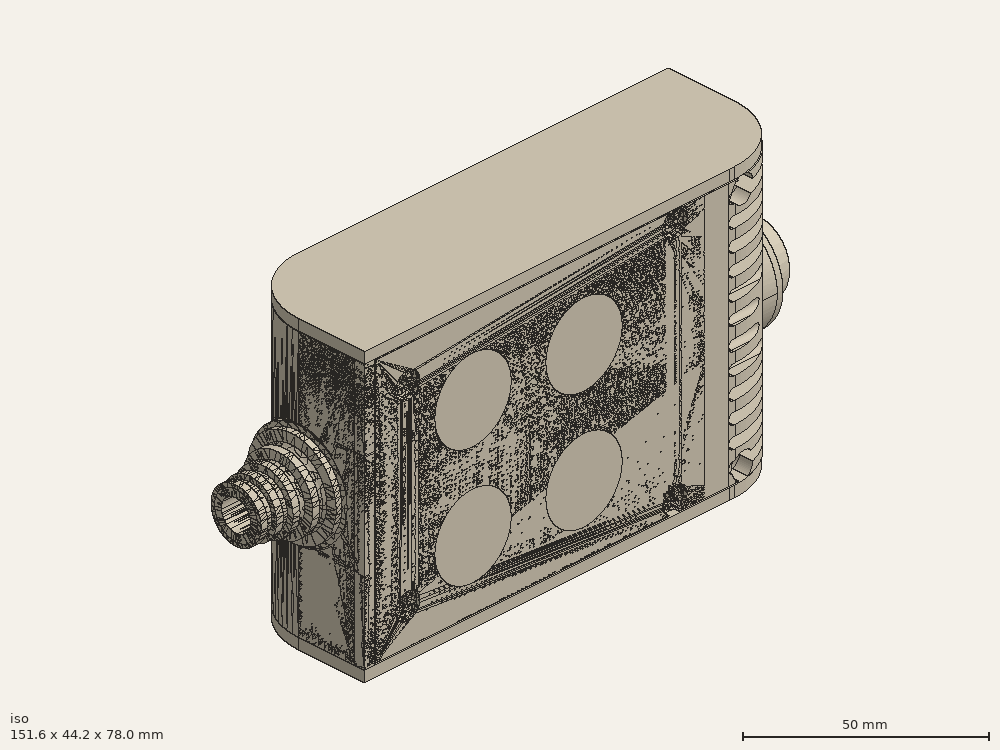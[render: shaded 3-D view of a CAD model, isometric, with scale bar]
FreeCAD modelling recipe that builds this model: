
FCSTD DOCUMENT  (FreeCAD 0.19R0.19.2)
Label: enclosure_204FCStd
License: All rights reserved
LicenseURL: http://en.wikipedia.org/wiki/All_rights_reserved
objects: Part::Revolution×152, Part::MultiFuse×146, Part::Feature×146, Sketcher::SketchObject×83, Part::Cut×70, Part::Cylinder×70, Part::Extrusion×68, Part::Fillet×58, Part::Box×36, App::MeasureDistance×4, Image::ImagePlane×1, PartDesign::Body×1, Part::FeaturePython×1
note: 831 computed .brp shape members not serialized (recipe doc carries the construction recipe); baked Part::Feature solids carry a one-line shape summary decoded from their .brp

FEATURE [Sketcher::SketchObject] Sketch  label="topSketch"
  FullyConstrained = true
  sketch-geometry (20):
    g0: LineSegment StartX=5.21097e-06 StartY=3 StartZ=0 EndX=5.21097e-06 EndY=19 EndZ=0
    g1: ArcOfCircle CenterX=19 CenterY=19 CenterZ=0 NormalX=0 NormalY=0 NormalZ=1 AngleXU=0 Radius=19 StartAngle=1.5708 EndAngle=3.14159
    g2: ArcOfCircle CenterX=19 CenterY=19 CenterZ=0 NormalX=0 NormalY=0 NormalZ=1 AngleXU=0 Radius=16 StartAngle=1.5708 EndAngle=3.14159
    g3: LineSegment StartX=114 StartY=35 StartZ=0 EndX=19 EndY=35 EndZ=0
    g4: LineSegment StartX=5.21097e-06 StartY=3 StartZ=0 EndX=5.21097e-06 EndY=0 EndZ=0
    g5: LineSegment StartX=3 StartY=0 StartZ=0 EndX=5.21097e-06 EndY=0 EndZ=0
    g6: LineSegment StartX=3 StartY=19 StartZ=0 EndX=3 EndY=0 EndZ=0
    g7: LineSegment StartX=19 StartY=38 StartZ=0 EndX=124 EndY=38 EndZ=0
    g8: Circle CenterX=119 CenterY=35 CenterZ=0 NormalX=0 NormalY=0 NormalZ=1 AngleXU=0 Radius=1
    g9: Circle CenterX=121 CenterY=35 CenterZ=0 NormalX=0 NormalY=0 NormalZ=1 AngleXU=0 Radius=1
    g10: Circle CenterX=121 CenterY=33 CenterZ=0 NormalX=0 NormalY=0 NormalZ=1 AngleXU=0 Radius=1
    g11: BSplineCurve PolesCount=3 KnotsCount=2 Degree=2 IsPeriodic=0
    g12: GeomPoint X=119 Y=35 Z=0
    g13: GeomPoint X=121 Y=33 Z=0
    g14: LineSegment StartX=119 StartY=35 StartZ=0 EndX=114 EndY=35 EndZ=0
    g15: ArcOfCircle CenterX=105 CenterY=19 CenterZ=0 NormalX=0 NormalY=0 NormalZ=1 AngleXU=0 Radius=19 StartAngle=5.7297 EndAngle=6.28319
    g16: ArcOfCircle CenterX=105 CenterY=19 CenterZ=0 NormalX=0 NormalY=0 NormalZ=1 AngleXU=0 Radius=16 StartAngle=5.60905 EndAngle=6.28319
    g17: LineSegment StartX=121 StartY=33 StartZ=0 EndX=121 EndY=19 EndZ=0
    g18: LineSegment StartX=124 StartY=38 StartZ=0 EndX=124 EndY=19 EndZ=0
    g19: LineSegment StartX=117.5 StartY=9.01251 StartZ=0 EndX=121.163 EndY=9.0125 EndZ=0
  constraints (46):
    c: Vertical(g0)
    c: Block(g0)
    c: Coincident(g1,g0)
    c: Block(g1)
    c: Coincident(g2,g1)
    c: Block(g2)
    c: Coincident(g3,g2)
    c: Horizontal(g3)
    c: Tangent(g3,g2)
    c: Coincident(g4,g0)
    c: Distance(g4) = 3
    c: Vertical(g4)
    c: Coincident(g5,g4)
    c: Horizontal(g5)
    c: Coincident(g6,g2)
    c: Coincident(g6,g5)
    c: Vertical(g6)
    c: Horizontal(g7)
    c: Distance(g7) = 105
    c: Coincident(g7,g1)
    c: Block(g3)
    c: Weight(g8) = 1
    c: Equal(g8,g9)
    c: Equal(g8,g10)
    c: InternalAlignment(g8,g11)
    c: InternalAlignment(g9,g11)
    c: InternalAlignment(g10,g11)
    c: InternalAlignment(g12,g11)
    c: InternalAlignment(g13,g11)
    c: Block(g11)
    c: Coincident(g14,g11)
    c: Coincident(g14,g3)
    c: Horizontal(g14)
    c: Block(g15)
    c: Coincident(g16,g15)
    c: Block(g16)
    c: Coincident(g17,g11)
    c: Coincident(g17,g16)
    c: Vertical(g17)
    c: Distance(g17) = 14
    c: Coincident(g18,g7)
    c: Coincident(g18,g15)
    c: Vertical(g18)
    c: Distance(g18) = 19
    c: Coincident(g19,g16)
    c: Coincident(g19,g15)
FEATURE [Sketcher::SketchObject] Sketch001  label="bottomSketch"
  FullyConstrained = true
  sketch-geometry (32):
    g0: LineSegment StartX=3.3 StartY=-6.03275e-07 StartZ=0 EndX=98 EndY=-6.03275e-07 EndZ=0
    g1: ArcOfCircle CenterX=98 CenterY=19 CenterZ=0 NormalX=0 NormalY=0 NormalZ=1 AngleXU=0 Radius=19 StartAngle=4.71239 EndAngle=5.71103
    g2: LineSegment StartX=6.3 StartY=8 StartZ=0 EndX=3.3 EndY=8 EndZ=0
    g3: LineSegment StartX=3.3 StartY=8 StartZ=0 EndX=3.3 EndY=-6.03275e-07 EndZ=0
    g4: ArcOfCircle CenterX=8.3 CenterY=5 CenterZ=0 NormalX=0 NormalY=0 NormalZ=1 AngleXU=0 Radius=2 StartAngle=3.14159 EndAngle=4.71239
    g5: LineSegment StartX=6.3 StartY=8 StartZ=0 EndX=6.3 EndY=5 EndZ=0
    g6: ArcOfCircle CenterX=98 CenterY=19 CenterZ=0 NormalX=0 NormalY=0 NormalZ=1 AngleXU=0 Radius=12.7 StartAngle=4.71239 EndAngle=6.28319
    g7: LineSegment StartX=94.7 StartY=3 StartZ=0 EndX=8.3 EndY=3 EndZ=0
    g8-g12: Circle x5 (B-spline internal-alignment scaffolding for g13; pole/knot coordinates omitted)
    g13: BSplineCurve PolesCount=5 KnotsCount=3 Degree=3 IsPeriodic=0
    g14: GeomPoint X=98 Y=6.3 Z=0
    g15: GeomPoint X=96.3938 Y=4.71946 Z=0
    g16: GeomPoint X=94.7 Y=3 Z=0
    g17-g23: Circle x7 (B-spline internal-alignment scaffolding for g24; pole/knot coordinates omitted)
    g24: BSplineCurve PolesCount=7 KnotsCount=5 Degree=3 IsPeriodic=0
    g25-g29: GeomPoint x5 (B-spline internal-alignment scaffolding for g24; pole/knot coordinates omitted)
    g30: ArcOfCircle CenterX=98 CenterY=19 CenterZ=0 NormalX=0 NormalY=0 NormalZ=1 AngleXU=0 Radius=15.7 StartAngle=5.81226 EndAngle=6.28319
    g31: LineSegment StartX=110.7 StartY=19 StartZ=0 EndX=113.7 EndY=19 EndZ=0
  constraints (41):
    c: Horizontal(g0)
    c: Coincident(g1,g0)
    c: Block(g1)
    c: Horizontal(g2)
    c: Distance(g2) = 3
    c: Coincident(g3,g2)
    c: Vertical(g3)
    c: Coincident(g3,g0)
    c: Block(g4)
    c: Block(g2)
    c: Coincident(g5,g2)
    c: Coincident(g5,g4)
    c: Vertical(g5)
    c: Coincident(g6,g1)
    c: Block(g6)
    c: Coincident(g7,g4)
    c: Horizontal(g7)
    c: Block(g0)
    c: Block(g7)
    c: Block(g3)
    c: Coincident(g13,g6)
    c: Weight(g8) = 1
    c: Equal(g8, g9-g12) x4
    c: Coincident(g13,g7)
    c: InternalAlignment(g8-g12 -> g13) x5
    c: InternalAlignment(g14,g13)
    c: InternalAlignment(g15,g13)
    c: InternalAlignment(g16,g13)
    c: Block(g13)
    c: Weight(g17) = 1
    c: Equal(g17, g18-g23) x6
    c: Coincident(g24,g1)
    c: InternalAlignment(g17-g23 -> g24) x7
    c: InternalAlignment(g25-g29 -> g24) x5
    c: Block(g24)
    c: Coincident(g30,g24)
    c: Coincident(g31,g6)
    c: Coincident(g31,g30)
    c: Horizontal(g31)
    c: Block(g31)
    c: Block(g30)
FEATURE [Part::Extrusion] Extrude  label="top"
  Base = -> Sketch
  Dir = (0,0,1)
  DirMode = 2
  FaceMakerClass = Part::FaceMakerBullseye
  LengthFwd = 72
  LengthRev = 0
  Solid = true
  Symmetric = false
FEATURE [Part::Extrusion] Extrude001  label="bottom"
  Base = -> Sketch001
  Dir = (0,0,1)
  DirMode = 2
  FaceMakerClass = Part::FaceMakerBullseye
  LengthFwd = 71.4
  LengthRev = 0
  Placement = pos=(0,0,0.3) rot=(0,0,1;0rad)
  Solid = true
  Symmetric = false
FEATURE [Sketcher::SketchObject] Sketch002  label="topSketch001"
  FullyConstrained = true
  sketch-geometry (8):
    g0: ArcOfCircle CenterX=19 CenterY=19.0975 CenterZ=0 NormalX=0 NormalY=0 NormalZ=1 AngleXU=0 Radius=18.9025 StartAngle=1.5708 EndAngle=3.14674
    g1: LineSegment StartX=0.0977805 StartY=19.0003 StartZ=0 EndX=0.0977805 EndY=0.000251602 EndZ=0
    g2: LineSegment StartX=19 StartY=38 StartZ=0 EndX=124 EndY=38 EndZ=0
    g3: LineSegment StartX=0.0977805 StartY=0.000251602 StartZ=0 EndX=105.098 EndY=0.000251602 EndZ=0
    g4: LineSegment StartX=124 StartY=38 StartZ=0 EndX=125.616 EndY=38 EndZ=0
    g5: LineSegment StartX=105.098 StartY=0.000251602 StartZ=0 EndX=106.713 EndY=0.000251602 EndZ=0
    g6: ArcOfCircle CenterX=106.616 CenterY=19 CenterZ=0 NormalX=0 NormalY=0 NormalZ=1 AngleXU=0 Radius=19 StartAngle=4.71754 EndAngle=6.28319
    g7: LineSegment StartX=125.616 StartY=38 StartZ=0 EndX=125.616 EndY=19 EndZ=0
  constraints (21):
    c: Block(g0)
    c: Coincident(g1,g0)
    c: Vertical(g1)
    c: Horizontal(g2)
    c: Distance(g2) = 105
    c: Coincident(g2,g0)
    c: Distance(g1) = 19
    c: Coincident(g3,g1)
    c: Horizontal(g3)
    c: Distance(g3) = 105
    c: Coincident(g4,g2)
    c: Horizontal(g4)
    c: Distance(g4) = 1.61553
    c: Horizontal(g5)
    c: Equal(g4,g5) = 1.61553
    c: Coincident(g5,g3)
    c: Block(g6)
    c: Coincident(g6,g5)
    c: Coincident(g7,g4)
    c: Coincident(g7,g6)
    c: Vertical(g7)
FEATURE [Part::Extrusion] Extrude002  label="sideA"
  Base = -> Sketch002
  Dir = (0,0,1)
  DirMode = 2
  FaceMakerClass = Part::FaceMakerBullseye
  LengthFwd = 3
  LengthRev = 0
  Placement = pos=(0,0,-3) rot=(0,0,1;0rad)
  Solid = true
  Symmetric = false
FEATURE [Sketcher::SketchObject] Sketch003  label="topSketch002"
  FullyConstrained = true
  sketch-geometry (6):
    g0: LineSegment StartX=19 StartY=38 StartZ=0 EndX=117 EndY=38 EndZ=0
    g1: ArcOfCircle CenterX=19 CenterY=19 CenterZ=0 NormalX=0 NormalY=0 NormalZ=1 AngleXU=0 Radius=19 StartAngle=1.5708 EndAngle=3.14159
    g2: LineSegment StartX=117 StartY=38 StartZ=0 EndX=117 EndY=19 EndZ=0
    g3: LineSegment StartX=98 StartY=1.0161e-12 StartZ=0 EndX=5.22862e-06 EndY=1.0161e-12 EndZ=0
    g4: LineSegment StartX=5.22862e-06 StartY=19 StartZ=0 EndX=5.22862e-06 EndY=1.0161e-12 EndZ=0
    g5: ArcOfCircle CenterX=98 CenterY=19 CenterZ=0 NormalX=0 NormalY=0 NormalZ=1 AngleXU=0 Radius=19 StartAngle=4.71239 EndAngle=6.28319
  constraints (16):
    c: Horizontal(g0)
    c: Distance(g0) = 98
    c: Coincident(g1,g0)
    c: Block(g1)
    c: Coincident(g2,g0)
    c: Vertical(g2)
    c: Distance(g2) = 19
    c: Horizontal(g3)
    c: Coincident(g4,g1)
    c: Vertical(g4)
    c: Coincident(g3,g4)
    c: Block(g3)
    c: Coincident(g5,g2)
    c: Coincident(g5,g3)
    c: Block(g0)
    c: Block(g5)
FEATURE [Sketcher::SketchObject] Sketch004
  FullyConstrained = true
  MapMode = 3
  Placement = pos=(0,0,0) rot=(1,0,0;1.5708rad)
  Support = -> [Extrude]
  sketch-geometry (8):
    g0: Circle CenterX=80.351 CenterY=-67.6202 CenterZ=0 NormalX=0 NormalY=0 NormalZ=1 AngleXU=0 Radius=2
    g1: Circle CenterX=80.351 CenterY=-67.6202 CenterZ=0 NormalX=0 NormalY=0 NormalZ=1 AngleXU=0 Radius=3
    g2: Circle CenterX=80.351 CenterY=-4.92017 CenterZ=0 NormalX=0 NormalY=0 NormalZ=1 AngleXU=0 Radius=2
    g3: Circle CenterX=80.351 CenterY=-4.92017 CenterZ=0 NormalX=0 NormalY=0 NormalZ=1 AngleXU=0 Radius=3
    g4: Circle CenterX=23.851 CenterY=-4.92017 CenterZ=0 NormalX=0 NormalY=0 NormalZ=1 AngleXU=0 Radius=2
    g5: Circle CenterX=23.851 CenterY=-4.92017 CenterZ=0 NormalX=0 NormalY=0 NormalZ=1 AngleXU=0 Radius=3
    g6: Circle CenterX=23.851 CenterY=-67.6202 CenterZ=0 NormalX=0 NormalY=0 NormalZ=1 AngleXU=0 Radius=2
    g7: Circle CenterX=23.851 CenterY=-67.6202 CenterZ=0 NormalX=0 NormalY=0 NormalZ=1 AngleXU=0 Radius=3
  constraints (8):
    c: Block(g3)
    c: Block(g2)
    c: Block(g1)
    c: Block(g0)
    c: Block(g6)
    c: Block(g7)
    c: Block(g4)
    c: Block(g5)
FEATURE [Part::Extrusion] Extrude004
  Base = -> Sketch004
  Dir = (0,-1,2e-16)
  DirMode = 2
  FaceMakerClass = Part::FaceMakerBullseye
  LengthFwd = 6
  LengthRev = 0
  Placement = pos=(0,9,0) rot=(0,0,1;0rad)
  Solid = true
  Symmetric = false
FEATURE [Sketcher::SketchObject] Sketch005
  FullyConstrained = true
  MapMode = 3
  Placement = pos=(0,0,0) rot=(1,0,0;1.5708rad)
  Support = -> [Extrude]
  sketch-geometry (8):
    g0: Circle CenterX=80.351 CenterY=-67.6202 CenterZ=0 NormalX=0 NormalY=0 NormalZ=1 AngleXU=0 Radius=3
    g1: Circle CenterX=80.351 CenterY=-4.92017 CenterZ=0 NormalX=0 NormalY=0 NormalZ=1 AngleXU=0 Radius=3
    g2: Circle CenterX=23.851 CenterY=-4.92017 CenterZ=0 NormalX=0 NormalY=0 NormalZ=1 AngleXU=0 Radius=3
    g3: Circle CenterX=23.851 CenterY=-67.6202 CenterZ=0 NormalX=0 NormalY=0 NormalZ=1 AngleXU=0 Radius=3
    g4: Circle CenterX=23.851 CenterY=-67.6202 CenterZ=0 NormalX=0 NormalY=0 NormalZ=1 AngleXU=0 Radius=5
    g5: Circle CenterX=80.351 CenterY=-67.6202 CenterZ=0 NormalX=0 NormalY=0 NormalZ=1 AngleXU=0 Radius=5
    g6: Circle CenterX=23.851 CenterY=-4.92017 CenterZ=0 NormalX=0 NormalY=0 NormalZ=1 AngleXU=0 Radius=5
    g7: Circle CenterX=80.351 CenterY=-4.92017 CenterZ=0 NormalX=0 NormalY=0 NormalZ=1 AngleXU=0 Radius=5
  constraints (8):
    c: Block(g1)
    c: Block(g0)
    c: Block(g3)
    c: Block(g2)
    c: Block(g5)
    c: Block(g4)
    c: Block(g6)
    c: Block(g7)
FEATURE [Part::Extrusion] Extrude005
  Base = -> Sketch005
  Dir = (0,-1,2e-16)
  DirMode = 2
  FaceMakerClass = Part::FaceMakerBullseye
  LengthFwd = 2
  LengthRev = 0
  Solid = true
  Symmetric = false
FEATURE [Sketcher::SketchObject] Sketch006
  FullyConstrained = true
  MapMode = 3
  Placement = pos=(0,0,0) rot=(1,0,0;1.5708rad)
  sketch-geometry (8):
    g0: Circle CenterX=80.351 CenterY=-67.6202 CenterZ=0 NormalX=0 NormalY=0 NormalZ=1 AngleXU=0 Radius=3
    g1: Circle CenterX=80.351 CenterY=-4.92017 CenterZ=0 NormalX=0 NormalY=0 NormalZ=1 AngleXU=0 Radius=3
    g2: Circle CenterX=23.851 CenterY=-4.92017 CenterZ=0 NormalX=0 NormalY=0 NormalZ=1 AngleXU=0 Radius=3
    g3: Circle CenterX=23.851 CenterY=-67.6202 CenterZ=0 NormalX=0 NormalY=0 NormalZ=1 AngleXU=0 Radius=3
    g4: Circle CenterX=23.851 CenterY=-67.6202 CenterZ=0 NormalX=0 NormalY=0 NormalZ=1 AngleXU=0 Radius=5
    g5: Circle CenterX=80.351 CenterY=-67.6202 CenterZ=0 NormalX=0 NormalY=0 NormalZ=1 AngleXU=0 Radius=5
    g6: Circle CenterX=23.851 CenterY=-4.92017 CenterZ=0 NormalX=0 NormalY=0 NormalZ=1 AngleXU=0 Radius=5
    g7: Circle CenterX=80.351 CenterY=-4.92017 CenterZ=0 NormalX=0 NormalY=0 NormalZ=1 AngleXU=0 Radius=5
  constraints (8):
    c: Block(g1)
    c: Block(g0)
    c: Block(g3)
    c: Block(g2)
    c: Block(g5)
    c: Block(g4)
    c: Block(g6)
    c: Block(g7)
FEATURE [Part::Extrusion] Extrude007
  Base = -> Sketch006
  Dir = (0,-1,2e-16)
  DirMode = 2
  FaceMakerClass = Part::FaceMakerBullseye
  LengthFwd = 2
  LengthRev = 0
  Solid = true
  Symmetric = false
FEATURE [Part::Fillet] Fillet
  Base = -> Extrude007
  Edges = 4 edges r=1.99: [Edge6,Edge12,Edge18,Edge24]
FEATURE [Part::Cut] Cut
  Base = -> Extrude005
  Placement = pos=(0,5,0) rot=(0,0,1;0rad)
  Tool = -> Fillet
FEATURE [Part::MultiFuse] Fusion  label="pCBScrews"
  Placement = pos=(-2.5,0,72.3) rot=(0,0,1;0rad)
  Shapes = -> [Extrude004,Cut]
FEATURE [App::MeasureDistance] Distance  label="Distance: 0.69 mm"
  Distance = 0.685967
  P1 = (24.0138,2.9647,0.3)
  P2 = (23.8901,3,-0.373787)
FEATURE [App::MeasureDistance] Distance001  label="Distance: 0.53 mm"
  Distance = 0.533607
  P1 = (80.2939,3,72.2334)
  P2 = (80.281,2.99661,71.7)
FEATURE [Part::Fillet] Fillet001
  Base = -> Extrude001
  Edges = 1 edges r=2.4: [Edge17]
FEATURE [Part::Fillet] Fillet002  label="bottom001"
  Base = -> Fillet001
  Edges = 1 edges r=2.4: [Edge36]
FEATURE [Part::Fillet] Fillet003  label="top001"
  Base = -> Extrude
  Edges = 1 edges r=2: [Edge1]
FEATURE [Sketcher::SketchObject] Sketch007
  FullyConstrained = true
  sketch-geometry (16):
    g0: LineSegment StartX=4 StartY=0 StartZ=0 EndX=4 EndY=2.4 EndZ=0
    g1: LineSegment StartX=4 StartY=2.4 StartZ=0 EndX=7 EndY=2.4 EndZ=0
    g2: LineSegment StartX=4 StartY=0 StartZ=0 EndX=5.7 EndY=0 EndZ=0
    g3: LineSegment StartX=5.7 StartY=0 StartZ=0 EndX=5.7 EndY=-5.6 EndZ=0
    g4-g8: Circle x5 (B-spline internal-alignment scaffolding for g9; pole/knot coordinates omitted)
    g9: BSplineCurve PolesCount=5 KnotsCount=3 Degree=3 IsPeriodic=0
    g10: GeomPoint X=7 Y=2.4 Z=0
    g11: GeomPoint X=10.4582 Y=-1.55472 Z=0
    g12: GeomPoint X=14 Y=-5.6 Z=0
    g13: LineSegment StartX=14 StartY=-5.6 StartZ=0 EndX=14 EndY=-14.1 EndZ=0
    g14: LineSegment StartX=14 StartY=-14.1 StartZ=0 EndX=6.5 EndY=-14.1 EndZ=0
    g15: LineSegment StartX=5.7 StartY=-5.6 StartZ=0 EndX=6.5 EndY=-14.1 EndZ=0
  constraints (28):
    c: Distance(g0) = 2.4
    c: Vertical(g0)
    c: Block(g0)
    c: Coincident(g1,g0)
    c: Horizontal(g1)
    c: Distance(g1) = 3
    c: Coincident(g2,g0)
    c: Horizontal(g2)
    c: Distance(g2) = 1.7
    c: Coincident(g3,g2)
    c: Vertical(g3)
    c: Distance(g3) = 5.6
    c: Coincident(g9,g1)
    c: Weight(g4) = 1
    c: Equal(g4, g5-g8) x4
    c: InternalAlignment(g4-g8 -> g9) x5
    c: InternalAlignment(g10,g9)
    c: InternalAlignment(g11,g9)
    c: InternalAlignment(g12,g9)
    c: Block(g9)
    c: Coincident(g13,g9)
    c: Vertical(g13)
    c: Distance(g13) = 8.5
    c: Coincident(g14,g13)
    c: Horizontal(g14)
    c: Distance(g14) = 7.5
    c: Coincident(g15,g3)
    c: Coincident(g15,g14)
FEATURE [Part::Feature] Face
  shape: bbox 10 x 16.5 x 2e-07 mm, 1 faces, 0 solids (baked)
FEATURE [Part::Revolution] Revolve  label="plugHousing"
  Angle = 360
  Axis = (0,1,0)
  Base = (0,0,0)
  FaceMakerClass = Part::FaceMakerBullseye
  Placement = pos=(0,0,36.15) rot=(0,0,1;0rad)
  Solid = false
  Source = -> Face
  Symmetric = false
FEATURE [Part::Feature] Face001
  shape: bbox 10 x 16.5 x 2e-07 mm, 1 faces, 0 solids (baked)
FEATURE [Part::Revolution] Revolve001  label="plugHousing001"
  Angle = 360
  Axis = (0,1,0)
  Base = (0,0,0)
  FaceMakerClass = Part::FaceMakerBullseye
  Placement = pos=(0,0,36.15) rot=(0,0,1;0rad)
  Solid = false
  Source = -> Face001
  Symmetric = false
FEATURE [Part::MultiFuse] Fusion001  label="plugHousing002"
  Placement = pos=(0,0,0) rot=(0,0,1;1.5708rad)
  Shapes = -> [Revolve001,Revolve]
FEATURE [Part::Feature] Face002
  shape: bbox 10 x 16.5 x 2e-07 mm, 1 faces, 0 solids (baked)
FEATURE [Part::Revolution] Revolve003  label="plugHousing005"
  Angle = 360
  Axis = (0,1,0)
  Base = (0,0,0)
  FaceMakerClass = Part::FaceMakerBullseye
  Placement = pos=(0,0,36.15) rot=(0,0,1;0rad)
  Solid = false
  Source = -> Face002
  Symmetric = false
FEATURE [Part::Feature] Face003
  shape: bbox 10 x 16.5 x 2e-07 mm, 1 faces, 0 solids (baked)
FEATURE [Part::Revolution] Revolve002  label="plugHousing003"
  Angle = 360
  Axis = (0,1,0)
  Base = (0,0,0)
  FaceMakerClass = Part::FaceMakerBullseye
  Placement = pos=(0,0,36.15) rot=(0,0,1;0rad)
  Solid = false
  Source = -> Face003
  Symmetric = false
FEATURE [Part::MultiFuse] Fusion002  label="plugHousing004"
  Placement = pos=(0,0,0) rot=(0,0,1;1.5708rad)
  Shapes = -> [Revolve002,Revolve003]
FEATURE [Part::MultiFuse] Fusion003  label="plugHousing006"
  Placement = pos=(0,19,0) rot=(0,0,1;3.14159rad)
  Shapes = -> [Fusion002,Fusion001]
FEATURE [Part::Feature] Face004
  shape: bbox 10 x 16.5 x 2e-07 mm, 1 faces, 0 solids (baked)
FEATURE [Part::Revolution] Revolve006  label="plugHousing010"
  Angle = 360
  Axis = (0,1,0)
  Base = (0,0,0)
  FaceMakerClass = Part::FaceMakerBullseye
  Placement = pos=(0,0,36.15) rot=(0,0,1;0rad)
  Solid = false
  Source = -> Face004
  Symmetric = false
FEATURE [Part::Feature] Face005
  shape: bbox 10 x 16.5 x 2e-07 mm, 1 faces, 0 solids (baked)
FEATURE [Part::Revolution] Revolve007  label="plugHousing011"
  Angle = 360
  Axis = (0,1,0)
  Base = (0,0,0)
  FaceMakerClass = Part::FaceMakerBullseye
  Placement = pos=(0,0,36.15) rot=(0,0,1;0rad)
  Solid = false
  Source = -> Face005
  Symmetric = false
FEATURE [Part::Feature] Face006
  shape: bbox 10 x 16.5 x 2e-07 mm, 1 faces, 0 solids (baked)
FEATURE [Part::Revolution] Revolve004  label="plugHousing007"
  Angle = 360
  Axis = (0,1,0)
  Base = (0,0,0)
  FaceMakerClass = Part::FaceMakerBullseye
  Placement = pos=(0,0,36.15) rot=(0,0,1;0rad)
  Solid = false
  Source = -> Face006
  Symmetric = false
FEATURE [Part::MultiFuse] Fusion004  label="plugHousing009"
  Placement = pos=(0,0,0) rot=(0,0,1;1.5708rad)
  Shapes = -> [Revolve004,Revolve007]
FEATURE [Part::Feature] Face007
  shape: bbox 10 x 16.5 x 2e-07 mm, 1 faces, 0 solids (baked)
FEATURE [Part::Revolution] Revolve005  label="plugHousing008"
  Angle = 360
  Axis = (0,1,0)
  Base = (0,0,0)
  FaceMakerClass = Part::FaceMakerBullseye
  Placement = pos=(0,0,36.15) rot=(0,0,1;0rad)
  Solid = false
  Source = -> Face007
  Symmetric = false
FEATURE [Part::MultiFuse] Fusion005  label="plugHousing012"
  Placement = pos=(0,0,0) rot=(0,0,1;1.5708rad)
  Shapes = -> [Revolve006,Revolve005]
FEATURE [Part::MultiFuse] Fusion006  label="plugHousing013"
  Placement = pos=(0,19,0) rot=(0,0,1;3.14159rad)
  Shapes = -> [Fusion005,Fusion004]
FEATURE [Part::MultiFuse] Fusion007  label="plugHousing014"
  Placement = pos=(122.621,0,-0.15) rot=(0,0,1;0rad)
  Shapes = -> [Fusion003,Fusion006]
FEATURE [Part::Cylinder] Cylinder002
  Angle = 360
  AttacherType = Attacher::AttachEngine3D
  Height = 20
  Placement = pos=(0,0,36.15) rot=(0,0,1;0rad)
  Radius = 4
FEATURE [Part::Cylinder] Cylinder003
  Angle = 360
  AttacherType = Attacher::AttachEngine3D
  Height = 10
  Placement = pos=(0,0,36.15) rot=(0,0,1;0rad)
  Radius = 4
FEATURE [Part::MultiFuse] Fusion009  label="removeToCreateHoleForPlugHousing"
  Placement = pos=(70,19,36.15) rot=(0,1,0;1.5708rad)
  Shapes = -> [Cylinder002,Cylinder003]
FEATURE [Part::Cylinder] Cylinder004
  Angle = 360
  AttacherType = Attacher::AttachEngine3D
  Height = 20
  Placement = pos=(0,0,36.15) rot=(0,0,1;0rad)
  Radius = 4
FEATURE [Part::Cylinder] Cylinder005
  Angle = 360
  AttacherType = Attacher::AttachEngine3D
  Height = 10
  Placement = pos=(0,0,36.15) rot=(0,0,1;0rad)
  Radius = 4
FEATURE [Part::MultiFuse] Fusion010  label="removeToCreateHoleForPlugHousing001"
  Placement = pos=(70,19,36.15) rot=(0,1,0;1.5708rad)
  Shapes = -> [Cylinder004,Cylinder005]
FEATURE [Part::Cut] Cut001
  Base = -> Fillet003
  Tool = -> Fusion010
FEATURE [Part::Cut] Cut002  label="Bottom"
  Base = -> Fillet002
  Tool = -> Fusion009
FEATURE [Part::Feature] Face008
  shape: bbox 10 x 16.5 x 2e-07 mm, 1 faces, 0 solids (baked)
FEATURE [Part::Revolution] Revolve011  label="plugHousing021"
  Angle = 360
  Axis = (0,1,0)
  Base = (0,0,0)
  FaceMakerClass = Part::FaceMakerBullseye
  Placement = pos=(0,0,36.15) rot=(0,0,1;0rad)
  Solid = false
  Source = -> Face008
  Symmetric = false
FEATURE [Part::Feature] Face009
  shape: bbox 10 x 16.5 x 2e-07 mm, 1 faces, 0 solids (baked)
FEATURE [Part::Revolution] Revolve012  label="plugHousing022"
  Angle = 360
  Axis = (0,1,0)
  Base = (0,0,0)
  FaceMakerClass = Part::FaceMakerBullseye
  Placement = pos=(0,0,36.15) rot=(0,0,1;0rad)
  Solid = false
  Source = -> Face009
  Symmetric = false
FEATURE [Part::Feature] Face010 .. Face013  x4 (patterned run collapsed; names and placements below)
  shape: bbox 10 x 16.5 x 2e-07 mm, 1 faces, 0 solids (baked)
FEATURE [Part::Revolution] Revolve015  label="plugHousing027"
  Angle = 360
  Axis = (0,1,0)
  Base = (0,0,0)
  FaceMakerClass = Part::FaceMakerBullseye
  Placement = pos=(0,0,36.15) rot=(0,0,1;0rad)
  Solid = false
  Source = -> Face013
  Symmetric = false
FEATURE [Part::Feature] Face014
  shape: bbox 10 x 16.5 x 2e-07 mm, 1 faces, 0 solids (baked)
FEATURE [Part::Feature] Face015
  shape: bbox 10 x 16.5 x 2e-07 mm, 1 faces, 0 solids (baked)
FEATURE [Part::Feature] Face016
  shape: bbox 10 x 16.5 x 2e-07 mm, 1 faces, 0 solids (baked)
FEATURE [Part::Revolution] Revolve019  label="plugHousing033"
  Angle = 360
  Axis = (0,1,0)
  Base = (0,0,0)
  FaceMakerClass = Part::FaceMakerBullseye
  Placement = pos=(0,0,36.15) rot=(0,0,1;0rad)
  Solid = false
  Source = -> Face016
  Symmetric = false
FEATURE [Part::Feature] Face017
  shape: bbox 10 x 16.5 x 2e-07 mm, 1 faces, 0 solids (baked)
FEATURE [Part::Revolution] Revolve020  label="plugHousing034"
  Angle = 360
  Axis = (0,1,0)
  Base = (0,0,0)
  FaceMakerClass = Part::FaceMakerBullseye
  Placement = pos=(0,0,36.15) rot=(0,0,1;0rad)
  Solid = false
  Source = -> Face017
  Symmetric = false
FEATURE [Part::Feature] Face018
  shape: bbox 10 x 16.5 x 2e-07 mm, 1 faces, 0 solids (baked)
FEATURE [Part::Revolution] Revolve016  label="plugHousing030"
  Angle = 360
  Axis = (0,1,0)
  Base = (0,0,0)
  FaceMakerClass = Part::FaceMakerBullseye
  Placement = pos=(0,0,36.15) rot=(0,0,1;0rad)
  Solid = false
  Source = -> Face018
  Symmetric = false
FEATURE [Part::MultiFuse] Fusion020  label="plugHousing038"
  Placement = pos=(0,0,0) rot=(0,0,1;1.5708rad)
  Shapes = -> [Revolve016,Revolve020]
FEATURE [Part::Feature] Face019
  shape: bbox 10 x 16.5 x 2e-07 mm, 1 faces, 0 solids (baked)
FEATURE [Part::Feature] Face020
  shape: bbox 10 x 16.5 x 2e-07 mm, 1 faces, 0 solids (baked)
FEATURE [Part::Revolution] Revolve017  label="plugHousing031"
  Angle = 360
  Axis = (0,1,0)
  Base = (0,0,0)
  FaceMakerClass = Part::FaceMakerBullseye
  Placement = pos=(0,0,36.15) rot=(0,0,1;0rad)
  Solid = false
  Source = -> Face020
  Symmetric = false
FEATURE [Part::MultiFuse] Fusion021  label="plugHousing039"
  Placement = pos=(0,0,0) rot=(0,0,1;1.5708rad)
  Shapes = -> [Revolve019,Revolve017]
FEATURE [Part::MultiFuse] Fusion023  label="plugHousing041"
  Placement = pos=(0,19,0) rot=(0,0,1;3.14159rad)
  Shapes = -> [Fusion021,Fusion020]
FEATURE [Part::Revolution] Revolve022  label="plugHousing043"
  Angle = 360
  Axis = (0,1,0)
  Base = (0,0,0)
  FaceMakerClass = Part::FaceMakerBullseye
  Placement = pos=(0,0,36.15) rot=(0,0,1;0rad)
  Solid = false
  Source = -> Face019
  Symmetric = false
FEATURE [Part::Feature] Face021
  shape: bbox 10 x 16.5 x 2e-07 mm, 1 faces, 0 solids (baked)
FEATURE [Part::Revolution] Revolve023  label="plugHousing044"
  Angle = 360
  Axis = (0,1,0)
  Base = (0,0,0)
  FaceMakerClass = Part::FaceMakerBullseye
  Placement = pos=(0,0,36.15) rot=(0,0,1;0rad)
  Solid = false
  Source = -> Face021
  Symmetric = false
FEATURE [Part::Feature] Face022
  shape: bbox 10 x 16.5 x 2e-07 mm, 1 faces, 0 solids (baked)
FEATURE [Part::Revolution] Revolve018  label="plugHousing032"
  Angle = 360
  Axis = (0,1,0)
  Base = (0,0,0)
  FaceMakerClass = Part::FaceMakerBullseye
  Placement = pos=(0,0,36.15) rot=(0,0,1;0rad)
  Solid = false
  Source = -> Face022
  Symmetric = false
FEATURE [Part::MultiFuse] Fusion022  label="plugHousing040"
  Placement = pos=(0,0,0) rot=(0,0,1;1.5708rad)
  Shapes = -> [Revolve018,Revolve023]
FEATURE [Part::Feature] Face023
  shape: bbox 10 x 16.5 x 2e-07 mm, 1 faces, 0 solids (baked)
FEATURE [Part::Revolution] Revolve021  label="plugHousing035"
  Angle = 360
  Axis = (0,1,0)
  Base = (0,0,0)
  FaceMakerClass = Part::FaceMakerBullseye
  Placement = pos=(0,0,36.15) rot=(0,0,1;0rad)
  Solid = false
  Source = -> Face023
  Symmetric = false
FEATURE [Part::MultiFuse] Fusion018  label="plugHousing036"
  Placement = pos=(0,0,0) rot=(0,0,1;1.5708rad)
  Shapes = -> [Revolve022,Revolve021]
FEATURE [Part::MultiFuse] Fusion019  label="plugHousing037"
  Placement = pos=(0,19,0) rot=(0,0,1;3.14159rad)
  Shapes = -> [Fusion018,Fusion022]
FEATURE [Part::MultiFuse] Fusion024  label="plugHousing042"
  Placement = pos=(122.621,0,-0.15) rot=(0,0,1;0rad)
  Shapes = -> [Fusion023,Fusion019]
FEATURE [Part::Cylinder] Cylinder006
  Angle = 360
  AttacherType = Attacher::AttachEngine3D
  Height = 20
  Placement = pos=(0,0,36.15) rot=(0,0,1;0rad)
  Radius = 14.3
FEATURE [Part::Cylinder] Cylinder007
  Angle = 360
  AttacherType = Attacher::AttachEngine3D
  Height = 10
  Placement = pos=(0,0,36.15) rot=(0,0,1;0rad)
  Radius = 4
FEATURE [Part::MultiFuse] Fusion026  label="removeToCreteHoleForPlugHousing"
  Placement = pos=(70,19,36) rot=(0,1,0;1.5708rad)
  Shapes = -> [Cylinder006,Cylinder007]
FEATURE [Part::Box] Box001  label="Cube001"
  AttacherType = Attacher::AttachEngine3D
  Height = 28
  Length = 3
  Placement = pos=(110.7,19,22) rot=(0,0,1;0rad)
  Width = 15.7
FEATURE [Part::Cut] Cut003  label="top002"
  Base = -> Cut001
  Tool = -> Fusion007
FEATURE [Part::Revolution] Revolve008  label="plugHousing015"
  Angle = 360
  Axis = (0,1,0)
  Base = (0,0,0)
  FaceMakerClass = Part::FaceMakerBullseye
  Placement = pos=(0,0,36.15) rot=(0,0,1;0rad)
  Solid = false
  Source = -> Face010
  Symmetric = false
FEATURE [Part::MultiFuse] Fusion013  label="plugHousing020"
  Placement = pos=(0,0,0) rot=(0,0,1;1.5708rad)
  Shapes = -> [Revolve008,Revolve012]
FEATURE [Part::Cut] Cut004  label="top003"
  Base = -> Cut003
  Placement = pos=(1,0,0) rot=(0,0,1;0rad)
  Tool = -> Fusion026
FEATURE [Part::Cylinder] Cylinder008
  Angle = 360
  AttacherType = Attacher::AttachEngine3D
  Height = 20
  Placement = pos=(0,0,36.15) rot=(0,0,1;0rad)
  Radius = 10.3
FEATURE [Part::Cylinder] Cylinder009
  Angle = 360
  AttacherType = Attacher::AttachEngine3D
  Height = 10
  Placement = pos=(0,0,36.15) rot=(0,0,1;0rad)
  Radius = 4
FEATURE [Part::MultiFuse] Fusion027  label="removeToCreteHoleForPlugHousing001"
  Placement = pos=(70,19,36) rot=(0,1,0;1.5708rad)
  Shapes = -> [Cylinder008,Cylinder009]
FEATURE [Part::Cut] Cut005  label="plugHousingTab"
  Base = -> Box001
  Tool = -> Fusion027
FEATURE [Part::MultiFuse] Fusion028  label="plugHousing045"
  Shapes = -> [Fusion024,Cut005]
FEATURE [Part::Box] Box002  label="Cube002"
  AttacherType = Attacher::AttachEngine3D
  Height = 28.8
  Length = 3
  Placement = pos=(107.3,28,21.6) rot=(0,0,1;0rad)
  Width = 7
FEATURE [Part::Box] Box003  label="Cube003"
  AttacherType = Attacher::AttachEngine3D
  Height = 3
  Length = 6.4
  Placement = pos=(107.3,28,18.6) rot=(0,0,1;0rad)
  Width = 7
FEATURE [Part::Box] Box004  label="Cube004"
  AttacherType = Attacher::AttachEngine3D
  Height = 3
  Length = 6.4
  Placement = pos=(107.3,28,50.4) rot=(0,0,1;0rad)
  Width = 7
FEATURE [Part::MultiFuse] Fusion029  label="plugHousingBracketHolder"
  Shapes = -> [Box004,Box002,Box003]
FEATURE [Part::Cylinder] Cylinder010
  Angle = 360
  AttacherType = Attacher::AttachEngine3D
  Height = 20
  Placement = pos=(0,0,36.15) rot=(0,0,1;0rad)
  Radius = 14.3
FEATURE [Part::Cylinder] Cylinder011
  Angle = 360
  AttacherType = Attacher::AttachEngine3D
  Height = 10
  Placement = pos=(0,0,36.15) rot=(0,0,1;0rad)
  Radius = 4
FEATURE [Part::MultiFuse] Fusion030  label="removeToCreteHoleForPlugHousing002"
  Placement = pos=(70,19,36) rot=(0,1,0;1.5708rad)
  Shapes = -> [Cylinder010,Cylinder011]
FEATURE [Part::Cut] Cut006  label="plugHousingBracketHolder001"
  Base = -> Fusion029
  Tool = -> Fusion030
FEATURE [Part::Cylinder] Cylinder012
  Angle = 360
  AttacherType = Attacher::AttachEngine3D
  Height = 20
  Placement = pos=(0,0,36.15) rot=(0,0,1;0rad)
  Radius = 7
FEATURE [Part::Cylinder] Cylinder013
  Angle = 360
  AttacherType = Attacher::AttachEngine3D
  Height = 10
  Placement = pos=(0,0,36.15) rot=(0,0,1;0rad)
  Radius = 4
FEATURE [Part::MultiFuse] Fusion032  label="removeToCreteHoleForPlugHousing003"
  Placement = pos=(70,19,36) rot=(0,1,0;1.5708rad)
  Shapes = -> [Cylinder012,Cylinder013]
FEATURE [Part::Cut] Cut007  label="bottom002"
  Base = -> Cut002
  Tool = -> Fusion032
FEATURE [Sketcher::SketchObject] Sketch008
  FullyConstrained = true
  sketch-geometry (54):
    g0: LineSegment StartX=-4.2 StartY=0 StartZ=0 EndX=-6.2 EndY=0 EndZ=0
    g1: LineSegment StartX=-14 StartY=-18 StartZ=0 EndX=-14 EndY=-26.5 EndZ=0
    g2: LineSegment StartX=-4.2 StartY=0 StartZ=0 EndX=-4.2 EndY=-13.4877 EndZ=0
    g3: Circle CenterX=-4.2 CenterY=-13.4877 CenterZ=0 NormalX=0 NormalY=0 NormalZ=1 AngleXU=0 Radius=1
    g4: Circle CenterX=-4.2 CenterY=-26.5 CenterZ=0 NormalX=0 NormalY=0 NormalZ=1 AngleXU=0 Radius=1
    g5: Circle CenterX=-8.2 CenterY=-26.5 CenterZ=0 NormalX=0 NormalY=0 NormalZ=1 AngleXU=0 Radius=1
    g6: BSplineCurve PolesCount=3 KnotsCount=2 Degree=2 IsPeriodic=0
    g7: GeomPoint X=-4.2 Y=-13.4877 Z=0
    g8: GeomPoint X=-8.2 Y=-26.5 Z=0
    g9: LineSegment StartX=-14 StartY=-26.5 StartZ=0 EndX=-8.2 EndY=-26.5 EndZ=0
    g10: LineSegment StartX=-10.15 StartY=-12 StartZ=0 EndX=-10.15 EndY=-14 EndZ=0
    g11: LineSegment StartX=-12.8401 StartY=-16 StartZ=0 EndX=-10.1571 EndY=-16 EndZ=0
    g12: LineSegment StartX=-10.15 StartY=-14 StartZ=0 EndX=-8.70761 EndY=-14 EndZ=0
    g13: LineSegment StartX=-12.8401 StartY=-16 StartZ=0 EndX=-12.8401 EndY=-17.6958 EndZ=0
    g14: LineSegment StartX=-10.15 StartY=-12 StartZ=0 EndX=-7.79258 EndY=-12 EndZ=0
    g15: Circle CenterX=-6.2215 CenterY=-2 CenterZ=0 NormalX=0 NormalY=0 NormalZ=1 AngleXU=0 Radius=1
    g16: Circle CenterX=-6.22762 CenterY=-2.58724 CenterZ=0 NormalX=0 NormalY=0 NormalZ=1 AngleXU=0 Radius=1
    g17: Circle CenterX=-6.32538 CenterY=-4 CenterZ=0 NormalX=0 NormalY=0 NormalZ=1 AngleXU=0 Radius=1
    g18: BSplineCurve PolesCount=3 KnotsCount=2 Degree=2 IsPeriodic=0
    g19: GeomPoint X=-6.2215 Y=-2 Z=0
    g20: GeomPoint X=-6.32538 Y=-4 Z=0
    g21: Circle CenterX=-6.48644 CenterY=-5.99526 CenterZ=0 NormalX=0 NormalY=0 NormalZ=1 AngleXU=0 Radius=1
    g22: Circle CenterX=-6.58486 CenterY=-6.99526 CenterZ=0 NormalX=0 NormalY=0 NormalZ=1 AngleXU=0 Radius=1
    g23: Circle CenterX=-6.77343 CenterY=-8 CenterZ=0 NormalX=0 NormalY=0 NormalZ=1 AngleXU=0 Radius=1
    g24: BSplineCurve PolesCount=3 KnotsCount=2 Degree=2 IsPeriodic=0
    g25: GeomPoint X=-6.48644 Y=-5.99526 Z=0
    g26: GeomPoint X=-6.77343 Y=-8 Z=0
    g27: Circle CenterX=-7.19003 CenterY=-10 CenterZ=0 NormalX=0 NormalY=0 NormalZ=1 AngleXU=0 Radius=1
    g28: Circle CenterX=-7.44407 CenterY=-11.0915 CenterZ=0 NormalX=0 NormalY=0 NormalZ=1 AngleXU=0 Radius=1
    g29: Circle CenterX=-7.79258 CenterY=-12 CenterZ=0 NormalX=0 NormalY=0 NormalZ=1 AngleXU=0 Radius=1
    g30: BSplineCurve PolesCount=3 KnotsCount=2 Degree=2 IsPeriodic=0
    g31: GeomPoint X=-7.19003 Y=-10 Z=0
    g32: GeomPoint X=-7.79258 Y=-12 Z=0
    g33: Circle CenterX=-8.70761 CenterY=-14 CenterZ=0 NormalX=0 NormalY=0 NormalZ=1 AngleXU=0 Radius=1
    g34: Circle CenterX=-9.33087 CenterY=-15.1837 CenterZ=0 NormalX=0 NormalY=0 NormalZ=1 AngleXU=0 Radius=1
    g35: Circle CenterX=-10.1571 CenterY=-16 CenterZ=0 NormalX=0 NormalY=0 NormalZ=1 AngleXU=0 Radius=1
    g36: BSplineCurve PolesCount=3 KnotsCount=2 Degree=2 IsPeriodic=0
    g37: GeomPoint X=-8.70761 Y=-14 Z=0
    g38: GeomPoint X=-10.1571 Y=-16 Z=0
    g39: Circle CenterX=-12.8401 CenterY=-17.6958 CenterZ=0 NormalX=0 NormalY=0 NormalZ=1 AngleXU=0 Radius=1
    g40: Circle CenterX=-13.3521 CenterY=-17.9027 CenterZ=0 NormalX=0 NormalY=0 NormalZ=1 AngleXU=0 Radius=1
    g41: Circle CenterX=-14 CenterY=-18 CenterZ=0 NormalX=0 NormalY=0 NormalZ=1 AngleXU=0 Radius=1
    g42: BSplineCurve PolesCount=3 KnotsCount=2 Degree=2 IsPeriodic=0
    g43: GeomPoint X=-12.8401 Y=-17.6958 Z=0
    g44: GeomPoint X=-14 Y=-18 Z=0
    g45: LineSegment StartX=-6.2 StartY=0 StartZ=0 EndX=-7.2 EndY=0 EndZ=0
    g46: LineSegment StartX=-7.2 StartY=0 StartZ=0 EndX=-7.2 EndY=-2 EndZ=0
    g47: LineSegment StartX=-7.2 StartY=-2 StartZ=0 EndX=-6.2215 EndY=-2 EndZ=0
    g48: LineSegment StartX=-6.32538 StartY=-4 StartZ=0 EndX=-7.65538 EndY=-4 EndZ=0
    g49: LineSegment StartX=-7.65538 StartY=-4 StartZ=0 EndX=-7.65538 EndY=-5.99526 EndZ=0
    g50: LineSegment StartX=-7.65538 StartY=-5.99526 StartZ=0 EndX=-6.48644 EndY=-5.99526 EndZ=0
    g51: LineSegment StartX=-6.77343 StartY=-8 StartZ=0 EndX=-8.43343 EndY=-8 EndZ=0
    g52: LineSegment StartX=-8.43343 StartY=-8 StartZ=0 EndX=-8.43343 EndY=-10 EndZ=0
    g53: LineSegment StartX=-8.43343 StartY=-10 StartZ=0 EndX=-7.19003 EndY=-10 EndZ=0
  constraints (112):
    c: Horizontal(g0)
    c: Distance(g0) = 2
    c: Block(g0)
    c: Vertical(g1)
    c: Coincident(g2,g0)
    c: Vertical(g2)
    c: Block(g2)
    c: Coincident(g6,g2)
    c: Weight(g3) = 1
    c: Equal(g3,g4)
    c: Equal(g3,g5)
    c: InternalAlignment(g3,g6)
    c: InternalAlignment(g4,g6)
    c: InternalAlignment(g5,g6)
    c: InternalAlignment(g7,g6)
    c: InternalAlignment(g8,g6)
    c: Block(g6)
    c: Coincident(g9,g1)
    c: Coincident(g9,g6)
    c: Horizontal(g9)
    c: Vertical(g10)
    c: Block(g10)
    c: Horizontal(g11)
    c: Block(g11)
    c: Coincident(g12,g10)
    c: Horizontal(g12)
    c: Block(g12)
    c: Coincident(g13,g11)
    c: Vertical(g13)
    c: Block(g13)
    c: Coincident(g14,g10)
    c: Horizontal(g14)
    c: Block(g14)
    c: Block(g9)
    c: Block(g1)
    c: Weight(g15) = 1
    c: Equal(g15,g16)
    c: Equal(g15,g17)
    c: InternalAlignment(g15,g18)
    c: InternalAlignment(g16,g18)
    c: InternalAlignment(g17,g18)
    c: InternalAlignment(g19,g18)
    c: InternalAlignment(g20,g18)
    c: Weight(g21) = 1
    c: Equal(g21,g22)
    c: Equal(g21,g23)
    c: InternalAlignment(g21,g24)
    c: InternalAlignment(g22,g24)
    c: InternalAlignment(g23,g24)
    c: InternalAlignment(g25,g24)
    c: InternalAlignment(g26,g24)
    c: Weight(g27) = 1
    c: Equal(g27,g28)
    c: Equal(g27,g29)
    c: Coincident(g30,g14)
    c: InternalAlignment(g27,g30)
    c: InternalAlignment(g28,g30)
    c: InternalAlignment(g29,g30)
    c: InternalAlignment(g31,g30)
    c: InternalAlignment(g32,g30)
    c: Coincident(g36,g12)
    c: Weight(g33) = 1
    c: Equal(g33,g34)
    c: Equal(g33,g35)
    c: Coincident(g36,g11)
    c: InternalAlignment(g33,g36)
    c: InternalAlignment(g34,g36)
    c: InternalAlignment(g35,g36)
    c: InternalAlignment(g37,g36)
    c: InternalAlignment(g38,g36)
    c: Coincident(g42,g13)
    c: Weight(g39) = 1
    c: Equal(g39,g40)
    c: Equal(g39,g41)
    c: Coincident(g42,g1)
    c: InternalAlignment(g39,g42)
    c: InternalAlignment(g40,g42)
    c: InternalAlignment(g41,g42)
    c: InternalAlignment(g43,g42)
    c: InternalAlignment(g44,g42)
    c: Block(g18)
    c: Block(g24)
    c: Block(g30)
    c: Block(g36)
    c: Block(g42)
    c: Horizontal(g45)
    c: Coincident(g45,g0)
    c: Vertical(g46)
    c: Coincident(g46,g45)
    c: Coincident(g47,g46)
    c: Coincident(g47,g18)
    c: Horizontal(g47)
    c: Block(g46)
    c: Coincident(g48,g18)
    c: Horizontal(g48)
    c: Distance(g48) = 1.33
    c: Vertical(g49)
    c: Coincident(g49,g48)
    c: Coincident(g50,g49)
    c: Coincident(g50,g24)
    c: Horizontal(g50)
    c: Tangent(g50,g22)
    c: Horizontal(g51)
    c: Coincident(g51,g24)
    c: Block(g51)
    c: Vertical(g52)
    c: Block(g52)
    c: Coincident(g52,g51)
    c: Coincident(g53,g52)
    c: Coincident(g53,g30)
    c: Horizontal(g53)
    c: Distance(g1) = 8.5
FEATURE [Part::Feature] Face024
  shape: bbox 9.8 x 26.5 x 2e-07 mm, 1 faces, 0 solids (baked)
FEATURE [Part::Revolution] Revolve024
  Angle = 360
  Axis = (0,1,0)
  Base = (0,0,0)
  FaceMakerClass = Part::FaceMakerBullseye
  Placement = pos=(0,0,0) rot=(0,0,1;1.5708rad)
  Solid = false
  Source = -> Face024
  Symmetric = false
FEATURE [Part::Feature] Face025
  shape: bbox 9.8 x 26.5 x 2e-07 mm, 1 faces, 0 solids (baked)
FEATURE [Part::Revolution] Revolve025
  Angle = 360
  Axis = (0,1,0)
  Base = (0,0,0)
  FaceMakerClass = Part::FaceMakerBullseye
  Placement = pos=(0,0,0) rot=(0,0,1;1.5708rad)
  Solid = false
  Source = -> Face025
  Symmetric = false
FEATURE [Part::MultiFuse] Fusion033
  Placement = pos=(-18,19,36) rot=(0,0,1;0rad)
  Shapes = -> [Revolve025,Revolve024]
FEATURE [Part::Cylinder] Cylinder014
  Angle = 360
  AttacherType = Attacher::AttachEngine3D
  Height = 20
  Placement = pos=(0,0,36.15) rot=(0,0,1;0rad)
  Radius = 14.3
FEATURE [Part::Cylinder] Cylinder015
  Angle = 360
  AttacherType = Attacher::AttachEngine3D
  Height = 10
  Placement = pos=(0,0,36.15) rot=(0,0,1;0rad)
  Radius = 4
FEATURE [Part::MultiFuse] Fusion034  label="removeToCreteHoleForPlugHousing004"
  Placement = pos=(-42,19,36) rot=(0,1,0;1.5708rad)
  Shapes = -> [Cylinder014,Cylinder015]
FEATURE [Part::Cut] Cut008  label="top004"
  Base = -> Cut004
  Placement = pos=(-1,0,0) rot=(0,0,1;0rad)
  Tool = -> Fusion034
FEATURE [Part::Box] Box005  label="Cube005"
  AttacherType = Attacher::AttachEngine3D
  Height = 28
  Length = 3
  Placement = pos=(110.7,19,22) rot=(0,0,1;0rad)
  Width = 15.7
FEATURE [Part::Cylinder] Cylinder016
  Angle = 360
  AttacherType = Attacher::AttachEngine3D
  Height = 10
  Placement = pos=(0,0,36.15) rot=(0,0,1;0rad)
  Radius = 4
FEATURE [Part::Cylinder] Cylinder017
  Angle = 360
  AttacherType = Attacher::AttachEngine3D
  Height = 20
  Placement = pos=(0,0,36.15) rot=(0,0,1;0rad)
  Radius = 10.3
FEATURE [Part::MultiFuse] Fusion035  label="removeToCreteHoleForPlugHousing005"
  Placement = pos=(70,19,36) rot=(0,1,0;1.5708rad)
  Shapes = -> [Cylinder017,Cylinder016]
FEATURE [Part::Cut] Cut009  label="plugHousingTab001"
  Base = -> Box005
  Placement = pos=(-107.4,-14,0) rot=(0,0,1;0rad)
  Tool = -> Fusion035
FEATURE [Part::Box] Box006  label="Cube006"
  AttacherType = Attacher::AttachEngine3D
  Height = 28
  Length = 3
  Placement = pos=(110.7,19,22) rot=(0,0,1;0rad)
  Width = 15.7
FEATURE [Part::Cylinder] Cylinder018
  Angle = 360
  AttacherType = Attacher::AttachEngine3D
  Height = 10
  Placement = pos=(0,0,36.15) rot=(0,0,1;0rad)
  Radius = 4
FEATURE [Part::Cylinder] Cylinder019
  Angle = 360
  AttacherType = Attacher::AttachEngine3D
  Height = 20
  Placement = pos=(0,0,36.15) rot=(0,0,1;0rad)
  Radius = 10.3
FEATURE [Part::MultiFuse] Fusion036  label="removeToCreteHoleForPlugHousing006"
  Placement = pos=(70,19,36) rot=(0,1,0;1.5708rad)
  Shapes = -> [Cylinder019,Cylinder018]
FEATURE [Part::Cut] Cut010  label="plugHousingTab002"
  Base = -> Box006
  Placement = pos=(-107.4,-14,0) rot=(0,0,1;0rad)
  Tool = -> Fusion036
FEATURE [Part::MultiFuse] Fusion037
  Placement = pos=(9.6,23,0) rot=(0,0,1;3.14159rad)
  Shapes = -> [Cut009,Cut010]
FEATURE [Part::Box] Box  label="Cube"
  AttacherType = Attacher::AttachEngine3D
  Height = 10
  Length = 3
  Placement = pos=(3.3,4,12) rot=(0,0,1;0rad)
  Width = 10
FEATURE [Part::Fillet] Fillet004
  Base = -> Fusion028
  Edges = 1 edges r=2: [Edge25]
FEATURE [Part::Fillet] Fillet005  label="plugHousing046"
  Base = -> Fillet004
  Edges = 1 edges r=2: [Edge8]
FEATURE [Part::Fillet] Fillet006
  Base = -> Box
  Edges = 1 edges r=2: [Edge11]
FEATURE [Part::Box] Box007  label="Cube007"
  AttacherType = Attacher::AttachEngine3D
  Height = 10
  Length = 3
  Placement = pos=(3.3,4,50) rot=(0,0,1;0rad)
  Width = 10
FEATURE [Part::Fillet] Fillet007
  Base = -> Box007
  Edges = 1 edges r=2: [Edge12]
FEATURE [Part::Box] Box008  label="Cube008"
  AttacherType = Attacher::AttachEngine3D
  Height = 28
  Length = 4
  Placement = pos=(5,0,22) rot=(0,0,1;0rad)
  Width = 10
FEATURE [Part::Fillet] Fillet008
  Base = -> Box008
  Edges = 1 edges r=1: [Edge7]
FEATURE [Part::Fillet] Fillet009
  Base = -> Fillet008
  Edges = 1 edges r=2: [Edge5]
FEATURE [Part::Fillet] Fillet010
  Base = -> Fillet009
  Edges = 1 edges r=2: [Edge2]
FEATURE [Sketcher::SketchObject] Sketch009  label="topSketch003"
  FullyConstrained = true
  sketch-geometry (4):
    g0: LineSegment StartX=16.8446 StartY=31.512 StartZ=0 EndX=16.3251 EndY=34.4666 EndZ=0
    g1: ArcOfCircle CenterX=19 CenterY=19.2524 CenterZ=0 NormalX=0 NormalY=0 NormalZ=1 AngleXU=0 Radius=15.4476 StartAngle=1.74483 EndAngle=2.72717
    g2: ArcOfCircle CenterX=19 CenterY=19.2524 CenterZ=0 NormalX=0 NormalY=0 NormalZ=1 AngleXU=0 Radius=12.4476 StartAngle=1.74483 EndAngle=2.73189
    g3: LineSegment StartX=4.86004 StartY=25.4725 StartZ=0 EndX=7.58253 EndY=24.2107 EndZ=0
  constraints (7):
    c: Block(g0)
    c: Coincident(g1,g0)
    c: Coincident(g2,g0)
    c: Coincident(g3,g1)
    c: Coincident(g3,g2)
    c: Block(g1)
    c: Block(g2)
FEATURE [Part::Extrusion] Extrude008
  Base = -> Sketch009
  Dir = (0,0,1)
  DirMode = 2
  FaceMakerClass = Part::FaceMakerBullseye
  LengthFwd = 10
  LengthRev = 0
  Placement = pos=(0,0,31) rot=(0,0,1;0rad)
  Solid = true
  Symmetric = false
FEATURE [Part::Cylinder] Cylinder020
  Angle = 360
  AttacherType = Attacher::AttachEngine3D
  Height = 20
  Placement = pos=(0,0,36.15) rot=(0,0,1;0rad)
  Radius = 8.2
FEATURE [Part::Cylinder] Cylinder021
  Angle = 360
  AttacherType = Attacher::AttachEngine3D
  Height = 10
  Placement = pos=(0,0,36.15) rot=(0,0,1;0rad)
  Radius = 4
FEATURE [Part::MultiFuse] Fusion038  label="removeToCreteHoleForPlugHousing007"
  Placement = pos=(-42,19,36) rot=(0,1,0;1.5708rad)
  Shapes = -> [Cylinder020,Cylinder021]
FEATURE [Part::Cut] Cut011
  Base = -> Extrude008
  Tool = -> Fusion038
FEATURE [Part::Fillet] Fillet011
  Base = -> Cut011
  Edges = 1 edges r=2: [Edge1]
FEATURE [Part::Fillet] Fillet012
  Base = -> Fillet011
  Edges = 1 edges r=2.5: [Edge1]
FEATURE [Part::Fillet] Fillet013
  Base = -> Fillet012
  Edges = 1 edges r=2.5: [Edge2]
FEATURE [Part::Box] Box010  label="Cube010"
  AttacherType = Attacher::AttachEngine3D
  Height = 16
  Length = 8
  Placement = pos=(12.7,31.52,28) rot=(0,0,1;0rad)
  Width = 4
FEATURE [Sketcher::SketchObject] Sketch010  label="topSketch004"
  FullyConstrained = true
  sketch-geometry (4):
    g0: LineSegment StartX=16.8446 StartY=31.512 StartZ=0 EndX=16.3251 EndY=34.4666 EndZ=0
    g1: ArcOfCircle CenterX=19 CenterY=19.2524 CenterZ=0 NormalX=0 NormalY=0 NormalZ=1 AngleXU=0 Radius=15.4476 StartAngle=1.74483 EndAngle=2.72717
    g2: ArcOfCircle CenterX=19 CenterY=19.2524 CenterZ=0 NormalX=0 NormalY=0 NormalZ=1 AngleXU=0 Radius=12.4476 StartAngle=1.74483 EndAngle=2.73189
    g3: LineSegment StartX=4.86004 StartY=25.4725 StartZ=0 EndX=7.58253 EndY=24.2107 EndZ=0
  constraints (7):
    c: Block(g0)
    c: Coincident(g1,g0)
    c: Coincident(g2,g0)
    c: Coincident(g3,g1)
    c: Coincident(g3,g2)
    c: Block(g1)
    c: Block(g2)
FEATURE [Part::Cylinder] Cylinder022
  Angle = 360
  AttacherType = Attacher::AttachEngine3D
  Height = 10
  Placement = pos=(0,0,36.15) rot=(0,0,1;0rad)
  Radius = 4
FEATURE [Sketcher::SketchObject] Sketch011  label="topSketch005"
  FullyConstrained = true
  sketch-geometry (4):
    g0: LineSegment StartX=16.8446 StartY=31.512 StartZ=0 EndX=16.3251 EndY=34.4666 EndZ=0
    g1: ArcOfCircle CenterX=19 CenterY=19.2524 CenterZ=0 NormalX=0 NormalY=0 NormalZ=1 AngleXU=0 Radius=15.4476 StartAngle=1.74483 EndAngle=2.72717
    g2: ArcOfCircle CenterX=19 CenterY=19.2524 CenterZ=0 NormalX=0 NormalY=0 NormalZ=1 AngleXU=0 Radius=12.4476 StartAngle=1.74483 EndAngle=2.73189
    g3: LineSegment StartX=4.86004 StartY=25.4725 StartZ=0 EndX=7.58253 EndY=24.2107 EndZ=0
  constraints (7):
    c: Block(g0)
    c: Coincident(g1,g0)
    c: Coincident(g2,g0)
    c: Coincident(g3,g1)
    c: Coincident(g3,g2)
    c: Block(g1)
    c: Block(g2)
FEATURE [Part::Extrusion] Extrude010
  Base = -> Sketch011
  Dir = (0,0,1)
  DirMode = 2
  FaceMakerClass = Part::FaceMakerBullseye
  LengthFwd = 10.6
  LengthRev = 0
  Placement = pos=(0,0,31) rot=(0,0,1;0rad)
  Solid = true
  Symmetric = false
FEATURE [Part::Cylinder] Cylinder023
  Angle = 360
  AttacherType = Attacher::AttachEngine3D
  Height = 20
  Placement = pos=(0,0,36.15) rot=(0,0,1;0rad)
  Radius = 8.2
FEATURE [Part::MultiFuse] Fusion039  label="removeToCreteHoleForPlugHousing008"
  Placement = pos=(-42,19,36) rot=(0,1,0;1.5708rad)
  Shapes = -> [Cylinder023,Cylinder022]
FEATURE [Part::Cut] Cut012
  Base = -> Extrude010
  Placement = pos=(0,0,-0.3) rot=(0,0,1;0rad)
  Tool = -> Fusion039
FEATURE [Part::Cut] Cut013
  Base = -> Box010
  Tool = -> Cut012
FEATURE [Part::Fillet] Fillet014
  Base = -> Cut013
  Edges = 1 edges r=0.7: [Edge13]
FEATURE [Part::Fillet] Fillet015
  Base = -> Fillet014
  Edges = 1 edges r=0.7: [Edge13]
FEATURE [Part::Fillet] Fillet016
  Base = -> Fillet015
  Edges = 1 edges r=0.7: [Edge16]
FEATURE [Part::Fillet] Fillet017
  Base = -> Fillet016
  Edges = 1 edges r=0.7: [Edge11]
FEATURE [Part::Fillet] Fillet018
  Base = -> Fillet017
  Edges = 1 edges r=0.7: [Edge10]
FEATURE [Part::Fillet] Fillet019
  Base = -> Fillet018
  Edges = 1 edges r=1.2: [Edge5]
FEATURE [Part::Fillet] Fillet020
  Base = -> Fillet019
  Edges = 1 edges r=1.2: [Edge12]
FEATURE [Part::Fillet] Fillet021
  Base = -> Fillet020
  Edges = 1 edges r=2: [Edge1]
  Placement = pos=(0.3,0,0) rot=(0,0,1;0rad)
FEATURE [Part::MultiFuse] Fusion040  label="top005"
  Shapes = -> [Cut008,Fillet021]
FEATURE [Part::MultiFuse] Fusion041  label="wireHolder"
  Shapes = -> [Fusion033,Fillet013]
FEATURE [Part::MultiFuse] Fusion042
  Shapes = -> [Fillet007,Fusion041]
FEATURE [Part::MultiFuse] Fusion043  label="wireHolder001"
  Shapes = -> [Fusion042,Fillet010]
FEATURE [Part::MultiFuse] Fusion044  label="wireHolder002"
  Shapes = -> [Fillet006,Fusion037,Fusion043]
FEATURE [Part::Feature] Face026
  shape: bbox 11 x 6 x 2e-07 mm, 1 faces, 0 solids (baked)
FEATURE [Part::Revolution] Revolve026
  Angle = 360
  Axis = (0,1,0)
  Base = (0,0,0)
  FaceMakerClass = Part::FaceMakerBullseye
  Placement = pos=(30.3,-1,19.7) rot=(0,0,1;0rad)
  Solid = false
  Source = -> Face026
  Symmetric = false
FEATURE [Sketcher::SketchObject] Sketch013  label="topSketch006"
  FullyConstrained = true
  sketch-geometry (13):
    g0: LineSegment StartX=117 StartY=19 StartZ=0 EndX=117 EndY=38 EndZ=0
    g1: ArcOfCircle CenterX=98 CenterY=19 CenterZ=0 NormalX=0 NormalY=0 NormalZ=1 AngleXU=0 Radius=19 StartAngle=5.7297 EndAngle=6.28319
    g2: LineSegment StartX=0 StartY=3 StartZ=0 EndX=0 EndY=19 EndZ=0
    g3: LineSegment StartX=19 StartY=38 StartZ=0 EndX=117 EndY=38 EndZ=0
    g4: ArcOfCircle CenterX=19 CenterY=19 CenterZ=0 NormalX=0 NormalY=0 NormalZ=1 AngleXU=0 Radius=19 StartAngle=1.5708 EndAngle=3.14159
    g5: ArcOfCircle CenterX=19 CenterY=19 CenterZ=0 NormalX=0 NormalY=0 NormalZ=1 AngleXU=0 Radius=16 StartAngle=1.5708 EndAngle=3.14159
    g6: ArcOfCircle CenterX=98 CenterY=19 CenterZ=0 NormalX=0 NormalY=0 NormalZ=1 AngleXU=0 Radius=16 StartAngle=5.60905 EndAngle=6.28319
    g7: LineSegment StartX=114 StartY=19 StartZ=0 EndX=114 EndY=35 EndZ=0
    g8: LineSegment StartX=110.5 StartY=9.01251 StartZ=0 EndX=114.163 EndY=9.01251 EndZ=0
    g9: LineSegment StartX=114 StartY=35 StartZ=0 EndX=19 EndY=35 EndZ=0
    g10: LineSegment StartX=0 StartY=3 StartZ=0 EndX=0 EndY=0 EndZ=0
    g11: LineSegment StartX=3 StartY=0 StartZ=0 EndX=0 EndY=0 EndZ=0
    g12: LineSegment StartX=3 StartY=19 StartZ=0 EndX=3 EndY=0 EndZ=0
  constraints (33):
    c: Vertical(g0)
    c: Distance(g0) = 19
    c: Block(g0)
    c: Coincident(g1,g0)
    c: Block(g1)
    c: Vertical(g2)
    c: Block(g2)
    c: Coincident(g3,g0)
    c: Horizontal(g3)
    c: Distance(g3) = 98
    c: Coincident(g4,g3)
    c: Coincident(g4,g2)
    c: Block(g4)
    c: Coincident(g5,g4)
    c: Coincident(g6,g1)
    c: Block(g6)
    c: Block(g5)
    c: Coincident(g7,g6)
    c: Vertical(g7)
    c: Coincident(g8,g6)
    c: Coincident(g8,g1)
    c: Coincident(g9,g7)
    c: Coincident(g9,g5)
    c: Horizontal(g9)
    c: Tangent(g9,g5)
    c: Coincident(g10,g2)
    c: Distance(g10) = 3
    c: Vertical(g10)
    c: Coincident(g11,g10)
    c: Horizontal(g11)
    c: Coincident(g12,g5)
    c: Coincident(g12,g11)
    c: Vertical(g12)
FEATURE [Part::Extrusion] Extrude011  label="top006"
  Base = -> Sketch013
  Dir = (0,0,1)
  DirMode = 2
  FaceMakerClass = Part::FaceMakerBullseye
  LengthFwd = 72
  LengthRev = 0
  Solid = true
  Symmetric = false
FEATURE [Sketcher::SketchObject] Sketch014
  FullyConstrained = true
  MapMode = 3
  Placement = pos=(0,0,0) rot=(1,0,0;1.5708rad)
  Support = -> [Extrude011]
  sketch-geometry (8):
    g0: Circle CenterX=80.351 CenterY=-67.6202 CenterZ=0 NormalX=0 NormalY=0 NormalZ=1 AngleXU=0 Radius=2
    g1: Circle CenterX=80.351 CenterY=-67.6202 CenterZ=0 NormalX=0 NormalY=0 NormalZ=1 AngleXU=0 Radius=3
    g2: Circle CenterX=80.351 CenterY=-4.92017 CenterZ=0 NormalX=0 NormalY=0 NormalZ=1 AngleXU=0 Radius=2
    g3: Circle CenterX=80.351 CenterY=-4.92017 CenterZ=0 NormalX=0 NormalY=0 NormalZ=1 AngleXU=0 Radius=3
    g4: Circle CenterX=23.851 CenterY=-4.92017 CenterZ=0 NormalX=0 NormalY=0 NormalZ=1 AngleXU=0 Radius=2
    g5: Circle CenterX=23.851 CenterY=-4.92017 CenterZ=0 NormalX=0 NormalY=0 NormalZ=1 AngleXU=0 Radius=3
    g6: Circle CenterX=23.851 CenterY=-67.6202 CenterZ=0 NormalX=0 NormalY=0 NormalZ=1 AngleXU=0 Radius=2
    g7: Circle CenterX=23.851 CenterY=-67.6202 CenterZ=0 NormalX=0 NormalY=0 NormalZ=1 AngleXU=0 Radius=3
  constraints (8):
    c: Block(g3)
    c: Block(g2)
    c: Block(g1)
    c: Block(g0)
    c: Block(g6)
    c: Block(g7)
    c: Block(g4)
    c: Block(g5)
FEATURE [Part::Feature] Face027
  shape: bbox 11 x 6 x 2e-07 mm, 1 faces, 0 solids (baked)
FEATURE [Part::Revolution] Revolve027
  Angle = 360
  Axis = (0,1,0)
  Base = (0,0,0)
  FaceMakerClass = Part::FaceMakerBullseye
  Placement = pos=(30.3,-1,51.7) rot=(0,0,1;0rad)
  Solid = false
  Source = -> Face027
  Symmetric = false
FEATURE [Part::Feature] Face028
  shape: bbox 11 x 6 x 2e-07 mm, 1 faces, 0 solids (baked)
FEATURE [Part::Revolution] Revolve028
  Angle = 360
  Axis = (0,1,0)
  Base = (0,0,0)
  FaceMakerClass = Part::FaceMakerBullseye
  Placement = pos=(62.3,-1,19.7) rot=(0,0,1;0rad)
  Solid = false
  Source = -> Face028
  Symmetric = false
FEATURE [Part::Feature] Face029
  shape: bbox 11 x 6 x 2e-07 mm, 1 faces, 0 solids (baked)
FEATURE [Part::Revolution] Revolve029
  Angle = 360
  Axis = (0,1,0)
  Base = (0,0,0)
  FaceMakerClass = Part::FaceMakerBullseye
  Placement = pos=(62.3,-1,51.7) rot=(0,0,1;0rad)
  Solid = false
  Source = -> Face029
  Symmetric = false
FEATURE [Part::Feature] Wire
  shape: bbox 11 x 5.2 x 2e-07 mm, 0 faces, 0 solids (baked)
FEATURE [Part::Revolution] Revolve030
  Angle = 360
  Axis = (0,1,0)
  Base = (0,0,0)
  FaceMakerClass = Part::FaceMakerBullseye
  Placement = pos=(30.3,38,19.7) rot=(0,0,1;0rad)
  Solid = true
  Source = -> Wire
  Symmetric = false
FEATURE [Part::Feature] Wire001
  shape: bbox 11 x 5.2 x 2e-07 mm, 0 faces, 0 solids (baked)
FEATURE [Part::Revolution] Revolve031
  Angle = 360
  Axis = (0,1,0)
  Base = (0,0,0)
  FaceMakerClass = Part::FaceMakerBullseye
  Placement = pos=(30.3,38,51.7) rot=(0,0,1;0rad)
  Solid = true
  Source = -> Wire001
  Symmetric = false
FEATURE [Part::Feature] Wire002
  shape: bbox 11 x 5.2 x 2e-07 mm, 0 faces, 0 solids (baked)
FEATURE [Part::Revolution] Revolve032
  Angle = 360
  Axis = (0,1,0)
  Base = (0,0,0)
  FaceMakerClass = Part::FaceMakerBullseye
  Placement = pos=(62.3,38,51.7) rot=(0,0,1;0rad)
  Solid = true
  Source = -> Wire002
  Symmetric = false
FEATURE [Part::Feature] Wire003
  shape: bbox 11 x 5.2 x 2e-07 mm, 0 faces, 0 solids (baked)
FEATURE [Part::Revolution] Revolve033
  Angle = 360
  Axis = (0,1,0)
  Base = (0,0,0)
  FaceMakerClass = Part::FaceMakerBullseye
  Placement = pos=(62.3,38,19.7) rot=(0,0,1;0rad)
  Solid = true
  Source = -> Wire003
  Symmetric = false
FEATURE [Part::MultiFuse] Fusion045  label="altRandScrewHousing"
  Shapes = -> [Revolve029,Revolve027,Revolve028,Revolve026]
FEATURE [Part::MultiFuse] Fusion046  label="fanScrewHousing"
  Shapes = -> [Revolve033,Revolve032,Revolve031,Revolve030]
FEATURE [Sketcher::SketchObject] Sketch015
  FullyConstrained = true
  sketch-geometry (17):
    g0: Circle CenterX=-3.5 CenterY=23.5 CenterZ=0 NormalX=0 NormalY=0 NormalZ=1 AngleXU=0 Radius=1
    g1: Circle CenterX=-1 CenterY=15.25 CenterZ=0 NormalX=0 NormalY=0 NormalZ=1 AngleXU=0 Radius=1
    g2: Circle CenterX=-3.5 CenterY=7 CenterZ=0 NormalX=0 NormalY=0 NormalZ=1 AngleXU=0 Radius=1
    g3: BSplineCurve PolesCount=3 KnotsCount=2 Degree=2 IsPeriodic=0
    g4: GeomPoint X=-3.5 Y=23.5 Z=0
    g5: GeomPoint X=-3.5 Y=7 Z=0
    g6: Circle CenterX=-4.8 CenterY=30.5 CenterZ=0 NormalX=0 NormalY=0 NormalZ=1 AngleXU=0 Radius=1
    g7: Circle CenterX=-3.5 CenterY=30.5 CenterZ=0 NormalX=0 NormalY=0 NormalZ=1 AngleXU=0 Radius=1
    g8: Circle CenterX=-3.5 CenterY=29.2 CenterZ=0 NormalX=0 NormalY=0 NormalZ=1 AngleXU=0 Radius=1
    g9: BSplineCurve PolesCount=3 KnotsCount=2 Degree=2 IsPeriodic=0
    g10: GeomPoint X=-4.8 Y=30.5 Z=0
    g11: GeomPoint X=-3.5 Y=29.2 Z=0
    g12: LineSegment StartX=-3.5 StartY=29.2 StartZ=0 EndX=-3.5 EndY=23.5 EndZ=0
    g13: LineSegment StartX=-4.8 StartY=30.5 StartZ=0 EndX=0 EndY=30.5 EndZ=0
    g14: LineSegment StartX=-3.5 StartY=0.3 StartZ=0 EndX=0 EndY=0.3 EndZ=0
    g15: LineSegment StartX=-3.5 StartY=0.3 StartZ=0 EndX=-3.5 EndY=7 EndZ=0
    g16: LineSegment StartX=0 StartY=0.3 StartZ=0 EndX=0 EndY=30.5 EndZ=0
  constraints (33):
    c: Weight(g0) = 1
    c: Equal(g0,g1)
    c: Equal(g0,g2)
    c: InternalAlignment(g0,g3)
    c: InternalAlignment(g1,g3)
    c: InternalAlignment(g2,g3)
    c: InternalAlignment(g4,g3)
    c: InternalAlignment(g5,g3)
    c: Block(g3)
    c: Weight(g6) = 1
    c: Equal(g6,g7)
    c: Equal(g6,g8)
    c: InternalAlignment(g6,g9)
    c: InternalAlignment(g7,g9)
    c: InternalAlignment(g8,g9)
    c: InternalAlignment(g10,g9)
    c: InternalAlignment(g11,g9)
    c: Block(g9)
    c: Coincident(g12,g9)
    c: Coincident(g12,g3)
    c: Vertical(g12)
    c: Coincident(g13,g9)
    c: Horizontal(g13)
    c: Distance(g13) = 4.8
    c: Horizontal(g14)
    c: Block(g14)
    c: Coincident(g15,g14)
    c: Coincident(g15,g3)
    c: Vertical(g15)
    c: Coincident(g16,g14)
    c: Coincident(g16,g13)
    c: Vertical(g16)
    c: Tangent(g16,g1)
FEATURE [Sketcher::SketchObject] Sketch016
  FullyConstrained = true
  sketch-geometry (16):
    g0: Circle CenterX=-3.5 CenterY=23.5 CenterZ=0 NormalX=0 NormalY=0 NormalZ=1 AngleXU=0 Radius=1
    g1: Circle CenterX=-1 CenterY=15.25 CenterZ=0 NormalX=0 NormalY=0 NormalZ=1 AngleXU=0 Radius=1
    g2: Circle CenterX=-3.5 CenterY=7 CenterZ=0 NormalX=0 NormalY=0 NormalZ=1 AngleXU=0 Radius=1
    g3: BSplineCurve PolesCount=3 KnotsCount=2 Degree=2 IsPeriodic=0
    g4: GeomPoint X=-3.5 Y=23.5 Z=0
    g5: GeomPoint X=-3.5 Y=7 Z=0
    g6: LineSegment StartX=-3.5 StartY=28.2 StartZ=0 EndX=-3.5 EndY=23.5 EndZ=0
    g7: LineSegment StartX=0 StartY=29.5 StartZ=0 EndX=0 EndY=30 EndZ=0
    g8: LineSegment StartX=-3.5 StartY=28.2 StartZ=0 EndX=-3.5 EndY=30 EndZ=0
    g9: LineSegment StartX=0 StartY=30 StartZ=0 EndX=0 EndY=30.5 EndZ=0
    g10: LineSegment StartX=0 StartY=30.5 StartZ=0 EndX=-3.5 EndY=30.5 EndZ=0
    g11: LineSegment StartX=-3.5 StartY=30.5 StartZ=0 EndX=-3.5 EndY=30 EndZ=0
    g12: LineSegment StartX=0 StartY=29.5 StartZ=0 EndX=0 EndY=5 EndZ=0
    g13: LineSegment StartX=-3.5 StartY=0.3 StartZ=0 EndX=-3.5 EndY=7 EndZ=0
    g14: LineSegment StartX=-3.5 StartY=0.3 StartZ=0 EndX=0 EndY=0.3 EndZ=0
    g15: LineSegment StartX=0 StartY=5 StartZ=0 EndX=0 EndY=0.3 EndZ=0
  constraints (39):
    c: Weight(g0) = 1
    c: Equal(g0,g1)
    c: Equal(g0,g2)
    c: InternalAlignment(g0,g3)
    c: InternalAlignment(g1,g3)
    c: InternalAlignment(g2,g3)
    c: InternalAlignment(g4,g3)
    c: InternalAlignment(g5,g3)
    c: Block(g3)
    c: Coincident(g6,g3)
    c: Vertical(g6)
    c: Vertical(g7)
    c: Distance(g7) = 0.5
    c: Coincident(g8,g6)
    c: Vertical(g8)
    c: Block(g6)
    c: Block(g7)
    c: Vertical(g9)
    c: Equal(g7,g9) = 0.5
    c: Block(g9)
    c: Coincident(g9,g7)
    c: Horizontal(g10)
    c: Coincident(g10,g9)
    c: Coincident(g11,g10)
    c: Coincident(g11,g8)
    c: Vertical(g11)
    c: Block(g11)
    c: Coincident(g12,g7)
    c: Vertical(g12)
    c: Coincident(g13,g3)
    c: Vertical(g13)
    c: Distance(g13) = 6.7
    c: Coincident(g14,g13)
    c: Horizontal(g14)
    c: Block(g14)
    c: Coincident(g15,g12)
    c: Coincident(g15,g14)
    c: Vertical(g15)
    c: Block(g15)
FEATURE [Sketcher::SketchObject] Sketch017
  FullyConstrained = true
  sketch-geometry (11):
    g0: LineSegment StartX=-3.5 StartY=1e-16 StartZ=0 EndX=-1.6 EndY=1e-16 EndZ=0
    g1: LineSegment StartX=-1.6 StartY=1e-16 StartZ=0 EndX=-1.6 EndY=1.5 EndZ=0
    g2: LineSegment StartX=-3.5 StartY=1.5 StartZ=0 EndX=-1.6 EndY=1.5 EndZ=0
    g3: LineSegment StartX=-3.5 StartY=1e-16 StartZ=0 EndX=-4.8 EndY=1e-16 EndZ=0
    g4: Circle CenterX=-3.5 CenterY=1.3 CenterZ=0 NormalX=0 NormalY=0 NormalZ=1 AngleXU=0 Radius=1
    g5: Circle CenterX=-3.5 CenterY=1e-16 CenterZ=0 NormalX=0 NormalY=0 NormalZ=1 AngleXU=0 Radius=1
    g6: Circle CenterX=-4.8 CenterY=1e-16 CenterZ=0 NormalX=0 NormalY=0 NormalZ=1 AngleXU=0 Radius=1
    g7: BSplineCurve PolesCount=3 KnotsCount=2 Degree=2 IsPeriodic=0
    g8: GeomPoint X=-3.5 Y=1.3 Z=0
    g9: GeomPoint X=-4.8 Y=1e-16 Z=0
    g10: LineSegment StartX=-3.5 StartY=1.3 StartZ=0 EndX=-3.5 EndY=1.5 EndZ=0
  constraints (24):
    c: Horizontal(g0)
    c: Distance(g0) = 1.9
    c: Block(g0)
    c: Coincident(g1,g0)
    c: Vertical(g1)
    c: Coincident(g2,g1)
    c: Horizontal(g2)
    c: Coincident(g3,g0)
    c: Horizontal(g3)
    c: Distance(g3) = 1.3
    c: Weight(g4) = 1
    c: Equal(g4,g5)
    c: Coincident(g5,g0)
    c: Equal(g4,g6)
    c: Coincident(g7,g3)
    c: InternalAlignment(g4,g7)
    c: InternalAlignment(g5,g7)
    c: InternalAlignment(g6,g7)
    c: InternalAlignment(g8,g7)
    c: InternalAlignment(g9,g7)
    c: Coincident(g10,g7)
    c: Coincident(g10,g2)
    c: Vertical(g10)
    c: Block(g10)
FEATURE [Part::Feature] Face035
  shape: bbox 3.2 x 1.5 x 2e-07 mm, 1 faces, 0 solids (baked)
FEATURE [Part::Revolution] Revolve039  label="backCaseScrewRetainer"
  Angle = 360
  Axis = (0,1,0)
  Base = (0,0,0)
  FaceMakerClass = Part::FaceMakerBullseye
  Placement = pos=(12.5,3,62) rot=(0,0,1;0rad)
  Solid = false
  Source = -> Face035
  Symmetric = false
FEATURE [Part::Feature] Face036
  shape: bbox 3.2 x 1.5 x 2e-07 mm, 1 faces, 0 solids (baked)
FEATURE [Part::Feature] Face039
  shape: bbox 4.8 x 30.2 x 2e-07 mm, 1 faces, 0 solids (baked)
FEATURE [Part::Revolution] Revolve043  label="frontCaseScrewPost002"
  Angle = 360
  Axis = (0,1,0)
  Base = (0,0,0)
  FaceMakerClass = Part::FaceMakerBullseye
  Placement = pos=(89.5,4.5,3.5) rot=(0,0,1;0rad)
  Solid = false
  Source = -> Face039
  Symmetric = false
FEATURE [Part::Feature] Face042
  shape: bbox 4.8 x 30.2 x 2e-07 mm, 1 faces, 0 solids (baked)
FEATURE [Part::Revolution] Revolve046  label="frontCaseScrewPost003"
  Angle = 360
  Axis = (0,1,0)
  Base = (0,0,0)
  FaceMakerClass = Part::FaceMakerBullseye
  Placement = pos=(89.5,4.5,68.5) rot=(0,0,1;0rad)
  Solid = false
  Source = -> Face042
  Symmetric = false
FEATURE [Part::Feature] Face043
  shape: bbox 3.2 x 1.5 x 2e-07 mm, 1 faces, 0 solids (baked)
FEATURE [Part::Revolution] Revolve047  label="frontCaseScrewRetainer002"
  Angle = 360
  Axis = (0,1,0)
  Base = (0,0,0)
  FaceMakerClass = Part::FaceMakerBullseye
  Placement = pos=(89.5,3,68.5) rot=(0,0,1;0rad)
  Solid = false
  Source = -> Face043
  Symmetric = false
FEATURE [Part::Feature] Face044
  shape: bbox 3.2 x 1.5 x 2e-07 mm, 1 faces, 0 solids (baked)
FEATURE [Part::Revolution] Revolve048  label="frontCaseScrewRetainer003"
  Angle = 360
  Axis = (0,1,0)
  Base = (0,0,0)
  FaceMakerClass = Part::FaceMakerBullseye
  Placement = pos=(89.5,3,3.5) rot=(0,0,1;0rad)
  Solid = false
  Source = -> Face044
  Symmetric = false
FEATURE [App::MeasureDistance] Distance002  label="Distance: 1.67 mm"
  Distance = 1.66921
  P1 = (99.2361,4.7524,71.7)
  P2 = (99.2347,6.42161,71.7)
FEATURE [Sketcher::SketchObject] Sketch018
  FullyConstrained = true
  sketch-geometry (7):
    g0: LineSegment StartX=0 StartY=0 StartZ=0 EndX=0 EndY=6 EndZ=0
    g1: Circle CenterX=0 CenterY=0 CenterZ=0 NormalX=0 NormalY=0 NormalZ=1 AngleXU=0 Radius=1
    g2: Circle CenterX=8 CenterY=6 CenterZ=0 NormalX=0 NormalY=0 NormalZ=1 AngleXU=0 Radius=1
    g3: BSplineCurve PolesCount=3 KnotsCount=2 Degree=2 IsPeriodic=0
    g4: GeomPoint X=0 Y=0 Z=0
    g5: GeomPoint X=8 Y=6 Z=0
    g6: LineSegment StartX=0 StartY=6 StartZ=0 EndX=8 EndY=6 EndZ=0
  constraints (14):
    c: Coincident(g0,g-1)
    c: Distance(g0) = 6
    c: Vertical(g0)
    c: Coincident(g3,g0)
    c: Weight(g1) = 1
    c: Equal(g1,g2)
    c: InternalAlignment(g1,g3)
    c: InternalAlignment(g2,g3)
    c: InternalAlignment(g4,g3)
    c: InternalAlignment(g5,g3)
    c: Block(g3)
    c: Coincident(g6,g0)
    c: Coincident(g6,g3)
    c: Horizontal(g6)
FEATURE [Part::Extrusion] Extrude012  label="caseScrewPillarBracket"
  Base = -> Sketch018
  Dir = (0,0,1)
  DirMode = 2
  FaceMakerClass = Part::FaceMakerBullseye
  LengthFwd = 2.4
  LengthRev = 0
  Placement = pos=(15.76,29,8.8) rot=(0,1,0;0rad)
  Solid = true
  Symmetric = false
FEATURE [Sketcher::SketchObject] Sketch019
  FullyConstrained = true
  sketch-geometry (7):
    g0: LineSegment StartX=0 StartY=0 StartZ=0 EndX=0 EndY=6 EndZ=0
    g1: Circle CenterX=0 CenterY=0 CenterZ=0 NormalX=0 NormalY=0 NormalZ=1 AngleXU=0 Radius=1
    g2: Circle CenterX=8 CenterY=6 CenterZ=0 NormalX=0 NormalY=0 NormalZ=1 AngleXU=0 Radius=1
    g3: BSplineCurve PolesCount=3 KnotsCount=2 Degree=2 IsPeriodic=0
    g4: GeomPoint X=0 Y=0 Z=0
    g5: GeomPoint X=8 Y=6 Z=0
    g6: LineSegment StartX=0 StartY=6 StartZ=0 EndX=8 EndY=6 EndZ=0
  constraints (14):
    c: Coincident(g0,g-1)
    c: Distance(g0) = 6
    c: Vertical(g0)
    c: Coincident(g3,g0)
    c: Weight(g1) = 1
    c: Equal(g1,g2)
    c: InternalAlignment(g1,g3)
    c: InternalAlignment(g2,g3)
    c: InternalAlignment(g4,g3)
    c: InternalAlignment(g5,g3)
    c: Block(g3)
    c: Coincident(g6,g0)
    c: Coincident(g6,g3)
    c: Horizontal(g6)
FEATURE [Part::Extrusion] Extrude013  label="caseScrewPillarBracket001"
  Base = -> Sketch019
  Dir = (0,0,1)
  DirMode = 2
  FaceMakerClass = Part::FaceMakerBullseye
  LengthFwd = 2.4
  LengthRev = 0
  Placement = pos=(15.76,29,60.8) rot=(0,0,1;0rad)
  Solid = true
  Symmetric = false
FEATURE [Sketcher::SketchObject] Sketch020
  FullyConstrained = true
  sketch-geometry (7):
    g0: LineSegment StartX=0 StartY=0 StartZ=0 EndX=0 EndY=6 EndZ=0
    g1: Circle CenterX=0 CenterY=0 CenterZ=0 NormalX=0 NormalY=0 NormalZ=1 AngleXU=0 Radius=1
    g2: Circle CenterX=8 CenterY=6 CenterZ=0 NormalX=0 NormalY=0 NormalZ=1 AngleXU=0 Radius=1
    g3: BSplineCurve PolesCount=3 KnotsCount=2 Degree=2 IsPeriodic=0
    g4: GeomPoint X=0 Y=0 Z=0
    g5: GeomPoint X=8 Y=6 Z=0
    g6: LineSegment StartX=0 StartY=6 StartZ=0 EndX=8 EndY=6 EndZ=0
  constraints (14):
    c: Coincident(g0,g-1)
    c: Distance(g0) = 6
    c: Vertical(g0)
    c: Coincident(g3,g0)
    c: Weight(g1) = 1
    c: Equal(g1,g2)
    c: InternalAlignment(g1,g3)
    c: InternalAlignment(g2,g3)
    c: InternalAlignment(g4,g3)
    c: InternalAlignment(g5,g3)
    c: Block(g3)
    c: Coincident(g6,g0)
    c: Coincident(g6,g3)
    c: Horizontal(g6)
FEATURE [Part::Extrusion] Extrude014  label="caseScrewPillarBracket002"
  Base = -> Sketch020
  Dir = (0,0,1)
  DirMode = 2
  FaceMakerClass = Part::FaceMakerBullseye
  LengthFwd = 2.4
  LengthRev = 0
  Placement = pos=(13.7,29,13.26) rot=(0,-1,0;1.5708rad)
  Solid = true
  Symmetric = false
FEATURE [Sketcher::SketchObject] Sketch021
  FullyConstrained = true
  sketch-geometry (7):
    g0: LineSegment StartX=0 StartY=0 StartZ=0 EndX=0 EndY=6 EndZ=0
    g1: Circle CenterX=0 CenterY=0 CenterZ=0 NormalX=0 NormalY=0 NormalZ=1 AngleXU=0 Radius=1
    g2: Circle CenterX=8 CenterY=6 CenterZ=0 NormalX=0 NormalY=0 NormalZ=1 AngleXU=0 Radius=1
    g3: BSplineCurve PolesCount=3 KnotsCount=2 Degree=2 IsPeriodic=0
    g4: GeomPoint X=0 Y=0 Z=0
    g5: GeomPoint X=8 Y=6 Z=0
    g6: LineSegment StartX=0 StartY=6 StartZ=0 EndX=8 EndY=6 EndZ=0
  constraints (14):
    c: Coincident(g0,g-1)
    c: Distance(g0) = 6
    c: Vertical(g0)
    c: Coincident(g3,g0)
    c: Weight(g1) = 1
    c: Equal(g1,g2)
    c: InternalAlignment(g1,g3)
    c: InternalAlignment(g2,g3)
    c: InternalAlignment(g4,g3)
    c: InternalAlignment(g5,g3)
    c: Block(g3)
    c: Coincident(g6,g0)
    c: Coincident(g6,g3)
    c: Horizontal(g6)
FEATURE [Part::Extrusion] Extrude015  label="caseScrewPillarBracket003"
  Base = -> Sketch021
  Dir = (0,0,1)
  DirMode = 2
  FaceMakerClass = Part::FaceMakerBullseye
  LengthFwd = 2.4
  LengthRev = 0
  Placement = pos=(11.3,29,58.74) rot=(0,1,0;1.5708rad)
  Solid = true
  Symmetric = false
FEATURE [Sketcher::SketchObject] Sketch022
  FullyConstrained = true
  sketch-geometry (7):
    g0: LineSegment StartX=0 StartY=0 StartZ=0 EndX=0 EndY=6 EndZ=0
    g1: Circle CenterX=0 CenterY=0 CenterZ=0 NormalX=0 NormalY=0 NormalZ=1 AngleXU=0 Radius=1
    g2: Circle CenterX=8 CenterY=6 CenterZ=0 NormalX=0 NormalY=0 NormalZ=1 AngleXU=0 Radius=1
    g3: BSplineCurve PolesCount=3 KnotsCount=2 Degree=2 IsPeriodic=0
    g4: GeomPoint X=0 Y=0 Z=0
    g5: GeomPoint X=8 Y=6 Z=0
    g6: LineSegment StartX=0 StartY=6 StartZ=0 EndX=8 EndY=6 EndZ=0
  constraints (14):
    c: Coincident(g0,g-1)
    c: Distance(g0) = 6
    c: Vertical(g0)
    c: Coincident(g3,g0)
    c: Weight(g1) = 1
    c: Equal(g1,g2)
    c: InternalAlignment(g1,g3)
    c: InternalAlignment(g2,g3)
    c: InternalAlignment(g4,g3)
    c: InternalAlignment(g5,g3)
    c: Block(g3)
    c: Coincident(g6,g0)
    c: Coincident(g6,g3)
    c: Horizontal(g6)
FEATURE [Part::Extrusion] Extrude016  label="caseScrewPillarBracket004"
  Base = -> Sketch022
  Dir = (0,0,1)
  DirMode = 2
  FaceMakerClass = Part::FaceMakerBullseye
  LengthFwd = 2.4
  LengthRev = 0
  Placement = pos=(88.3,29,65.23) rot=(0,1,0;1.5708rad)
  Solid = true
  Symmetric = false
FEATURE [Sketcher::SketchObject] Sketch023
  FullyConstrained = true
  sketch-geometry (7):
    g0: LineSegment StartX=0 StartY=0 StartZ=0 EndX=0 EndY=6 EndZ=0
    g1: Circle CenterX=0 CenterY=0 CenterZ=0 NormalX=0 NormalY=0 NormalZ=1 AngleXU=0 Radius=1
    g2: Circle CenterX=8 CenterY=6 CenterZ=0 NormalX=0 NormalY=0 NormalZ=1 AngleXU=0 Radius=1
    g3: BSplineCurve PolesCount=3 KnotsCount=2 Degree=2 IsPeriodic=0
    g4: GeomPoint X=0 Y=0 Z=0
    g5: GeomPoint X=8 Y=6 Z=0
    g6: LineSegment StartX=0 StartY=6 StartZ=0 EndX=8 EndY=6 EndZ=0
  constraints (14):
    c: Coincident(g0,g-1)
    c: Distance(g0) = 6
    c: Vertical(g0)
    c: Coincident(g3,g0)
    c: Weight(g1) = 1
    c: Equal(g1,g2)
    c: InternalAlignment(g1,g3)
    c: InternalAlignment(g2,g3)
    c: InternalAlignment(g4,g3)
    c: InternalAlignment(g5,g3)
    c: Block(g3)
    c: Coincident(g6,g0)
    c: Coincident(g6,g3)
    c: Horizontal(g6)
FEATURE [Part::Extrusion] Extrude017  label="caseScrewPillarBracket005"
  Base = -> Sketch023
  Dir = (0,0,1)
  DirMode = 2
  FaceMakerClass = Part::FaceMakerBullseye
  LengthFwd = 2.4
  LengthRev = 0
  Placement = pos=(90.7,29,6.77) rot=(0,-1,0;1.5708rad)
  Solid = true
  Symmetric = false
FEATURE [Sketcher::SketchObject] Sketch024
  FullyConstrained = true
  sketch-geometry (7):
    g0: LineSegment StartX=0 StartY=0 StartZ=0 EndX=0 EndY=6 EndZ=0
    g1: Circle CenterX=0 CenterY=0 CenterZ=0 NormalX=0 NormalY=0 NormalZ=1 AngleXU=0 Radius=1
    g2: Circle CenterX=8 CenterY=6 CenterZ=0 NormalX=0 NormalY=0 NormalZ=1 AngleXU=0 Radius=1
    g3: BSplineCurve PolesCount=3 KnotsCount=2 Degree=2 IsPeriodic=0
    g4: GeomPoint X=0 Y=0 Z=0
    g5: GeomPoint X=8 Y=6 Z=0
    g6: LineSegment StartX=0 StartY=6 StartZ=0 EndX=8 EndY=6 EndZ=0
  constraints (14):
    c: Coincident(g0,g-1)
    c: Distance(g0) = 6
    c: Vertical(g0)
    c: Coincident(g3,g0)
    c: Weight(g1) = 1
    c: Equal(g1,g2)
    c: InternalAlignment(g1,g3)
    c: InternalAlignment(g2,g3)
    c: InternalAlignment(g4,g3)
    c: InternalAlignment(g5,g3)
    c: Block(g3)
    c: Coincident(g6,g0)
    c: Coincident(g6,g3)
    c: Horizontal(g6)
FEATURE [Part::Extrusion] Extrude018  label="caseScrewPillarBracket006"
  Base = -> Sketch024
  Dir = (0,0,1)
  DirMode = 2
  FaceMakerClass = Part::FaceMakerBullseye
  LengthFwd = 2.4
  LengthRev = 0
  Placement = pos=(103.7,29,6.77) rot=(0,-1,0;1.5708rad)
  Solid = true
  Symmetric = false
FEATURE [Sketcher::SketchObject] Sketch025
  FullyConstrained = true
  sketch-geometry (7):
    g0: LineSegment StartX=0 StartY=0 StartZ=0 EndX=0 EndY=6 EndZ=0
    g1: Circle CenterX=0 CenterY=0 CenterZ=0 NormalX=0 NormalY=0 NormalZ=1 AngleXU=0 Radius=1
    g2: Circle CenterX=8 CenterY=6 CenterZ=0 NormalX=0 NormalY=0 NormalZ=1 AngleXU=0 Radius=1
    g3: BSplineCurve PolesCount=3 KnotsCount=2 Degree=2 IsPeriodic=0
    g4: GeomPoint X=0 Y=0 Z=0
    g5: GeomPoint X=8 Y=6 Z=0
    g6: LineSegment StartX=0 StartY=6 StartZ=0 EndX=8 EndY=6 EndZ=0
  constraints (14):
    c: Coincident(g0,g-1)
    c: Distance(g0) = 6
    c: Vertical(g0)
    c: Coincident(g3,g0)
    c: Weight(g1) = 1
    c: Equal(g1,g2)
    c: InternalAlignment(g1,g3)
    c: InternalAlignment(g2,g3)
    c: InternalAlignment(g4,g3)
    c: InternalAlignment(g5,g3)
    c: Block(g3)
    c: Coincident(g6,g0)
    c: Coincident(g6,g3)
    c: Horizontal(g6)
FEATURE [Part::Extrusion] Extrude019  label="caseScrewPillarBracket007"
  Base = -> Sketch025
  Dir = (0,0,1)
  DirMode = 2
  FaceMakerClass = Part::FaceMakerBullseye
  LengthFwd = 2.4
  LengthRev = 0
  Placement = pos=(101.3,29,65.23) rot=(0,1,0;1.5708rad)
  Solid = true
  Symmetric = false
FEATURE [Part::Box] Box011  label="frontCaseScrewPillarBracket"
  AttacherType = Attacher::AttachEngine3D
  Height = 2.4
  Length = 16
  Placement = pos=(87,28,2.3) rot=(0,0,1;0rad)
  Width = 7
FEATURE [Part::Box] Box012  label="frontCaseScrewPillarBracket001"
  AttacherType = Attacher::AttachEngine3D
  Height = 2.4
  Length = 16
  Placement = pos=(87,28,67.3) rot=(0,0,1;0rad)
  Width = 7
FEATURE [Sketcher::SketchObject] Sketch026
  FullyConstrained = true
  sketch-geometry (17):
    g0: Circle CenterX=-3.5 CenterY=23.5 CenterZ=0 NormalX=0 NormalY=0 NormalZ=1 AngleXU=0 Radius=1
    g1: Circle CenterX=-1 CenterY=15.25 CenterZ=0 NormalX=0 NormalY=0 NormalZ=1 AngleXU=0 Radius=1
    g2: Circle CenterX=-3.5 CenterY=7 CenterZ=0 NormalX=0 NormalY=0 NormalZ=1 AngleXU=0 Radius=1
    g3: BSplineCurve PolesCount=3 KnotsCount=2 Degree=2 IsPeriodic=0
    g4: GeomPoint X=-3.5 Y=23.5 Z=0
    g5: GeomPoint X=-3.5 Y=7 Z=0
    g6: Circle CenterX=-4.8 CenterY=30.5 CenterZ=0 NormalX=0 NormalY=0 NormalZ=1 AngleXU=0 Radius=1
    g7: Circle CenterX=-3.5 CenterY=30.5 CenterZ=0 NormalX=0 NormalY=0 NormalZ=1 AngleXU=0 Radius=1
    g8: Circle CenterX=-3.5 CenterY=29.2 CenterZ=0 NormalX=0 NormalY=0 NormalZ=1 AngleXU=0 Radius=1
    g9: BSplineCurve PolesCount=3 KnotsCount=2 Degree=2 IsPeriodic=0
    g10: GeomPoint X=-4.8 Y=30.5 Z=0
    g11: GeomPoint X=-3.5 Y=29.2 Z=0
    g12: LineSegment StartX=-3.5 StartY=29.2 StartZ=0 EndX=-3.5 EndY=23.5 EndZ=0
    g13: LineSegment StartX=-4.8 StartY=30.5 StartZ=0 EndX=0 EndY=30.5 EndZ=0
    g14: LineSegment StartX=-3.5 StartY=5 StartZ=0 EndX=-3.5 EndY=7 EndZ=0
    g15: LineSegment StartX=0 StartY=5 StartZ=0 EndX=0 EndY=30.5 EndZ=0
    g16: LineSegment StartX=-3.5 StartY=5 StartZ=0 EndX=0 EndY=5 EndZ=0
  constraints (33):
    c: Weight(g0) = 1
    c: Equal(g0,g1)
    c: Equal(g0,g2)
    c: InternalAlignment(g0,g3)
    c: InternalAlignment(g1,g3)
    c: InternalAlignment(g2,g3)
    c: InternalAlignment(g4,g3)
    c: InternalAlignment(g5,g3)
    c: Block(g3)
    c: Weight(g6) = 1
    c: Equal(g6,g7)
    c: Equal(g6,g8)
    c: InternalAlignment(g6,g9)
    c: InternalAlignment(g7,g9)
    c: InternalAlignment(g8,g9)
    c: InternalAlignment(g10,g9)
    c: InternalAlignment(g11,g9)
    c: Block(g9)
    c: Coincident(g12,g9)
    c: Coincident(g12,g3)
    c: Vertical(g12)
    c: Coincident(g13,g9)
    c: Horizontal(g13)
    c: Distance(g13) = 4.8
    c: Coincident(g14,g3)
    c: Vertical(g14)
    c: Coincident(g15,g13)
    c: Vertical(g15)
    c: Tangent(g15,g1)
    c: Distance(g14) = 2
    c: Coincident(g16,g14)
    c: Horizontal(g16)
    c: Coincident(g15,g16)
FEATURE [Part::Feature] Face050
  shape: bbox 4.8 x 25.5 x 2e-07 mm, 1 faces, 0 solids (baked)
FEATURE [Part::Revolution] Revolve054  label="moreFrontCaseScrewPost001"
  Angle = 360
  Axis = (0,1,0)
  Base = (0,0,0)
  FaceMakerClass = Part::FaceMakerBullseye
  Placement = pos=(102.5,4.5,3.5) rot=(0,0,1;0rad)
  Solid = false
  Source = -> Face050
  Symmetric = false
FEATURE [Part::Feature] Face051
  shape: bbox 4.8 x 25.5 x 2e-07 mm, 1 faces, 0 solids (baked)
FEATURE [Part::Revolution] Revolve055  label="moreFrontCaseScrewPost002"
  Angle = 360
  Axis = (0,1,0)
  Base = (0,0,0)
  FaceMakerClass = Part::FaceMakerBullseye
  Placement = pos=(102.5,4.5,68.5) rot=(0,0,1;0rad)
  Solid = false
  Source = -> Face051
  Symmetric = false
FEATURE [Sketcher::SketchObject] Sketch027
  FullyConstrained = true
  sketch-geometry (10):
    g0: LineSegment StartX=-1.6 StartY=4.7 StartZ=0 EndX=-1.6 EndY=1.7 EndZ=0
    g1: LineSegment StartX=-3.5 StartY=4.7 StartZ=0 EndX=-1.6 EndY=4.7 EndZ=0
    g2: LineSegment StartX=-1.6 StartY=1.7 StartZ=0 EndX=-1.6 EndY=1.5 EndZ=0
    g3: LineSegment StartX=-1.6 StartY=1.5 StartZ=0 EndX=-5.2 EndY=1.5 EndZ=0
    g4: Circle CenterX=-3.5 CenterY=4.7 CenterZ=0 NormalX=0 NormalY=0 NormalZ=1 AngleXU=0 Radius=1
    g5: Circle CenterX=-3.59627 CenterY=2.99743 CenterZ=0 NormalX=0 NormalY=0 NormalZ=1 AngleXU=0 Radius=1
    g6: Circle CenterX=-5.2 CenterY=1.5 CenterZ=0 NormalX=0 NormalY=0 NormalZ=1 AngleXU=0 Radius=1
    g7: BSplineCurve PolesCount=3 KnotsCount=2 Degree=2 IsPeriodic=0
    g8: GeomPoint X=-3.5 Y=4.7 Z=0
    g9: GeomPoint X=-5.2 Y=1.5 Z=0
  constraints (23):
    c: Vertical(g0)
    c: Distance(g0) = 3
    c: Coincident(g1,g0)
    c: Horizontal(g1)
    c: Block(g0)
    c: Block(g1)
    c: Coincident(g2,g0)
    c: Vertical(g2)
    c: Distance(g2) = 0.2
    c: Coincident(g3,g2)
    c: Horizontal(g3)
    c: Block(g3)
    c: Coincident(g7,g1)
    c: Weight(g4) = 1
    c: Equal(g4,g5)
    c: Equal(g4,g6)
    c: Coincident(g7,g3)
    c: InternalAlignment(g4,g7)
    c: InternalAlignment(g5,g7)
    c: InternalAlignment(g6,g7)
    c: InternalAlignment(g8,g7)
    c: InternalAlignment(g9,g7)
    c: Block(g7)
FEATURE [Sketcher::SketchObject] Sketch028
  FullyConstrained = true
  sketch-geometry (18):
    g0: LineSegment StartX=0 StartY=3e-16 StartZ=0 EndX=0 EndY=1.7 EndZ=0
    g1: LineSegment StartX=-3.5 StartY=0 StartZ=0 EndX=-3.5 EndY=0.9 EndZ=0
    g2: Circle CenterX=-2.7 CenterY=1.7 CenterZ=0 NormalX=0 NormalY=0 NormalZ=1 AngleXU=0 Radius=1
    g3: Circle CenterX=-3.5 CenterY=1.7 CenterZ=0 NormalX=0 NormalY=0 NormalZ=1 AngleXU=0 Radius=1
    g4: Circle CenterX=-3.5 CenterY=0.9 CenterZ=0 NormalX=0 NormalY=0 NormalZ=1 AngleXU=0 Radius=1
    g5: BSplineCurve PolesCount=3 KnotsCount=2 Degree=2 IsPeriodic=0
    g6: GeomPoint X=-2.7 Y=1.7 Z=0
    g7: GeomPoint X=-3.5 Y=0.9 Z=0
    g8: LineSegment StartX=-3.5 StartY=0 StartZ=0 EndX=-3.5 EndY=-7 EndZ=0
    g9: LineSegment StartX=0 StartY=3e-16 StartZ=0 EndX=0 EndY=-7 EndZ=0
    g10: LineSegment StartX=-3.5 StartY=-7 StartZ=0 EndX=0 EndY=-7 EndZ=0
    g11: LineSegment StartX=-2.7 StartY=1.7 StartZ=0 EndX=-1.6 EndY=1.7 EndZ=0
    g12: LineSegment StartX=0 StartY=1.7 StartZ=0 EndX=0 EndY=4.5 EndZ=0
    g13: LineSegment StartX=0 StartY=4.5 StartZ=0 EndX=0 EndY=10.8 EndZ=0
    g14: LineSegment StartX=0 StartY=10.8 StartZ=0 EndX=-2 EndY=10.8 EndZ=0
    g15: LineSegment StartX=-1.6 StartY=4.7 StartZ=0 EndX=-1.6 EndY=1.7 EndZ=0
    g16: LineSegment StartX=-1.6 StartY=4.7 StartZ=0 EndX=-2 EndY=4.7 EndZ=0
    g17: LineSegment StartX=-2 StartY=4.7 StartZ=0 EndX=-2 EndY=10.8 EndZ=0
  constraints (44):
    c: Vertical(g0)
    c: Vertical(g1)
    c: Distance(g1) = 0.9
    c: Block(g0)
    c: Distance(g0) = 1.7
    c: Weight(g2) = 1
    c: Equal(g2,g3)
    c: Equal(g2,g4)
    c: Coincident(g5,g1)
    c: InternalAlignment(g2,g5)
    c: InternalAlignment(g3,g5)
    c: InternalAlignment(g4,g5)
    c: InternalAlignment(g6,g5)
    c: InternalAlignment(g7,g5)
    c: Block(g5)
    c: Coincident(g8,g1)
    c: Vertical(g8)
    c: Distance(g8) = 7
    c: Vertical(g9)
    c: Equal(g8,g9) = 7
    c: Coincident(g9,g0)
    c: Coincident(g10,g8)
    c: Coincident(g10,g9)
    c: Horizontal(g10)
    c: Coincident(g11,g5)
    c: Horizontal(g11)
    c: Coincident(g12,g0)
    c: Vertical(g12)
    c: Distance(g12) = 2.8
    c: Coincident(g13,g12)
    c: Vertical(g13)
    c: Distance(g13) = 6.3
    c: Coincident(g14,g13)
    c: Horizontal(g14)
    c: Distance(g14) = 2
    c: Vertical(g15)
    c: Distance(g15) = 3
    c: Block(g11)
    c: Coincident(g15,g11)
    c: Coincident(g16,g15)
    c: Horizontal(g16)
    c: Coincident(g17,g16)
    c: Coincident(g17,g14)
    c: Vertical(g17)
FEATURE [Part::Revolution] Revolve040  label="backCaseScrewRetainer001"
  Angle = 360
  Axis = (0,1,0)
  Base = (0,0,0)
  FaceMakerClass = Part::FaceMakerBullseye
  Placement = pos=(12.5,3,10) rot=(0,0,1;0rad)
  Solid = false
  Source = -> Face036
  Symmetric = false
FEATURE [Part::Feature] Face055
  shape: bbox 3.5 x 30.2 x 2e-07 mm, 1 faces, 0 solids (baked)
FEATURE [Part::Revolution] Revolve059  label="backCaseScrewPost"
  Angle = 360
  Axis = (0,1,0)
  Base = (0,0,0)
  FaceMakerClass = Part::FaceMakerBullseye
  Placement = pos=(12.5,4.5,10) rot=(0,0,1;0rad)
  Solid = false
  Source = -> Face055
  Symmetric = false
FEATURE [Part::Feature] Face056
  shape: bbox 3.5 x 30.2 x 2e-07 mm, 1 faces, 0 solids (baked)
FEATURE [Part::Revolution] Revolve060  label="backCaseScrewPost001"
  Angle = 360
  Axis = (0,1,0)
  Base = (0,0,0)
  FaceMakerClass = Part::FaceMakerBullseye
  Placement = pos=(12.5,4.5,62) rot=(0,0,1;0rad)
  Solid = false
  Source = -> Face056
  Symmetric = false
FEATURE [Part::Feature] Face057
  shape: bbox 3.5 x 17.8 x 2e-07 mm, 1 faces, 0 solids (baked)
FEATURE [Part::Revolution] Revolve061  label="removeToCreateScrewAndThreadedInsertHole"
  Angle = 360
  Axis = (0,1,0)
  Base = (0,0,0)
  FaceMakerClass = Part::FaceMakerBullseye
  Placement = pos=(12.5,0,10) rot=(0,0,1;0rad)
  Solid = false
  Source = -> Face057
  Symmetric = false
FEATURE [Part::Feature] Face058
  shape: bbox 3.5 x 17.8 x 2e-07 mm, 1 faces, 0 solids (baked)
FEATURE [Part::Revolution] Revolve062  label="removeToCreateScrewAndThreadedInsertHole001"
  Angle = 360
  Axis = (0,1,0)
  Base = (0,0,0)
  FaceMakerClass = Part::FaceMakerBullseye
  Placement = pos=(12.5,0,62) rot=(0,0,1;0rad)
  Solid = false
  Source = -> Face058
  Symmetric = false
FEATURE [Part::Feature] Face059
  shape: bbox 3.5 x 17.8 x 2e-07 mm, 1 faces, 0 solids (baked)
FEATURE [Part::Revolution] Revolve063  label="removeToCreateScrewAndThreadedInsertHole002"
  Angle = 360
  Axis = (0,1,0)
  Base = (0,0,0)
  FaceMakerClass = Part::FaceMakerBullseye
  Placement = pos=(89.5,0,68.5) rot=(0,0,1;0rad)
  Solid = false
  Source = -> Face059
  Symmetric = false
FEATURE [Part::Feature] Face060
  shape: bbox 3.5 x 17.8 x 2e-07 mm, 1 faces, 0 solids (baked)
FEATURE [Part::Revolution] Revolve064  label="removeToCreateScrewAndThreadedInsertHole003"
  Angle = 360
  Axis = (0,1,0)
  Base = (0,0,0)
  FaceMakerClass = Part::FaceMakerBullseye
  Placement = pos=(89.5,0,3.5) rot=(0,0,1;0rad)
  Solid = false
  Source = -> Face060
  Symmetric = false
FEATURE [Part::Feature] Face061
  shape: bbox 3.5 x 17.8 x 2e-07 mm, 1 faces, 0 solids (baked)
FEATURE [Part::Revolution] Revolve065  label="removeToCreateScrewAndThreadedInsertHole004"
  Angle = 360
  Axis = (0,1,0)
  Base = (0,0,0)
  FaceMakerClass = Part::FaceMakerBullseye
  Placement = pos=(102.5,4.7,3.5) rot=(0,0,1;0rad)
  Solid = false
  Source = -> Face061
  Symmetric = false
FEATURE [Part::Feature] Face062
  shape: bbox 3.5 x 17.8 x 2e-07 mm, 1 faces, 0 solids (baked)
FEATURE [Part::Revolution] Revolve066  label="removeToCreateScrewAndThreadedInsertHole005"
  Angle = 360
  Axis = (0,1,0)
  Base = (0,0,0)
  FaceMakerClass = Part::FaceMakerBullseye
  Placement = pos=(102.5,4.7,68.5) rot=(0,0,1;0rad)
  Solid = false
  Source = -> Face062
  Symmetric = false
FEATURE [Part::MultiFuse] Fusion047  label="makeHoles"
  Shapes = -> [Revolve066,Revolve065,Revolve064,Revolve063,Revolve062,Revolve061]
FEATURE [Part::Feature] Face063
  shape: bbox 3.6 x 3.2 x 2e-07 mm, 1 faces, 0 solids (baked)
FEATURE [Part::Revolution] Revolve067  label="moreFrontCaseScrewRetainer002"
  Angle = 360
  Axis = (0,1,0)
  Base = (0,0,0)
  FaceMakerClass = Part::FaceMakerBullseye
  Placement = pos=(102.5,4.5,68.5) rot=(0,0,1;0rad)
  Solid = false
  Source = -> Face063
  Symmetric = false
FEATURE [Part::Feature] Face064
  shape: bbox 3.6 x 3.2 x 2e-07 mm, 1 faces, 0 solids (baked)
FEATURE [Part::Revolution] Revolve068  label="moreFrontCaseScrewRetainer003"
  Angle = 360
  Axis = (0,1,0)
  Base = (0,0,0)
  FaceMakerClass = Part::FaceMakerBullseye
  Placement = pos=(102.5,4.5,3.5) rot=(0,0,1;0rad)
  Solid = false
  Source = -> Face064
  Symmetric = false
FEATURE [Part::Feature] Face065
  shape: bbox 3.5 x 17.8 x 2e-07 mm, 1 faces, 0 solids (baked)
FEATURE [Part::Revolution] Revolve069  label="removeToCreateScrewAndThreadedInsertHole006"
  Angle = 360
  Axis = (0,1,0)
  Base = (0,0,0)
  FaceMakerClass = Part::FaceMakerBullseye
  Placement = pos=(12.5,0,10) rot=(0,0,1;0rad)
  Solid = false
  Source = -> Face065
  Symmetric = false
FEATURE [Part::Feature] Face066
  shape: bbox 3.5 x 17.8 x 2e-07 mm, 1 faces, 0 solids (baked)
FEATURE [Part::Revolution] Revolve070  label="removeToCreateScrewAndThreadedInsertHole007"
  Angle = 360
  Axis = (0,1,0)
  Base = (0,0,0)
  FaceMakerClass = Part::FaceMakerBullseye
  Placement = pos=(12.5,0,62) rot=(0,0,1;0rad)
  Solid = false
  Source = -> Face066
  Symmetric = false
FEATURE [Part::Feature] Face067
  shape: bbox 3.5 x 17.8 x 2e-07 mm, 1 faces, 0 solids (baked)
FEATURE [Part::Revolution] Revolve071  label="removeToCreateScrewAndThreadedInsertHole008"
  Angle = 360
  Axis = (0,1,0)
  Base = (0,0,0)
  FaceMakerClass = Part::FaceMakerBullseye
  Placement = pos=(89.5,0,68.5) rot=(0,0,1;0rad)
  Solid = false
  Source = -> Face067
  Symmetric = false
FEATURE [Part::Feature] Face068
  shape: bbox 3.5 x 17.8 x 2e-07 mm, 1 faces, 0 solids (baked)
FEATURE [Part::Revolution] Revolve072  label="removeToCreateScrewAndThreadedInsertHole009"
  Angle = 360
  Axis = (0,1,0)
  Base = (0,0,0)
  FaceMakerClass = Part::FaceMakerBullseye
  Placement = pos=(89.5,0,3.5) rot=(0,0,1;0rad)
  Solid = false
  Source = -> Face068
  Symmetric = false
FEATURE [Part::Feature] Face069
  shape: bbox 3.5 x 17.8 x 2e-07 mm, 1 faces, 0 solids (baked)
FEATURE [Part::Feature] Face070
  shape: bbox 3.5 x 17.8 x 2e-07 mm, 1 faces, 0 solids (baked)
FEATURE [Part::Revolution] Revolve073  label="removeToCreateScrewAndThreadedInsertHole010"
  Angle = 360
  Axis = (0,1,0)
  Base = (0,0,0)
  FaceMakerClass = Part::FaceMakerBullseye
  Placement = pos=(102.5,4.7,3.5) rot=(0,0,1;0rad)
  Solid = false
  Source = -> Face069
  Symmetric = false
FEATURE [Part::Revolution] Revolve074  label="removeToCreateScrewAndThreadedInsertHole011"
  Angle = 360
  Axis = (0,1,0)
  Base = (0,0,0)
  FaceMakerClass = Part::FaceMakerBullseye
  Placement = pos=(102.5,4.7,68.5) rot=(0,0,1;0rad)
  Solid = false
  Source = -> Face070
  Symmetric = false
FEATURE [Part::MultiFuse] Fusion048  label="makeHoles001"
  Shapes = -> [Revolve074,Revolve073,Revolve072,Revolve071,Revolve070,Revolve069]
FEATURE [Part::MultiFuse] Fusion049  label="caseScrewRetainers"
  Shapes = -> [Revolve067,Revolve068,Revolve048,Revolve047,Revolve039,Revolve040]
FEATURE [Part::Cut] Cut015  label="caseScrewRetainers001"
  Base = -> Fusion049
  Tool = -> Fusion048
FEATURE [Part::MultiFuse] Fusion050  label="casePillars"
  Shapes = -> [Revolve055,Revolve054,Revolve043,Revolve046,Revolve059,Revolve060]
FEATURE [Part::Feature] Face071 .. Face076  x6 (patterned run collapsed; names and placements below)
  shape: bbox 3.5 x 17.8 x 2e-07 mm, 1 faces, 0 solids (baked)
FEATURE [Part::Revolution] Revolve075  label="removeToCreateScrewAndThreadedInsertHole012"
  Angle = 360
  Axis = (0,1,0)
  Base = (0,0,0)
  FaceMakerClass = Part::FaceMakerBullseye
  Placement = pos=(12.5,0,10) rot=(0,0,1;0rad)
  Solid = false
  Source = -> Face071
  Symmetric = false
FEATURE [Part::Revolution] Revolve076  label="removeToCreateScrewAndThreadedInsertHole013"
  Angle = 360
  Axis = (0,1,0)
  Base = (0,0,0)
  FaceMakerClass = Part::FaceMakerBullseye
  Placement = pos=(12.5,0,62) rot=(0,0,1;0rad)
  Solid = false
  Source = -> Face072
  Symmetric = false
FEATURE [Part::Revolution] Revolve077  label="removeToCreateScrewAndThreadedInsertHole014"
  Angle = 360
  Axis = (0,1,0)
  Base = (0,0,0)
  FaceMakerClass = Part::FaceMakerBullseye
  Placement = pos=(89.5,0,68.5) rot=(0,0,1;0rad)
  Solid = false
  Source = -> Face073
  Symmetric = false
FEATURE [Part::Revolution] Revolve078  label="removeToCreateScrewAndThreadedInsertHole015"
  Angle = 360
  Axis = (0,1,0)
  Base = (0,0,0)
  FaceMakerClass = Part::FaceMakerBullseye
  Placement = pos=(89.5,0,3.5) rot=(0,0,1;0rad)
  Solid = false
  Source = -> Face074
  Symmetric = false
FEATURE [Part::Revolution] Revolve079  label="removeToCreateScrewAndThreadedInsertHole016"
  Angle = 360
  Axis = (0,1,0)
  Base = (0,0,0)
  FaceMakerClass = Part::FaceMakerBullseye
  Placement = pos=(102.5,4.7,3.5) rot=(0,0,1;0rad)
  Solid = false
  Source = -> Face075
  Symmetric = false
FEATURE [Part::Revolution] Revolve080  label="removeToCreateScrewAndThreadedInsertHole017"
  Angle = 360
  Axis = (0,1,0)
  Base = (0,0,0)
  FaceMakerClass = Part::FaceMakerBullseye
  Placement = pos=(102.5,4.7,68.5) rot=(0,0,1;0rad)
  Solid = false
  Source = -> Face076
  Symmetric = false
FEATURE [Part::MultiFuse] Fusion051  label="makeHoles002"
  Shapes = -> [Revolve080,Revolve079,Revolve078,Revolve077,Revolve076,Revolve075]
FEATURE [Part::Cut] Cut016  label="caesPillars"
  Base = -> Fusion050
  Tool = -> Fusion051
FEATURE [Part::Revolution] Revolve009  label="plugHousing016"
  Angle = 360
  Axis = (0,1,0)
  Base = (0,0,0)
  FaceMakerClass = Part::FaceMakerBullseye
  Placement = pos=(0,0,36.15) rot=(0,0,1;0rad)
  Solid = false
  Source = -> Face012
  Symmetric = false
FEATURE [Part::MultiFuse] Fusion014  label="plugHousing023"
  Placement = pos=(0,0,0) rot=(0,0,1;1.5708rad)
  Shapes = -> [Revolve011,Revolve009]
FEATURE [Part::Revolution] Revolve010  label="plugHousing017"
  Angle = 360
  Axis = (0,1,0)
  Base = (0,0,0)
  FaceMakerClass = Part::FaceMakerBullseye
  Placement = pos=(0,0,36.15) rot=(0,0,1;0rad)
  Solid = false
  Source = -> Face014
  Symmetric = false
FEATURE [Part::MultiFuse] Fusion015  label="plugHousing024"
  Placement = pos=(0,0,0) rot=(0,0,1;1.5708rad)
  Shapes = -> [Revolve010,Revolve015]
FEATURE [Part::Revolution] Revolve014  label="plugHousing026"
  Angle = 360
  Axis = (0,1,0)
  Base = (0,0,0)
  FaceMakerClass = Part::FaceMakerBullseye
  Placement = pos=(0,0,36.15) rot=(0,0,1;0rad)
  Solid = false
  Source = -> Face011
  Symmetric = false
FEATURE [Part::Revolution] Revolve013  label="plugHousing025"
  Angle = 360
  Axis = (0,1,0)
  Base = (0,0,0)
  FaceMakerClass = Part::FaceMakerBullseye
  Placement = pos=(0,0,36.15) rot=(0,0,1;0rad)
  Solid = false
  Source = -> Face015
  Symmetric = false
FEATURE [Part::MultiFuse] Fusion016  label="plugHousing028"
  Placement = pos=(0,19,0) rot=(0,0,1;3.14159rad)
  Shapes = -> [Fusion014,Fusion013]
FEATURE [Part::MultiFuse] Fusion011  label="plugHousing018"
  Placement = pos=(0,0,0) rot=(0,0,1;1.5708rad)
  Shapes = -> [Revolve014,Revolve013]
FEATURE [Part::MultiFuse] Fusion012  label="plugHousing019"
  Placement = pos=(0,19,0) rot=(0,0,1;3.14159rad)
  Shapes = -> [Fusion011,Fusion015]
FEATURE [Part::MultiFuse] Fusion017  label="plugHousing029"
  Placement = pos=(122.621,0,-0.15) rot=(0,0,1;0rad)
  Shapes = -> [Fusion016,Fusion012]
FEATURE [Part::MultiFuse] Fusion052  label="casePillarRetainers"
  Shapes = -> [Extrude012,Extrude013,Extrude014,Extrude015,Extrude016,Extrude017,Extrude018,Extrude019,Box011,Box012]
FEATURE [Part::Feature] Face077
  shape: bbox 3.5 x 17.8 x 2e-07 mm, 1 faces, 0 solids (baked)
FEATURE [Part::Revolution] Revolve081  label="removeToCreateScrewAndThreadedInsertHole018"
  Angle = 360
  Axis = (0,1,0)
  Base = (0,0,0)
  FaceMakerClass = Part::FaceMakerBullseye
  Placement = pos=(62.3,30.3,19.7) rot=(0,0,1;0rad)
  Solid = false
  Source = -> Face077
  Symmetric = false
FEATURE [Part::Feature] Face078
  shape: bbox 3.5 x 17.8 x 2e-07 mm, 1 faces, 0 solids (baked)
FEATURE [Part::Revolution] Revolve082  label="removeToCreateScrewAndThreadedInsertHole019"
  Angle = 360
  Axis = (0,1,0)
  Base = (0,0,0)
  FaceMakerClass = Part::FaceMakerBullseye
  Placement = pos=(62.3,30.3,51.7) rot=(0,0,1;0rad)
  Solid = false
  Source = -> Face078
  Symmetric = false
FEATURE [Part::Feature] Face079
  shape: bbox 3.5 x 17.8 x 2e-07 mm, 1 faces, 0 solids (baked)
FEATURE [Part::Revolution] Revolve083  label="removeToCreateScrewAndThreadedInsertHole020"
  Angle = 360
  Axis = (0,1,0)
  Base = (0,0,0)
  FaceMakerClass = Part::FaceMakerBullseye
  Placement = pos=(30.3,30.3,19.7) rot=(0,0,1;0rad)
  Solid = false
  Source = -> Face079
  Symmetric = false
FEATURE [Part::Feature] Face080
  shape: bbox 3.5 x 17.8 x 2e-07 mm, 1 faces, 0 solids (baked)
FEATURE [Part::Revolution] Revolve084  label="removeToCreateScrewAndThreadedInsertHole021"
  Angle = 360
  Axis = (0,1,0)
  Base = (0,0,0)
  FaceMakerClass = Part::FaceMakerBullseye
  Placement = pos=(30.3,30.3,51.7) rot=(0,0,1;0rad)
  Solid = false
  Source = -> Face080
  Symmetric = false
FEATURE [Part::MultiFuse] Fusion053  label="createThreadedInsertHolesForFan"
  Shapes = -> [Revolve081,Revolve082,Revolve083,Revolve084]
FEATURE [Part::Cut] Cut017  label="fanScrewHousing001"
  Base = -> Fusion046
  Tool = -> Fusion053
FEATURE [Part::Feature] Face081
  shape: bbox 3.5 x 17.8 x 2e-07 mm, 1 faces, 0 solids (baked)
FEATURE [Part::Revolution] Revolve085  label="removeToCreateScrewAndThreadedInsertHole022"
  Angle = 360
  Axis = (0,1,0)
  Base = (0,0,0)
  FaceMakerClass = Part::FaceMakerBullseye
  Placement = pos=(62.3,30.3,19.7) rot=(0,0,1;0rad)
  Solid = false
  Source = -> Face081
  Symmetric = false
FEATURE [Part::Feature] Face082
  shape: bbox 3.5 x 17.8 x 2e-07 mm, 1 faces, 0 solids (baked)
FEATURE [Part::Revolution] Revolve086  label="removeToCreateScrewAndThreadedInsertHole023"
  Angle = 360
  Axis = (0,1,0)
  Base = (0,0,0)
  FaceMakerClass = Part::FaceMakerBullseye
  Placement = pos=(62.3,30.3,51.7) rot=(0,0,1;0rad)
  Solid = false
  Source = -> Face082
  Symmetric = false
FEATURE [Part::Feature] Face083
  shape: bbox 3.5 x 17.8 x 2e-07 mm, 1 faces, 0 solids (baked)
FEATURE [Part::Revolution] Revolve087  label="removeToCreateScrewAndThreadedInsertHole024"
  Angle = 360
  Axis = (0,1,0)
  Base = (0,0,0)
  FaceMakerClass = Part::FaceMakerBullseye
  Placement = pos=(30.3,30.3,19.7) rot=(0,0,1;0rad)
  Solid = false
  Source = -> Face083
  Symmetric = false
FEATURE [Part::Feature] Face084
  shape: bbox 3.5 x 17.8 x 2e-07 mm, 1 faces, 0 solids (baked)
FEATURE [Part::Revolution] Revolve088  label="removeToCreateScrewAndThreadedInsertHole025"
  Angle = 360
  Axis = (0,1,0)
  Base = (0,0,0)
  FaceMakerClass = Part::FaceMakerBullseye
  Placement = pos=(30.3,30.3,51.7) rot=(0,0,1;0rad)
  Solid = false
  Source = -> Face084
  Symmetric = false
FEATURE [Part::MultiFuse] Fusion054  label="createThreadedInsertHolesForFan001"
  Shapes = -> [Revolve085,Revolve086,Revolve087,Revolve088]
FEATURE [Part::Cut] Cut018  label="top007"
  Base = -> Fusion040
  Tool = -> Fusion054
FEATURE [Sketcher::SketchObject] Sketch029
  FullyConstrained = false
  Placement = pos=(0,0,0) rot=(1,0,0;1.5708rad)
  sketch-geometry (24):
    g0: ArcOfCircle CenterX=-4 CenterY=-10.5 CenterZ=0 NormalX=0 NormalY=0 NormalZ=1 AngleXU=0 Radius=1.5 StartAngle=6e-16 EndAngle=3.14159
    g1: ArcOfCircle CenterX=-34.2 CenterY=-10.5 CenterZ=0 NormalX=0 NormalY=0 NormalZ=1 AngleXU=0 Radius=1.5 StartAngle=0 EndAngle=3.14159
    g2: ArcOfCircle CenterX=-34.2 CenterY=-27.7 CenterZ=0 NormalX=0 NormalY=0 NormalZ=1 AngleXU=0 Radius=1.5 StartAngle=3.14159 EndAngle=6.28319
    g3: ArcOfCircle CenterX=-4 CenterY=-27.7 CenterZ=0 NormalX=0 NormalY=0 NormalZ=1 AngleXU=0 Radius=1.5 StartAngle=3.1416 EndAngle=6.28319
    g4: ArcOfCircle CenterX=-10 CenterY=-4.3 CenterZ=0 NormalX=0 NormalY=0 NormalZ=1 AngleXU=0 Radius=1.5 StartAngle=2e-16 EndAngle=3.14159
    g5: ArcOfCircle CenterX=-16.1 CenterY=-1.8 CenterZ=0 NormalX=0 NormalY=0 NormalZ=1 AngleXU=0 Radius=1.5 StartAngle=5e-16 EndAngle=3.14159
    g6: ArcOfCircle CenterX=-22.1 CenterY=-1.8 CenterZ=0 NormalX=0 NormalY=0 NormalZ=1 AngleXU=0 Radius=1.5 StartAngle=5e-16 EndAngle=3.14159
    g7: ArcOfCircle CenterX=-28.2 CenterY=-4.3 CenterZ=0 NormalX=0 NormalY=0 NormalZ=1 AngleXU=0 Radius=1.5 StartAngle=2e-16 EndAngle=3.14159
    g8: ArcOfCircle CenterX=-10 CenterY=-33.9 CenterZ=0 NormalX=0 NormalY=0 NormalZ=1 AngleXU=0 Radius=1.5 StartAngle=3.14159 EndAngle=6.28319
    g9: ArcOfCircle CenterX=-16.1 CenterY=-36.4 CenterZ=0 NormalX=0 NormalY=0 NormalZ=1 AngleXU=0 Radius=1.5 StartAngle=3.14159 EndAngle=6.28319
    g10: ArcOfCircle CenterX=-22.1 CenterY=-36.4 CenterZ=0 NormalX=0 NormalY=0 NormalZ=1 AngleXU=0 Radius=1.5 StartAngle=3.14159 EndAngle=6.28319
    g11: ArcOfCircle CenterX=-28.2 CenterY=-33.9 CenterZ=0 NormalX=0 NormalY=0 NormalZ=1 AngleXU=0 Radius=1.5 StartAngle=3.14159 EndAngle=6.28319
    g12: LineSegment StartX=-35.7 StartY=-10.5 StartZ=0 EndX=-35.7 EndY=-27.7 EndZ=0
    g13: LineSegment StartX=-32.7 StartY=-10.5 StartZ=0 EndX=-32.7 EndY=-27.7 EndZ=0
    g14: LineSegment StartX=-29.7 StartY=-33.9 StartZ=0 EndX=-29.7 EndY=-4.3 EndZ=0
    g15: LineSegment StartX=-26.7 StartY=-33.9 StartZ=0 EndX=-26.7 EndY=-4.3 EndZ=0
    g16: LineSegment StartX=-2.5 StartY=-10.5 StartZ=0 EndX=-2.5 EndY=-27.7 EndZ=0
    g17: LineSegment StartX=-8.5 StartY=-4.3 StartZ=0 EndX=-8.5 EndY=-33.9 EndZ=0
    g18: LineSegment StartX=-5.5 StartY=-10.5 StartZ=0 EndX=-5.5 EndY=-27.7 EndZ=0
    g19: LineSegment StartX=-11.5 StartY=-4.3 StartZ=0 EndX=-11.5 EndY=-33.9 EndZ=0
    g20: LineSegment StartX=-14.6 StartY=-1.8 StartZ=0 EndX=-14.6 EndY=-36.4 EndZ=0
    g21: LineSegment StartX=-17.6 StartY=-1.8 StartZ=0 EndX=-17.6 EndY=-36.4 EndZ=0
    g22: LineSegment StartX=-20.6 StartY=-36.4 StartZ=0 EndX=-20.6 EndY=-1.8 EndZ=0
    g23: LineSegment StartX=-23.6 StartY=-1.8 StartZ=0 EndX=-23.6 EndY=-36.4 EndZ=0
  constraints (48):
    c: Block(g0)
    c: Block(g1)
    c: Block(g2)
    c: Block(g3)
    c: Block(g4)
    c: Block(g5)
    c: Block(g6)
    c: Block(g7)
    c: Block(g8)
    c: Block(g9)
    c: Block(g10)
    c: Block(g11)
    c: Coincident(g12,g1)
    c: Coincident(g12,g2)
    c: Vertical(g12)
    c: Coincident(g13,g1)
    c: Coincident(g13,g2)
    c: Vertical(g13)
    c: Coincident(g14,g11)
    c: Coincident(g14,g7)
    c: Vertical(g14)
    c: Coincident(g15,g11)
    c: Coincident(g15,g7)
    c: Vertical(g15)
    c: Coincident(g16,g0)
    c: Coincident(g16,g3)
    c: Vertical(g16)
    c: Coincident(g17,g4)
    c: Coincident(g17,g8)
    c: Vertical(g17)
    c: Coincident(g18,g0)
    c: Coincident(g18,g3)
    c: Vertical(g18)
    c: Coincident(g19,g4)
    c: Coincident(g19,g8)
    c: Vertical(g19)
    c: Coincident(g20,g5)
    c: Coincident(g20,g9)
    c: Vertical(g20)
    c: Coincident(g21,g5)
    c: Coincident(g21,g9)
    c: Vertical(g21)
    c: Coincident(g22,g10)
    c: Coincident(g22,g6)
    c: Vertical(g22)
    c: Coincident(g23,g6)
    c: Coincident(g23,g10)
    c: Vertical(g23)
FEATURE [Part::Extrusion] Extrude020  label="removeToCreateFanGrillHoles"
  Base = -> Sketch029
  Dir = (0,-1,6e-16)
  DirMode = 2
  FaceMakerClass = Part::FaceMakerBullseye
  LengthFwd = 10
  LengthRev = 0
  Placement = pos=(65.4,44,54.82) rot=(0,0,1;0rad)
  Solid = true
  Symmetric = false
FEATURE [Part::MultiFuse] Fusion055  label="top008"
  Shapes = -> [Cut017,Cut018]
FEATURE [Part::Cut] Cut019  label="top009"
  Base = -> Fusion055
  Tool = -> Extrude020
FEATURE [App::MeasureDistance] Distance003  label="Distance: 71.95 mm"
  Distance = 71.9513
  P1 = (117,38,72)
  P2 = (117,38,0.0487319)
FEATURE [Sketcher::SketchObject] Sketch030
  FullyConstrained = true
  Placement = pos=(117,19,0) rot=(0.57735,0.57735,0.57735;2.0944rad)
  sketch-geometry (48):
    g0: LineSegment StartX=-49.19 StartY=69.25 StartZ=0 EndX=-49.19 EndY=66.25 EndZ=0
    g1: LineSegment StartX=-49.19 StartY=63.5 StartZ=0 EndX=-49.19 EndY=60.5 EndZ=0
    g2: LineSegment StartX=-49.19 StartY=57.75 StartZ=0 EndX=-49.19 EndY=54.75 EndZ=0
    g3: LineSegment StartX=-49.19 StartY=52 StartZ=0 EndX=-49.19 EndY=49 EndZ=0
    g4: LineSegment StartX=-49.19 StartY=46.25 StartZ=0 EndX=-49.19 EndY=43.25 EndZ=0
    g5: LineSegment StartX=-49.19 StartY=40.5 StartZ=0 EndX=-49.19 EndY=37.5 EndZ=0
    g6: LineSegment StartX=-49.19 StartY=34.5 StartZ=0 EndX=-49.19 EndY=31.5 EndZ=0
    g7: LineSegment StartX=-49.19 StartY=28.75 StartZ=0 EndX=-49.19 EndY=25.75 EndZ=0
    g8: LineSegment StartX=-49.19 StartY=23 StartZ=0 EndX=-49.19 EndY=20 EndZ=0
    g9: LineSegment StartX=-49.19 StartY=17.25 StartZ=0 EndX=-49.19 EndY=14.25 EndZ=0
    g10: LineSegment StartX=-49.19 StartY=11.5 StartZ=0 EndX=-49.19 EndY=8.5 EndZ=0
    g11: LineSegment StartX=-49.19 StartY=5.75 StartZ=0 EndX=-49.19 EndY=2.75 EndZ=0
    g12: ArcOfCircle CenterX=-1.5 CenterY=67.75 CenterZ=0 NormalX=0 NormalY=0 NormalZ=1 AngleXU=0 Radius=1.5 StartAngle=4.71239 EndAngle=7.85398
    g13: ArcOfCircle CenterX=-1.5 CenterY=62 CenterZ=0 NormalX=0 NormalY=0 NormalZ=1 AngleXU=0 Radius=1.5 StartAngle=4.71239 EndAngle=7.85398
    g14: ArcOfCircle CenterX=-1.5 CenterY=56.25 CenterZ=0 NormalX=0 NormalY=0 NormalZ=1 AngleXU=0 Radius=1.5 StartAngle=4.71239 EndAngle=7.85398
    g15: ArcOfCircle CenterX=-11.49 CenterY=50.5 CenterZ=0 NormalX=0 NormalY=0 NormalZ=1 AngleXU=0 Radius=1.5 StartAngle=4.71239 EndAngle=7.85398
    g16: ArcOfCircle CenterX=-16.28 CenterY=44.75 CenterZ=0 NormalX=0 NormalY=0 NormalZ=1 AngleXU=0 Radius=1.5 StartAngle=4.71239 EndAngle=7.85398
    g17: ArcOfCircle CenterX=-18.2337 CenterY=39 CenterZ=0 NormalX=0 NormalY=0 NormalZ=1 AngleXU=0 Radius=1.5 StartAngle=4.71485 EndAngle=7.85398
    g18: ArcOfCircle CenterX=-16.2837 CenterY=27.25 CenterZ=0 NormalX=0 NormalY=0 NormalZ=1 AngleXU=0 Radius=1.5 StartAngle=4.71485 EndAngle=7.85398
    g19: ArcOfCircle CenterX=-18.2337 CenterY=33 CenterZ=0 NormalX=0 NormalY=0 NormalZ=1 AngleXU=0 Radius=1.5 StartAngle=4.71485 EndAngle=7.85398
    g20: ArcOfCircle CenterX=-11.49 CenterY=21.5 CenterZ=0 NormalX=0 NormalY=0 NormalZ=1 AngleXU=0 Radius=1.5 StartAngle=4.71239 EndAngle=7.85398
    g21: ArcOfCircle CenterX=-1.5 CenterY=4.25 CenterZ=0 NormalX=0 NormalY=0 NormalZ=1 AngleXU=0 Radius=1.5 StartAngle=4.71239 EndAngle=7.85398
    g22: ArcOfCircle CenterX=-1.5 CenterY=10 CenterZ=0 NormalX=0 NormalY=0 NormalZ=1 AngleXU=0 Radius=1.5 StartAngle=4.71239 EndAngle=7.85398
    g23: ArcOfCircle CenterX=-1.5 CenterY=15.75 CenterZ=0 NormalX=0 NormalY=0 NormalZ=1 AngleXU=0 Radius=1.5 StartAngle=4.71239 EndAngle=7.85398
    g24: LineSegment StartX=-49.19 StartY=69.25 StartZ=0 EndX=-1.5 EndY=69.25 EndZ=0
    g25: LineSegment StartX=-49.19 StartY=66.25 StartZ=0 EndX=-1.5 EndY=66.25 EndZ=0
    g26: LineSegment StartX=-49.19 StartY=63.5 StartZ=0 EndX=-1.5 EndY=63.5 EndZ=0
    g27: LineSegment StartX=-49.19 StartY=60.5 StartZ=0 EndX=-1.5 EndY=60.5 EndZ=0
    g28: LineSegment StartX=-49.19 StartY=57.75 StartZ=0 EndX=-1.5 EndY=57.75 EndZ=0
    g29: LineSegment StartX=-49.19 StartY=54.75 StartZ=0 EndX=-1.5 EndY=54.75 EndZ=0
    g30: LineSegment StartX=-49.19 StartY=52 StartZ=0 EndX=-11.49 EndY=52 EndZ=0
    g31: LineSegment StartX=-49.19 StartY=49 StartZ=0 EndX=-11.49 EndY=49 EndZ=0
    g32: LineSegment StartX=-49.19 StartY=46.25 StartZ=0 EndX=-16.28 EndY=46.25 EndZ=0
    g33: LineSegment StartX=-49.19 StartY=43.25 StartZ=0 EndX=-16.28 EndY=43.25 EndZ=0
    g34: LineSegment StartX=-49.19 StartY=40.5 StartZ=0 EndX=-18.2337 EndY=40.5 EndZ=0
    g35: LineSegment StartX=-49.19 StartY=37.5 StartZ=0 EndX=-18.23 EndY=37.5 EndZ=0
    g36: LineSegment StartX=-49.19 StartY=34.5 StartZ=0 EndX=-18.2337 EndY=34.5 EndZ=0
    g37: LineSegment StartX=-49.19 StartY=31.5 StartZ=0 EndX=-18.23 EndY=31.5 EndZ=0
    g38: LineSegment StartX=-49.19 StartY=28.75 StartZ=0 EndX=-16.2837 EndY=28.75 EndZ=0
    g39: LineSegment StartX=-49.19 StartY=25.75 StartZ=0 EndX=-16.28 EndY=25.75 EndZ=0
    g40: LineSegment StartX=-49.19 StartY=23 StartZ=0 EndX=-11.49 EndY=23 EndZ=0
    g41: LineSegment StartX=-49.19 StartY=20 StartZ=0 EndX=-11.49 EndY=20 EndZ=0
    g42: LineSegment StartX=-49.19 StartY=17.25 StartZ=0 EndX=-1.5 EndY=17.25 EndZ=0
    g43: LineSegment StartX=-49.19 StartY=14.25 StartZ=0 EndX=-1.5 EndY=14.25 EndZ=0
    g44: LineSegment StartX=-49.19 StartY=11.5 StartZ=0 EndX=-1.5 EndY=11.5 EndZ=0
    g45: LineSegment StartX=-49.19 StartY=8.5 StartZ=0 EndX=-1.5 EndY=8.5 EndZ=0
    g46: LineSegment StartX=-49.19 StartY=5.75 StartZ=0 EndX=-1.5 EndY=5.75 EndZ=0
    g47: LineSegment StartX=-49.19 StartY=2.75 StartZ=0 EndX=-1.5 EndY=2.75 EndZ=0
  constraints (120):
    c: Vertical(g0)
    c: Distance(g0) = 3
    c: Block(g0)
    c: Vertical(g1)
    c: Distance(g1) = 3
    c: Vertical(g2)
    c: Equal(g0,g2) = 3
    c: Block(g2)
    c: Vertical(g3)
    c: Equal(g1,g3) = 3
    c: Vertical(g4)
    c: Equal(g0,g4) = 3
    c: Block(g4)
    c: Vertical(g5)
    c: Equal(g1,g5) = 3
    c: Vertical(g6)
    c: Equal(g0,g6) = 3
    c: Block(g6)
    c: Vertical(g7)
    c: Equal(g1,g7) = 3
    c: Vertical(g8)
    c: Equal(g0,g8) = 3
    c: Block(g8)
    c: Vertical(g9)
    c: Equal(g1,g9) = 3
    c: Vertical(g10)
    c: Equal(g0,g10) = 3
    c: Block(g10)
    c: Vertical(g11)
    c: Equal(g1,g11) = 3
    c: Block(g12)
    c: Block(g13)
    c: Block(g14)
    c: Block(g15)
    c: Block(g16)
    c: Block(g17)
    c: Block(g18)
    c: Block(g19)
    c: Block(g20)
    c: Block(g21)
    c: Block(g22)
    c: Block(g23)
    c: Block(g11)
    c: Block(g9)
    c: Block(g7)
    c: Block(g5)
    c: Block(g3)
    c: Block(g1)
    c: Coincident(g24,g0)
    c: Coincident(g24,g12)
    c: Horizontal(g24)
    c: Coincident(g25,g0)
    c: Coincident(g25,g12)
    c: Horizontal(g25)
    c: Coincident(g26,g1)
    c: Coincident(g26,g13)
    c: Horizontal(g26)
    c: Coincident(g27,g1)
    c: Coincident(g27,g13)
    c: Horizontal(g27)
    c: Coincident(g28,g2)
    c: Coincident(g28,g14)
    c: Horizontal(g28)
    c: Coincident(g29,g2)
    c: Coincident(g29,g14)
    c: Horizontal(g29)
    c: Coincident(g30,g3)
    c: Coincident(g30,g15)
    c: Horizontal(g30)
    c: Coincident(g31,g3)
    c: Coincident(g31,g15)
    c: Horizontal(g31)
    c: Coincident(g32,g4)
    c: Coincident(g32,g16)
    c: Horizontal(g32)
    c: Coincident(g33,g4)
    c: Coincident(g33,g16)
    c: Horizontal(g33)
    c: Coincident(g34,g5)
    c: Coincident(g34,g17)
    c: Horizontal(g34)
    c: Coincident(g35,g5)
    c: Coincident(g35,g17)
    c: Horizontal(g35)
    c: Coincident(g36,g6)
    c: Coincident(g36,g19)
    c: Horizontal(g36)
    c: Coincident(g37,g6)
    c: Coincident(g37,g19)
    c: Horizontal(g37)
    c: Coincident(g38,g7)
    c: Coincident(g38,g18)
    c: Horizontal(g38)
    c: Coincident(g39,g7)
    c: Coincident(g39,g18)
    c: Horizontal(g39)
    c: Coincident(g40,g8)
    c: Coincident(g40,g20)
    c: Horizontal(g40)
    c: Coincident(g41,g8)
    c: Coincident(g41,g20)
    c: Horizontal(g41)
    c: Coincident(g42,g9)
    c: Coincident(g42,g23)
    c: Horizontal(g42)
    c: Coincident(g43,g9)
    c: Coincident(g43,g23)
    c: Horizontal(g43)
    c: Coincident(g44,g10)
    c: Coincident(g44,g22)
    c: Horizontal(g44)
    c: Coincident(g45,g10)
    c: Coincident(g45,g22)
    c: Horizontal(g45)
    c: Coincident(g46,g11)
    c: Coincident(g46,g21)
    c: Horizontal(g46)
    c: Coincident(g47,g11)
    c: Coincident(g47,g21)
    c: Horizontal(g47)
FEATURE [Sketcher::SketchObject] Sketch031
  FullyConstrained = true
  Placement = pos=(117,19,0) rot=(0.57735,0.57735,0.57735;2.0944rad)
  sketch-geometry (24):
    g0: ArcOfCircle CenterX=-49.19 CenterY=67.75 CenterZ=0 NormalX=0 NormalY=0 NormalZ=1 AngleXU=0 Radius=1.5 StartAngle=1.5708 EndAngle=4.71239
    g1: ArcOfCircle CenterX=-49.19 CenterY=62 CenterZ=0 NormalX=0 NormalY=0 NormalZ=1 AngleXU=0 Radius=1.5 StartAngle=1.5708 EndAngle=4.71239
    g2: ArcOfCircle CenterX=-49.19 CenterY=56.25 CenterZ=0 NormalX=0 NormalY=0 NormalZ=1 AngleXU=0 Radius=1.5 StartAngle=1.5708 EndAngle=4.71239
    g3: ArcOfCircle CenterX=-49.19 CenterY=50.5 CenterZ=0 NormalX=0 NormalY=0 NormalZ=1 AngleXU=0 Radius=1.5 StartAngle=1.5708 EndAngle=4.71239
    g4: ArcOfCircle CenterX=-49.19 CenterY=44.75 CenterZ=0 NormalX=0 NormalY=0 NormalZ=1 AngleXU=0 Radius=1.5 StartAngle=1.5708 EndAngle=4.71239
    g5: ArcOfCircle CenterX=-49.19 CenterY=39 CenterZ=0 NormalX=0 NormalY=0 NormalZ=1 AngleXU=0 Radius=1.5 StartAngle=1.5708 EndAngle=4.71239
    g6: ArcOfCircle CenterX=-49.19 CenterY=33 CenterZ=0 NormalX=0 NormalY=0 NormalZ=1 AngleXU=0 Radius=1.5 StartAngle=1.5708 EndAngle=4.71239
    g7: ArcOfCircle CenterX=-49.19 CenterY=27.25 CenterZ=0 NormalX=0 NormalY=0 NormalZ=1 AngleXU=0 Radius=1.5 StartAngle=1.5708 EndAngle=4.71239
    g8: ArcOfCircle CenterX=-49.19 CenterY=21.5 CenterZ=0 NormalX=0 NormalY=0 NormalZ=1 AngleXU=0 Radius=1.5 StartAngle=1.5708 EndAngle=4.71239
    g9: ArcOfCircle CenterX=-49.19 CenterY=15.75 CenterZ=0 NormalX=0 NormalY=0 NormalZ=1 AngleXU=0 Radius=1.5 StartAngle=1.5708 EndAngle=4.71239
    g10: ArcOfCircle CenterX=-49.19 CenterY=10 CenterZ=0 NormalX=0 NormalY=0 NormalZ=1 AngleXU=0 Radius=1.5 StartAngle=1.5708 EndAngle=4.71239
    g11: ArcOfCircle CenterX=-49.19 CenterY=4.25 CenterZ=0 NormalX=0 NormalY=0 NormalZ=1 AngleXU=0 Radius=1.5 StartAngle=1.5708 EndAngle=4.71239
    g12: LineSegment StartX=-49.19 StartY=69.25 StartZ=0 EndX=-49.19 EndY=66.25 EndZ=0
    g13: LineSegment StartX=-49.19 StartY=63.5 StartZ=0 EndX=-49.19 EndY=60.5 EndZ=0
    g14: LineSegment StartX=-49.19 StartY=57.75 StartZ=0 EndX=-49.19 EndY=54.75 EndZ=0
    g15: LineSegment StartX=-49.19 StartY=52 StartZ=0 EndX=-49.19 EndY=49 EndZ=0
    g16: LineSegment StartX=-49.19 StartY=46.25 StartZ=0 EndX=-49.19 EndY=43.25 EndZ=0
    g17: LineSegment StartX=-49.19 StartY=40.5 StartZ=0 EndX=-49.19 EndY=37.5 EndZ=0
    g18: LineSegment StartX=-49.19 StartY=34.5 StartZ=0 EndX=-49.19 EndY=31.5 EndZ=0
    g19: LineSegment StartX=-49.19 StartY=28.75 StartZ=0 EndX=-49.19 EndY=25.75 EndZ=0
    g20: LineSegment StartX=-49.19 StartY=23 StartZ=0 EndX=-49.19 EndY=20 EndZ=0
    g21: LineSegment StartX=-49.19 StartY=17.25 StartZ=0 EndX=-49.19 EndY=14.25 EndZ=0
    g22: LineSegment StartX=-49.19 StartY=11.5 StartZ=0 EndX=-49.19 EndY=8.5 EndZ=0
    g23: LineSegment StartX=-49.19 StartY=5.75 StartZ=0 EndX=-49.19 EndY=2.75 EndZ=0
  constraints (48):
    c: Block(g0)
    c: Block(g1)
    c: Block(g2)
    c: Block(g3)
    c: Block(g4)
    c: Block(g5)
    c: Block(g6)
    c: Block(g7)
    c: Block(g8)
    c: Block(g9)
    c: Block(g10)
    c: Block(g11)
    c: Coincident(g12,g0)
    c: Coincident(g12,g0)
    c: Vertical(g12)
    c: Vertical(g13)
    c: Coincident(g13,g1)
    c: Vertical(g14)
    c: Coincident(g14,g2)
    c: Vertical(g15)
    c: Coincident(g15,g3)
    c: Vertical(g16)
    c: Coincident(g16,g4)
    c: Vertical(g17)
    c: Coincident(g17,g5)
    c: Vertical(g18)
    c: Coincident(g18,g6)
    c: Vertical(g19)
    c: Coincident(g19,g7)
    c: Vertical(g20)
    c: Coincident(g20,g8)
    c: Vertical(g21)
    c: Coincident(g21,g9)
    c: Vertical(g22)
    c: Coincident(g22,g10)
    c: Vertical(g23)
    c: Coincident(g23,g11)
    c: Block(g23)
    c: Block(g22)
    c: Block(g21)
    c: Block(g20)
    c: Block(g13)
    c: Block(g14)
    c: Block(g15)
    c: Block(g16)
    c: Block(g17)
    c: Block(g18)
    c: Block(g19)
FEATURE [Part::Extrusion] Extrude022
  Base = -> Sketch030
  Dir = (1,-2e-16,2e-16)
  DirMode = 2
  FaceMakerClass = Part::FaceMakerBullseye
  LengthFwd = 19
  LengthRev = 0
  Placement = pos=(-19,0,0) rot=(0,0,1;0rad)
  Solid = true
  Symmetric = false
FEATURE [Part::Fillet] Fillet022
  Base = -> Extrude022
  Edges = 24 edges r=1.49: [Edge6,Edge11,Edge18,Edge23,Edge30,Edge35,Edge42,Edge47,Edge54,Edge59,Edge66,Edge71,Edge78,Edge83,Edge90,Edge95,Edge102,Edge107,Edge114,Edge119,Edge126,Edge131,Edge138,Edge143]
FEATURE [Part::Cut] Cut020  label="top010"
  Base = -> Cut019
  Tool = -> Fillet022
FEATURE [Sketcher::SketchObject] Sketch032
  FullyConstrained = true
  Placement = pos=(117,19,0) rot=(0.57735,0.57735,0.57735;2.0944rad)
  sketch-geometry (48):
    g0: LineSegment StartX=-49.19 StartY=69.25 StartZ=0 EndX=-49.19 EndY=66.25 EndZ=0
    g1: LineSegment StartX=-49.19 StartY=63.5 StartZ=0 EndX=-49.19 EndY=60.5 EndZ=0
    g2: LineSegment StartX=-49.19 StartY=57.75 StartZ=0 EndX=-49.19 EndY=54.75 EndZ=0
    g3: LineSegment StartX=-49.19 StartY=52 StartZ=0 EndX=-49.19 EndY=49 EndZ=0
    g4: LineSegment StartX=-49.19 StartY=46.25 StartZ=0 EndX=-49.19 EndY=43.25 EndZ=0
    g5: LineSegment StartX=-49.19 StartY=40.5 StartZ=0 EndX=-49.19 EndY=37.5 EndZ=0
    g6: LineSegment StartX=-49.19 StartY=34.5 StartZ=0 EndX=-49.19 EndY=31.5 EndZ=0
    g7: LineSegment StartX=-49.19 StartY=28.75 StartZ=0 EndX=-49.19 EndY=25.75 EndZ=0
    g8: LineSegment StartX=-49.19 StartY=23 StartZ=0 EndX=-49.19 EndY=20 EndZ=0
    g9: LineSegment StartX=-49.19 StartY=17.25 StartZ=0 EndX=-49.19 EndY=14.25 EndZ=0
    g10: LineSegment StartX=-49.19 StartY=11.5 StartZ=0 EndX=-49.19 EndY=8.5 EndZ=0
    g11: LineSegment StartX=-49.19 StartY=5.75 StartZ=0 EndX=-49.19 EndY=2.75 EndZ=0
    g12: ArcOfCircle CenterX=-1.5 CenterY=67.75 CenterZ=0 NormalX=0 NormalY=0 NormalZ=1 AngleXU=0 Radius=1.5 StartAngle=4.71239 EndAngle=7.85398
    g13: ArcOfCircle CenterX=-1.5 CenterY=62 CenterZ=0 NormalX=0 NormalY=0 NormalZ=1 AngleXU=0 Radius=1.5 StartAngle=4.71239 EndAngle=7.85398
    g14: ArcOfCircle CenterX=-1.5 CenterY=56.25 CenterZ=0 NormalX=0 NormalY=0 NormalZ=1 AngleXU=0 Radius=1.5 StartAngle=4.71239 EndAngle=7.85398
    g15: ArcOfCircle CenterX=-11.49 CenterY=50.5 CenterZ=0 NormalX=0 NormalY=0 NormalZ=1 AngleXU=0 Radius=1.5 StartAngle=4.71239 EndAngle=7.85398
    g16: ArcOfCircle CenterX=-16.28 CenterY=44.75 CenterZ=0 NormalX=0 NormalY=0 NormalZ=1 AngleXU=0 Radius=1.5 StartAngle=4.71239 EndAngle=7.85398
    g17: ArcOfCircle CenterX=-18.2337 CenterY=39 CenterZ=0 NormalX=0 NormalY=0 NormalZ=1 AngleXU=0 Radius=1.5 StartAngle=4.71485 EndAngle=7.85398
    g18: ArcOfCircle CenterX=-16.2837 CenterY=27.25 CenterZ=0 NormalX=0 NormalY=0 NormalZ=1 AngleXU=0 Radius=1.5 StartAngle=4.71485 EndAngle=7.85398
    g19: ArcOfCircle CenterX=-18.2337 CenterY=33 CenterZ=0 NormalX=0 NormalY=0 NormalZ=1 AngleXU=0 Radius=1.5 StartAngle=4.71485 EndAngle=7.85398
    g20: ArcOfCircle CenterX=-11.49 CenterY=21.5 CenterZ=0 NormalX=0 NormalY=0 NormalZ=1 AngleXU=0 Radius=1.5 StartAngle=4.71239 EndAngle=7.85398
    g21: ArcOfCircle CenterX=-1.5 CenterY=4.25 CenterZ=0 NormalX=0 NormalY=0 NormalZ=1 AngleXU=0 Radius=1.5 StartAngle=4.71239 EndAngle=7.85398
    g22: ArcOfCircle CenterX=-1.5 CenterY=10 CenterZ=0 NormalX=0 NormalY=0 NormalZ=1 AngleXU=0 Radius=1.5 StartAngle=4.71239 EndAngle=7.85398
    g23: ArcOfCircle CenterX=-1.5 CenterY=15.75 CenterZ=0 NormalX=0 NormalY=0 NormalZ=1 AngleXU=0 Radius=1.5 StartAngle=4.71239 EndAngle=7.85398
    g24: LineSegment StartX=-49.19 StartY=69.25 StartZ=0 EndX=-1.5 EndY=69.25 EndZ=0
    g25: LineSegment StartX=-49.19 StartY=66.25 StartZ=0 EndX=-1.5 EndY=66.25 EndZ=0
    g26: LineSegment StartX=-49.19 StartY=63.5 StartZ=0 EndX=-1.5 EndY=63.5 EndZ=0
    g27: LineSegment StartX=-49.19 StartY=60.5 StartZ=0 EndX=-1.5 EndY=60.5 EndZ=0
    g28: LineSegment StartX=-49.19 StartY=57.75 StartZ=0 EndX=-1.5 EndY=57.75 EndZ=0
    g29: LineSegment StartX=-49.19 StartY=54.75 StartZ=0 EndX=-1.5 EndY=54.75 EndZ=0
    g30: LineSegment StartX=-49.19 StartY=52 StartZ=0 EndX=-11.49 EndY=52 EndZ=0
    g31: LineSegment StartX=-49.19 StartY=49 StartZ=0 EndX=-11.49 EndY=49 EndZ=0
    g32: LineSegment StartX=-49.19 StartY=46.25 StartZ=0 EndX=-16.28 EndY=46.25 EndZ=0
    g33: LineSegment StartX=-49.19 StartY=43.25 StartZ=0 EndX=-16.28 EndY=43.25 EndZ=0
    g34: LineSegment StartX=-49.19 StartY=40.5 StartZ=0 EndX=-18.2337 EndY=40.5 EndZ=0
    g35: LineSegment StartX=-49.19 StartY=37.5 StartZ=0 EndX=-18.23 EndY=37.5 EndZ=0
    g36: LineSegment StartX=-49.19 StartY=34.5 StartZ=0 EndX=-18.2337 EndY=34.5 EndZ=0
    g37: LineSegment StartX=-49.19 StartY=31.5 StartZ=0 EndX=-18.23 EndY=31.5 EndZ=0
    g38: LineSegment StartX=-49.19 StartY=28.75 StartZ=0 EndX=-16.2837 EndY=28.75 EndZ=0
    g39: LineSegment StartX=-49.19 StartY=25.75 StartZ=0 EndX=-16.28 EndY=25.75 EndZ=0
    g40: LineSegment StartX=-49.19 StartY=23 StartZ=0 EndX=-11.49 EndY=23 EndZ=0
    g41: LineSegment StartX=-49.19 StartY=20 StartZ=0 EndX=-11.49 EndY=20 EndZ=0
    g42: LineSegment StartX=-49.19 StartY=17.25 StartZ=0 EndX=-1.5 EndY=17.25 EndZ=0
    g43: LineSegment StartX=-49.19 StartY=14.25 StartZ=0 EndX=-1.5 EndY=14.25 EndZ=0
    g44: LineSegment StartX=-49.19 StartY=11.5 StartZ=0 EndX=-1.5 EndY=11.5 EndZ=0
    g45: LineSegment StartX=-49.19 StartY=8.5 StartZ=0 EndX=-1.5 EndY=8.5 EndZ=0
    g46: LineSegment StartX=-49.19 StartY=5.75 StartZ=0 EndX=-1.5 EndY=5.75 EndZ=0
    g47: LineSegment StartX=-49.19 StartY=2.75 StartZ=0 EndX=-1.5 EndY=2.75 EndZ=0
  constraints (120):
    c: Vertical(g0)
    c: Distance(g0) = 3
    c: Block(g0)
    c: Vertical(g1)
    c: Distance(g1) = 3
    c: Vertical(g2)
    c: Equal(g0,g2) = 3
    c: Block(g2)
    c: Vertical(g3)
    c: Equal(g1,g3) = 3
    c: Vertical(g4)
    c: Equal(g0,g4) = 3
    c: Block(g4)
    c: Vertical(g5)
    c: Equal(g1,g5) = 3
    c: Vertical(g6)
    c: Equal(g0,g6) = 3
    c: Block(g6)
    c: Vertical(g7)
    c: Equal(g1,g7) = 3
    c: Vertical(g8)
    c: Equal(g0,g8) = 3
    c: Block(g8)
    c: Vertical(g9)
    c: Equal(g1,g9) = 3
    c: Vertical(g10)
    c: Equal(g0,g10) = 3
    c: Block(g10)
    c: Vertical(g11)
    c: Equal(g1,g11) = 3
    c: Block(g12)
    c: Block(g13)
    c: Block(g14)
    c: Block(g15)
    c: Block(g16)
    c: Block(g17)
    c: Block(g18)
    c: Block(g19)
    c: Block(g20)
    c: Block(g21)
    c: Block(g22)
    c: Block(g23)
    c: Block(g11)
    c: Block(g9)
    c: Block(g7)
    c: Block(g5)
    c: Block(g3)
    c: Block(g1)
    c: Coincident(g24,g0)
    c: Coincident(g24,g12)
    c: Horizontal(g24)
    c: Coincident(g25,g0)
    c: Coincident(g25,g12)
    c: Horizontal(g25)
    c: Coincident(g26,g1)
    c: Coincident(g26,g13)
    c: Horizontal(g26)
    c: Coincident(g27,g1)
    c: Coincident(g27,g13)
    c: Horizontal(g27)
    c: Coincident(g28,g2)
    c: Coincident(g28,g14)
    c: Horizontal(g28)
    c: Coincident(g29,g2)
    c: Coincident(g29,g14)
    c: Horizontal(g29)
    c: Coincident(g30,g3)
    c: Coincident(g30,g15)
    c: Horizontal(g30)
    c: Coincident(g31,g3)
    c: Coincident(g31,g15)
    c: Horizontal(g31)
    c: Coincident(g32,g4)
    c: Coincident(g32,g16)
    c: Horizontal(g32)
    c: Coincident(g33,g4)
    c: Coincident(g33,g16)
    c: Horizontal(g33)
    c: Coincident(g34,g5)
    c: Coincident(g34,g17)
    c: Horizontal(g34)
    c: Coincident(g35,g5)
    c: Coincident(g35,g17)
    c: Horizontal(g35)
    c: Coincident(g36,g6)
    c: Coincident(g36,g19)
    c: Horizontal(g36)
    c: Coincident(g37,g6)
    c: Coincident(g37,g19)
    c: Horizontal(g37)
    c: Coincident(g38,g7)
    c: Coincident(g38,g18)
    c: Horizontal(g38)
    c: Coincident(g39,g7)
    c: Coincident(g39,g18)
    c: Horizontal(g39)
    c: Coincident(g40,g8)
    c: Coincident(g40,g20)
    c: Horizontal(g40)
    c: Coincident(g41,g8)
    c: Coincident(g41,g20)
    c: Horizontal(g41)
    c: Coincident(g42,g9)
    c: Coincident(g42,g23)
    c: Horizontal(g42)
    c: Coincident(g43,g9)
    c: Coincident(g43,g23)
    c: Horizontal(g43)
    c: Coincident(g44,g10)
    c: Coincident(g44,g22)
    c: Horizontal(g44)
    c: Coincident(g45,g10)
    c: Coincident(g45,g22)
    c: Horizontal(g45)
    c: Coincident(g46,g11)
    c: Coincident(g46,g21)
    c: Horizontal(g46)
    c: Coincident(g47,g11)
    c: Coincident(g47,g21)
    c: Horizontal(g47)
FEATURE [Part::Extrusion] Extrude023
  Base = -> Sketch032
  Dir = (1,-2e-16,2e-16)
  DirMode = 2
  FaceMakerClass = Part::FaceMakerBullseye
  LengthFwd = 19
  LengthRev = 0
  Placement = pos=(-19,0,0) rot=(0,0,1;0rad)
  Solid = true
  Symmetric = false
FEATURE [Part::Fillet] Fillet023
  Base = -> Extrude023
  Edges = <same value as first occurrence — deduplicated (x6 in doc)>
  Placement = pos=(0,0.05,0) rot=(0,0,1;0rad)
FEATURE [Part::Cut] Cut014  label="bottom003"
  Base = -> Cut007
  Tool = -> Fusion047
FEATURE [Part::Cut] Cut021  label="bottom004"
  Base = -> Cut014
  Tool = -> Fillet023
FEATURE [Sketcher::SketchObject] Sketch033
  FullyConstrained = true
  Placement = pos=(117,19,0) rot=(0.57735,0.57735,0.57735;2.0944rad)
  sketch-geometry (8):
    g0: LineSegment StartX=-49.19 StartY=69.25 StartZ=0 EndX=-49.19 EndY=66.25 EndZ=0
    g1: LineSegment StartX=-49.19 StartY=5.75 StartZ=0 EndX=-49.19 EndY=2.75 EndZ=0
    g2: ArcOfCircle CenterX=-1.5 CenterY=67.75 CenterZ=0 NormalX=0 NormalY=0 NormalZ=1 AngleXU=0 Radius=1.5 StartAngle=4.71239 EndAngle=7.85398
    g3: ArcOfCircle CenterX=-1.5 CenterY=4.25 CenterZ=0 NormalX=0 NormalY=0 NormalZ=1 AngleXU=0 Radius=1.5 StartAngle=4.71239 EndAngle=7.85398
    g4: LineSegment StartX=-49.19 StartY=69.25 StartZ=0 EndX=-1.5 EndY=69.25 EndZ=0
    g5: LineSegment StartX=-49.19 StartY=66.25 StartZ=0 EndX=-1.5 EndY=66.25 EndZ=0
    g6: LineSegment StartX=-49.19 StartY=5.75 StartZ=0 EndX=-1.5 EndY=5.75 EndZ=0
    g7: LineSegment StartX=-49.19 StartY=2.75 StartZ=0 EndX=-1.5 EndY=2.75 EndZ=0
  constraints (19):
    c: Vertical(g0)
    c: Distance(g0) = 3
    c: Block(g0)
    c: Vertical(g1)
    c: Block(g2)
    c: Block(g3)
    c: Block(g1)
    c: Coincident(g4,g0)
    c: Coincident(g4,g2)
    c: Horizontal(g4)
    c: Coincident(g5,g0)
    c: Coincident(g5,g2)
    c: Horizontal(g5)
    c: Coincident(g6,g1)
    c: Coincident(g6,g3)
    c: Horizontal(g6)
    c: Coincident(g7,g1)
    c: Coincident(g7,g3)
    c: Horizontal(g7)
FEATURE [Sketcher::SketchObject] Sketch034
  FullyConstrained = true
  Placement = pos=(117,19,0) rot=(0.57735,0.57735,0.57735;2.0944rad)
  sketch-geometry (8):
    g0: LineSegment StartX=-49.19 StartY=63.5 StartZ=0 EndX=-49.19 EndY=60.5 EndZ=0
    g1: LineSegment StartX=-49.19 StartY=11.5 StartZ=0 EndX=-49.19 EndY=8.5 EndZ=0
    g2: ArcOfCircle CenterX=-1.5 CenterY=62 CenterZ=0 NormalX=0 NormalY=0 NormalZ=1 AngleXU=0 Radius=1.5 StartAngle=4.71239 EndAngle=7.85398
    g3: ArcOfCircle CenterX=-1.5 CenterY=10 CenterZ=0 NormalX=0 NormalY=0 NormalZ=1 AngleXU=0 Radius=1.5 StartAngle=4.71239 EndAngle=7.85398
    g4: LineSegment StartX=-49.19 StartY=63.5 StartZ=0 EndX=-1.5 EndY=63.5 EndZ=0
    g5: LineSegment StartX=-49.19 StartY=60.5 StartZ=0 EndX=-1.5 EndY=60.5 EndZ=0
    g6: LineSegment StartX=-49.19 StartY=11.5 StartZ=0 EndX=-1.5 EndY=11.5 EndZ=0
    g7: LineSegment StartX=-49.19 StartY=8.5 StartZ=0 EndX=-1.5 EndY=8.5 EndZ=0
  constraints (19):
    c: Vertical(g0)
    c: Distance(g0) = 3
    c: Vertical(g1)
    c: Block(g1)
    c: Block(g2)
    c: Block(g3)
    c: Block(g0)
    c: Coincident(g4,g0)
    c: Coincident(g4,g2)
    c: Horizontal(g4)
    c: Coincident(g5,g0)
    c: Coincident(g5,g2)
    c: Horizontal(g5)
    c: Coincident(g6,g1)
    c: Coincident(g6,g3)
    c: Horizontal(g6)
    c: Coincident(g7,g1)
    c: Coincident(g7,g3)
    c: Horizontal(g7)
FEATURE [Part::Extrusion] Extrude024
  Base = -> Sketch033
  Dir = (1,0,0)
  DirMode = 2
  FaceMakerClass = Part::FaceMakerBullseye
  LengthFwd = 10
  LengthRev = 0
  Solid = true
  Symmetric = false
FEATURE [Part::Extrusion] Extrude025
  Base = -> Sketch034
  Dir = (1,0,0)
  DirMode = 2
  FaceMakerClass = Part::FaceMakerBullseye
  LengthFwd = 10
  LengthRev = 0
  Solid = true
  Symmetric = false
FEATURE [Part::Fillet] Fillet024  label="removeFromtMoreFrontCaseScrewRetainers"
  Base = -> Extrude024
  Edges = 4 edges r=1.49: [Edge6,Edge11,Edge18,Edge23]
  Placement = pos=(-11,0,0) rot=(0,0,1;0rad)
FEATURE [Part::Fillet] Fillet025  label="removeFromtMoreFrontCaseScrewRetainers001"
  Base = -> Extrude025
  Edges = 4 edges r=1.49: [Edge6,Edge11,Edge18,Edge23]
  Placement = pos=(-19,0,0) rot=(0,0,1;0rad)
FEATURE [Part::Cut] Cut022
  Base = -> Cut015
  Tool = -> Fillet025
FEATURE [Part::Cut] Cut023  label="screwRetainers"
  Base = -> Cut022
  Tool = -> Fillet024
FEATURE [Part::MultiFuse] Fusion056  label="bottom005"
  Shapes = -> [Fusion044,Cut021]
FEATURE [Part::MultiFuse] Fusion057  label="casePillars001"
  Shapes = -> [Cut016,Fusion052]
FEATURE [Part::MultiFuse] Fusion058  label="bottom006"
  Shapes = -> [Fusion056,Cut023]
FEATURE [Part::MultiFuse] Fusion059  label="bottom007"
  Shapes = -> [Fusion058,Fillet005]
FEATURE [Part::MultiFuse] Fusion060  label="bottom008"
  Shapes = -> [Fusion059,Fusion]
FEATURE [Part::MultiFuse] Fusion061  label="top011"
  Shapes = -> [Cut006,Cut020]
FEATURE [Part::MultiFuse] Fusion062  label="top012"
  Shapes = -> [Fusion057,Fusion061]
FEATURE [Sketcher::SketchObject] Sketch035  label="topSketch007"
  FullyConstrained = true
  sketch-geometry (6):
    g0: LineSegment StartX=19 StartY=38 StartZ=0 EndX=117 EndY=38 EndZ=0
    g1: ArcOfCircle CenterX=19 CenterY=19 CenterZ=0 NormalX=0 NormalY=0 NormalZ=1 AngleXU=0 Radius=19 StartAngle=1.5708 EndAngle=3.14159
    g2: LineSegment StartX=117 StartY=38 StartZ=0 EndX=117 EndY=19 EndZ=0
    g3: LineSegment StartX=98 StartY=1.0161e-12 StartZ=0 EndX=5.22862e-06 EndY=1.0161e-12 EndZ=0
    g4: LineSegment StartX=5.22862e-06 StartY=19 StartZ=0 EndX=5.22862e-06 EndY=1.0161e-12 EndZ=0
    g5: ArcOfCircle CenterX=98 CenterY=19 CenterZ=0 NormalX=0 NormalY=0 NormalZ=1 AngleXU=0 Radius=19 StartAngle=4.71239 EndAngle=6.28319
  constraints (16):
    c: Horizontal(g0)
    c: Distance(g0) = 98
    c: Coincident(g1,g0)
    c: Block(g1)
    c: Coincident(g2,g0)
    c: Vertical(g2)
    c: Distance(g2) = 19
    c: Horizontal(g3)
    c: Coincident(g4,g1)
    c: Vertical(g4)
    c: Coincident(g3,g4)
    c: Block(g3)
    c: Coincident(g5,g2)
    c: Coincident(g5,g3)
    c: Block(g0)
    c: Block(g5)
FEATURE [Part::Extrusion] Extrude026  label="sideA001"
  Base = -> Sketch035
  Dir = (0,0,1)
  DirMode = 2
  FaceMakerClass = Part::FaceMakerBullseye
  LengthFwd = 3
  LengthRev = 0
  Placement = pos=(0,0,-2.7) rot=(0,0,1;0rad)
  Solid = true
  Symmetric = false
FEATURE [Sketcher::SketchObject] Sketch036  label="topSketch008"
  FullyConstrained = true
  sketch-geometry (6):
    g0: LineSegment StartX=19 StartY=38 StartZ=0 EndX=117 EndY=38 EndZ=0
    g1: ArcOfCircle CenterX=19 CenterY=19 CenterZ=0 NormalX=0 NormalY=0 NormalZ=1 AngleXU=0 Radius=19 StartAngle=1.5708 EndAngle=3.14159
    g2: LineSegment StartX=117 StartY=38 StartZ=0 EndX=117 EndY=19 EndZ=0
    g3: LineSegment StartX=98 StartY=1.0161e-12 StartZ=0 EndX=5.22862e-06 EndY=1.0161e-12 EndZ=0
    g4: LineSegment StartX=5.22862e-06 StartY=19 StartZ=0 EndX=5.22862e-06 EndY=1.0161e-12 EndZ=0
    g5: ArcOfCircle CenterX=98 CenterY=19 CenterZ=0 NormalX=0 NormalY=0 NormalZ=1 AngleXU=0 Radius=19 StartAngle=4.71239 EndAngle=6.28319
  constraints (16):
    c: Horizontal(g0)
    c: Distance(g0) = 98
    c: Coincident(g1,g0)
    c: Block(g1)
    c: Coincident(g2,g0)
    c: Vertical(g2)
    c: Distance(g2) = 19
    c: Horizontal(g3)
    c: Coincident(g4,g1)
    c: Vertical(g4)
    c: Coincident(g3,g4)
    c: Block(g3)
    c: Coincident(g5,g2)
    c: Coincident(g5,g3)
    c: Block(g0)
    c: Block(g5)
FEATURE [Part::Extrusion] Extrude027  label="sideB001"
  Base = -> Sketch036
  Dir = (0,0,1)
  DirMode = 2
  FaceMakerClass = Part::FaceMakerBullseye
  LengthFwd = 3
  LengthRev = 0
  Placement = pos=(0,0,71.7) rot=(0,0,1;0rad)
  Solid = true
  Symmetric = false
FEATURE [Part::MultiFuse] Fusion064  label="removeFromBottom"
  Shapes = -> [Extrude026,Extrude027]
FEATURE [Part::Cut] Cut024  label="bottom009"
  Base = -> Fusion060
  Tool = -> Fusion064
FEATURE [Sketcher::SketchObject] Sketch037  label="topSketch009"
  FullyConstrained = true
  sketch-geometry (8):
    g0: ArcOfCircle CenterX=19 CenterY=19.1201 CenterZ=0 NormalX=0 NormalY=0 NormalZ=1 AngleXU=0 Radius=18.8799 StartAngle=1.5708 EndAngle=3.14793
    g1: LineSegment StartX=0.120501 StartY=19.0004 StartZ=0 EndX=0.120501 EndY=0.000382114 EndZ=0
    g2: LineSegment StartX=19 StartY=38 StartZ=0 EndX=124 EndY=38 EndZ=0
    g3: LineSegment StartX=0.120501 StartY=0.000382114 StartZ=0 EndX=105.121 EndY=0.000382114 EndZ=0
    g4: LineSegment StartX=124 StartY=38 StartZ=0 EndX=125.616 EndY=38 EndZ=0
    g5: LineSegment StartX=105.121 StartY=0.000382114 StartZ=0 EndX=106.736 EndY=0.000382114 EndZ=0
    g6: ArcOfCircle CenterX=106.616 CenterY=19 CenterZ=0 NormalX=0 NormalY=0 NormalZ=1 AngleXU=0 Radius=19 StartAngle=4.71873 EndAngle=6.28319
    g7: LineSegment StartX=125.616 StartY=38 StartZ=0 EndX=125.616 EndY=19 EndZ=0
  constraints (21):
    c: Block(g0)
    c: Coincident(g1,g0)
    c: Vertical(g1)
    c: Horizontal(g2)
    c: Distance(g2) = 105
    c: Coincident(g2,g0)
    c: Distance(g1) = 19
    c: Coincident(g3,g1)
    c: Horizontal(g3)
    c: Distance(g3) = 105
    c: Coincident(g4,g2)
    c: Horizontal(g4)
    c: Distance(g4) = 1.61553
    c: Horizontal(g5)
    c: Equal(g4,g5) = 1.61553
    c: Coincident(g5,g3)
    c: Block(g6)
    c: Coincident(g6,g5)
    c: Coincident(g7,g4)
    c: Coincident(g7,g6)
    c: Vertical(g7)
FEATURE [Part::Extrusion] Extrude028  label="sideB"
  Base = -> Sketch037
  Dir = (0,0,1)
  DirMode = 2
  FaceMakerClass = Part::FaceMakerBullseye
  LengthFwd = 3
  LengthRev = 0
  Placement = pos=(0,0,72) rot=(0,0,1;0rad)
  Solid = true
  Symmetric = false
FEATURE [Sketcher::SketchObject] Sketch038  label="topSketch010"
  FullyConstrained = true
  sketch-geometry (22):
    g0: LineSegment StartX=5.21097e-06 StartY=3 StartZ=0 EndX=5.21097e-06 EndY=19 EndZ=0
    g1: ArcOfCircle CenterX=19 CenterY=19 CenterZ=0 NormalX=0 NormalY=0 NormalZ=1 AngleXU=0 Radius=19 StartAngle=1.5708 EndAngle=3.14159
    g2: ArcOfCircle CenterX=19 CenterY=19 CenterZ=0 NormalX=0 NormalY=0 NormalZ=1 AngleXU=0 Radius=16 StartAngle=1.5708 EndAngle=3.14159
    g3: LineSegment StartX=114 StartY=35 StartZ=0 EndX=19 EndY=35 EndZ=0
    g4: LineSegment StartX=5.21097e-06 StartY=3 StartZ=0 EndX=5.21097e-06 EndY=0 EndZ=0
    g5: LineSegment StartX=3 StartY=0 StartZ=0 EndX=5.21097e-06 EndY=0 EndZ=0
    g6: LineSegment StartX=3 StartY=19 StartZ=0 EndX=3 EndY=0 EndZ=0
    g7: LineSegment StartX=19 StartY=38 StartZ=0 EndX=124 EndY=38 EndZ=0
    g8: Circle CenterX=119 CenterY=35 CenterZ=0 NormalX=0 NormalY=0 NormalZ=1 AngleXU=0 Radius=1
    g9: Circle CenterX=121 CenterY=35 CenterZ=0 NormalX=0 NormalY=0 NormalZ=1 AngleXU=0 Radius=1
    g10: Circle CenterX=121 CenterY=33 CenterZ=0 NormalX=0 NormalY=0 NormalZ=1 AngleXU=0 Radius=1
    g11: BSplineCurve PolesCount=3 KnotsCount=2 Degree=2 IsPeriodic=0
    g12: GeomPoint X=119 Y=35 Z=0
    g13: GeomPoint X=121 Y=33 Z=0
    g14: LineSegment StartX=119 StartY=35 StartZ=0 EndX=114 EndY=35 EndZ=0
    g15: ArcOfCircle CenterX=105 CenterY=19 CenterZ=0 NormalX=0 NormalY=0 NormalZ=1 AngleXU=0 Radius=16 StartAngle=5.60905 EndAngle=6.28319
    g16: LineSegment StartX=121 StartY=33 StartZ=0 EndX=121 EndY=19 EndZ=0
    g17: LineSegment StartX=117.5 StartY=9.01251 StartZ=0 EndX=121.163 EndY=9.0125 EndZ=0
    g18: ArcOfCircle CenterX=105 CenterY=19 CenterZ=0 NormalX=0 NormalY=0 NormalZ=1 AngleXU=0 Radius=20.6155 StartAngle=5.7297 EndAngle=6.28319
    g19: LineSegment StartX=121.163 StartY=9.0125 StartZ=0 EndX=122.538 EndY=8.16329 EndZ=0
    g20: LineSegment StartX=124 StartY=38 StartZ=0 EndX=125.616 EndY=38 EndZ=0
    g21: LineSegment StartX=125.616 StartY=19 StartZ=0 EndX=125.616 EndY=38 EndZ=0
  constraints (49):
    c: Vertical(g0)
    c: Block(g0)
    c: Coincident(g1,g0)
    c: Block(g1)
    c: Coincident(g2,g1)
    c: Block(g2)
    c: Coincident(g3,g2)
    c: Horizontal(g3)
    c: Tangent(g3,g2)
    c: Coincident(g4,g0)
    c: Distance(g4) = 3
    c: Vertical(g4)
    c: Coincident(g5,g4)
    c: Horizontal(g5)
    c: Coincident(g6,g2)
    c: Coincident(g6,g5)
    c: Vertical(g6)
    c: Horizontal(g7)
    c: Distance(g7) = 105
    c: Coincident(g7,g1)
    c: Block(g3)
    c: Weight(g8) = 1
    c: Equal(g8,g9)
    c: Equal(g8,g10)
    c: InternalAlignment(g8,g11)
    c: InternalAlignment(g9,g11)
    c: InternalAlignment(g10,g11)
    c: InternalAlignment(g12,g11)
    c: InternalAlignment(g13,g11)
    c: Block(g11)
    c: Coincident(g14,g11)
    c: Coincident(g14,g3)
    c: Horizontal(g14)
    c: Block(g15)
    c: Coincident(g16,g11)
    c: Coincident(g16,g15)
    c: Vertical(g16)
    c: Distance(g16) = 14
    c: Coincident(g17,g15)
    c: Block(g18)
    c: Coincident(g19,g18)
    c: Coincident(g20,g7)
    c: Horizontal(g20)
    c: Vertical(g21)
    c: Coincident(g20,g21)
    c: Block(g20)
    c: Block(g21)
    c: Block(g19)
    c: Block(g17)
FEATURE [Part::Extrusion] Extrude029
  Base = -> Sketch038
  Dir = (0,0,1)
  DirMode = 2
  FaceMakerClass = Part::FaceMakerBullseye
  LengthFwd = 72
  LengthRev = 0
  Solid = true
  Symmetric = false
FEATURE [Part::Feature] Face085
  shape: bbox 4.8 x 25.5 x 2e-07 mm, 1 faces, 0 solids (baked)
FEATURE [Part::Revolution] Revolve089  label="moreFrontCaseScrewPost003"
  Angle = 360
  Axis = (0,1,0)
  Base = (0,0,0)
  FaceMakerClass = Part::FaceMakerBullseye
  Placement = pos=(109.5,4.5,3.5) rot=(0,0,1;0rad)
  Solid = false
  Source = -> Face085
  Symmetric = false
FEATURE [Part::Feature] Face086
  shape: bbox 4.8 x 25.5 x 2e-07 mm, 1 faces, 0 solids (baked)
FEATURE [Part::Revolution] Revolve090  label="moreFrontCaseScrewPost004"
  Angle = 360
  Axis = (0,1,0)
  Base = (0,0,0)
  FaceMakerClass = Part::FaceMakerBullseye
  Placement = pos=(109.5,4.5,68.5) rot=(0,0,1;0rad)
  Solid = false
  Source = -> Face086
  Symmetric = false
FEATURE [Part::Fillet] Fillet026  label="top013"
  Base = -> Extrude029
  Edges = 1 edges r=2: [Edge35]
FEATURE [Sketcher::SketchObject] Sketch039
  FullyConstrained = true
  sketch-geometry (7):
    g0: LineSegment StartX=0 StartY=0 StartZ=0 EndX=0 EndY=6 EndZ=0
    g1: Circle CenterX=0 CenterY=0 CenterZ=0 NormalX=0 NormalY=0 NormalZ=1 AngleXU=0 Radius=1
    g2: Circle CenterX=8 CenterY=6 CenterZ=0 NormalX=0 NormalY=0 NormalZ=1 AngleXU=0 Radius=1
    g3: BSplineCurve PolesCount=3 KnotsCount=2 Degree=2 IsPeriodic=0
    g4: GeomPoint X=0 Y=0 Z=0
    g5: GeomPoint X=8 Y=6 Z=0
    g6: LineSegment StartX=0 StartY=6 StartZ=0 EndX=8 EndY=6 EndZ=0
  constraints (14):
    c: Coincident(g0,g-1)
    c: Distance(g0) = 6
    c: Vertical(g0)
    c: Coincident(g3,g0)
    c: Weight(g1) = 1
    c: Equal(g1,g2)
    c: InternalAlignment(g1,g3)
    c: InternalAlignment(g2,g3)
    c: InternalAlignment(g4,g3)
    c: InternalAlignment(g5,g3)
    c: Block(g3)
    c: Coincident(g6,g0)
    c: Coincident(g6,g3)
    c: Horizontal(g6)
FEATURE [Sketcher::SketchObject] Sketch040
  FullyConstrained = true
  sketch-geometry (7):
    g0: LineSegment StartX=0 StartY=0 StartZ=0 EndX=0 EndY=6 EndZ=0
    g1: Circle CenterX=0 CenterY=0 CenterZ=0 NormalX=0 NormalY=0 NormalZ=1 AngleXU=0 Radius=1
    g2: Circle CenterX=8 CenterY=6 CenterZ=0 NormalX=0 NormalY=0 NormalZ=1 AngleXU=0 Radius=1
    g3: BSplineCurve PolesCount=3 KnotsCount=2 Degree=2 IsPeriodic=0
    g4: GeomPoint X=0 Y=0 Z=0
    g5: GeomPoint X=8 Y=6 Z=0
    g6: LineSegment StartX=0 StartY=6 StartZ=0 EndX=8 EndY=6 EndZ=0
  constraints (14):
    c: Coincident(g0,g-1)
    c: Distance(g0) = 6
    c: Vertical(g0)
    c: Coincident(g3,g0)
    c: Weight(g1) = 1
    c: Equal(g1,g2)
    c: InternalAlignment(g1,g3)
    c: InternalAlignment(g2,g3)
    c: InternalAlignment(g4,g3)
    c: InternalAlignment(g5,g3)
    c: Block(g3)
    c: Coincident(g6,g0)
    c: Coincident(g6,g3)
    c: Horizontal(g6)
FEATURE [Sketcher::SketchObject] Sketch041
  FullyConstrained = true
  sketch-geometry (7):
    g0: LineSegment StartX=0 StartY=0 StartZ=0 EndX=0 EndY=6 EndZ=0
    g1: Circle CenterX=0 CenterY=0 CenterZ=0 NormalX=0 NormalY=0 NormalZ=1 AngleXU=0 Radius=1
    g2: Circle CenterX=8 CenterY=6 CenterZ=0 NormalX=0 NormalY=0 NormalZ=1 AngleXU=0 Radius=1
    g3: BSplineCurve PolesCount=3 KnotsCount=2 Degree=2 IsPeriodic=0
    g4: GeomPoint X=0 Y=0 Z=0
    g5: GeomPoint X=8 Y=6 Z=0
    g6: LineSegment StartX=0 StartY=6 StartZ=0 EndX=8 EndY=6 EndZ=0
  constraints (14):
    c: Coincident(g0,g-1)
    c: Distance(g0) = 6
    c: Vertical(g0)
    c: Coincident(g3,g0)
    c: Weight(g1) = 1
    c: Equal(g1,g2)
    c: InternalAlignment(g1,g3)
    c: InternalAlignment(g2,g3)
    c: InternalAlignment(g4,g3)
    c: InternalAlignment(g5,g3)
    c: Block(g3)
    c: Coincident(g6,g0)
    c: Coincident(g6,g3)
    c: Horizontal(g6)
FEATURE [Sketcher::SketchObject] Sketch042
  FullyConstrained = true
  sketch-geometry (7):
    g0: LineSegment StartX=0 StartY=0 StartZ=0 EndX=0 EndY=6 EndZ=0
    g1: Circle CenterX=0 CenterY=0 CenterZ=0 NormalX=0 NormalY=0 NormalZ=1 AngleXU=0 Radius=1
    g2: Circle CenterX=8 CenterY=6 CenterZ=0 NormalX=0 NormalY=0 NormalZ=1 AngleXU=0 Radius=1
    g3: BSplineCurve PolesCount=3 KnotsCount=2 Degree=2 IsPeriodic=0
    g4: GeomPoint X=0 Y=0 Z=0
    g5: GeomPoint X=8 Y=6 Z=0
    g6: LineSegment StartX=0 StartY=6 StartZ=0 EndX=8 EndY=6 EndZ=0
  constraints (14):
    c: Coincident(g0,g-1)
    c: Distance(g0) = 6
    c: Vertical(g0)
    c: Coincident(g3,g0)
    c: Weight(g1) = 1
    c: Equal(g1,g2)
    c: InternalAlignment(g1,g3)
    c: InternalAlignment(g2,g3)
    c: InternalAlignment(g4,g3)
    c: InternalAlignment(g5,g3)
    c: Block(g3)
    c: Coincident(g6,g0)
    c: Coincident(g6,g3)
    c: Horizontal(g6)
FEATURE [Part::Extrusion] Extrude030  label="caseScrewPillarBracket008"
  Base = -> Sketch039
  Dir = (0,0,1)
  DirMode = 2
  FaceMakerClass = Part::FaceMakerBullseye
  LengthFwd = 2.4
  LengthRev = 0
  Placement = pos=(15.76,29,8.8) rot=(0,1,0;0rad)
  Solid = true
  Symmetric = false
FEATURE [Part::Extrusion] Extrude031  label="caseScrewPillarBracket009"
  Base = -> Sketch040
  Dir = (0,0,1)
  DirMode = 2
  FaceMakerClass = Part::FaceMakerBullseye
  LengthFwd = 2.4
  LengthRev = 0
  Placement = pos=(15.76,29,60.8) rot=(0,0,1;0rad)
  Solid = true
  Symmetric = false
FEATURE [Part::Extrusion] Extrude032  label="caseScrewPillarBracket010"
  Base = -> Sketch041
  Dir = (0,0,1)
  DirMode = 2
  FaceMakerClass = Part::FaceMakerBullseye
  LengthFwd = 2.4
  LengthRev = 0
  Placement = pos=(13.7,29,13.26) rot=(0,-1,0;1.5708rad)
  Solid = true
  Symmetric = false
FEATURE [Part::Extrusion] Extrude033  label="caseScrewPillarBracket011"
  Base = -> Sketch042
  Dir = (0,0,1)
  DirMode = 2
  FaceMakerClass = Part::FaceMakerBullseye
  LengthFwd = 2.4
  LengthRev = 0
  Placement = pos=(11.3,29,58.74) rot=(0,1,0;1.5708rad)
  Solid = true
  Symmetric = false
FEATURE [Sketcher::SketchObject] Sketch043
  FullyConstrained = true
  sketch-geometry (7):
    g0: LineSegment StartX=0 StartY=0 StartZ=0 EndX=0 EndY=6 EndZ=0
    g1: Circle CenterX=0 CenterY=0 CenterZ=0 NormalX=0 NormalY=0 NormalZ=1 AngleXU=0 Radius=1
    g2: Circle CenterX=8 CenterY=6 CenterZ=0 NormalX=0 NormalY=0 NormalZ=1 AngleXU=0 Radius=1
    g3: BSplineCurve PolesCount=3 KnotsCount=2 Degree=2 IsPeriodic=0
    g4: GeomPoint X=0 Y=0 Z=0
    g5: GeomPoint X=8 Y=6 Z=0
    g6: LineSegment StartX=0 StartY=6 StartZ=0 EndX=8 EndY=6 EndZ=0
  constraints (14):
    c: Coincident(g0,g-1)
    c: Distance(g0) = 6
    c: Vertical(g0)
    c: Coincident(g3,g0)
    c: Weight(g1) = 1
    c: Equal(g1,g2)
    c: InternalAlignment(g1,g3)
    c: InternalAlignment(g2,g3)
    c: InternalAlignment(g4,g3)
    c: InternalAlignment(g5,g3)
    c: Block(g3)
    c: Coincident(g6,g0)
    c: Coincident(g6,g3)
    c: Horizontal(g6)
FEATURE [Part::Extrusion] Extrude034  label="caseScrewPillarBracket012"
  Base = -> Sketch043
  Dir = (0,0,1)
  DirMode = 2
  FaceMakerClass = Part::FaceMakerBullseye
  LengthFwd = 2.4
  LengthRev = 0
  Placement = pos=(88.3,29,65.23) rot=(0,1,0;1.5708rad)
  Solid = true
  Symmetric = false
FEATURE [Sketcher::SketchObject] Sketch044
  FullyConstrained = true
  sketch-geometry (7):
    g0: LineSegment StartX=0 StartY=0 StartZ=0 EndX=0 EndY=6 EndZ=0
    g1: Circle CenterX=0 CenterY=0 CenterZ=0 NormalX=0 NormalY=0 NormalZ=1 AngleXU=0 Radius=1
    g2: Circle CenterX=8 CenterY=6 CenterZ=0 NormalX=0 NormalY=0 NormalZ=1 AngleXU=0 Radius=1
    g3: BSplineCurve PolesCount=3 KnotsCount=2 Degree=2 IsPeriodic=0
    g4: GeomPoint X=0 Y=0 Z=0
    g5: GeomPoint X=8 Y=6 Z=0
    g6: LineSegment StartX=0 StartY=6 StartZ=0 EndX=8 EndY=6 EndZ=0
  constraints (14):
    c: Coincident(g0,g-1)
    c: Distance(g0) = 6
    c: Vertical(g0)
    c: Coincident(g3,g0)
    c: Weight(g1) = 1
    c: Equal(g1,g2)
    c: InternalAlignment(g1,g3)
    c: InternalAlignment(g2,g3)
    c: InternalAlignment(g4,g3)
    c: InternalAlignment(g5,g3)
    c: Block(g3)
    c: Coincident(g6,g0)
    c: Coincident(g6,g3)
    c: Horizontal(g6)
FEATURE [Part::Extrusion] Extrude035  label="caseScrewPillarBracket013"
  Base = -> Sketch044
  Dir = (0,0,1)
  DirMode = 2
  FaceMakerClass = Part::FaceMakerBullseye
  LengthFwd = 2.4
  LengthRev = 0
  Placement = pos=(90.7,29,6.77) rot=(0,-1,0;1.5708rad)
  Solid = true
  Symmetric = false
FEATURE [Sketcher::SketchObject] Sketch045
  FullyConstrained = true
  sketch-geometry (7):
    g0: LineSegment StartX=0 StartY=0 StartZ=0 EndX=0 EndY=6 EndZ=0
    g1: Circle CenterX=0 CenterY=0 CenterZ=0 NormalX=0 NormalY=0 NormalZ=1 AngleXU=0 Radius=1
    g2: Circle CenterX=8 CenterY=6 CenterZ=0 NormalX=0 NormalY=0 NormalZ=1 AngleXU=0 Radius=1
    g3: BSplineCurve PolesCount=3 KnotsCount=2 Degree=2 IsPeriodic=0
    g4: GeomPoint X=0 Y=0 Z=0
    g5: GeomPoint X=8 Y=6 Z=0
    g6: LineSegment StartX=0 StartY=6 StartZ=0 EndX=8 EndY=6 EndZ=0
  constraints (14):
    c: Coincident(g0,g-1)
    c: Distance(g0) = 6
    c: Vertical(g0)
    c: Coincident(g3,g0)
    c: Weight(g1) = 1
    c: Equal(g1,g2)
    c: InternalAlignment(g1,g3)
    c: InternalAlignment(g2,g3)
    c: InternalAlignment(g4,g3)
    c: InternalAlignment(g5,g3)
    c: Block(g3)
    c: Coincident(g6,g0)
    c: Coincident(g6,g3)
    c: Horizontal(g6)
FEATURE [Sketcher::SketchObject] Sketch046
  FullyConstrained = true
  sketch-geometry (7):
    g0: LineSegment StartX=0 StartY=0 StartZ=0 EndX=0 EndY=6 EndZ=0
    g1: Circle CenterX=0 CenterY=0 CenterZ=0 NormalX=0 NormalY=0 NormalZ=1 AngleXU=0 Radius=1
    g2: Circle CenterX=8 CenterY=6 CenterZ=0 NormalX=0 NormalY=0 NormalZ=1 AngleXU=0 Radius=1
    g3: BSplineCurve PolesCount=3 KnotsCount=2 Degree=2 IsPeriodic=0
    g4: GeomPoint X=0 Y=0 Z=0
    g5: GeomPoint X=8 Y=6 Z=0
    g6: LineSegment StartX=0 StartY=6 StartZ=0 EndX=8 EndY=6 EndZ=0
  constraints (14):
    c: Coincident(g0,g-1)
    c: Distance(g0) = 6
    c: Vertical(g0)
    c: Coincident(g3,g0)
    c: Weight(g1) = 1
    c: Equal(g1,g2)
    c: InternalAlignment(g1,g3)
    c: InternalAlignment(g2,g3)
    c: InternalAlignment(g4,g3)
    c: InternalAlignment(g5,g3)
    c: Block(g3)
    c: Coincident(g6,g0)
    c: Coincident(g6,g3)
    c: Horizontal(g6)
FEATURE [Part::Extrusion] Extrude036  label="caseScrewPillarBracket014"
  Base = -> Sketch045
  Dir = (0,0,1)
  DirMode = 2
  FaceMakerClass = Part::FaceMakerBullseye
  LengthFwd = 2.4
  LengthRev = 0
  Placement = pos=(110.7,29,6.77) rot=(0,-1,0;1.5708rad)
  Solid = true
  Symmetric = false
FEATURE [Part::Extrusion] Extrude037  label="caseScrewPillarBracket015"
  Base = -> Sketch046
  Dir = (0,0,1)
  DirMode = 2
  FaceMakerClass = Part::FaceMakerBullseye
  LengthFwd = 2.4
  LengthRev = 0
  Placement = pos=(108.3,29,65.23) rot=(0,1,0;1.5708rad)
  Solid = true
  Symmetric = false
FEATURE [Part::Box] Box013  label="frontCaseScrewPillarBracket002"
  AttacherType = Attacher::AttachEngine3D
  Height = 2.4
  Length = 22
  Placement = pos=(87,28,2.3) rot=(0,0,1;0rad)
  Width = 7
FEATURE [Part::Box] Box014  label="frontCaseScrewPillarBracket003"
  AttacherType = Attacher::AttachEngine3D
  Height = 2.4
  Length = 22
  Placement = pos=(87,28,67.3) rot=(0,0,1;0rad)
  Width = 7
FEATURE [Part::Feature] Face087
  shape: bbox 4.8 x 30.2 x 2e-07 mm, 1 faces, 0 solids (baked)
FEATURE [Part::Revolution] Revolve091  label="frontCaseScrewPost004"
  Angle = 360
  Axis = (0,1,0)
  Base = (0,0,0)
  FaceMakerClass = Part::FaceMakerBullseye
  Placement = pos=(89.5,4.5,3.5) rot=(0,0,1;0rad)
  Solid = false
  Source = -> Face087
  Symmetric = false
FEATURE [Part::Feature] Face088
  shape: bbox 4.8 x 30.2 x 2e-07 mm, 1 faces, 0 solids (baked)
FEATURE [Part::Revolution] Revolve092  label="frontCaseScrewPost005"
  Angle = 360
  Axis = (0,1,0)
  Base = (0,0,0)
  FaceMakerClass = Part::FaceMakerBullseye
  Placement = pos=(89.5,4.5,68.5) rot=(0,0,1;0rad)
  Solid = false
  Source = -> Face088
  Symmetric = false
FEATURE [Part::Feature] Face089
  shape: bbox 3.5 x 30.2 x 2e-07 mm, 1 faces, 0 solids (baked)
FEATURE [Part::Revolution] Revolve093  label="backCaseScrewPost002"
  Angle = 360
  Axis = (0,1,0)
  Base = (0,0,0)
  FaceMakerClass = Part::FaceMakerBullseye
  Placement = pos=(12.5,4.5,10) rot=(0,0,1;0rad)
  Solid = false
  Source = -> Face089
  Symmetric = false
FEATURE [Part::Feature] Face090
  shape: bbox 3.5 x 30.2 x 2e-07 mm, 1 faces, 0 solids (baked)
FEATURE [Part::Revolution] Revolve094  label="backCaseScrewPost003"
  Angle = 360
  Axis = (0,1,0)
  Base = (0,0,0)
  FaceMakerClass = Part::FaceMakerBullseye
  Placement = pos=(12.5,4.5,62) rot=(0,0,1;0rad)
  Solid = false
  Source = -> Face090
  Symmetric = false
FEATURE [Part::Box] Box015  label="Cube011"
  AttacherType = Attacher::AttachEngine3D
  Height = 28.8
  Length = 3
  Placement = pos=(107.3,28,21.6) rot=(0,0,1;0rad)
  Width = 7
FEATURE [Part::Box] Box016  label="Cube012"
  AttacherType = Attacher::AttachEngine3D
  Height = 3
  Length = 7.4
  Placement = pos=(107.3,28,18.6) rot=(0,0,1;0rad)
  Width = 7
FEATURE [Part::Box] Box017  label="Cube013"
  AttacherType = Attacher::AttachEngine3D
  Height = 3
  Length = 7.4
  Placement = pos=(107.3,28,50.4) rot=(0,0,1;0rad)
  Width = 7
FEATURE [Part::Cylinder] Cylinder024
  Angle = 360
  AttacherType = Attacher::AttachEngine3D
  Height = 20
  Placement = pos=(0,0,36.15) rot=(0,0,1;0rad)
  Radius = 14.3
FEATURE [Part::Cylinder] Cylinder025
  Angle = 360
  AttacherType = Attacher::AttachEngine3D
  Height = 10
  Placement = pos=(0,0,36.15) rot=(0,0,1;0rad)
  Radius = 4
FEATURE [Part::MultiFuse] Fusion066  label="removeToCreteHoleForPlugHousing009"
  Placement = pos=(70,19,36) rot=(0,1,0;1.5708rad)
  Shapes = -> [Cylinder024,Cylinder025]
FEATURE [Part::MultiFuse] Fusion065  label="plugHousingBracketHolder002"
  Shapes = -> [Box017,Box015,Box016]
FEATURE [Part::Cut] Cut025  label="plugHousingBracketHolder003"
  Base = -> Fusion065
  Placement = pos=(7,0,0) rot=(0,0,1;0rad)
  Tool = -> Fusion066
FEATURE [Sketcher::SketchObject] Sketch047
  FullyConstrained = false
  Placement = pos=(0,0,0) rot=(1,0,0;1.5708rad)
  sketch-geometry (24):
    g0: ArcOfCircle CenterX=-4 CenterY=-10.5 CenterZ=0 NormalX=0 NormalY=0 NormalZ=1 AngleXU=0 Radius=1.5 StartAngle=6e-16 EndAngle=3.14159
    g1: ArcOfCircle CenterX=-34.2 CenterY=-10.5 CenterZ=0 NormalX=0 NormalY=0 NormalZ=1 AngleXU=0 Radius=1.5 StartAngle=0 EndAngle=3.14159
    g2: ArcOfCircle CenterX=-34.2 CenterY=-27.7 CenterZ=0 NormalX=0 NormalY=0 NormalZ=1 AngleXU=0 Radius=1.5 StartAngle=3.14159 EndAngle=6.28319
    g3: ArcOfCircle CenterX=-4 CenterY=-27.7 CenterZ=0 NormalX=0 NormalY=0 NormalZ=1 AngleXU=0 Radius=1.5 StartAngle=3.1416 EndAngle=6.28319
    g4: ArcOfCircle CenterX=-10 CenterY=-4.3 CenterZ=0 NormalX=0 NormalY=0 NormalZ=1 AngleXU=0 Radius=1.5 StartAngle=2e-16 EndAngle=3.14159
    g5: ArcOfCircle CenterX=-16.1 CenterY=-1.8 CenterZ=0 NormalX=0 NormalY=0 NormalZ=1 AngleXU=0 Radius=1.5 StartAngle=5e-16 EndAngle=3.14159
    g6: ArcOfCircle CenterX=-22.1 CenterY=-1.8 CenterZ=0 NormalX=0 NormalY=0 NormalZ=1 AngleXU=0 Radius=1.5 StartAngle=5e-16 EndAngle=3.14159
    g7: ArcOfCircle CenterX=-28.2 CenterY=-4.3 CenterZ=0 NormalX=0 NormalY=0 NormalZ=1 AngleXU=0 Radius=1.5 StartAngle=2e-16 EndAngle=3.14159
    g8: ArcOfCircle CenterX=-10 CenterY=-33.9 CenterZ=0 NormalX=0 NormalY=0 NormalZ=1 AngleXU=0 Radius=1.5 StartAngle=3.14159 EndAngle=6.28319
    g9: ArcOfCircle CenterX=-16.1 CenterY=-36.4 CenterZ=0 NormalX=0 NormalY=0 NormalZ=1 AngleXU=0 Radius=1.5 StartAngle=3.14159 EndAngle=6.28319
    g10: ArcOfCircle CenterX=-22.1 CenterY=-36.4 CenterZ=0 NormalX=0 NormalY=0 NormalZ=1 AngleXU=0 Radius=1.5 StartAngle=3.14159 EndAngle=6.28319
    g11: ArcOfCircle CenterX=-28.2 CenterY=-33.9 CenterZ=0 NormalX=0 NormalY=0 NormalZ=1 AngleXU=0 Radius=1.5 StartAngle=3.14159 EndAngle=6.28319
    g12: LineSegment StartX=-35.7 StartY=-10.5 StartZ=0 EndX=-35.7 EndY=-27.7 EndZ=0
    g13: LineSegment StartX=-32.7 StartY=-10.5 StartZ=0 EndX=-32.7 EndY=-27.7 EndZ=0
    g14: LineSegment StartX=-29.7 StartY=-33.9 StartZ=0 EndX=-29.7 EndY=-4.3 EndZ=0
    g15: LineSegment StartX=-26.7 StartY=-33.9 StartZ=0 EndX=-26.7 EndY=-4.3 EndZ=0
    g16: LineSegment StartX=-2.5 StartY=-10.5 StartZ=0 EndX=-2.5 EndY=-27.7 EndZ=0
    g17: LineSegment StartX=-8.5 StartY=-4.3 StartZ=0 EndX=-8.5 EndY=-33.9 EndZ=0
    g18: LineSegment StartX=-5.5 StartY=-10.5 StartZ=0 EndX=-5.5 EndY=-27.7 EndZ=0
    g19: LineSegment StartX=-11.5 StartY=-4.3 StartZ=0 EndX=-11.5 EndY=-33.9 EndZ=0
    g20: LineSegment StartX=-14.6 StartY=-1.8 StartZ=0 EndX=-14.6 EndY=-36.4 EndZ=0
    g21: LineSegment StartX=-17.6 StartY=-1.8 StartZ=0 EndX=-17.6 EndY=-36.4 EndZ=0
    g22: LineSegment StartX=-20.6 StartY=-36.4 StartZ=0 EndX=-20.6 EndY=-1.8 EndZ=0
    g23: LineSegment StartX=-23.6 StartY=-1.8 StartZ=0 EndX=-23.6 EndY=-36.4 EndZ=0
  constraints (48):
    c: Block(g0)
    c: Block(g1)
    c: Block(g2)
    c: Block(g3)
    c: Block(g4)
    c: Block(g5)
    c: Block(g6)
    c: Block(g7)
    c: Block(g8)
    c: Block(g9)
    c: Block(g10)
    c: Block(g11)
    c: Coincident(g12,g1)
    c: Coincident(g12,g2)
    c: Vertical(g12)
    c: Coincident(g13,g1)
    c: Coincident(g13,g2)
    c: Vertical(g13)
    c: Coincident(g14,g11)
    c: Coincident(g14,g7)
    c: Vertical(g14)
    c: Coincident(g15,g11)
    c: Coincident(g15,g7)
    c: Vertical(g15)
    c: Coincident(g16,g0)
    c: Coincident(g16,g3)
    c: Vertical(g16)
    c: Coincident(g17,g4)
    c: Coincident(g17,g8)
    c: Vertical(g17)
    c: Coincident(g18,g0)
    c: Coincident(g18,g3)
    c: Vertical(g18)
    c: Coincident(g19,g4)
    c: Coincident(g19,g8)
    c: Vertical(g19)
    c: Coincident(g20,g5)
    c: Coincident(g20,g9)
    c: Vertical(g20)
    c: Coincident(g21,g5)
    c: Coincident(g21,g9)
    c: Vertical(g21)
    c: Coincident(g22,g10)
    c: Coincident(g22,g6)
    c: Vertical(g22)
    c: Coincident(g23,g6)
    c: Coincident(g23,g10)
    c: Vertical(g23)
FEATURE [Part::Extrusion] Extrude038  label="removeToCreateFanGrillHoles001"
  Base = -> Sketch047
  Dir = (0,-1,6e-16)
  DirMode = 2
  FaceMakerClass = Part::FaceMakerBullseye
  LengthFwd = 10
  LengthRev = 0
  Placement = pos=(65.4,44,54.82) rot=(0,0,1;0rad)
  Solid = true
  Symmetric = false
FEATURE [Part::Feature] Wire004
  shape: bbox 11 x 5.2 x 2e-07 mm, 0 faces, 0 solids (baked)
FEATURE [Part::Revolution] Revolve095
  Angle = 360
  Axis = (0,1,0)
  Base = (0,0,0)
  FaceMakerClass = Part::FaceMakerBullseye
  Placement = pos=(30.3,38,19.7) rot=(0,0,1;0rad)
  Solid = true
  Source = -> Wire004
  Symmetric = false
FEATURE [Part::Feature] Wire005
  shape: bbox 11 x 5.2 x 2e-07 mm, 0 faces, 0 solids (baked)
FEATURE [Part::Revolution] Revolve096
  Angle = 360
  Axis = (0,1,0)
  Base = (0,0,0)
  FaceMakerClass = Part::FaceMakerBullseye
  Placement = pos=(30.3,38,51.7) rot=(0,0,1;0rad)
  Solid = true
  Source = -> Wire005
  Symmetric = false
FEATURE [Part::Feature] Wire006
  shape: bbox 11 x 5.2 x 2e-07 mm, 0 faces, 0 solids (baked)
FEATURE [Part::Revolution] Revolve097
  Angle = 360
  Axis = (0,1,0)
  Base = (0,0,0)
  FaceMakerClass = Part::FaceMakerBullseye
  Placement = pos=(62.3,38,51.7) rot=(0,0,1;0rad)
  Solid = true
  Source = -> Wire006
  Symmetric = false
FEATURE [Part::Feature] Wire007
  shape: bbox 11 x 5.2 x 2e-07 mm, 0 faces, 0 solids (baked)
FEATURE [Part::Revolution] Revolve098
  Angle = 360
  Axis = (0,1,0)
  Base = (0,0,0)
  FaceMakerClass = Part::FaceMakerBullseye
  Placement = pos=(62.3,38,19.7) rot=(0,0,1;0rad)
  Solid = true
  Source = -> Wire007
  Symmetric = false
FEATURE [Part::MultiFuse] Fusion067  label="fanScrewHousing002"
  Shapes = -> [Revolve098,Revolve097,Revolve096,Revolve095]
FEATURE [Part::Feature] Face091 .. Face094  x4 (patterned run collapsed; names and placements below)
  shape: bbox 3.5 x 17.8 x 2e-07 mm, 1 faces, 0 solids (baked)
FEATURE [Part::Revolution] Revolve099  label="removeToCreateScrewAndThreadedInsertHole026"
  Angle = 360
  Axis = (0,1,0)
  Base = (0,0,0)
  FaceMakerClass = Part::FaceMakerBullseye
  Placement = pos=(62.3,30.3,19.7) rot=(0,0,1;0rad)
  Solid = false
  Source = -> Face091
  Symmetric = false
FEATURE [Part::Revolution] Revolve100  label="removeToCreateScrewAndThreadedInsertHole027"
  Angle = 360
  Axis = (0,1,0)
  Base = (0,0,0)
  FaceMakerClass = Part::FaceMakerBullseye
  Placement = pos=(62.3,30.3,51.7) rot=(0,0,1;0rad)
  Solid = false
  Source = -> Face092
  Symmetric = false
FEATURE [Part::Revolution] Revolve101  label="removeToCreateScrewAndThreadedInsertHole028"
  Angle = 360
  Axis = (0,1,0)
  Base = (0,0,0)
  FaceMakerClass = Part::FaceMakerBullseye
  Placement = pos=(30.3,30.3,19.7) rot=(0,0,1;0rad)
  Solid = false
  Source = -> Face093
  Symmetric = false
FEATURE [Part::Revolution] Revolve102  label="removeToCreateScrewAndThreadedInsertHole029"
  Angle = 360
  Axis = (0,1,0)
  Base = (0,0,0)
  FaceMakerClass = Part::FaceMakerBullseye
  Placement = pos=(30.3,30.3,51.7) rot=(0,0,1;0rad)
  Solid = false
  Source = -> Face094
  Symmetric = false
FEATURE [Part::MultiFuse] Fusion068  label="createThreadedInsertHolesForFan002"
  Shapes = -> [Revolve099,Revolve100,Revolve101,Revolve102]
FEATURE [Part::Cut] Cut026  label="fanScrewHousing003"
  Base = -> Fusion067
  Tool = -> Fusion068
FEATURE [Sketcher::SketchObject] Sketch048
  FullyConstrained = false
  Placement = pos=(0,0,0) rot=(1,0,0;1.5708rad)
  sketch-geometry (24):
    g0: ArcOfCircle CenterX=-4 CenterY=-10.5 CenterZ=0 NormalX=0 NormalY=0 NormalZ=1 AngleXU=0 Radius=1.5 StartAngle=6e-16 EndAngle=3.14159
    g1: ArcOfCircle CenterX=-34.2 CenterY=-10.5 CenterZ=0 NormalX=0 NormalY=0 NormalZ=1 AngleXU=0 Radius=1.5 StartAngle=0 EndAngle=3.14159
    g2: ArcOfCircle CenterX=-34.2 CenterY=-27.7 CenterZ=0 NormalX=0 NormalY=0 NormalZ=1 AngleXU=0 Radius=1.5 StartAngle=3.14159 EndAngle=6.28319
    g3: ArcOfCircle CenterX=-4 CenterY=-27.7 CenterZ=0 NormalX=0 NormalY=0 NormalZ=1 AngleXU=0 Radius=1.5 StartAngle=3.1416 EndAngle=6.28319
    g4: ArcOfCircle CenterX=-10 CenterY=-4.3 CenterZ=0 NormalX=0 NormalY=0 NormalZ=1 AngleXU=0 Radius=1.5 StartAngle=2e-16 EndAngle=3.14159
    g5: ArcOfCircle CenterX=-16.1 CenterY=-1.8 CenterZ=0 NormalX=0 NormalY=0 NormalZ=1 AngleXU=0 Radius=1.5 StartAngle=5e-16 EndAngle=3.14159
    g6: ArcOfCircle CenterX=-22.1 CenterY=-1.8 CenterZ=0 NormalX=0 NormalY=0 NormalZ=1 AngleXU=0 Radius=1.5 StartAngle=5e-16 EndAngle=3.14159
    g7: ArcOfCircle CenterX=-28.2 CenterY=-4.3 CenterZ=0 NormalX=0 NormalY=0 NormalZ=1 AngleXU=0 Radius=1.5 StartAngle=2e-16 EndAngle=3.14159
    g8: ArcOfCircle CenterX=-10 CenterY=-33.9 CenterZ=0 NormalX=0 NormalY=0 NormalZ=1 AngleXU=0 Radius=1.5 StartAngle=3.14159 EndAngle=6.28319
    g9: ArcOfCircle CenterX=-16.1 CenterY=-36.4 CenterZ=0 NormalX=0 NormalY=0 NormalZ=1 AngleXU=0 Radius=1.5 StartAngle=3.14159 EndAngle=6.28319
    g10: ArcOfCircle CenterX=-22.1 CenterY=-36.4 CenterZ=0 NormalX=0 NormalY=0 NormalZ=1 AngleXU=0 Radius=1.5 StartAngle=3.14159 EndAngle=6.28319
    g11: ArcOfCircle CenterX=-28.2 CenterY=-33.9 CenterZ=0 NormalX=0 NormalY=0 NormalZ=1 AngleXU=0 Radius=1.5 StartAngle=3.14159 EndAngle=6.28319
    g12: LineSegment StartX=-35.7 StartY=-10.5 StartZ=0 EndX=-35.7 EndY=-27.7 EndZ=0
    g13: LineSegment StartX=-32.7 StartY=-10.5 StartZ=0 EndX=-32.7 EndY=-27.7 EndZ=0
    g14: LineSegment StartX=-29.7 StartY=-33.9 StartZ=0 EndX=-29.7 EndY=-4.3 EndZ=0
    g15: LineSegment StartX=-26.7 StartY=-33.9 StartZ=0 EndX=-26.7 EndY=-4.3 EndZ=0
    g16: LineSegment StartX=-2.5 StartY=-10.5 StartZ=0 EndX=-2.5 EndY=-27.7 EndZ=0
    g17: LineSegment StartX=-8.5 StartY=-4.3 StartZ=0 EndX=-8.5 EndY=-33.9 EndZ=0
    g18: LineSegment StartX=-5.5 StartY=-10.5 StartZ=0 EndX=-5.5 EndY=-27.7 EndZ=0
    g19: LineSegment StartX=-11.5 StartY=-4.3 StartZ=0 EndX=-11.5 EndY=-33.9 EndZ=0
    g20: LineSegment StartX=-14.6 StartY=-1.8 StartZ=0 EndX=-14.6 EndY=-36.4 EndZ=0
    g21: LineSegment StartX=-17.6 StartY=-1.8 StartZ=0 EndX=-17.6 EndY=-36.4 EndZ=0
    g22: LineSegment StartX=-20.6 StartY=-36.4 StartZ=0 EndX=-20.6 EndY=-1.8 EndZ=0
    g23: LineSegment StartX=-23.6 StartY=-1.8 StartZ=0 EndX=-23.6 EndY=-36.4 EndZ=0
  constraints (48):
    c: Block(g0)
    c: Block(g1)
    c: Block(g2)
    c: Block(g3)
    c: Block(g4)
    c: Block(g5)
    c: Block(g6)
    c: Block(g7)
    c: Block(g8)
    c: Block(g9)
    c: Block(g10)
    c: Block(g11)
    c: Coincident(g12,g1)
    c: Coincident(g12,g2)
    c: Vertical(g12)
    c: Coincident(g13,g1)
    c: Coincident(g13,g2)
    c: Vertical(g13)
    c: Coincident(g14,g11)
    c: Coincident(g14,g7)
    c: Vertical(g14)
    c: Coincident(g15,g11)
    c: Coincident(g15,g7)
    c: Vertical(g15)
    c: Coincident(g16,g0)
    c: Coincident(g16,g3)
    c: Vertical(g16)
    c: Coincident(g17,g4)
    c: Coincident(g17,g8)
    c: Vertical(g17)
    c: Coincident(g18,g0)
    c: Coincident(g18,g3)
    c: Vertical(g18)
    c: Coincident(g19,g4)
    c: Coincident(g19,g8)
    c: Vertical(g19)
    c: Coincident(g20,g5)
    c: Coincident(g20,g9)
    c: Vertical(g20)
    c: Coincident(g21,g5)
    c: Coincident(g21,g9)
    c: Vertical(g21)
    c: Coincident(g22,g10)
    c: Coincident(g22,g6)
    c: Vertical(g22)
    c: Coincident(g23,g6)
    c: Coincident(g23,g10)
    c: Vertical(g23)
FEATURE [Part::Extrusion] Extrude039  label="removeToCreateFanGrillHoles002"
  Base = -> Sketch048
  Dir = (0,-1,6e-16)
  DirMode = 2
  FaceMakerClass = Part::FaceMakerBullseye
  LengthFwd = 10
  LengthRev = 0
  Placement = pos=(65.4,44,54.82) rot=(0,0,1;0rad)
  Solid = true
  Symmetric = false
FEATURE [Part::Cut] Cut027  label="fanScrewHousing004"
  Base = -> Cut026
  Tool = -> Extrude038
FEATURE [Part::Cut] Cut028  label="top014"
  Base = -> Fillet026
  Tool = -> Extrude039
FEATURE [Part::Feature] Face095 .. Face098  x4 (patterned run collapsed; names and placements below)
  shape: bbox 3.5 x 17.8 x 2e-07 mm, 1 faces, 0 solids (baked)
FEATURE [Part::Revolution] Revolve103  label="removeToCreateScrewAndThreadedInsertHole030"
  Angle = 360
  Axis = (0,1,0)
  Base = (0,0,0)
  FaceMakerClass = Part::FaceMakerBullseye
  Placement = pos=(62.3,30.3,19.7) rot=(0,0,1;0rad)
  Solid = false
  Source = -> Face095
  Symmetric = false
FEATURE [Part::Revolution] Revolve104  label="removeToCreateScrewAndThreadedInsertHole031"
  Angle = 360
  Axis = (0,1,0)
  Base = (0,0,0)
  FaceMakerClass = Part::FaceMakerBullseye
  Placement = pos=(62.3,30.3,51.7) rot=(0,0,1;0rad)
  Solid = false
  Source = -> Face096
  Symmetric = false
FEATURE [Part::Revolution] Revolve105  label="removeToCreateScrewAndThreadedInsertHole032"
  Angle = 360
  Axis = (0,1,0)
  Base = (0,0,0)
  FaceMakerClass = Part::FaceMakerBullseye
  Placement = pos=(30.3,30.3,19.7) rot=(0,0,1;0rad)
  Solid = false
  Source = -> Face097
  Symmetric = false
FEATURE [Part::Revolution] Revolve106  label="removeToCreateScrewAndThreadedInsertHole033"
  Angle = 360
  Axis = (0,1,0)
  Base = (0,0,0)
  FaceMakerClass = Part::FaceMakerBullseye
  Placement = pos=(30.3,30.3,51.7) rot=(0,0,1;0rad)
  Solid = false
  Source = -> Face098
  Symmetric = false
FEATURE [Part::MultiFuse] Fusion069  label="createThreadedInsertHolesForFan003"
  Shapes = -> [Revolve103,Revolve104,Revolve105,Revolve106]
FEATURE [Part::Cut] Cut029  label="top015"
  Base = -> Cut028
  Tool = -> Fusion054
FEATURE [Part::Cut] Cut030  label="fanScrewHousing005"
  Base = -> Cut027
  Tool = -> Fusion069
FEATURE [Part::Cylinder] Cylinder026  label="removeToCreteHoleForPlugHousing010"
  Angle = 360
  AttacherType = Attacher::AttachEngine3D
  Height = 20
  Placement = pos=(-2,19,36) rot=(0,1,0;1.5708rad)
  Radius = 14.3
FEATURE [Part::Box] Box018  label="removeToCreteHoleForPlugHousing011"
  AttacherType = Attacher::AttachEngine3D
  Height = 28.6
  Length = 10
  Placement = pos=(-2,0,21.7) rot=(0,0,1;0rad)
  Width = 19
FEATURE [Part::Box] Box019  label="wireHolderBottomCaseBit"
  AttacherType = Attacher::AttachEngine3D
  Height = 28
  Length = 3
  Placement = pos=(0,0,22) rot=(0,0,1;0rad)
  Width = 21
FEATURE [Part::Cylinder] Cylinder027  label="removeToCreteHoleForPlugHousing012"
  Angle = 360
  AttacherType = Attacher::AttachEngine3D
  Height = 20
  Placement = pos=(-2,19,36) rot=(0,1,0;1.5708rad)
  Radius = 14.3
FEATURE [Part::Cut] Cut031  label="wireHolderBottomCaseBit001"
  Base = -> Box019
  Tool = -> Cylinder027
FEATURE [Part::MultiFuse] Fusion070  label="removeToCreteHoleForPlugHousing013"
  Shapes = -> [Box018,Cylinder026]
FEATURE [Part::Cut] Cut032  label="top016"
  Base = -> Cut029
  Tool = -> Fusion070
FEATURE [Part::Cylinder] Cylinder028
  Angle = 360
  AttacherType = Attacher::AttachEngine3D
  Height = 20
  Placement = pos=(0,0,36.15) rot=(0,0,1;0rad)
  Radius = 14.3
FEATURE [Part::Cylinder] Cylinder029
  Angle = 360
  AttacherType = Attacher::AttachEngine3D
  Height = 10
  Placement = pos=(0,0,36.15) rot=(0,0,1;0rad)
  Radius = 4
FEATURE [Part::MultiFuse] Fusion071  label="removeToCreteHoleForPlugHousing014"
  Placement = pos=(70,19,36) rot=(0,1,0;1.5708rad)
  Shapes = -> [Cylinder028,Cylinder029]
FEATURE [Sketcher::SketchObject] Sketch049  label="topSketch011"
  FullyConstrained = true
  sketch-geometry (4):
    g0: ArcOfCircle CenterX=105 CenterY=19 CenterZ=0 NormalX=0 NormalY=0 NormalZ=1 AngleXU=0 Radius=20.6155 StartAngle=5.54125 EndAngle=6.28319
    g1: ArcOfCircle CenterX=105 CenterY=19 CenterZ=0 NormalX=0 NormalY=0 NormalZ=1 AngleXU=0 Radius=13 StartAngle=5.54125 EndAngle=6.28319
    g2: LineSegment StartX=118 StartY=19 StartZ=0 EndX=125.616 EndY=19 EndZ=0
    g3: LineSegment StartX=114.583 StartY=10.2157 StartZ=0 EndX=120.197 EndY=5.06982 EndZ=0
  constraints (7):
    c: Block(g0)
    c: Block(g1)
    c: Coincident(g2,g1)
    c: Coincident(g2,g0)
    c: Horizontal(g2)
    c: Coincident(g3,g1)
    c: Coincident(g3,g0)
FEATURE [Part::Box] Box020  label="removeToCreteHoleForPlugHousing015"
  AttacherType = Attacher::AttachEngine3D
  Height = 28.6
  Length = 20
  Placement = pos=(106.15,0,21.7) rot=(0,0,1;0rad)
  Width = 19
FEATURE [Part::MultiFuse] Fusion072  label="removeToCreteHoleForPlugHousing016"
  Shapes = -> [Box020,Fusion071]
FEATURE [Part::Cut] Cut033  label="removeToCreteHoleForPlugHousing017"
  Base = -> Cut032
  Tool = -> Fusion072
FEATURE [Part::Cylinder] Cylinder030
  Angle = 360
  AttacherType = Attacher::AttachEngine3D
  Height = 20
  Placement = pos=(0,0,36.15) rot=(0,0,1;0rad)
  Radius = 14.3
FEATURE [Part::Cylinder] Cylinder031
  Angle = 360
  AttacherType = Attacher::AttachEngine3D
  Height = 10
  Placement = pos=(0,0,36.15) rot=(0,0,1;0rad)
  Radius = 4
FEATURE [Part::Box] Box021  label="removeToCreteHoleForPlugHousing019"
  AttacherType = Attacher::AttachEngine3D
  Height = 28.6
  Length = 20
  Placement = pos=(106.15,0,21.7) rot=(0,0,1;0rad)
  Width = 19
FEATURE [Part::MultiFuse] Fusion074  label="removeToCreteHoleForPlugHousing020"
  Placement = pos=(70,19,36) rot=(0,1,0;1.5708rad)
  Shapes = -> [Cylinder030,Cylinder031]
FEATURE [Part::MultiFuse] Fusion073  label="removeToCreteHoleForPlugHousing018"
  Placement = pos=(0,0,28.3) rot=(0,0,1;0rad)
  Shapes = -> [Box021,Fusion074]
FEATURE [Part::Cylinder] Cylinder032
  Angle = 360
  AttacherType = Attacher::AttachEngine3D
  Height = 20
  Placement = pos=(0,0,36.15) rot=(0,0,1;0rad)
  Radius = 14.3
FEATURE [Part::Cylinder] Cylinder033
  Angle = 360
  AttacherType = Attacher::AttachEngine3D
  Height = 10
  Placement = pos=(0,0,36.15) rot=(0,0,1;0rad)
  Radius = 4
FEATURE [Part::Box] Box022  label="removeToCreteHoleForPlugHousing021"
  AttacherType = Attacher::AttachEngine3D
  Height = 28.6
  Length = 20
  Placement = pos=(106.15,0,21.7) rot=(0,0,1;0rad)
  Width = 19
FEATURE [Part::MultiFuse] Fusion076  label="removeToCreteHoleForPlugHousing023"
  Placement = pos=(70,19,36) rot=(0,1,0;1.5708rad)
  Shapes = -> [Cylinder032,Cylinder033]
FEATURE [Part::MultiFuse] Fusion075  label="removeToCreteHoleForPlugHousing022"
  Placement = pos=(0,0,-28.3) rot=(0,0,1;0rad)
  Shapes = -> [Box022,Fusion076]
FEATURE [Part::MultiFuse] Fusion077  label="removeToCreatePlugHousingBottomBit"
  Shapes = -> [Fusion075,Fusion073]
FEATURE [Part::Cylinder] Cylinder034
  Angle = 360
  AttacherType = Attacher::AttachEngine3D
  Height = 20
  Placement = pos=(0,0,36.15) rot=(0,0,1;0rad)
  Radius = 14
FEATURE [Part::Cylinder] Cylinder035
  Angle = 360
  AttacherType = Attacher::AttachEngine3D
  Height = 10
  Placement = pos=(0,0,36.15) rot=(0,0,1;0rad)
  Radius = 4
FEATURE [Part::MultiFuse] Fusion078  label="removeToCreteHoleForPlugHousing024"
  Placement = pos=(70,19,36) rot=(0,1,0;1.5708rad)
  Shapes = -> [Cylinder034,Cylinder035]
FEATURE [Part::MultiFuse] Fusion079  label="removeToCreatePlugHousingBottomBit001"
  Shapes = -> [Fusion078,Fusion077]
FEATURE [Part::Extrusion] Extrude040  label="bottomPlugHousingBit"
  Base = -> Sketch049
  Dir = (0,0,1)
  DirMode = 2
  FaceMakerClass = Part::FaceMakerBullseye
  LengthFwd = 72
  LengthRev = 0
  Solid = true
  Symmetric = false
FEATURE [Part::Cut] Cut034  label="bottomPlugHousingBit001"
  Base = -> Extrude040
  Placement = pos=(-0.09,0,0) rot=(0,0,1;0rad)
  Tool = -> Fusion079
FEATURE [Part::Box] Box023  label="Cube014"
  AttacherType = Attacher::AttachEngine3D
  Height = 16
  Length = 8
  Placement = pos=(12.7,31.52,28) rot=(0,0,1;0rad)
  Width = 4
FEATURE [Part::Cylinder] Cylinder036
  Angle = 360
  AttacherType = Attacher::AttachEngine3D
  Height = 10
  Placement = pos=(0,0,36.15) rot=(0,0,1;0rad)
  Radius = 4
FEATURE [Part::Cylinder] Cylinder037
  Angle = 360
  AttacherType = Attacher::AttachEngine3D
  Height = 20
  Placement = pos=(0,0,36.15) rot=(0,0,1;0rad)
  Radius = 8.2
FEATURE [Part::MultiFuse] Fusion080  label="removeToCreteHoleForPlugHousing025"
  Placement = pos=(-42,19,36) rot=(0,1,0;1.5708rad)
  Shapes = -> [Cylinder037,Cylinder036]
FEATURE [Sketcher::SketchObject] Sketch050  label="topSketch012"
  FullyConstrained = true
  sketch-geometry (4):
    g0: LineSegment StartX=16.8446 StartY=31.512 StartZ=0 EndX=16.3251 EndY=34.4666 EndZ=0
    g1: ArcOfCircle CenterX=19 CenterY=19.2524 CenterZ=0 NormalX=0 NormalY=0 NormalZ=1 AngleXU=0 Radius=15.4476 StartAngle=1.74483 EndAngle=2.72717
    g2: ArcOfCircle CenterX=19 CenterY=19.2524 CenterZ=0 NormalX=0 NormalY=0 NormalZ=1 AngleXU=0 Radius=12.4476 StartAngle=1.74483 EndAngle=2.73189
    g3: LineSegment StartX=4.86004 StartY=25.4725 StartZ=0 EndX=7.58253 EndY=24.2107 EndZ=0
  constraints (7):
    c: Block(g0)
    c: Coincident(g1,g0)
    c: Coincident(g2,g0)
    c: Coincident(g3,g1)
    c: Coincident(g3,g2)
    c: Block(g1)
    c: Block(g2)
FEATURE [Part::Extrusion] Extrude041
  Base = -> Sketch050
  Dir = (0,0,1)
  DirMode = 2
  FaceMakerClass = Part::FaceMakerBullseye
  LengthFwd = 10.6
  LengthRev = 0
  Placement = pos=(0,0,31) rot=(0,0,1;0rad)
  Solid = true
  Symmetric = false
FEATURE [Part::Cut] Cut035
  Base = -> Extrude041
  Placement = pos=(0,0,-0.3) rot=(0,0,1;0rad)
  Tool = -> Fusion080
FEATURE [Part::Cut] Cut036
  Base = -> Box023
  Tool = -> Cut035
FEATURE [Part::Fillet] Fillet027
  Base = -> Cut036
  Edges = 1 edges r=0.7: [Edge13]
FEATURE [Part::Fillet] Fillet028
  Base = -> Fillet027
  Edges = 1 edges r=0.7: [Edge13]
FEATURE [Part::Fillet] Fillet029
  Base = -> Fillet028
  Edges = 1 edges r=0.7: [Edge16]
FEATURE [Part::Fillet] Fillet030
  Base = -> Fillet029
  Edges = 1 edges r=0.7: [Edge11]
FEATURE [Part::Fillet] Fillet031
  Base = -> Fillet030
  Edges = 1 edges r=0.7: [Edge10]
FEATURE [Part::Fillet] Fillet032
  Base = -> Fillet031
  Edges = 1 edges r=1.2: [Edge5]
FEATURE [Part::Fillet] Fillet033
  Base = -> Fillet032
  Edges = 1 edges r=1.2: [Edge12]
FEATURE [Part::Fillet] Fillet034  label="wireHousingRetainer"
  Base = -> Fillet033
  Edges = 1 edges r=2: [Edge1]
  Placement = pos=(0.3,0,0) rot=(0,0,1;0rad)
FEATURE [Part::Feature] Face099
  shape: bbox 3.5 x 17.8 x 2e-07 mm, 1 faces, 0 solids (baked)
FEATURE [Part::Revolution] Revolve107  label="removeToCreateScrewAndThreadedInsertHole034"
  Angle = 360
  Axis = (0,1,0)
  Base = (0,0,0)
  FaceMakerClass = Part::FaceMakerBullseye
  Placement = pos=(12.5,0,10) rot=(0,0,1;0rad)
  Solid = false
  Source = -> Face099
  Symmetric = false
FEATURE [Part::Feature] Face100
  shape: bbox 3.5 x 17.8 x 2e-07 mm, 1 faces, 0 solids (baked)
FEATURE [Part::Revolution] Revolve108  label="removeToCreateScrewAndThreadedInsertHole035"
  Angle = 360
  Axis = (0,1,0)
  Base = (0,0,0)
  FaceMakerClass = Part::FaceMakerBullseye
  Placement = pos=(12.5,0,62) rot=(0,0,1;0rad)
  Solid = false
  Source = -> Face100
  Symmetric = false
FEATURE [Part::Feature] Face101
  shape: bbox 3.5 x 17.8 x 2e-07 mm, 1 faces, 0 solids (baked)
FEATURE [Part::Revolution] Revolve109  label="removeToCreateScrewAndThreadedInsertHole036"
  Angle = 360
  Axis = (0,1,0)
  Base = (0,0,0)
  FaceMakerClass = Part::FaceMakerBullseye
  Placement = pos=(89.5,0,68.5) rot=(0,0,1;0rad)
  Solid = false
  Source = -> Face101
  Symmetric = false
FEATURE [Part::Feature] Face102
  shape: bbox 3.5 x 17.8 x 2e-07 mm, 1 faces, 0 solids (baked)
FEATURE [Part::Revolution] Revolve110  label="removeToCreateScrewAndThreadedInsertHole037"
  Angle = 360
  Axis = (0,1,0)
  Base = (0,0,0)
  FaceMakerClass = Part::FaceMakerBullseye
  Placement = pos=(89.5,0,3.5) rot=(0,0,1;0rad)
  Solid = false
  Source = -> Face102
  Symmetric = false
FEATURE [Part::Feature] Face103
  shape: bbox 3.5 x 17.8 x 2e-07 mm, 1 faces, 0 solids (baked)
FEATURE [Part::Revolution] Revolve111  label="removeToCreateScrewAndThreadedInsertHole038"
  Angle = 360
  Axis = (0,1,0)
  Base = (0,0,0)
  FaceMakerClass = Part::FaceMakerBullseye
  Placement = pos=(109.5,4.7,3.5) rot=(0,0,1;0rad)
  Solid = false
  Source = -> Face103
  Symmetric = false
FEATURE [Part::Feature] Face104
  shape: bbox 3.5 x 17.8 x 2e-07 mm, 1 faces, 0 solids (baked)
FEATURE [Part::Revolution] Revolve112  label="removeToCreateScrewAndThreadedInsertHole039"
  Angle = 360
  Axis = (0,1,0)
  Base = (0,0,0)
  FaceMakerClass = Part::FaceMakerBullseye
  Placement = pos=(109.5,4.7,68.5) rot=(0,0,1;0rad)
  Solid = false
  Source = -> Face104
  Symmetric = false
FEATURE [Part::MultiFuse] Fusion081  label="removeToCreateScrewAndThreadedInsertHole040"
  Shapes = -> [Revolve107,Revolve108,Revolve109,Revolve110,Revolve111,Revolve112]
FEATURE [Part::MultiFuse] Fusion082  label="casePillars002"
  Shapes = -> [Revolve094,Revolve092,Revolve090,Revolve089,Revolve091,Revolve093]
FEATURE [Part::Cut] Cut037  label="casePillars003"
  Base = -> Fusion082
  Tool = -> Fusion081
FEATURE [Sketcher::SketchObject] Sketch051
  FullyConstrained = true
  Placement = pos=(117,19,0) rot=(0.57735,0.57735,0.57735;2.0944rad)
  sketch-geometry (48):
    g0: LineSegment StartX=-49.19 StartY=69.25 StartZ=0 EndX=-49.19 EndY=66.25 EndZ=0
    g1: LineSegment StartX=-49.19 StartY=63.5 StartZ=0 EndX=-49.19 EndY=60.5 EndZ=0
    g2: LineSegment StartX=-49.19 StartY=57.75 StartZ=0 EndX=-49.19 EndY=54.75 EndZ=0
    g3: LineSegment StartX=-49.19 StartY=52 StartZ=0 EndX=-49.19 EndY=49 EndZ=0
    g4: LineSegment StartX=-49.19 StartY=46.25 StartZ=0 EndX=-49.19 EndY=43.25 EndZ=0
    g5: LineSegment StartX=-49.19 StartY=40.5 StartZ=0 EndX=-49.19 EndY=37.5 EndZ=0
    g6: LineSegment StartX=-49.19 StartY=34.5 StartZ=0 EndX=-49.19 EndY=31.5 EndZ=0
    g7: LineSegment StartX=-49.19 StartY=28.75 StartZ=0 EndX=-49.19 EndY=25.75 EndZ=0
    g8: LineSegment StartX=-49.19 StartY=23 StartZ=0 EndX=-49.19 EndY=20 EndZ=0
    g9: LineSegment StartX=-49.19 StartY=17.25 StartZ=0 EndX=-49.19 EndY=14.25 EndZ=0
    g10: LineSegment StartX=-49.19 StartY=11.5 StartZ=0 EndX=-49.19 EndY=8.5 EndZ=0
    g11: LineSegment StartX=-49.19 StartY=5.75 StartZ=0 EndX=-49.19 EndY=2.75 EndZ=0
    g12: ArcOfCircle CenterX=-1.5 CenterY=67.75 CenterZ=0 NormalX=0 NormalY=0 NormalZ=1 AngleXU=0 Radius=1.5 StartAngle=4.71239 EndAngle=7.85398
    g13: ArcOfCircle CenterX=-1.5 CenterY=62 CenterZ=0 NormalX=0 NormalY=0 NormalZ=1 AngleXU=0 Radius=1.5 StartAngle=4.71239 EndAngle=7.85398
    g14: ArcOfCircle CenterX=-1.5 CenterY=56.25 CenterZ=0 NormalX=0 NormalY=0 NormalZ=1 AngleXU=0 Radius=1.5 StartAngle=4.71239 EndAngle=7.85398
    g15: ArcOfCircle CenterX=-11.49 CenterY=50.5 CenterZ=0 NormalX=0 NormalY=0 NormalZ=1 AngleXU=0 Radius=1.5 StartAngle=4.71239 EndAngle=7.85398
    g16: ArcOfCircle CenterX=-16.28 CenterY=44.75 CenterZ=0 NormalX=0 NormalY=0 NormalZ=1 AngleXU=0 Radius=1.5 StartAngle=4.71239 EndAngle=7.85398
    g17: ArcOfCircle CenterX=-18.2337 CenterY=39 CenterZ=0 NormalX=0 NormalY=0 NormalZ=1 AngleXU=0 Radius=1.5 StartAngle=4.71485 EndAngle=7.85398
    g18: ArcOfCircle CenterX=-16.2837 CenterY=27.25 CenterZ=0 NormalX=0 NormalY=0 NormalZ=1 AngleXU=0 Radius=1.5 StartAngle=4.71485 EndAngle=7.85398
    g19: ArcOfCircle CenterX=-18.2337 CenterY=33 CenterZ=0 NormalX=0 NormalY=0 NormalZ=1 AngleXU=0 Radius=1.5 StartAngle=4.71485 EndAngle=7.85398
    g20: ArcOfCircle CenterX=-11.49 CenterY=21.5 CenterZ=0 NormalX=0 NormalY=0 NormalZ=1 AngleXU=0 Radius=1.5 StartAngle=4.71239 EndAngle=7.85398
    g21: ArcOfCircle CenterX=-1.5 CenterY=4.25 CenterZ=0 NormalX=0 NormalY=0 NormalZ=1 AngleXU=0 Radius=1.5 StartAngle=4.71239 EndAngle=7.85398
    g22: ArcOfCircle CenterX=-1.5 CenterY=10 CenterZ=0 NormalX=0 NormalY=0 NormalZ=1 AngleXU=0 Radius=1.5 StartAngle=4.71239 EndAngle=7.85398
    g23: ArcOfCircle CenterX=-1.5 CenterY=15.75 CenterZ=0 NormalX=0 NormalY=0 NormalZ=1 AngleXU=0 Radius=1.5 StartAngle=4.71239 EndAngle=7.85398
    g24: LineSegment StartX=-49.19 StartY=69.25 StartZ=0 EndX=-1.5 EndY=69.25 EndZ=0
    g25: LineSegment StartX=-49.19 StartY=66.25 StartZ=0 EndX=-1.5 EndY=66.25 EndZ=0
    g26: LineSegment StartX=-49.19 StartY=63.5 StartZ=0 EndX=-1.5 EndY=63.5 EndZ=0
    g27: LineSegment StartX=-49.19 StartY=60.5 StartZ=0 EndX=-1.5 EndY=60.5 EndZ=0
    g28: LineSegment StartX=-49.19 StartY=57.75 StartZ=0 EndX=-1.5 EndY=57.75 EndZ=0
    g29: LineSegment StartX=-49.19 StartY=54.75 StartZ=0 EndX=-1.5 EndY=54.75 EndZ=0
    g30: LineSegment StartX=-49.19 StartY=52 StartZ=0 EndX=-11.49 EndY=52 EndZ=0
    g31: LineSegment StartX=-49.19 StartY=49 StartZ=0 EndX=-11.49 EndY=49 EndZ=0
    g32: LineSegment StartX=-49.19 StartY=46.25 StartZ=0 EndX=-16.28 EndY=46.25 EndZ=0
    g33: LineSegment StartX=-49.19 StartY=43.25 StartZ=0 EndX=-16.28 EndY=43.25 EndZ=0
    g34: LineSegment StartX=-49.19 StartY=40.5 StartZ=0 EndX=-18.2337 EndY=40.5 EndZ=0
    g35: LineSegment StartX=-49.19 StartY=37.5 StartZ=0 EndX=-18.23 EndY=37.5 EndZ=0
    g36: LineSegment StartX=-49.19 StartY=34.5 StartZ=0 EndX=-18.2337 EndY=34.5 EndZ=0
    g37: LineSegment StartX=-49.19 StartY=31.5 StartZ=0 EndX=-18.23 EndY=31.5 EndZ=0
    g38: LineSegment StartX=-49.19 StartY=28.75 StartZ=0 EndX=-16.2837 EndY=28.75 EndZ=0
    g39: LineSegment StartX=-49.19 StartY=25.75 StartZ=0 EndX=-16.28 EndY=25.75 EndZ=0
    g40: LineSegment StartX=-49.19 StartY=23 StartZ=0 EndX=-11.49 EndY=23 EndZ=0
    g41: LineSegment StartX=-49.19 StartY=20 StartZ=0 EndX=-11.49 EndY=20 EndZ=0
    g42: LineSegment StartX=-49.19 StartY=17.25 StartZ=0 EndX=-1.5 EndY=17.25 EndZ=0
    g43: LineSegment StartX=-49.19 StartY=14.25 StartZ=0 EndX=-1.5 EndY=14.25 EndZ=0
    g44: LineSegment StartX=-49.19 StartY=11.5 StartZ=0 EndX=-1.5 EndY=11.5 EndZ=0
    g45: LineSegment StartX=-49.19 StartY=8.5 StartZ=0 EndX=-1.5 EndY=8.5 EndZ=0
    g46: LineSegment StartX=-49.19 StartY=5.75 StartZ=0 EndX=-1.5 EndY=5.75 EndZ=0
    g47: LineSegment StartX=-49.19 StartY=2.75 StartZ=0 EndX=-1.5 EndY=2.75 EndZ=0
  constraints (120):
    c: Vertical(g0)
    c: Distance(g0) = 3
    c: Block(g0)
    c: Vertical(g1)
    c: Distance(g1) = 3
    c: Vertical(g2)
    c: Equal(g0,g2) = 3
    c: Block(g2)
    c: Vertical(g3)
    c: Equal(g1,g3) = 3
    c: Vertical(g4)
    c: Equal(g0,g4) = 3
    c: Block(g4)
    c: Vertical(g5)
    c: Equal(g1,g5) = 3
    c: Vertical(g6)
    c: Equal(g0,g6) = 3
    c: Block(g6)
    c: Vertical(g7)
    c: Equal(g1,g7) = 3
    c: Vertical(g8)
    c: Equal(g0,g8) = 3
    c: Block(g8)
    c: Vertical(g9)
    c: Equal(g1,g9) = 3
    c: Vertical(g10)
    c: Equal(g0,g10) = 3
    c: Block(g10)
    c: Vertical(g11)
    c: Equal(g1,g11) = 3
    c: Block(g12)
    c: Block(g13)
    c: Block(g14)
    c: Block(g15)
    c: Block(g16)
    c: Block(g17)
    c: Block(g18)
    c: Block(g19)
    c: Block(g20)
    c: Block(g21)
    c: Block(g22)
    c: Block(g23)
    c: Block(g11)
    c: Block(g9)
    c: Block(g7)
    c: Block(g5)
    c: Block(g3)
    c: Block(g1)
    c: Coincident(g24,g0)
    c: Coincident(g24,g12)
    c: Horizontal(g24)
    c: Coincident(g25,g0)
    c: Coincident(g25,g12)
    c: Horizontal(g25)
    c: Coincident(g26,g1)
    c: Coincident(g26,g13)
    c: Horizontal(g26)
    c: Coincident(g27,g1)
    c: Coincident(g27,g13)
    c: Horizontal(g27)
    c: Coincident(g28,g2)
    c: Coincident(g28,g14)
    c: Horizontal(g28)
    c: Coincident(g29,g2)
    c: Coincident(g29,g14)
    c: Horizontal(g29)
    c: Coincident(g30,g3)
    c: Coincident(g30,g15)
    c: Horizontal(g30)
    c: Coincident(g31,g3)
    c: Coincident(g31,g15)
    c: Horizontal(g31)
    c: Coincident(g32,g4)
    c: Coincident(g32,g16)
    c: Horizontal(g32)
    c: Coincident(g33,g4)
    c: Coincident(g33,g16)
    c: Horizontal(g33)
    c: Coincident(g34,g5)
    c: Coincident(g34,g17)
    c: Horizontal(g34)
    c: Coincident(g35,g5)
    c: Coincident(g35,g17)
    c: Horizontal(g35)
    c: Coincident(g36,g6)
    c: Coincident(g36,g19)
    c: Horizontal(g36)
    c: Coincident(g37,g6)
    c: Coincident(g37,g19)
    c: Horizontal(g37)
    c: Coincident(g38,g7)
    c: Coincident(g38,g18)
    c: Horizontal(g38)
    c: Coincident(g39,g7)
    c: Coincident(g39,g18)
    c: Horizontal(g39)
    c: Coincident(g40,g8)
    c: Coincident(g40,g20)
    c: Horizontal(g40)
    c: Coincident(g41,g8)
    c: Coincident(g41,g20)
    c: Horizontal(g41)
    c: Coincident(g42,g9)
    c: Coincident(g42,g23)
    c: Horizontal(g42)
    c: Coincident(g43,g9)
    c: Coincident(g43,g23)
    c: Horizontal(g43)
    c: Coincident(g44,g10)
    c: Coincident(g44,g22)
    c: Horizontal(g44)
    c: Coincident(g45,g10)
    c: Coincident(g45,g22)
    c: Horizontal(g45)
    c: Coincident(g46,g11)
    c: Coincident(g46,g21)
    c: Horizontal(g46)
    c: Coincident(g47,g11)
    c: Coincident(g47,g21)
    c: Horizontal(g47)
FEATURE [Part::Extrusion] Extrude042
  Base = -> Sketch051
  Dir = (1,-2e-16,2e-16)
  DirMode = 2
  FaceMakerClass = Part::FaceMakerBullseye
  LengthFwd = 19
  LengthRev = 0
  Placement = pos=(-19,0,0) rot=(0,0,1;0rad)
  Solid = true
  Symmetric = false
FEATURE [Part::Fillet] Fillet035  label="removeToCreateVentalationHoles"
  Base = -> Extrude042
  Edges = <same value as first occurrence — deduplicated (x6 in doc)>
  Placement = pos=(7,0,0) rot=(0,0,1;0rad)
FEATURE [Part::Cut] Cut038  label="top017"
  Base = -> Cut033
  Tool = -> Fillet035
FEATURE [Sketcher::SketchObject] Sketch052  label="bottomSketch001"
  FullyConstrained = true
  sketch-geometry (45):
    g0: LineSegment StartX=6.29999 StartY=8 StartZ=0 EndX=3.29999 EndY=8 EndZ=0
    g1: LineSegment StartX=3.29999 StartY=8 StartZ=0 EndX=3.29999 EndY=-6.03275e-07 EndZ=0
    g2: ArcOfCircle CenterX=8.29999 CenterY=5 CenterZ=0 NormalX=0 NormalY=0 NormalZ=1 AngleXU=0 Radius=2 StartAngle=3.14159 EndAngle=4.71239
    g3: LineSegment StartX=6.29999 StartY=8 StartZ=0 EndX=6.29999 EndY=5 EndZ=0
    g4: ArcOfCircle CenterX=105 CenterY=19 CenterZ=0 NormalX=0 NormalY=0 NormalZ=1 AngleXU=0 Radius=12.7 StartAngle=4.71239 EndAngle=5.94289
    g5-g11: Circle x7 (B-spline internal-alignment scaffolding for g12; pole/knot coordinates omitted)
    g12: BSplineCurve PolesCount=7 KnotsCount=5 Degree=3 IsPeriodic=0
    g13-g17: GeomPoint x5 (B-spline internal-alignment scaffolding for g12; pole/knot coordinates omitted)
    g18: ArcOfCircle CenterX=105 CenterY=19 CenterZ=0 NormalX=0 NormalY=0 NormalZ=1 AngleXU=0 Radius=15.7 StartAngle=5.81226 EndAngle=6.28319
    g19: BSplineCurve PolesCount=5 KnotsCount=3 Degree=3 IsPeriodic=0
    g20: LineSegment StartX=8.29999 StartY=3 StartZ=0 EndX=101.7 EndY=3 EndZ=0
    g21: LineSegment StartX=3.29999 StartY=-6.03275e-07 StartZ=0 EndX=105 EndY=-6.03275e-07 EndZ=0
    g22: LineSegment StartX=120.974 StartY=8.71251 StartZ=0 EndX=122.332 EndY=7.83778 EndZ=0
    g23: LineSegment StartX=105 StartY=-6.03274e-07 StartZ=0 EndX=113 EndY=-6.03274e-07 EndZ=0
    g24: ArcOfCircle CenterX=105 CenterY=19 CenterZ=0 NormalX=0 NormalY=0 NormalZ=1 AngleXU=0 Radius=20.6155 StartAngle=5.11091 EndAngle=5.71103
    g25: ArcOfCircle CenterX=117.7 CenterY=19 CenterZ=0 NormalX=0 NormalY=0 NormalZ=1 AngleXU=0 Radius=3 StartAngle=1.2e-15 EndAngle=2.10468
    g26: Circle CenterX=116.345 CenterY=16.3232 CenterZ=0 NormalX=0 NormalY=0 NormalZ=1 AngleXU=0 Radius=1
    g27: Circle CenterX=117.24 CenterY=15.7584 CenterZ=0 NormalX=0 NormalY=0 NormalZ=1 AngleXU=0 Radius=1
    g28: Circle CenterX=116.972 CenterY=14.7612 CenterZ=0 NormalX=0 NormalY=0 NormalZ=1 AngleXU=0 Radius=1
    g29: BSplineCurve PolesCount=3 KnotsCount=2 Degree=2 IsPeriodic=0
    g30: GeomPoint X=116.345 Y=16.3232 Z=0
    g31: GeomPoint X=116.972 Y=14.7612 Z=0
    g32: Circle CenterX=115.828 CenterY=17.157 CenterZ=0 NormalX=0 NormalY=0 NormalZ=1 AngleXU=0 Radius=1
    g33: Circle CenterX=115.841 CenterY=16.639 CenterZ=0 NormalX=0 NormalY=0 NormalZ=1 AngleXU=0 Radius=1
    g34: Circle CenterX=116.345 CenterY=16.3232 CenterZ=0 NormalX=0 NormalY=0 NormalZ=1 AngleXU=0 Radius=1
    g35: BSplineCurve PolesCount=3 KnotsCount=2 Degree=2 IsPeriodic=0
    g36: GeomPoint X=115.828 Y=17.157 Z=0
    g37: GeomPoint X=116.345 Y=16.3232 Z=0
    g38: LineSegment StartX=115.828 StartY=17.157 StartZ=0 EndX=115.828 EndY=20.8307 EndZ=0
    g39: Circle CenterX=115.828 CenterY=20.8307 CenterZ=0 NormalX=0 NormalY=0 NormalZ=1 AngleXU=0 Radius=1
    g40: Circle CenterX=115.831 CenterY=21.3396 CenterZ=0 NormalX=0 NormalY=0 NormalZ=1 AngleXU=0 Radius=1
    g41: Circle CenterX=116.173 CenterY=21.5825 CenterZ=0 NormalX=0 NormalY=0 NormalZ=1 AngleXU=0 Radius=1
    g42: BSplineCurve PolesCount=3 KnotsCount=2 Degree=2 IsPeriodic=0
    g43: GeomPoint X=115.828 Y=20.8307 Z=0
    g44: GeomPoint X=116.173 Y=21.5825 Z=0
  constraints (70):
    c: Horizontal(g0)
    c: Distance(g0) = 3
    c: Coincident(g1,g0)
    c: Vertical(g1)
    c: Block(g2)
    c: Block(g0)
    c: Coincident(g3,g0)
    c: Coincident(g3,g2)
    c: Vertical(g3)
    c: Block(g1)
    c: Block(g4)
    c: Coincident(g19,g4)
    c: Block(g19)
    c: Equal(g5, g6-g11) x6
    c: InternalAlignment(g5-g11 -> g12) x7
    c: InternalAlignment(g13-g17 -> g12) x5
    c: Block(g12)
    c: Coincident(g18,g12)
    c: Block(g18)
    c: Coincident(g20,g2)
    c: Coincident(g20,g19)
    c: Horizontal(g20)
    c: Distance(g20) = 93.4
    c: Coincident(g21,g1)
    c: Horizontal(g21)
    c: Distance(g21) = 101.7
    c: Horizontal(g23)
    c: Distance(g23) = 8
    c: Coincident(g24,g23)
    c: Block(g23)
    c: Coincident(g22,g24)
    c: Block(g24)
    c: Block(g22)
    c: Distance(g22) = 1.61553
    c: Coincident(g25,g18)
    c: Block(g25)
    c: Weight(g26) = 1
    c: Equal(g26,g27)
    c: Equal(g26,g28)
    c: Coincident(g29,g4)
    c: InternalAlignment(g26,g29)
    c: InternalAlignment(g27,g29)
    c: InternalAlignment(g28,g29)
    c: InternalAlignment(g30,g29)
    c: InternalAlignment(g31,g29)
    c: Block(g29)
    c: Weight(g32) = 1
    c: Equal(g32,g33)
    c: Equal(g32,g34)
    c: Coincident(g35,g29)
    c: InternalAlignment(g32,g35)
    c: InternalAlignment(g33,g35)
    c: InternalAlignment(g34,g35)
    c: InternalAlignment(g36,g35)
    c: InternalAlignment(g37,g35)
    c: Block(g35)
    c: Coincident(g38,g35)
    c: Vertical(g38)
    c: Block(g38)
    c: Coincident(g42,g38)
    c: Weight(g39) = 1
    c: Equal(g39,g40)
    c: Equal(g39,g41)
    c: Coincident(g42,g25)
    c: InternalAlignment(g39,g42)
    c: InternalAlignment(g40,g42)
    c: InternalAlignment(g41,g42)
    c: InternalAlignment(g43,g42)
    c: InternalAlignment(g44,g42)
    c: Block(g42)
FEATURE [Part::Extrusion] Extrude043  label="bottom010"
  Base = -> Sketch052
  Dir = (0,0,1)
  DirMode = 2
  FaceMakerClass = Part::FaceMakerBullseye
  LengthFwd = 71.4
  LengthRev = 0
  Placement = pos=(0,0,0.3) rot=(0,0,1;0rad)
  Solid = true
  Symmetric = false
FEATURE [Sketcher::SketchObject] Sketch053  label="topSketch013"
  FullyConstrained = true
  sketch-geometry (22):
    g0: LineSegment StartX=5.21097e-06 StartY=3 StartZ=0 EndX=5.21097e-06 EndY=19 EndZ=0
    g1: ArcOfCircle CenterX=19 CenterY=19 CenterZ=0 NormalX=0 NormalY=0 NormalZ=1 AngleXU=0 Radius=19 StartAngle=1.5708 EndAngle=3.14159
    g2: ArcOfCircle CenterX=19 CenterY=19 CenterZ=0 NormalX=0 NormalY=0 NormalZ=1 AngleXU=0 Radius=16 StartAngle=1.5708 EndAngle=3.14159
    g3: LineSegment StartX=114 StartY=35 StartZ=0 EndX=19 EndY=35 EndZ=0
    g4: LineSegment StartX=5.21097e-06 StartY=3 StartZ=0 EndX=5.21097e-06 EndY=0 EndZ=0
    g5: LineSegment StartX=3 StartY=0 StartZ=0 EndX=5.21097e-06 EndY=0 EndZ=0
    g6: LineSegment StartX=3 StartY=19 StartZ=0 EndX=3 EndY=0 EndZ=0
    g7: LineSegment StartX=19 StartY=38 StartZ=0 EndX=124 EndY=38 EndZ=0
    g8: Circle CenterX=119 CenterY=35 CenterZ=0 NormalX=0 NormalY=0 NormalZ=1 AngleXU=0 Radius=1
    g9: Circle CenterX=121 CenterY=35 CenterZ=0 NormalX=0 NormalY=0 NormalZ=1 AngleXU=0 Radius=1
    g10: Circle CenterX=121 CenterY=33 CenterZ=0 NormalX=0 NormalY=0 NormalZ=1 AngleXU=0 Radius=1
    g11: BSplineCurve PolesCount=3 KnotsCount=2 Degree=2 IsPeriodic=0
    g12: GeomPoint X=119 Y=35 Z=0
    g13: GeomPoint X=121 Y=33 Z=0
    g14: LineSegment StartX=119 StartY=35 StartZ=0 EndX=114 EndY=35 EndZ=0
    g15: ArcOfCircle CenterX=105 CenterY=19 CenterZ=0 NormalX=0 NormalY=0 NormalZ=1 AngleXU=0 Radius=16 StartAngle=5.60905 EndAngle=6.28319
    g16: LineSegment StartX=121 StartY=33 StartZ=0 EndX=121 EndY=19 EndZ=0
    g17: LineSegment StartX=117.5 StartY=9.01251 StartZ=0 EndX=121.163 EndY=9.0125 EndZ=0
    g18: ArcOfCircle CenterX=105 CenterY=19 CenterZ=0 NormalX=0 NormalY=0 NormalZ=1 AngleXU=0 Radius=20.6155 StartAngle=5.7297 EndAngle=6.28319
    g19: LineSegment StartX=121.163 StartY=9.0125 StartZ=0 EndX=122.538 EndY=8.16329 EndZ=0
    g20: LineSegment StartX=124 StartY=38 StartZ=0 EndX=125.616 EndY=38 EndZ=0
    g21: LineSegment StartX=125.616 StartY=19 StartZ=0 EndX=125.616 EndY=38 EndZ=0
  constraints (50):
    c: Vertical(g0)
    c: Block(g0)
    c: Coincident(g1,g0)
    c: Block(g1)
    c: Coincident(g2,g1)
    c: Block(g2)
    c: Coincident(g3,g2)
    c: Horizontal(g3)
    c: Tangent(g3,g2)
    c: Coincident(g4,g0)
    c: Distance(g4) = 3
    c: Vertical(g4)
    c: Coincident(g5,g4)
    c: Horizontal(g5)
    c: Coincident(g6,g2)
    c: Coincident(g6,g5)
    c: Vertical(g6)
    c: Horizontal(g7)
    c: Distance(g7) = 105
    c: Coincident(g7,g1)
    c: Block(g3)
    c: Weight(g8) = 1
    c: Equal(g8,g9)
    c: Equal(g8,g10)
    c: InternalAlignment(g8,g11)
    c: InternalAlignment(g9,g11)
    c: InternalAlignment(g10,g11)
    c: InternalAlignment(g12,g11)
    c: InternalAlignment(g13,g11)
    c: Block(g11)
    c: Coincident(g14,g11)
    c: Coincident(g14,g3)
    c: Horizontal(g14)
    c: Block(g15)
    c: Coincident(g16,g11)
    c: Coincident(g16,g15)
    c: Vertical(g16)
    c: Distance(g16) = 14
    c: Coincident(g17,g15)
    c: Block(g18)
    c: Coincident(g19,g18)
    c: Coincident(g20,g7)
    c: Horizontal(g20)
    c: Vertical(g21)
    c: Coincident(g20,g21)
    c: Block(g20)
    c: Block(g21)
    c: Block(g19)
    c: Block(g17)
    c: Distance(g20) = 1.61553
FEATURE [Part::Extrusion] Extrude044
  Base = -> Sketch053
  Dir = (0,0,1)
  DirMode = 2
  FaceMakerClass = Part::FaceMakerBullseye
  LengthFwd = 72
  LengthRev = 0
  Solid = true
  Symmetric = false
FEATURE [Part::Fillet] Fillet036  label="top018"
  Base = -> Extrude044
  Edges = 1 edges r=2: [Edge41]
FEATURE [Sketcher::SketchObject] Sketch054
  FullyConstrained = false
  Placement = pos=(0,0,0) rot=(1,0,0;1.5708rad)
  sketch-geometry (24):
    g0: ArcOfCircle CenterX=-4 CenterY=-10.5 CenterZ=0 NormalX=0 NormalY=0 NormalZ=1 AngleXU=0 Radius=1.5 StartAngle=6e-16 EndAngle=3.14159
    g1: ArcOfCircle CenterX=-34.2 CenterY=-10.5 CenterZ=0 NormalX=0 NormalY=0 NormalZ=1 AngleXU=0 Radius=1.5 StartAngle=0 EndAngle=3.14159
    g2: ArcOfCircle CenterX=-34.2 CenterY=-27.7 CenterZ=0 NormalX=0 NormalY=0 NormalZ=1 AngleXU=0 Radius=1.5 StartAngle=3.14159 EndAngle=6.28319
    g3: ArcOfCircle CenterX=-4 CenterY=-27.7 CenterZ=0 NormalX=0 NormalY=0 NormalZ=1 AngleXU=0 Radius=1.5 StartAngle=3.1416 EndAngle=6.28319
    g4: ArcOfCircle CenterX=-10 CenterY=-4.3 CenterZ=0 NormalX=0 NormalY=0 NormalZ=1 AngleXU=0 Radius=1.5 StartAngle=2e-16 EndAngle=3.14159
    g5: ArcOfCircle CenterX=-16.1 CenterY=-1.8 CenterZ=0 NormalX=0 NormalY=0 NormalZ=1 AngleXU=0 Radius=1.5 StartAngle=5e-16 EndAngle=3.14159
    g6: ArcOfCircle CenterX=-22.1 CenterY=-1.8 CenterZ=0 NormalX=0 NormalY=0 NormalZ=1 AngleXU=0 Radius=1.5 StartAngle=5e-16 EndAngle=3.14159
    g7: ArcOfCircle CenterX=-28.2 CenterY=-4.3 CenterZ=0 NormalX=0 NormalY=0 NormalZ=1 AngleXU=0 Radius=1.5 StartAngle=2e-16 EndAngle=3.14159
    g8: ArcOfCircle CenterX=-10 CenterY=-33.9 CenterZ=0 NormalX=0 NormalY=0 NormalZ=1 AngleXU=0 Radius=1.5 StartAngle=3.14159 EndAngle=6.28319
    g9: ArcOfCircle CenterX=-16.1 CenterY=-36.4 CenterZ=0 NormalX=0 NormalY=0 NormalZ=1 AngleXU=0 Radius=1.5 StartAngle=3.14159 EndAngle=6.28319
    g10: ArcOfCircle CenterX=-22.1 CenterY=-36.4 CenterZ=0 NormalX=0 NormalY=0 NormalZ=1 AngleXU=0 Radius=1.5 StartAngle=3.14159 EndAngle=6.28319
    g11: ArcOfCircle CenterX=-28.2 CenterY=-33.9 CenterZ=0 NormalX=0 NormalY=0 NormalZ=1 AngleXU=0 Radius=1.5 StartAngle=3.14159 EndAngle=6.28319
    g12: LineSegment StartX=-35.7 StartY=-10.5 StartZ=0 EndX=-35.7 EndY=-27.7 EndZ=0
    g13: LineSegment StartX=-32.7 StartY=-10.5 StartZ=0 EndX=-32.7 EndY=-27.7 EndZ=0
    g14: LineSegment StartX=-29.7 StartY=-33.9 StartZ=0 EndX=-29.7 EndY=-4.3 EndZ=0
    g15: LineSegment StartX=-26.7 StartY=-33.9 StartZ=0 EndX=-26.7 EndY=-4.3 EndZ=0
    g16: LineSegment StartX=-2.5 StartY=-10.5 StartZ=0 EndX=-2.5 EndY=-27.7 EndZ=0
    g17: LineSegment StartX=-8.5 StartY=-4.3 StartZ=0 EndX=-8.5 EndY=-33.9 EndZ=0
    g18: LineSegment StartX=-5.5 StartY=-10.5 StartZ=0 EndX=-5.5 EndY=-27.7 EndZ=0
    g19: LineSegment StartX=-11.5 StartY=-4.3 StartZ=0 EndX=-11.5 EndY=-33.9 EndZ=0
    g20: LineSegment StartX=-14.6 StartY=-1.8 StartZ=0 EndX=-14.6 EndY=-36.4 EndZ=0
    g21: LineSegment StartX=-17.6 StartY=-1.8 StartZ=0 EndX=-17.6 EndY=-36.4 EndZ=0
    g22: LineSegment StartX=-20.6 StartY=-36.4 StartZ=0 EndX=-20.6 EndY=-1.8 EndZ=0
    g23: LineSegment StartX=-23.6 StartY=-1.8 StartZ=0 EndX=-23.6 EndY=-36.4 EndZ=0
  constraints (48):
    c: Block(g0)
    c: Block(g1)
    c: Block(g2)
    c: Block(g3)
    c: Block(g4)
    c: Block(g5)
    c: Block(g6)
    c: Block(g7)
    c: Block(g8)
    c: Block(g9)
    c: Block(g10)
    c: Block(g11)
    c: Coincident(g12,g1)
    c: Coincident(g12,g2)
    c: Vertical(g12)
    c: Coincident(g13,g1)
    c: Coincident(g13,g2)
    c: Vertical(g13)
    c: Coincident(g14,g11)
    c: Coincident(g14,g7)
    c: Vertical(g14)
    c: Coincident(g15,g11)
    c: Coincident(g15,g7)
    c: Vertical(g15)
    c: Coincident(g16,g0)
    c: Coincident(g16,g3)
    c: Vertical(g16)
    c: Coincident(g17,g4)
    c: Coincident(g17,g8)
    c: Vertical(g17)
    c: Coincident(g18,g0)
    c: Coincident(g18,g3)
    c: Vertical(g18)
    c: Coincident(g19,g4)
    c: Coincident(g19,g8)
    c: Vertical(g19)
    c: Coincident(g20,g5)
    c: Coincident(g20,g9)
    c: Vertical(g20)
    c: Coincident(g21,g5)
    c: Coincident(g21,g9)
    c: Vertical(g21)
    c: Coincident(g22,g10)
    c: Coincident(g22,g6)
    c: Vertical(g22)
    c: Coincident(g23,g6)
    c: Coincident(g23,g10)
    c: Vertical(g23)
FEATURE [Part::Extrusion] Extrude045  label="removeToCreateFanGrillHoles003"
  Base = -> Sketch054
  Dir = (0,-1,6e-16)
  DirMode = 2
  FaceMakerClass = Part::FaceMakerBullseye
  LengthFwd = 10
  LengthRev = 0
  Placement = pos=(65.4,44,54.82) rot=(0,0,1;0rad)
  Solid = true
  Symmetric = false
FEATURE [Part::Feature] Face105 .. Face108  x4 (patterned run collapsed; names and placements below)
  shape: bbox 3.5 x 17.8 x 2e-07 mm, 1 faces, 0 solids (baked)
FEATURE [Part::Revolution] Revolve113  label="removeToCreateScrewAndThreadedInsertHole041"
  Angle = 360
  Axis = (0,1,0)
  Base = (0,0,0)
  FaceMakerClass = Part::FaceMakerBullseye
  Placement = pos=(62.3,30.3,19.7) rot=(0,0,1;0rad)
  Solid = false
  Source = -> Face105
  Symmetric = false
FEATURE [Part::Revolution] Revolve114  label="removeToCreateScrewAndThreadedInsertHole042"
  Angle = 360
  Axis = (0,1,0)
  Base = (0,0,0)
  FaceMakerClass = Part::FaceMakerBullseye
  Placement = pos=(62.3,30.3,51.7) rot=(0,0,1;0rad)
  Solid = false
  Source = -> Face106
  Symmetric = false
FEATURE [Part::Revolution] Revolve115  label="removeToCreateScrewAndThreadedInsertHole043"
  Angle = 360
  Axis = (0,1,0)
  Base = (0,0,0)
  FaceMakerClass = Part::FaceMakerBullseye
  Placement = pos=(30.3,30.3,19.7) rot=(0,0,1;0rad)
  Solid = false
  Source = -> Face107
  Symmetric = false
FEATURE [Part::Revolution] Revolve116  label="removeToCreateScrewAndThreadedInsertHole044"
  Angle = 360
  Axis = (0,1,0)
  Base = (0,0,0)
  FaceMakerClass = Part::FaceMakerBullseye
  Placement = pos=(30.3,30.3,51.7) rot=(0,0,1;0rad)
  Solid = false
  Source = -> Face108
  Symmetric = false
FEATURE [Part::MultiFuse] Fusion083  label="createThreadedInsertHolesForFan004"
  Shapes = -> [Revolve113,Revolve114,Revolve115,Revolve116]
FEATURE [Part::Box] Box024  label="removeToCreteHoleForPlugHousing026"
  AttacherType = Attacher::AttachEngine3D
  Height = 28.6
  Length = 10
  Placement = pos=(-2,0,21.7) rot=(0,0,1;0rad)
  Width = 19
FEATURE [Part::Cylinder] Cylinder038  label="removeToCreteHoleForPlugHousing027"
  Angle = 360
  AttacherType = Attacher::AttachEngine3D
  Height = 20
  Placement = pos=(-2,19,36) rot=(0,1,0;1.5708rad)
  Radius = 14.3
FEATURE [Part::MultiFuse] Fusion084  label="removeToCreteHoleForPlugHousing028"
  Shapes = -> [Box024,Cylinder038]
FEATURE [Part::Cylinder] Cylinder039
  Angle = 360
  AttacherType = Attacher::AttachEngine3D
  Height = 20
  Placement = pos=(0,0,36.15) rot=(0,0,1;0rad)
  Radius = 14.3
FEATURE [Part::Cylinder] Cylinder040
  Angle = 360
  AttacherType = Attacher::AttachEngine3D
  Height = 10
  Placement = pos=(0,0,36.15) rot=(0,0,1;0rad)
  Radius = 4
FEATURE [Part::Box] Box025  label="removeToCreteHoleForPlugHousing030"
  AttacherType = Attacher::AttachEngine3D
  Height = 28.6
  Length = 20
  Placement = pos=(106.15,0,21.7) rot=(0,0,1;0rad)
  Width = 19
FEATURE [Part::MultiFuse] Fusion086  label="removeToCreteHoleForPlugHousing031"
  Placement = pos=(70,19,36) rot=(0,1,0;1.5708rad)
  Shapes = -> [Cylinder039,Cylinder040]
FEATURE [Part::MultiFuse] Fusion085  label="removeToCreteHoleForPlugHousing029"
  Shapes = -> [Box025,Fusion086]
FEATURE [Sketcher::SketchObject] Sketch055
  FullyConstrained = true
  Placement = pos=(117,19,0) rot=(0.57735,0.57735,0.57735;2.0944rad)
  sketch-geometry (48):
    g0: LineSegment StartX=-49.19 StartY=69.25 StartZ=0 EndX=-49.19 EndY=66.25 EndZ=0
    g1: LineSegment StartX=-49.19 StartY=63.5 StartZ=0 EndX=-49.19 EndY=60.5 EndZ=0
    g2: LineSegment StartX=-49.19 StartY=57.75 StartZ=0 EndX=-49.19 EndY=54.75 EndZ=0
    g3: LineSegment StartX=-49.19 StartY=52 StartZ=0 EndX=-49.19 EndY=49 EndZ=0
    g4: LineSegment StartX=-49.19 StartY=46.25 StartZ=0 EndX=-49.19 EndY=43.25 EndZ=0
    g5: LineSegment StartX=-49.19 StartY=40.5 StartZ=0 EndX=-49.19 EndY=37.5 EndZ=0
    g6: LineSegment StartX=-49.19 StartY=34.5 StartZ=0 EndX=-49.19 EndY=31.5 EndZ=0
    g7: LineSegment StartX=-49.19 StartY=28.75 StartZ=0 EndX=-49.19 EndY=25.75 EndZ=0
    g8: LineSegment StartX=-49.19 StartY=23 StartZ=0 EndX=-49.19 EndY=20 EndZ=0
    g9: LineSegment StartX=-49.19 StartY=17.25 StartZ=0 EndX=-49.19 EndY=14.25 EndZ=0
    g10: LineSegment StartX=-49.19 StartY=11.5 StartZ=0 EndX=-49.19 EndY=8.5 EndZ=0
    g11: LineSegment StartX=-49.19 StartY=5.75 StartZ=0 EndX=-49.19 EndY=2.75 EndZ=0
    g12: ArcOfCircle CenterX=-1.5 CenterY=67.75 CenterZ=0 NormalX=0 NormalY=0 NormalZ=1 AngleXU=0 Radius=1.5 StartAngle=4.71239 EndAngle=7.85398
    g13: ArcOfCircle CenterX=-1.5 CenterY=62 CenterZ=0 NormalX=0 NormalY=0 NormalZ=1 AngleXU=0 Radius=1.5 StartAngle=4.71239 EndAngle=7.85398
    g14: ArcOfCircle CenterX=-1.5 CenterY=56.25 CenterZ=0 NormalX=0 NormalY=0 NormalZ=1 AngleXU=0 Radius=1.5 StartAngle=4.71239 EndAngle=7.85398
    g15: ArcOfCircle CenterX=-11.49 CenterY=50.5 CenterZ=0 NormalX=0 NormalY=0 NormalZ=1 AngleXU=0 Radius=1.5 StartAngle=4.71239 EndAngle=7.85398
    g16: ArcOfCircle CenterX=-16.28 CenterY=44.75 CenterZ=0 NormalX=0 NormalY=0 NormalZ=1 AngleXU=0 Radius=1.5 StartAngle=4.71239 EndAngle=7.85398
    g17: ArcOfCircle CenterX=-18.2337 CenterY=39 CenterZ=0 NormalX=0 NormalY=0 NormalZ=1 AngleXU=0 Radius=1.5 StartAngle=4.71485 EndAngle=7.85398
    g18: ArcOfCircle CenterX=-16.2837 CenterY=27.25 CenterZ=0 NormalX=0 NormalY=0 NormalZ=1 AngleXU=0 Radius=1.5 StartAngle=4.71485 EndAngle=7.85398
    g19: ArcOfCircle CenterX=-18.2337 CenterY=33 CenterZ=0 NormalX=0 NormalY=0 NormalZ=1 AngleXU=0 Radius=1.5 StartAngle=4.71485 EndAngle=7.85398
    g20: ArcOfCircle CenterX=-11.49 CenterY=21.5 CenterZ=0 NormalX=0 NormalY=0 NormalZ=1 AngleXU=0 Radius=1.5 StartAngle=4.71239 EndAngle=7.85398
    g21: ArcOfCircle CenterX=-1.5 CenterY=4.25 CenterZ=0 NormalX=0 NormalY=0 NormalZ=1 AngleXU=0 Radius=1.5 StartAngle=4.71239 EndAngle=7.85398
    g22: ArcOfCircle CenterX=-1.5 CenterY=10 CenterZ=0 NormalX=0 NormalY=0 NormalZ=1 AngleXU=0 Radius=1.5 StartAngle=4.71239 EndAngle=7.85398
    g23: ArcOfCircle CenterX=-1.5 CenterY=15.75 CenterZ=0 NormalX=0 NormalY=0 NormalZ=1 AngleXU=0 Radius=1.5 StartAngle=4.71239 EndAngle=7.85398
    g24: LineSegment StartX=-49.19 StartY=69.25 StartZ=0 EndX=-1.5 EndY=69.25 EndZ=0
    g25: LineSegment StartX=-49.19 StartY=66.25 StartZ=0 EndX=-1.5 EndY=66.25 EndZ=0
    g26: LineSegment StartX=-49.19 StartY=63.5 StartZ=0 EndX=-1.5 EndY=63.5 EndZ=0
    g27: LineSegment StartX=-49.19 StartY=60.5 StartZ=0 EndX=-1.5 EndY=60.5 EndZ=0
    g28: LineSegment StartX=-49.19 StartY=57.75 StartZ=0 EndX=-1.5 EndY=57.75 EndZ=0
    g29: LineSegment StartX=-49.19 StartY=54.75 StartZ=0 EndX=-1.5 EndY=54.75 EndZ=0
    g30: LineSegment StartX=-49.19 StartY=52 StartZ=0 EndX=-11.49 EndY=52 EndZ=0
    g31: LineSegment StartX=-49.19 StartY=49 StartZ=0 EndX=-11.49 EndY=49 EndZ=0
    g32: LineSegment StartX=-49.19 StartY=46.25 StartZ=0 EndX=-16.28 EndY=46.25 EndZ=0
    g33: LineSegment StartX=-49.19 StartY=43.25 StartZ=0 EndX=-16.28 EndY=43.25 EndZ=0
    g34: LineSegment StartX=-49.19 StartY=40.5 StartZ=0 EndX=-18.2337 EndY=40.5 EndZ=0
    g35: LineSegment StartX=-49.19 StartY=37.5 StartZ=0 EndX=-18.23 EndY=37.5 EndZ=0
    g36: LineSegment StartX=-49.19 StartY=34.5 StartZ=0 EndX=-18.2337 EndY=34.5 EndZ=0
    g37: LineSegment StartX=-49.19 StartY=31.5 StartZ=0 EndX=-18.23 EndY=31.5 EndZ=0
    g38: LineSegment StartX=-49.19 StartY=28.75 StartZ=0 EndX=-16.2837 EndY=28.75 EndZ=0
    g39: LineSegment StartX=-49.19 StartY=25.75 StartZ=0 EndX=-16.28 EndY=25.75 EndZ=0
    g40: LineSegment StartX=-49.19 StartY=23 StartZ=0 EndX=-11.49 EndY=23 EndZ=0
    g41: LineSegment StartX=-49.19 StartY=20 StartZ=0 EndX=-11.49 EndY=20 EndZ=0
    g42: LineSegment StartX=-49.19 StartY=17.25 StartZ=0 EndX=-1.5 EndY=17.25 EndZ=0
    g43: LineSegment StartX=-49.19 StartY=14.25 StartZ=0 EndX=-1.5 EndY=14.25 EndZ=0
    g44: LineSegment StartX=-49.19 StartY=11.5 StartZ=0 EndX=-1.5 EndY=11.5 EndZ=0
    g45: LineSegment StartX=-49.19 StartY=8.5 StartZ=0 EndX=-1.5 EndY=8.5 EndZ=0
    g46: LineSegment StartX=-49.19 StartY=5.75 StartZ=0 EndX=-1.5 EndY=5.75 EndZ=0
    g47: LineSegment StartX=-49.19 StartY=2.75 StartZ=0 EndX=-1.5 EndY=2.75 EndZ=0
  constraints (120):
    c: Vertical(g0)
    c: Distance(g0) = 3
    c: Block(g0)
    c: Vertical(g1)
    c: Distance(g1) = 3
    c: Vertical(g2)
    c: Equal(g0,g2) = 3
    c: Block(g2)
    c: Vertical(g3)
    c: Equal(g1,g3) = 3
    c: Vertical(g4)
    c: Equal(g0,g4) = 3
    c: Block(g4)
    c: Vertical(g5)
    c: Equal(g1,g5) = 3
    c: Vertical(g6)
    c: Equal(g0,g6) = 3
    c: Block(g6)
    c: Vertical(g7)
    c: Equal(g1,g7) = 3
    c: Vertical(g8)
    c: Equal(g0,g8) = 3
    c: Block(g8)
    c: Vertical(g9)
    c: Equal(g1,g9) = 3
    c: Vertical(g10)
    c: Equal(g0,g10) = 3
    c: Block(g10)
    c: Vertical(g11)
    c: Equal(g1,g11) = 3
    c: Block(g12)
    c: Block(g13)
    c: Block(g14)
    c: Block(g15)
    c: Block(g16)
    c: Block(g17)
    c: Block(g18)
    c: Block(g19)
    c: Block(g20)
    c: Block(g21)
    c: Block(g22)
    c: Block(g23)
    c: Block(g11)
    c: Block(g9)
    c: Block(g7)
    c: Block(g5)
    c: Block(g3)
    c: Block(g1)
    c: Coincident(g24,g0)
    c: Coincident(g24,g12)
    c: Horizontal(g24)
    c: Coincident(g25,g0)
    c: Coincident(g25,g12)
    c: Horizontal(g25)
    c: Coincident(g26,g1)
    c: Coincident(g26,g13)
    c: Horizontal(g26)
    c: Coincident(g27,g1)
    c: Coincident(g27,g13)
    c: Horizontal(g27)
    c: Coincident(g28,g2)
    c: Coincident(g28,g14)
    c: Horizontal(g28)
    c: Coincident(g29,g2)
    c: Coincident(g29,g14)
    c: Horizontal(g29)
    c: Coincident(g30,g3)
    c: Coincident(g30,g15)
    c: Horizontal(g30)
    c: Coincident(g31,g3)
    c: Coincident(g31,g15)
    c: Horizontal(g31)
    c: Coincident(g32,g4)
    c: Coincident(g32,g16)
    c: Horizontal(g32)
    c: Coincident(g33,g4)
    c: Coincident(g33,g16)
    c: Horizontal(g33)
    c: Coincident(g34,g5)
    c: Coincident(g34,g17)
    c: Horizontal(g34)
    c: Coincident(g35,g5)
    c: Coincident(g35,g17)
    c: Horizontal(g35)
    c: Coincident(g36,g6)
    c: Coincident(g36,g19)
    c: Horizontal(g36)
    c: Coincident(g37,g6)
    c: Coincident(g37,g19)
    c: Horizontal(g37)
    c: Coincident(g38,g7)
    c: Coincident(g38,g18)
    c: Horizontal(g38)
    c: Coincident(g39,g7)
    c: Coincident(g39,g18)
    c: Horizontal(g39)
    c: Coincident(g40,g8)
    c: Coincident(g40,g20)
    c: Horizontal(g40)
    c: Coincident(g41,g8)
    c: Coincident(g41,g20)
    c: Horizontal(g41)
    c: Coincident(g42,g9)
    c: Coincident(g42,g23)
    c: Horizontal(g42)
    c: Coincident(g43,g9)
    c: Coincident(g43,g23)
    c: Horizontal(g43)
    c: Coincident(g44,g10)
    c: Coincident(g44,g22)
    c: Horizontal(g44)
    c: Coincident(g45,g10)
    c: Coincident(g45,g22)
    c: Horizontal(g45)
    c: Coincident(g46,g11)
    c: Coincident(g46,g21)
    c: Horizontal(g46)
    c: Coincident(g47,g11)
    c: Coincident(g47,g21)
    c: Horizontal(g47)
FEATURE [Part::Extrusion] Extrude046
  Base = -> Sketch055
  Dir = (1,0,0)
  DirMode = 2
  FaceMakerClass = Part::FaceMakerBullseye
  LengthFwd = 23
  LengthRev = 0
  Placement = pos=(-19,0,0) rot=(0,0,1;0rad)
  Solid = true
  Symmetric = false
FEATURE [Part::Fillet] Fillet038  label="removeToCreateVentalationHoles001"
  Base = -> Extrude046
  Edges = <same value as first occurrence — deduplicated (x6 in doc)>
  Placement = pos=(7,0,0) rot=(0,0,1;0rad)
FEATURE [Sketcher::SketchObject] Sketch056  label="topSketch014"
  FullyConstrained = true
  sketch-geometry (22):
    g0: LineSegment StartX=5.21097e-06 StartY=3 StartZ=0 EndX=5.21097e-06 EndY=19 EndZ=0
    g1: ArcOfCircle CenterX=19 CenterY=19 CenterZ=0 NormalX=0 NormalY=0 NormalZ=1 AngleXU=0 Radius=19 StartAngle=1.5708 EndAngle=3.14159
    g2: ArcOfCircle CenterX=19 CenterY=19 CenterZ=0 NormalX=0 NormalY=0 NormalZ=1 AngleXU=0 Radius=16 StartAngle=1.5708 EndAngle=3.14159
    g3: LineSegment StartX=114 StartY=35 StartZ=0 EndX=19 EndY=35 EndZ=0
    g4: LineSegment StartX=5.21097e-06 StartY=3 StartZ=0 EndX=5.21097e-06 EndY=0 EndZ=0
    g5: LineSegment StartX=3 StartY=0 StartZ=0 EndX=5.21097e-06 EndY=0 EndZ=0
    g6: LineSegment StartX=3 StartY=19 StartZ=0 EndX=3 EndY=0 EndZ=0
    g7: LineSegment StartX=19 StartY=38 StartZ=0 EndX=124 EndY=38 EndZ=0
    g8: Circle CenterX=119 CenterY=35 CenterZ=0 NormalX=0 NormalY=0 NormalZ=1 AngleXU=0 Radius=1
    g9: Circle CenterX=121 CenterY=35 CenterZ=0 NormalX=0 NormalY=0 NormalZ=1 AngleXU=0 Radius=1
    g10: Circle CenterX=121 CenterY=33 CenterZ=0 NormalX=0 NormalY=0 NormalZ=1 AngleXU=0 Radius=1
    g11: BSplineCurve PolesCount=3 KnotsCount=2 Degree=2 IsPeriodic=0
    g12: GeomPoint X=119 Y=35 Z=0
    g13: GeomPoint X=121 Y=33 Z=0
    g14: LineSegment StartX=119 StartY=35 StartZ=0 EndX=114 EndY=35 EndZ=0
    g15: ArcOfCircle CenterX=105 CenterY=19 CenterZ=0 NormalX=0 NormalY=0 NormalZ=1 AngleXU=0 Radius=16 StartAngle=5.60905 EndAngle=6.28319
    g16: LineSegment StartX=121 StartY=33 StartZ=0 EndX=121 EndY=19 EndZ=0
    g17: LineSegment StartX=117.5 StartY=9.01251 StartZ=0 EndX=121.163 EndY=9.0125 EndZ=0
    g18: ArcOfCircle CenterX=105 CenterY=19 CenterZ=0 NormalX=0 NormalY=0 NormalZ=1 AngleXU=0 Radius=20.6155 StartAngle=5.7297 EndAngle=6.28319
    g19: LineSegment StartX=121.163 StartY=9.0125 StartZ=0 EndX=122.538 EndY=8.16329 EndZ=0
    g20: LineSegment StartX=124 StartY=38 StartZ=0 EndX=125.616 EndY=38 EndZ=0
    g21: LineSegment StartX=125.616 StartY=19 StartZ=0 EndX=125.616 EndY=38 EndZ=0
  constraints (49):
    c: Vertical(g0)
    c: Block(g0)
    c: Coincident(g1,g0)
    c: Block(g1)
    c: Coincident(g2,g1)
    c: Block(g2)
    c: Coincident(g3,g2)
    c: Horizontal(g3)
    c: Tangent(g3,g2)
    c: Coincident(g4,g0)
    c: Distance(g4) = 3
    c: Vertical(g4)
    c: Coincident(g5,g4)
    c: Horizontal(g5)
    c: Coincident(g6,g2)
    c: Coincident(g6,g5)
    c: Vertical(g6)
    c: Horizontal(g7)
    c: Distance(g7) = 105
    c: Coincident(g7,g1)
    c: Block(g3)
    c: Weight(g8) = 1
    c: Equal(g8,g9)
    c: Equal(g8,g10)
    c: InternalAlignment(g8,g11)
    c: InternalAlignment(g9,g11)
    c: InternalAlignment(g10,g11)
    c: InternalAlignment(g12,g11)
    c: InternalAlignment(g13,g11)
    c: Block(g11)
    c: Coincident(g14,g11)
    c: Coincident(g14,g3)
    c: Horizontal(g14)
    c: Block(g15)
    c: Coincident(g16,g11)
    c: Coincident(g16,g15)
    c: Vertical(g16)
    c: Distance(g16) = 14
    c: Coincident(g17,g15)
    c: Block(g18)
    c: Coincident(g19,g18)
    c: Coincident(g20,g7)
    c: Horizontal(g20)
    c: Vertical(g21)
    c: Coincident(g20,g21)
    c: Block(g20)
    c: Block(g21)
    c: Block(g19)
    c: Block(g17)
FEATURE [Part::Box] Box026  label="removeToCreteHoleForPlugHousing032"
  AttacherType = Attacher::AttachEngine3D
  Height = 28.6
  Length = 10
  Placement = pos=(-2,0,21.7) rot=(0,0,1;0rad)
  Width = 19
FEATURE [Part::Feature] Face109 .. Face112  x4 (patterned run collapsed; names and placements below)
  shape: bbox 3.5 x 17.8 x 2e-07 mm, 1 faces, 0 solids (baked)
FEATURE [Part::Revolution] Revolve117  label="removeToCreateScrewAndThreadedInsertHole045"
  Angle = 360
  Axis = (0,1,0)
  Base = (0,0,0)
  FaceMakerClass = Part::FaceMakerBullseye
  Placement = pos=(62.3,30.3,19.7) rot=(0,0,1;0rad)
  Solid = false
  Source = -> Face109
  Symmetric = false
FEATURE [Part::Revolution] Revolve118  label="removeToCreateScrewAndThreadedInsertHole046"
  Angle = 360
  Axis = (0,1,0)
  Base = (0,0,0)
  FaceMakerClass = Part::FaceMakerBullseye
  Placement = pos=(62.3,30.3,51.7) rot=(0,0,1;0rad)
  Solid = false
  Source = -> Face110
  Symmetric = false
FEATURE [Part::Revolution] Revolve119  label="removeToCreateScrewAndThreadedInsertHole047"
  Angle = 360
  Axis = (0,1,0)
  Base = (0,0,0)
  FaceMakerClass = Part::FaceMakerBullseye
  Placement = pos=(30.3,30.3,19.7) rot=(0,0,1;0rad)
  Solid = false
  Source = -> Face111
  Symmetric = false
FEATURE [Part::Revolution] Revolve120  label="removeToCreateScrewAndThreadedInsertHole048"
  Angle = 360
  Axis = (0,1,0)
  Base = (0,0,0)
  FaceMakerClass = Part::FaceMakerBullseye
  Placement = pos=(30.3,30.3,51.7) rot=(0,0,1;0rad)
  Solid = false
  Source = -> Face112
  Symmetric = false
FEATURE [Part::MultiFuse] Fusion087  label="createThreadedInsertHolesForFan005"
  Shapes = -> [Revolve117,Revolve118,Revolve119,Revolve120]
FEATURE [Part::Extrusion] Extrude047
  Base = -> Sketch056
  Dir = (0,0,1)
  DirMode = 2
  FaceMakerClass = Part::FaceMakerBullseye
  LengthFwd = 72
  LengthRev = 0
  Solid = true
  Symmetric = false
FEATURE [Part::Fillet] Fillet039  label="top019"
  Base = -> Extrude047
  Edges = 1 edges r=2: [Edge35]
FEATURE [Sketcher::SketchObject] Sketch057
  FullyConstrained = false
  Placement = pos=(0,0,0) rot=(1,0,0;1.5708rad)
  sketch-geometry (24):
    g0: ArcOfCircle CenterX=-4 CenterY=-10.5 CenterZ=0 NormalX=0 NormalY=0 NormalZ=1 AngleXU=0 Radius=1.5 StartAngle=6e-16 EndAngle=3.14159
    g1: ArcOfCircle CenterX=-34.2 CenterY=-10.5 CenterZ=0 NormalX=0 NormalY=0 NormalZ=1 AngleXU=0 Radius=1.5 StartAngle=0 EndAngle=3.14159
    g2: ArcOfCircle CenterX=-34.2 CenterY=-27.7 CenterZ=0 NormalX=0 NormalY=0 NormalZ=1 AngleXU=0 Radius=1.5 StartAngle=3.14159 EndAngle=6.28319
    g3: ArcOfCircle CenterX=-4 CenterY=-27.7 CenterZ=0 NormalX=0 NormalY=0 NormalZ=1 AngleXU=0 Radius=1.5 StartAngle=3.1416 EndAngle=6.28319
    g4: ArcOfCircle CenterX=-10 CenterY=-4.3 CenterZ=0 NormalX=0 NormalY=0 NormalZ=1 AngleXU=0 Radius=1.5 StartAngle=2e-16 EndAngle=3.14159
    g5: ArcOfCircle CenterX=-16.1 CenterY=-1.8 CenterZ=0 NormalX=0 NormalY=0 NormalZ=1 AngleXU=0 Radius=1.5 StartAngle=5e-16 EndAngle=3.14159
    g6: ArcOfCircle CenterX=-22.1 CenterY=-1.8 CenterZ=0 NormalX=0 NormalY=0 NormalZ=1 AngleXU=0 Radius=1.5 StartAngle=5e-16 EndAngle=3.14159
    g7: ArcOfCircle CenterX=-28.2 CenterY=-4.3 CenterZ=0 NormalX=0 NormalY=0 NormalZ=1 AngleXU=0 Radius=1.5 StartAngle=2e-16 EndAngle=3.14159
    g8: ArcOfCircle CenterX=-10 CenterY=-33.9 CenterZ=0 NormalX=0 NormalY=0 NormalZ=1 AngleXU=0 Radius=1.5 StartAngle=3.14159 EndAngle=6.28319
    g9: ArcOfCircle CenterX=-16.1 CenterY=-36.4 CenterZ=0 NormalX=0 NormalY=0 NormalZ=1 AngleXU=0 Radius=1.5 StartAngle=3.14159 EndAngle=6.28319
    g10: ArcOfCircle CenterX=-22.1 CenterY=-36.4 CenterZ=0 NormalX=0 NormalY=0 NormalZ=1 AngleXU=0 Radius=1.5 StartAngle=3.14159 EndAngle=6.28319
    g11: ArcOfCircle CenterX=-28.2 CenterY=-33.9 CenterZ=0 NormalX=0 NormalY=0 NormalZ=1 AngleXU=0 Radius=1.5 StartAngle=3.14159 EndAngle=6.28319
    g12: LineSegment StartX=-35.7 StartY=-10.5 StartZ=0 EndX=-35.7 EndY=-27.7 EndZ=0
    g13: LineSegment StartX=-32.7 StartY=-10.5 StartZ=0 EndX=-32.7 EndY=-27.7 EndZ=0
    g14: LineSegment StartX=-29.7 StartY=-33.9 StartZ=0 EndX=-29.7 EndY=-4.3 EndZ=0
    g15: LineSegment StartX=-26.7 StartY=-33.9 StartZ=0 EndX=-26.7 EndY=-4.3 EndZ=0
    g16: LineSegment StartX=-2.5 StartY=-10.5 StartZ=0 EndX=-2.5 EndY=-27.7 EndZ=0
    g17: LineSegment StartX=-8.5 StartY=-4.3 StartZ=0 EndX=-8.5 EndY=-33.9 EndZ=0
    g18: LineSegment StartX=-5.5 StartY=-10.5 StartZ=0 EndX=-5.5 EndY=-27.7 EndZ=0
    g19: LineSegment StartX=-11.5 StartY=-4.3 StartZ=0 EndX=-11.5 EndY=-33.9 EndZ=0
    g20: LineSegment StartX=-14.6 StartY=-1.8 StartZ=0 EndX=-14.6 EndY=-36.4 EndZ=0
    g21: LineSegment StartX=-17.6 StartY=-1.8 StartZ=0 EndX=-17.6 EndY=-36.4 EndZ=0
    g22: LineSegment StartX=-20.6 StartY=-36.4 StartZ=0 EndX=-20.6 EndY=-1.8 EndZ=0
    g23: LineSegment StartX=-23.6 StartY=-1.8 StartZ=0 EndX=-23.6 EndY=-36.4 EndZ=0
  constraints (48):
    c: Block(g0)
    c: Block(g1)
    c: Block(g2)
    c: Block(g3)
    c: Block(g4)
    c: Block(g5)
    c: Block(g6)
    c: Block(g7)
    c: Block(g8)
    c: Block(g9)
    c: Block(g10)
    c: Block(g11)
    c: Coincident(g12,g1)
    c: Coincident(g12,g2)
    c: Vertical(g12)
    c: Coincident(g13,g1)
    c: Coincident(g13,g2)
    c: Vertical(g13)
    c: Coincident(g14,g11)
    c: Coincident(g14,g7)
    c: Vertical(g14)
    c: Coincident(g15,g11)
    c: Coincident(g15,g7)
    c: Vertical(g15)
    c: Coincident(g16,g0)
    c: Coincident(g16,g3)
    c: Vertical(g16)
    c: Coincident(g17,g4)
    c: Coincident(g17,g8)
    c: Vertical(g17)
    c: Coincident(g18,g0)
    c: Coincident(g18,g3)
    c: Vertical(g18)
    c: Coincident(g19,g4)
    c: Coincident(g19,g8)
    c: Vertical(g19)
    c: Coincident(g20,g5)
    c: Coincident(g20,g9)
    c: Vertical(g20)
    c: Coincident(g21,g5)
    c: Coincident(g21,g9)
    c: Vertical(g21)
    c: Coincident(g22,g10)
    c: Coincident(g22,g6)
    c: Vertical(g22)
    c: Coincident(g23,g6)
    c: Coincident(g23,g10)
    c: Vertical(g23)
FEATURE [Part::Extrusion] Extrude048  label="removeToCreateFanGrillHoles004"
  Base = -> Sketch057
  Dir = (0,-1,6e-16)
  DirMode = 2
  FaceMakerClass = Part::FaceMakerBullseye
  LengthFwd = 10
  LengthRev = 0
  Placement = pos=(65.4,44,54.82) rot=(0,0,1;0rad)
  Solid = true
  Symmetric = false
FEATURE [Part::Cut] Cut040  label="top021"
  Base = -> Fillet039
  Tool = -> Extrude048
FEATURE [Part::Cylinder] Cylinder041  label="removeToCreteHoleForPlugHousing034"
  Angle = 360
  AttacherType = Attacher::AttachEngine3D
  Height = 20
  Placement = pos=(-2,19,36) rot=(0,1,0;1.5708rad)
  Radius = 14.3
FEATURE [Part::MultiFuse] Fusion089  label="removeToCreteHoleForPlugHousing035"
  Shapes = -> [Box026,Cylinder041]
FEATURE [Part::Cylinder] Cylinder042
  Angle = 360
  AttacherType = Attacher::AttachEngine3D
  Height = 20
  Placement = pos=(0,0,36.15) rot=(0,0,1;0rad)
  Radius = 14.3
FEATURE [Part::Cylinder] Cylinder043
  Angle = 360
  AttacherType = Attacher::AttachEngine3D
  Height = 10
  Placement = pos=(0,0,36.15) rot=(0,0,1;0rad)
  Radius = 4
FEATURE [Part::Box] Box027  label="removeToCreteHoleForPlugHousing036"
  AttacherType = Attacher::AttachEngine3D
  Height = 28.6
  Length = 20
  Placement = pos=(106.15,0,21.7) rot=(0,0,1;0rad)
  Width = 19
FEATURE [Part::Cut] Cut041  label="top022"
  Base = -> Cut040
  Tool = -> Fusion087
FEATURE [Part::Cut] Cut039  label="top020"
  Base = -> Cut041
  Tool = -> Fusion089
FEATURE [Part::MultiFuse] Fusion090  label="removeToCreteHoleForPlugHousing037"
  Placement = pos=(70,19,36) rot=(0,1,0;1.5708rad)
  Shapes = -> [Cylinder042,Cylinder043]
FEATURE [Part::MultiFuse] Fusion088  label="removeToCreteHoleForPlugHousing033"
  Shapes = -> [Box027,Fusion090]
FEATURE [Part::Cut] Cut042  label="removeToCreteHoleForPlugHousing038"
  Base = -> Cut039
  Tool = -> Fusion088
FEATURE [Part::MultiFuse] Fusion091  label="removeFromTop"
  Shapes = -> [Fillet038,Fusion085,Fusion084,Fusion083,Extrude045]
FEATURE [Part::Cut] Cut043  label="REAL TOP ====="
  Base = -> Fillet036
  Tool = -> Fusion091
FEATURE [Part::MultiFuse] Fusion092  label="caseScrewPillarBracket016"
  Shapes = -> [Extrude030,Extrude031,Extrude032,Extrude033,Extrude034,Extrude035,Extrude036,Extrude037,Box013,Box014]
FEATURE [Sketcher::SketchObject] Sketch058  label="topSketch015"
  FullyConstrained = true
  sketch-geometry (20):
    g0: LineSegment StartX=5.21097e-06 StartY=3 StartZ=0 EndX=5.21097e-06 EndY=19 EndZ=0
    g1: ArcOfCircle CenterX=19 CenterY=19 CenterZ=0 NormalX=0 NormalY=0 NormalZ=1 AngleXU=0 Radius=19 StartAngle=1.5708 EndAngle=3.14159
    g2: ArcOfCircle CenterX=19 CenterY=19 CenterZ=0 NormalX=0 NormalY=0 NormalZ=1 AngleXU=0 Radius=16 StartAngle=1.5708 EndAngle=3.14159
    g3: LineSegment StartX=114 StartY=35 StartZ=0 EndX=19 EndY=35 EndZ=0
    g4: LineSegment StartX=5.21097e-06 StartY=3 StartZ=0 EndX=5.21097e-06 EndY=0 EndZ=0
    g5: LineSegment StartX=3 StartY=0 StartZ=0 EndX=5.21097e-06 EndY=0 EndZ=0
    g6: LineSegment StartX=3 StartY=19 StartZ=0 EndX=3 EndY=0 EndZ=0
    g7: LineSegment StartX=19 StartY=38 StartZ=0 EndX=124 EndY=38 EndZ=0
    g8: Circle CenterX=119 CenterY=35 CenterZ=0 NormalX=0 NormalY=0 NormalZ=1 AngleXU=0 Radius=1
    g9: Circle CenterX=121 CenterY=35 CenterZ=0 NormalX=0 NormalY=0 NormalZ=1 AngleXU=0 Radius=1
    g10: Circle CenterX=121 CenterY=33 CenterZ=0 NormalX=0 NormalY=0 NormalZ=1 AngleXU=0 Radius=1
    g11: BSplineCurve PolesCount=3 KnotsCount=2 Degree=2 IsPeriodic=0
    g12: GeomPoint X=119 Y=35 Z=0
    g13: GeomPoint X=121 Y=33 Z=0
    g14: LineSegment StartX=119 StartY=35 StartZ=0 EndX=114 EndY=35 EndZ=0
    g15: ArcOfCircle CenterX=105 CenterY=19 CenterZ=0 NormalX=0 NormalY=0 NormalZ=1 AngleXU=0 Radius=19 StartAngle=5.7297 EndAngle=6.28319
    g16: ArcOfCircle CenterX=105 CenterY=19 CenterZ=0 NormalX=0 NormalY=0 NormalZ=1 AngleXU=0 Radius=16 StartAngle=5.60905 EndAngle=6.28319
    g17: LineSegment StartX=121 StartY=33 StartZ=0 EndX=121 EndY=19 EndZ=0
    g18: LineSegment StartX=124 StartY=38 StartZ=0 EndX=124 EndY=19 EndZ=0
    g19: LineSegment StartX=117.5 StartY=9.01251 StartZ=0 EndX=121.163 EndY=9.0125 EndZ=0
  constraints (46):
    c: Vertical(g0)
    c: Block(g0)
    c: Coincident(g1,g0)
    c: Block(g1)
    c: Coincident(g2,g1)
    c: Block(g2)
    c: Coincident(g3,g2)
    c: Horizontal(g3)
    c: Tangent(g3,g2)
    c: Coincident(g4,g0)
    c: Distance(g4) = 3
    c: Vertical(g4)
    c: Coincident(g5,g4)
    c: Horizontal(g5)
    c: Coincident(g6,g2)
    c: Coincident(g6,g5)
    c: Vertical(g6)
    c: Horizontal(g7)
    c: Distance(g7) = 105
    c: Coincident(g7,g1)
    c: Block(g3)
    c: Weight(g8) = 1
    c: Equal(g8,g9)
    c: Equal(g8,g10)
    c: InternalAlignment(g8,g11)
    c: InternalAlignment(g9,g11)
    c: InternalAlignment(g10,g11)
    c: InternalAlignment(g12,g11)
    c: InternalAlignment(g13,g11)
    c: Block(g11)
    c: Coincident(g14,g11)
    c: Coincident(g14,g3)
    c: Horizontal(g14)
    c: Block(g15)
    c: Coincident(g16,g15)
    c: Block(g16)
    c: Coincident(g17,g11)
    c: Coincident(g17,g16)
    c: Vertical(g17)
    c: Distance(g17) = 14
    c: Coincident(g18,g7)
    c: Coincident(g18,g15)
    c: Vertical(g18)
    c: Distance(g18) = 19
    c: Coincident(g19,g16)
    c: Coincident(g19,g15)
FEATURE [Part::Extrusion] Extrude049  label="top023"
  Base = -> Sketch058
  Dir = (0,0,1)
  DirMode = 2
  FaceMakerClass = Part::FaceMakerBullseye
  LengthFwd = 72
  LengthRev = 0
  Solid = true
  Symmetric = false
FEATURE [Sketcher::SketchObject] Sketch059
  FullyConstrained = true
  MapMode = 3
  Placement = pos=(0,0,0) rot=(1,0,0;1.5708rad)
  Support = -> [Extrude049]
  sketch-geometry (8):
    g0: Circle CenterX=80.351 CenterY=-67.6202 CenterZ=0 NormalX=0 NormalY=0 NormalZ=1 AngleXU=0 Radius=2
    g1: Circle CenterX=80.351 CenterY=-67.6202 CenterZ=0 NormalX=0 NormalY=0 NormalZ=1 AngleXU=0 Radius=3
    g2: Circle CenterX=80.351 CenterY=-4.92017 CenterZ=0 NormalX=0 NormalY=0 NormalZ=1 AngleXU=0 Radius=2
    g3: Circle CenterX=80.351 CenterY=-4.92017 CenterZ=0 NormalX=0 NormalY=0 NormalZ=1 AngleXU=0 Radius=3
    g4: Circle CenterX=23.851 CenterY=-4.92017 CenterZ=0 NormalX=0 NormalY=0 NormalZ=1 AngleXU=0 Radius=2
    g5: Circle CenterX=23.851 CenterY=-4.92017 CenterZ=0 NormalX=0 NormalY=0 NormalZ=1 AngleXU=0 Radius=3
    g6: Circle CenterX=23.851 CenterY=-67.6202 CenterZ=0 NormalX=0 NormalY=0 NormalZ=1 AngleXU=0 Radius=2
    g7: Circle CenterX=23.851 CenterY=-67.6202 CenterZ=0 NormalX=0 NormalY=0 NormalZ=1 AngleXU=0 Radius=3
  constraints (8):
    c: Block(g3)
    c: Block(g2)
    c: Block(g1)
    c: Block(g0)
    c: Block(g6)
    c: Block(g7)
    c: Block(g4)
    c: Block(g5)
FEATURE [Sketcher::SketchObject] Sketch060
  FullyConstrained = true
  MapMode = 3
  Placement = pos=(0,0,0) rot=(1,0,0;1.5708rad)
  Support = -> [Extrude049]
  sketch-geometry (8):
    g0: Circle CenterX=80.351 CenterY=-67.6202 CenterZ=0 NormalX=0 NormalY=0 NormalZ=1 AngleXU=0 Radius=3
    g1: Circle CenterX=80.351 CenterY=-4.92017 CenterZ=0 NormalX=0 NormalY=0 NormalZ=1 AngleXU=0 Radius=3
    g2: Circle CenterX=23.851 CenterY=-4.92017 CenterZ=0 NormalX=0 NormalY=0 NormalZ=1 AngleXU=0 Radius=3
    g3: Circle CenterX=23.851 CenterY=-67.6202 CenterZ=0 NormalX=0 NormalY=0 NormalZ=1 AngleXU=0 Radius=3
    g4: Circle CenterX=23.851 CenterY=-67.6202 CenterZ=0 NormalX=0 NormalY=0 NormalZ=1 AngleXU=0 Radius=5
    g5: Circle CenterX=80.351 CenterY=-67.6202 CenterZ=0 NormalX=0 NormalY=0 NormalZ=1 AngleXU=0 Radius=5
    g6: Circle CenterX=23.851 CenterY=-4.92017 CenterZ=0 NormalX=0 NormalY=0 NormalZ=1 AngleXU=0 Radius=5
    g7: Circle CenterX=80.351 CenterY=-4.92017 CenterZ=0 NormalX=0 NormalY=0 NormalZ=1 AngleXU=0 Radius=5
  constraints (8):
    c: Block(g1)
    c: Block(g0)
    c: Block(g3)
    c: Block(g2)
    c: Block(g5)
    c: Block(g4)
    c: Block(g6)
    c: Block(g7)
FEATURE [Sketcher::SketchObject] Sketch061
  FullyConstrained = true
  MapMode = 3
  Placement = pos=(0,0,0) rot=(1,0,0;1.5708rad)
  sketch-geometry (8):
    g0: Circle CenterX=80.351 CenterY=-67.6202 CenterZ=0 NormalX=0 NormalY=0 NormalZ=1 AngleXU=0 Radius=3
    g1: Circle CenterX=80.351 CenterY=-4.92017 CenterZ=0 NormalX=0 NormalY=0 NormalZ=1 AngleXU=0 Radius=3
    g2: Circle CenterX=23.851 CenterY=-4.92017 CenterZ=0 NormalX=0 NormalY=0 NormalZ=1 AngleXU=0 Radius=3
    g3: Circle CenterX=23.851 CenterY=-67.6202 CenterZ=0 NormalX=0 NormalY=0 NormalZ=1 AngleXU=0 Radius=3
    g4: Circle CenterX=23.851 CenterY=-67.6202 CenterZ=0 NormalX=0 NormalY=0 NormalZ=1 AngleXU=0 Radius=5
    g5: Circle CenterX=80.351 CenterY=-67.6202 CenterZ=0 NormalX=0 NormalY=0 NormalZ=1 AngleXU=0 Radius=5
    g6: Circle CenterX=23.851 CenterY=-4.92017 CenterZ=0 NormalX=0 NormalY=0 NormalZ=1 AngleXU=0 Radius=5
    g7: Circle CenterX=80.351 CenterY=-4.92017 CenterZ=0 NormalX=0 NormalY=0 NormalZ=1 AngleXU=0 Radius=5
  constraints (8):
    c: Block(g1)
    c: Block(g0)
    c: Block(g3)
    c: Block(g2)
    c: Block(g5)
    c: Block(g4)
    c: Block(g6)
    c: Block(g7)
FEATURE [Sketcher::SketchObject] Sketch062  label="topSketch016"
  FullyConstrained = true
  sketch-geometry (20):
    g0: LineSegment StartX=5.21097e-06 StartY=3 StartZ=0 EndX=5.21097e-06 EndY=19 EndZ=0
    g1: ArcOfCircle CenterX=19 CenterY=19 CenterZ=0 NormalX=0 NormalY=0 NormalZ=1 AngleXU=0 Radius=19 StartAngle=1.5708 EndAngle=3.14159
    g2: ArcOfCircle CenterX=19 CenterY=19 CenterZ=0 NormalX=0 NormalY=0 NormalZ=1 AngleXU=0 Radius=16 StartAngle=1.5708 EndAngle=3.14159
    g3: LineSegment StartX=114 StartY=35 StartZ=0 EndX=19 EndY=35 EndZ=0
    g4: LineSegment StartX=5.21097e-06 StartY=3 StartZ=0 EndX=5.21097e-06 EndY=0 EndZ=0
    g5: LineSegment StartX=3 StartY=0 StartZ=0 EndX=5.21097e-06 EndY=0 EndZ=0
    g6: LineSegment StartX=3 StartY=19 StartZ=0 EndX=3 EndY=0 EndZ=0
    g7: LineSegment StartX=19 StartY=38 StartZ=0 EndX=124 EndY=38 EndZ=0
    g8: Circle CenterX=119 CenterY=35 CenterZ=0 NormalX=0 NormalY=0 NormalZ=1 AngleXU=0 Radius=1
    g9: Circle CenterX=121 CenterY=35 CenterZ=0 NormalX=0 NormalY=0 NormalZ=1 AngleXU=0 Radius=1
    g10: Circle CenterX=121 CenterY=33 CenterZ=0 NormalX=0 NormalY=0 NormalZ=1 AngleXU=0 Radius=1
    g11: BSplineCurve PolesCount=3 KnotsCount=2 Degree=2 IsPeriodic=0
    g12: GeomPoint X=119 Y=35 Z=0
    g13: GeomPoint X=121 Y=33 Z=0
    g14: LineSegment StartX=119 StartY=35 StartZ=0 EndX=114 EndY=35 EndZ=0
    g15: ArcOfCircle CenterX=105 CenterY=19 CenterZ=0 NormalX=0 NormalY=0 NormalZ=1 AngleXU=0 Radius=19 StartAngle=5.7297 EndAngle=6.28319
    g16: ArcOfCircle CenterX=105 CenterY=19 CenterZ=0 NormalX=0 NormalY=0 NormalZ=1 AngleXU=0 Radius=16 StartAngle=5.60905 EndAngle=6.28319
    g17: LineSegment StartX=121 StartY=33 StartZ=0 EndX=121 EndY=19 EndZ=0
    g18: LineSegment StartX=124 StartY=38 StartZ=0 EndX=124 EndY=19 EndZ=0
    g19: LineSegment StartX=117.5 StartY=9.01251 StartZ=0 EndX=121.163 EndY=9.0125 EndZ=0
  constraints (46):
    c: Vertical(g0)
    c: Block(g0)
    c: Coincident(g1,g0)
    c: Block(g1)
    c: Coincident(g2,g1)
    c: Block(g2)
    c: Coincident(g3,g2)
    c: Horizontal(g3)
    c: Tangent(g3,g2)
    c: Coincident(g4,g0)
    c: Distance(g4) = 3
    c: Vertical(g4)
    c: Coincident(g5,g4)
    c: Horizontal(g5)
    c: Coincident(g6,g2)
    c: Coincident(g6,g5)
    c: Vertical(g6)
    c: Horizontal(g7)
    c: Distance(g7) = 105
    c: Coincident(g7,g1)
    c: Block(g3)
    c: Weight(g8) = 1
    c: Equal(g8,g9)
    c: Equal(g8,g10)
    c: InternalAlignment(g8,g11)
    c: InternalAlignment(g9,g11)
    c: InternalAlignment(g10,g11)
    c: InternalAlignment(g12,g11)
    c: InternalAlignment(g13,g11)
    c: Block(g11)
    c: Coincident(g14,g11)
    c: Coincident(g14,g3)
    c: Horizontal(g14)
    c: Block(g15)
    c: Coincident(g16,g15)
    c: Block(g16)
    c: Coincident(g17,g11)
    c: Coincident(g17,g16)
    c: Vertical(g17)
    c: Distance(g17) = 14
    c: Coincident(g18,g7)
    c: Coincident(g18,g15)
    c: Vertical(g18)
    c: Distance(g18) = 19
    c: Coincident(g19,g16)
    c: Coincident(g19,g15)
FEATURE [Part::Extrusion] Extrude053  label="top024"
  Base = -> Sketch062
  Dir = (0,0,1)
  DirMode = 2
  FaceMakerClass = Part::FaceMakerBullseye
  LengthFwd = 72
  LengthRev = 0
  Solid = true
  Symmetric = false
FEATURE [Sketcher::SketchObject] Sketch063
  FullyConstrained = true
  MapMode = 3
  Placement = pos=(0,0,0) rot=(1,0,0;1.5708rad)
  Support = -> [Extrude053]
  sketch-geometry (8):
    g0: Circle CenterX=80.351 CenterY=-67.6202 CenterZ=0 NormalX=0 NormalY=0 NormalZ=1 AngleXU=0 Radius=2
    g1: Circle CenterX=80.351 CenterY=-67.6202 CenterZ=0 NormalX=0 NormalY=0 NormalZ=1 AngleXU=0 Radius=3
    g2: Circle CenterX=80.351 CenterY=-4.92017 CenterZ=0 NormalX=0 NormalY=0 NormalZ=1 AngleXU=0 Radius=2
    g3: Circle CenterX=80.351 CenterY=-4.92017 CenterZ=0 NormalX=0 NormalY=0 NormalZ=1 AngleXU=0 Radius=3
    g4: Circle CenterX=23.851 CenterY=-4.92017 CenterZ=0 NormalX=0 NormalY=0 NormalZ=1 AngleXU=0 Radius=2
    g5: Circle CenterX=23.851 CenterY=-4.92017 CenterZ=0 NormalX=0 NormalY=0 NormalZ=1 AngleXU=0 Radius=3
    g6: Circle CenterX=23.851 CenterY=-67.6202 CenterZ=0 NormalX=0 NormalY=0 NormalZ=1 AngleXU=0 Radius=2
    g7: Circle CenterX=23.851 CenterY=-67.6202 CenterZ=0 NormalX=0 NormalY=0 NormalZ=1 AngleXU=0 Radius=3
  constraints (8):
    c: Block(g3)
    c: Block(g2)
    c: Block(g1)
    c: Block(g0)
    c: Block(g6)
    c: Block(g7)
    c: Block(g4)
    c: Block(g5)
FEATURE [Part::Extrusion] Extrude054
  Base = -> Sketch063
  Dir = (0,-1,2e-16)
  DirMode = 2
  FaceMakerClass = Part::FaceMakerBullseye
  LengthFwd = 6
  LengthRev = 0
  Placement = pos=(0,9,0) rot=(0,0,1;0rad)
  Solid = true
  Symmetric = false
FEATURE [Sketcher::SketchObject] Sketch064  label="topSketch017"
  FullyConstrained = true
  sketch-geometry (20):
    g0: LineSegment StartX=5.21097e-06 StartY=3 StartZ=0 EndX=5.21097e-06 EndY=19 EndZ=0
    g1: ArcOfCircle CenterX=19 CenterY=19 CenterZ=0 NormalX=0 NormalY=0 NormalZ=1 AngleXU=0 Radius=19 StartAngle=1.5708 EndAngle=3.14159
    g2: ArcOfCircle CenterX=19 CenterY=19 CenterZ=0 NormalX=0 NormalY=0 NormalZ=1 AngleXU=0 Radius=16 StartAngle=1.5708 EndAngle=3.14159
    g3: LineSegment StartX=114 StartY=35 StartZ=0 EndX=19 EndY=35 EndZ=0
    g4: LineSegment StartX=5.21097e-06 StartY=3 StartZ=0 EndX=5.21097e-06 EndY=0 EndZ=0
    g5: LineSegment StartX=3 StartY=0 StartZ=0 EndX=5.21097e-06 EndY=0 EndZ=0
    g6: LineSegment StartX=3 StartY=19 StartZ=0 EndX=3 EndY=0 EndZ=0
    g7: LineSegment StartX=19 StartY=38 StartZ=0 EndX=124 EndY=38 EndZ=0
    g8: Circle CenterX=119 CenterY=35 CenterZ=0 NormalX=0 NormalY=0 NormalZ=1 AngleXU=0 Radius=1
    g9: Circle CenterX=121 CenterY=35 CenterZ=0 NormalX=0 NormalY=0 NormalZ=1 AngleXU=0 Radius=1
    g10: Circle CenterX=121 CenterY=33 CenterZ=0 NormalX=0 NormalY=0 NormalZ=1 AngleXU=0 Radius=1
    g11: BSplineCurve PolesCount=3 KnotsCount=2 Degree=2 IsPeriodic=0
    g12: GeomPoint X=119 Y=35 Z=0
    g13: GeomPoint X=121 Y=33 Z=0
    g14: LineSegment StartX=119 StartY=35 StartZ=0 EndX=114 EndY=35 EndZ=0
    g15: ArcOfCircle CenterX=105 CenterY=19 CenterZ=0 NormalX=0 NormalY=0 NormalZ=1 AngleXU=0 Radius=19 StartAngle=5.7297 EndAngle=6.28319
    g16: ArcOfCircle CenterX=105 CenterY=19 CenterZ=0 NormalX=0 NormalY=0 NormalZ=1 AngleXU=0 Radius=16 StartAngle=5.60905 EndAngle=6.28319
    g17: LineSegment StartX=121 StartY=33 StartZ=0 EndX=121 EndY=19 EndZ=0
    g18: LineSegment StartX=124 StartY=38 StartZ=0 EndX=124 EndY=19 EndZ=0
    g19: LineSegment StartX=117.5 StartY=9.01251 StartZ=0 EndX=121.163 EndY=9.0125 EndZ=0
  constraints (46):
    c: Vertical(g0)
    c: Block(g0)
    c: Coincident(g1,g0)
    c: Block(g1)
    c: Coincident(g2,g1)
    c: Block(g2)
    c: Coincident(g3,g2)
    c: Horizontal(g3)
    c: Tangent(g3,g2)
    c: Coincident(g4,g0)
    c: Distance(g4) = 3
    c: Vertical(g4)
    c: Coincident(g5,g4)
    c: Horizontal(g5)
    c: Coincident(g6,g2)
    c: Coincident(g6,g5)
    c: Vertical(g6)
    c: Horizontal(g7)
    c: Distance(g7) = 105
    c: Coincident(g7,g1)
    c: Block(g3)
    c: Weight(g8) = 1
    c: Equal(g8,g9)
    c: Equal(g8,g10)
    c: InternalAlignment(g8,g11)
    c: InternalAlignment(g9,g11)
    c: InternalAlignment(g10,g11)
    c: InternalAlignment(g12,g11)
    c: InternalAlignment(g13,g11)
    c: Block(g11)
    c: Coincident(g14,g11)
    c: Coincident(g14,g3)
    c: Horizontal(g14)
    c: Block(g15)
    c: Coincident(g16,g15)
    c: Block(g16)
    c: Coincident(g17,g11)
    c: Coincident(g17,g16)
    c: Vertical(g17)
    c: Distance(g17) = 14
    c: Coincident(g18,g7)
    c: Coincident(g18,g15)
    c: Vertical(g18)
    c: Distance(g18) = 19
    c: Coincident(g19,g16)
    c: Coincident(g19,g15)
FEATURE [Sketcher::SketchObject] Sketch065
  FullyConstrained = true
  MapMode = 3
  Placement = pos=(0,0,0) rot=(1,0,0;1.5708rad)
  sketch-geometry (8):
    g0: Circle CenterX=80.351 CenterY=-67.6202 CenterZ=0 NormalX=0 NormalY=0 NormalZ=1 AngleXU=0 Radius=3
    g1: Circle CenterX=80.351 CenterY=-4.92017 CenterZ=0 NormalX=0 NormalY=0 NormalZ=1 AngleXU=0 Radius=3
    g2: Circle CenterX=23.851 CenterY=-4.92017 CenterZ=0 NormalX=0 NormalY=0 NormalZ=1 AngleXU=0 Radius=3
    g3: Circle CenterX=23.851 CenterY=-67.6202 CenterZ=0 NormalX=0 NormalY=0 NormalZ=1 AngleXU=0 Radius=3
    g4: Circle CenterX=23.851 CenterY=-67.6202 CenterZ=0 NormalX=0 NormalY=0 NormalZ=1 AngleXU=0 Radius=5
    g5: Circle CenterX=80.351 CenterY=-67.6202 CenterZ=0 NormalX=0 NormalY=0 NormalZ=1 AngleXU=0 Radius=5
    g6: Circle CenterX=23.851 CenterY=-4.92017 CenterZ=0 NormalX=0 NormalY=0 NormalZ=1 AngleXU=0 Radius=5
    g7: Circle CenterX=80.351 CenterY=-4.92017 CenterZ=0 NormalX=0 NormalY=0 NormalZ=1 AngleXU=0 Radius=5
  constraints (8):
    c: Block(g1)
    c: Block(g0)
    c: Block(g3)
    c: Block(g2)
    c: Block(g5)
    c: Block(g4)
    c: Block(g6)
    c: Block(g7)
FEATURE [Part::Extrusion] Extrude056
  Base = -> Sketch065
  Dir = (0,-1,2e-16)
  DirMode = 2
  FaceMakerClass = Part::FaceMakerBullseye
  LengthFwd = 2
  LengthRev = 0
  Solid = true
  Symmetric = false
FEATURE [Part::Extrusion] Extrude057  label="top025"
  Base = -> Sketch064
  Dir = (0,0,1)
  DirMode = 2
  FaceMakerClass = Part::FaceMakerBullseye
  LengthFwd = 72
  LengthRev = 0
  Solid = true
  Symmetric = false
FEATURE [Sketcher::SketchObject] Sketch066
  FullyConstrained = true
  MapMode = 3
  Placement = pos=(0,0,0) rot=(1,0,0;1.5708rad)
  Support = -> [Extrude057]
  sketch-geometry (8):
    g0: Circle CenterX=80.351 CenterY=-67.6202 CenterZ=0 NormalX=0 NormalY=0 NormalZ=1 AngleXU=0 Radius=3
    g1: Circle CenterX=80.351 CenterY=-4.92017 CenterZ=0 NormalX=0 NormalY=0 NormalZ=1 AngleXU=0 Radius=3
    g2: Circle CenterX=23.851 CenterY=-4.92017 CenterZ=0 NormalX=0 NormalY=0 NormalZ=1 AngleXU=0 Radius=3
    g3: Circle CenterX=23.851 CenterY=-67.6202 CenterZ=0 NormalX=0 NormalY=0 NormalZ=1 AngleXU=0 Radius=3
    g4: Circle CenterX=23.851 CenterY=-67.6202 CenterZ=0 NormalX=0 NormalY=0 NormalZ=1 AngleXU=0 Radius=5
    g5: Circle CenterX=80.351 CenterY=-67.6202 CenterZ=0 NormalX=0 NormalY=0 NormalZ=1 AngleXU=0 Radius=5
    g6: Circle CenterX=23.851 CenterY=-4.92017 CenterZ=0 NormalX=0 NormalY=0 NormalZ=1 AngleXU=0 Radius=5
    g7: Circle CenterX=80.351 CenterY=-4.92017 CenterZ=0 NormalX=0 NormalY=0 NormalZ=1 AngleXU=0 Radius=5
  constraints (8):
    c: Block(g1)
    c: Block(g0)
    c: Block(g3)
    c: Block(g2)
    c: Block(g5)
    c: Block(g4)
    c: Block(g6)
    c: Block(g7)
FEATURE [Part::Extrusion] Extrude055
  Base = -> Sketch066
  Dir = (0,-1,2e-16)
  DirMode = 2
  FaceMakerClass = Part::FaceMakerBullseye
  LengthFwd = 2
  LengthRev = 0
  Solid = true
  Symmetric = false
FEATURE [Part::Fillet] Fillet041
  Base = -> Extrude056
  Edges = 4 edges r=1.99: [Edge6,Edge12,Edge18,Edge24]
FEATURE [Part::Cut] Cut045
  Base = -> Extrude055
  Placement = pos=(0,6,0) rot=(0,0,1;0rad)
  Tool = -> Fillet041
FEATURE [Part::MultiFuse] Fusion095  label="pcbScrewPillars"
  Placement = pos=(-3.2,-1,72.3) rot=(0,0,1;0rad)
  Shapes = -> [Cut045,Extrude054]
FEATURE [Part::Feature] Face113
  shape: bbox 3.2 x 1.5 x 2e-07 mm, 1 faces, 0 solids (baked)
FEATURE [Part::Revolution] Revolve121  label="backCaseScrewRetainer002"
  Angle = 360
  Axis = (0,1,0)
  Base = (0,0,0)
  FaceMakerClass = Part::FaceMakerBullseye
  Placement = pos=(12.5,3,62) rot=(0,0,1;0rad)
  Solid = false
  Source = -> Face113
  Symmetric = false
FEATURE [Part::Feature] Face114
  shape: bbox 3.2 x 1.5 x 2e-07 mm, 1 faces, 0 solids (baked)
FEATURE [Part::Feature] Face115
  shape: bbox 3.2 x 1.5 x 2e-07 mm, 1 faces, 0 solids (baked)
FEATURE [Part::Feature] Face116
  shape: bbox 3.2 x 1.5 x 2e-07 mm, 1 faces, 0 solids (baked)
FEATURE [Part::Revolution] Revolve122  label="frontCaseScrewRetainer004"
  Angle = 360
  Axis = (0,1,0)
  Base = (0,0,0)
  FaceMakerClass = Part::FaceMakerBullseye
  Placement = pos=(89.5,3,68.5) rot=(0,0,1;0rad)
  Solid = false
  Source = -> Face115
  Symmetric = false
FEATURE [Part::Revolution] Revolve123  label="frontCaseScrewRetainer005"
  Angle = 360
  Axis = (0,1,0)
  Base = (0,0,0)
  FaceMakerClass = Part::FaceMakerBullseye
  Placement = pos=(89.5,3,3.5) rot=(0,0,1;0rad)
  Solid = false
  Source = -> Face116
  Symmetric = false
FEATURE [Part::Revolution] Revolve124  label="backCaseScrewRetainer003"
  Angle = 360
  Axis = (0,1,0)
  Base = (0,0,0)
  FaceMakerClass = Part::FaceMakerBullseye
  Placement = pos=(12.5,3,10) rot=(0,0,1;0rad)
  Solid = false
  Source = -> Face114
  Symmetric = false
FEATURE [Part::Feature] Face117
  shape: bbox 3.6 x 3.2 x 2e-07 mm, 1 faces, 0 solids (baked)
FEATURE [Part::Revolution] Revolve125  label="moreFrontCaseScrewRetainer004"
  Angle = 360
  Axis = (0,1,0)
  Base = (0,0,0)
  FaceMakerClass = Part::FaceMakerBullseye
  Placement = pos=(109.5,4.5,68.5) rot=(0,0,1;0rad)
  Solid = false
  Source = -> Face117
  Symmetric = false
FEATURE [Part::Feature] Face118
  shape: bbox 3.6 x 3.2 x 2e-07 mm, 1 faces, 0 solids (baked)
FEATURE [Part::Revolution] Revolve126  label="moreFrontCaseScrewRetainer005"
  Angle = 360
  Axis = (0,1,0)
  Base = (0,0,0)
  FaceMakerClass = Part::FaceMakerBullseye
  Placement = pos=(109.5,4.5,3.5) rot=(0,0,1;0rad)
  Solid = false
  Source = -> Face118
  Symmetric = false
FEATURE [Part::MultiFuse] Fusion096  label="screwRetainers001"
  Shapes = -> [Revolve126,Revolve125,Revolve124,Revolve123,Revolve122,Revolve121]
FEATURE [Part::Feature] Face119
  shape: bbox 10 x 16.5 x 2e-07 mm, 1 faces, 0 solids (baked)
FEATURE [Part::Revolution] Revolve130  label="plugHousing050"
  Angle = 360
  Axis = (0,1,0)
  Base = (0,0,0)
  FaceMakerClass = Part::FaceMakerBullseye
  Placement = pos=(0,0,36.15) rot=(0,0,1;0rad)
  Solid = false
  Source = -> Face119
  Symmetric = false
FEATURE [Part::Feature] Face120
  shape: bbox 10 x 16.5 x 2e-07 mm, 1 faces, 0 solids (baked)
FEATURE [Part::Feature] Face121
  shape: bbox 10 x 16.5 x 2e-07 mm, 1 faces, 0 solids (baked)
FEATURE [Part::Revolution] Revolve127  label="plugHousing047"
  Angle = 360
  Axis = (0,1,0)
  Base = (0,0,0)
  FaceMakerClass = Part::FaceMakerBullseye
  Placement = pos=(0,0,36.15) rot=(0,0,1;0rad)
  Solid = false
  Source = -> Face121
  Symmetric = false
FEATURE [Part::Feature] Face122
  shape: bbox 10 x 16.5 x 2e-07 mm, 1 faces, 0 solids (baked)
FEATURE [Part::Feature] Face123
  shape: bbox 10 x 16.5 x 2e-07 mm, 1 faces, 0 solids (baked)
FEATURE [Part::Revolution] Revolve128  label="plugHousing048"
  Angle = 360
  Axis = (0,1,0)
  Base = (0,0,0)
  FaceMakerClass = Part::FaceMakerBullseye
  Placement = pos=(0,0,36.15) rot=(0,0,1;0rad)
  Solid = false
  Source = -> Face123
  Symmetric = false
FEATURE [Part::MultiFuse] Fusion100  label="plugHousing054"
  Placement = pos=(0,0,0) rot=(0,0,1;1.5708rad)
  Shapes = -> [Revolve130,Revolve128]
FEATURE [Part::Feature] Face124
  shape: bbox 10 x 16.5 x 2e-07 mm, 1 faces, 0 solids (baked)
FEATURE [Part::Feature] Face125
  shape: bbox 10 x 16.5 x 2e-07 mm, 1 faces, 0 solids (baked)
FEATURE [Part::Revolution] Revolve129  label="plugHousing049"
  Angle = 360
  Axis = (0,1,0)
  Base = (0,0,0)
  FaceMakerClass = Part::FaceMakerBullseye
  Placement = pos=(0,0,36.15) rot=(0,0,1;0rad)
  Solid = false
  Source = -> Face125
  Symmetric = false
FEATURE [Part::Feature] Face126
  shape: bbox 10 x 16.5 x 2e-07 mm, 1 faces, 0 solids (baked)
FEATURE [Part::Revolution] Revolve131  label="plugHousing058"
  Angle = 360
  Axis = (0,1,0)
  Base = (0,0,0)
  FaceMakerClass = Part::FaceMakerBullseye
  Placement = pos=(0,0,36.15) rot=(0,0,1;0rad)
  Solid = false
  Source = -> Face120
  Symmetric = false
FEATURE [Part::MultiFuse] Fusion099  label="plugHousing053"
  Placement = pos=(0,0,0) rot=(0,0,1;1.5708rad)
  Shapes = -> [Revolve127,Revolve131]
FEATURE [Part::MultiFuse] Fusion102  label="plugHousing056"
  Placement = pos=(0,19,0) rot=(0,0,1;3.14159rad)
  Shapes = -> [Fusion100,Fusion099]
FEATURE [Part::Revolution] Revolve132  label="plugHousing059"
  Angle = 360
  Axis = (0,1,0)
  Base = (0,0,0)
  FaceMakerClass = Part::FaceMakerBullseye
  Placement = pos=(0,0,36.15) rot=(0,0,1;0rad)
  Solid = false
  Source = -> Face126
  Symmetric = false
FEATURE [Part::Revolution] Revolve133  label="plugHousing060"
  Angle = 360
  Axis = (0,1,0)
  Base = (0,0,0)
  FaceMakerClass = Part::FaceMakerBullseye
  Placement = pos=(0,0,36.15) rot=(0,0,1;0rad)
  Solid = false
  Source = -> Face122
  Symmetric = false
FEATURE [Part::MultiFuse] Fusion097  label="plugHousing051"
  Placement = pos=(0,0,0) rot=(0,0,1;1.5708rad)
  Shapes = -> [Revolve133,Revolve132]
FEATURE [Part::Revolution] Revolve134  label="plugHousing061"
  Angle = 360
  Axis = (0,1,0)
  Base = (0,0,0)
  FaceMakerClass = Part::FaceMakerBullseye
  Placement = pos=(0,0,36.15) rot=(0,0,1;0rad)
  Solid = false
  Source = -> Face124
  Symmetric = false
FEATURE [Part::MultiFuse] Fusion101  label="plugHousing055"
  Placement = pos=(0,0,0) rot=(0,0,1;1.5708rad)
  Shapes = -> [Revolve129,Revolve134]
FEATURE [Part::MultiFuse] Fusion098  label="plugHousing052"
  Placement = pos=(0,19,0) rot=(0,0,1;3.14159rad)
  Shapes = -> [Fusion097,Fusion101]
FEATURE [Part::MultiFuse] Fusion103  label="plugHousing057"
  Placement = pos=(122.621,0,-0.15) rot=(0,0,1;0rad)
  Shapes = -> [Fusion102,Fusion098]
FEATURE [Part::Box] Box028  label="Cube015"
  AttacherType = Attacher::AttachEngine3D
  Height = 28
  Length = 3
  Placement = pos=(110.7,19,22) rot=(0,0,1;0rad)
  Width = 15.7
FEATURE [Part::Cylinder] Cylinder044
  Angle = 360
  AttacherType = Attacher::AttachEngine3D
  Height = 20
  Placement = pos=(0,0,36.15) rot=(0,0,1;0rad)
  Radius = 10.3
FEATURE [Part::Cylinder] Cylinder045
  Angle = 360
  AttacherType = Attacher::AttachEngine3D
  Height = 10
  Placement = pos=(0,0,36.15) rot=(0,0,1;0rad)
  Radius = 4
FEATURE [Part::MultiFuse] Fusion104  label="removeToCreteHoleForPlugHousing040"
  Placement = pos=(70,19,36) rot=(0,1,0;1.5708rad)
  Shapes = -> [Cylinder044,Cylinder045]
FEATURE [Part::Cut] Cut046  label="plugHousingTab003"
  Base = -> Box028
  Tool = -> Fusion104
FEATURE [Part::MultiFuse] Fusion105  label="plugHousing062"
  Shapes = -> [Fusion103,Cut046]
FEATURE [Part::Fillet] Fillet042
  Base = -> Fusion105
  Edges = 1 edges r=2: [Edge25]
FEATURE [Part::Fillet] Fillet043  label="plugHousing063"
  Base = -> Fillet042
  Edges = 1 edges r=2: [Edge8]
  Placement = pos=(7,0,0) rot=(0,0,1;0rad)
FEATURE [Part::Feature] Face127
  shape: bbox 10 x 16.5 x 2e-07 mm, 1 faces, 0 solids (baked)
FEATURE [Part::Feature] Face128
  shape: bbox 10 x 16.5 x 2e-07 mm, 1 faces, 0 solids (baked)
FEATURE [Part::Revolution] Revolve137  label="plugHousing070"
  Angle = 360
  Axis = (0,1,0)
  Base = (0,0,0)
  FaceMakerClass = Part::FaceMakerBullseye
  Placement = pos=(0,0,36.15) rot=(0,0,1;0rad)
  Solid = false
  Source = -> Face127
  Symmetric = false
FEATURE [Part::Revolution] Revolve140  label="plugHousing073"
  Angle = 360
  Axis = (0,1,0)
  Base = (0,0,0)
  FaceMakerClass = Part::FaceMakerBullseye
  Placement = pos=(0,0,36.15) rot=(0,0,1;0rad)
  Solid = false
  Source = -> Face128
  Symmetric = false
FEATURE [Part::Feature] Face129
  shape: bbox 10 x 16.5 x 2e-07 mm, 1 faces, 0 solids (baked)
FEATURE [Part::Revolution] Revolve138  label="plugHousing071"
  Angle = 360
  Axis = (0,1,0)
  Base = (0,0,0)
  FaceMakerClass = Part::FaceMakerBullseye
  Placement = pos=(0,0,36.15) rot=(0,0,1;0rad)
  Solid = false
  Source = -> Face129
  Symmetric = false
FEATURE [Part::Feature] Face130
  shape: bbox 10 x 16.5 x 2e-07 mm, 1 faces, 0 solids (baked)
FEATURE [Part::Revolution] Revolve139  label="plugHousing072"
  Angle = 360
  Axis = (0,1,0)
  Base = (0,0,0)
  FaceMakerClass = Part::FaceMakerBullseye
  Placement = pos=(0,0,36.15) rot=(0,0,1;0rad)
  Solid = false
  Source = -> Face130
  Symmetric = false
FEATURE [Part::Feature] Face131
  shape: bbox 10 x 16.5 x 2e-07 mm, 1 faces, 0 solids (baked)
FEATURE [Part::Revolution] Revolve135  label="plugHousing068"
  Angle = 360
  Axis = (0,1,0)
  Base = (0,0,0)
  FaceMakerClass = Part::FaceMakerBullseye
  Placement = pos=(0,0,36.15) rot=(0,0,1;0rad)
  Solid = false
  Source = -> Face131
  Symmetric = false
FEATURE [Part::MultiFuse] Fusion112  label="plugHousing078"
  Placement = pos=(0,0,0) rot=(0,0,1;1.5708rad)
  Shapes = -> [Revolve135,Revolve139]
FEATURE [Part::Feature] Face132
  shape: bbox 10 x 16.5 x 2e-07 mm, 1 faces, 0 solids (baked)
FEATURE [Part::Revolution] Revolve141  label="plugHousing074"
  Angle = 360
  Axis = (0,1,0)
  Base = (0,0,0)
  FaceMakerClass = Part::FaceMakerBullseye
  Placement = pos=(0,0,36.15) rot=(0,0,1;0rad)
  Solid = false
  Source = -> Face132
  Symmetric = false
FEATURE [Part::MultiFuse] Fusion110  label="plugHousing076"
  Placement = pos=(0,0,0) rot=(0,0,1;1.5708rad)
  Shapes = -> [Revolve141,Revolve140]
FEATURE [Part::Feature] Face133
  shape: bbox 10 x 16.5 x 2e-07 mm, 1 faces, 0 solids (baked)
FEATURE [Part::Revolution] Revolve136  label="plugHousing069"
  Angle = 360
  Axis = (0,1,0)
  Base = (0,0,0)
  FaceMakerClass = Part::FaceMakerBullseye
  Placement = pos=(0,0,36.15) rot=(0,0,1;0rad)
  Solid = false
  Source = -> Face133
  Symmetric = false
FEATURE [Part::MultiFuse] Fusion106  label="plugHousing064"
  Placement = pos=(0,0,0) rot=(0,0,1;1.5708rad)
  Shapes = -> [Revolve138,Revolve136]
FEATURE [Part::MultiFuse] Fusion108  label="plugHousing066"
  Placement = pos=(0,19,0) rot=(0,0,1;3.14159rad)
  Shapes = -> [Fusion106,Fusion112]
FEATURE [Part::Feature] Face134
  shape: bbox 10 x 16.5 x 2e-07 mm, 1 faces, 0 solids (baked)
FEATURE [Part::Revolution] Revolve142  label="plugHousing075"
  Angle = 360
  Axis = (0,1,0)
  Base = (0,0,0)
  FaceMakerClass = Part::FaceMakerBullseye
  Placement = pos=(0,0,36.15) rot=(0,0,1;0rad)
  Solid = false
  Source = -> Face134
  Symmetric = false
FEATURE [Part::MultiFuse] Fusion107  label="plugHousing065"
  Placement = pos=(0,0,0) rot=(0,0,1;1.5708rad)
  Shapes = -> [Revolve137,Revolve142]
FEATURE [Part::MultiFuse] Fusion111  label="plugHousing077"
  Placement = pos=(0,19,0) rot=(0,0,1;3.14159rad)
  Shapes = -> [Fusion110,Fusion107]
FEATURE [Part::MultiFuse] Fusion109  label="plugHousing067"
  Placement = pos=(131.236,0,-0.15) rot=(0,0,1;0rad)
  Shapes = -> [Fusion108,Fusion111]
FEATURE [Part::MultiFuse] Fusion113  label="plugHousing079"
  Shapes = -> [Fillet043,Fusion109]
FEATURE [Part::Feature] Face135
  shape: bbox 3.5 x 17.8 x 2e-07 mm, 1 faces, 0 solids (baked)
FEATURE [Part::Revolution] Revolve143  label="removeToCreateScrewAndThreadedInsertHole049"
  Angle = 360
  Axis = (0,1,0)
  Base = (0,0,0)
  FaceMakerClass = Part::FaceMakerBullseye
  Placement = pos=(12.5,0,10) rot=(0,0,1;0rad)
  Solid = false
  Source = -> Face135
  Symmetric = false
FEATURE [Part::Feature] Face136
  shape: bbox 3.5 x 17.8 x 2e-07 mm, 1 faces, 0 solids (baked)
FEATURE [Part::Revolution] Revolve144  label="removeToCreateScrewAndThreadedInsertHole050"
  Angle = 360
  Axis = (0,1,0)
  Base = (0,0,0)
  FaceMakerClass = Part::FaceMakerBullseye
  Placement = pos=(12.5,0,62) rot=(0,0,1;0rad)
  Solid = false
  Source = -> Face136
  Symmetric = false
FEATURE [Part::Feature] Face137
  shape: bbox 3.5 x 17.8 x 2e-07 mm, 1 faces, 0 solids (baked)
FEATURE [Part::Revolution] Revolve145  label="removeToCreateScrewAndThreadedInsertHole051"
  Angle = 360
  Axis = (0,1,0)
  Base = (0,0,0)
  FaceMakerClass = Part::FaceMakerBullseye
  Placement = pos=(89.5,0,68.5) rot=(0,0,1;0rad)
  Solid = false
  Source = -> Face137
  Symmetric = false
FEATURE [Part::Feature] Face138
  shape: bbox 3.5 x 17.8 x 2e-07 mm, 1 faces, 0 solids (baked)
FEATURE [Part::Revolution] Revolve146  label="removeToCreateScrewAndThreadedInsertHole052"
  Angle = 360
  Axis = (0,1,0)
  Base = (0,0,0)
  FaceMakerClass = Part::FaceMakerBullseye
  Placement = pos=(89.5,0,3.5) rot=(0,0,1;0rad)
  Solid = false
  Source = -> Face138
  Symmetric = false
FEATURE [Part::Feature] Face139
  shape: bbox 3.5 x 17.8 x 2e-07 mm, 1 faces, 0 solids (baked)
FEATURE [Part::Revolution] Revolve147  label="removeToCreateScrewAndThreadedInsertHole053"
  Angle = 360
  Axis = (0,1,0)
  Base = (0,0,0)
  FaceMakerClass = Part::FaceMakerBullseye
  Placement = pos=(109.5,4.7,3.5) rot=(0,0,1;0rad)
  Solid = false
  Source = -> Face139
  Symmetric = false
FEATURE [Part::Feature] Face140
  shape: bbox 3.5 x 17.8 x 2e-07 mm, 1 faces, 0 solids (baked)
FEATURE [Part::Revolution] Revolve148  label="removeToCreateScrewAndThreadedInsertHole054"
  Angle = 360
  Axis = (0,1,0)
  Base = (0,0,0)
  FaceMakerClass = Part::FaceMakerBullseye
  Placement = pos=(109.5,4.7,68.5) rot=(0,0,1;0rad)
  Solid = false
  Source = -> Face140
  Symmetric = false
FEATURE [Part::MultiFuse] Fusion114  label="removeToCreateScrewAndThreadedInsertHole055"
  Shapes = -> [Revolve148,Revolve147,Revolve146,Revolve145,Revolve144,Revolve143]
FEATURE [Part::Cut] Cut047  label="casePillars004"
  Base = -> Cut037
  Tool = -> Fusion114
FEATURE [Part::Feature] Face141
  shape: bbox 3.5 x 17.8 x 2e-07 mm, 1 faces, 0 solids (baked)
FEATURE [Part::Feature] Face142
  shape: bbox 3.5 x 17.8 x 2e-07 mm, 1 faces, 0 solids (baked)
FEATURE [Part::Feature] Face143
  shape: bbox 3.5 x 17.8 x 2e-07 mm, 1 faces, 0 solids (baked)
FEATURE [Part::Revolution] Revolve149  label="removeToCreateScrewAndThreadedInsertHole057"
  Angle = 360
  Axis = (0,1,0)
  Base = (0,0,0)
  FaceMakerClass = Part::FaceMakerBullseye
  Placement = pos=(12.5,0,10) rot=(0,0,1;0rad)
  Solid = false
  Source = -> Face141
  Symmetric = false
FEATURE [Part::Feature] Face144
  shape: bbox 3.5 x 17.8 x 2e-07 mm, 1 faces, 0 solids (baked)
FEATURE [Part::Feature] Face145
  shape: bbox 3.5 x 17.8 x 2e-07 mm, 1 faces, 0 solids (baked)
FEATURE [Part::Feature] Face146
  shape: bbox 3.5 x 17.8 x 2e-07 mm, 1 faces, 0 solids (baked)
FEATURE [Part::Revolution] Revolve150  label="removeToCreateScrewAndThreadedInsertHole058"
  Angle = 360
  Axis = (0,1,0)
  Base = (0,0,0)
  FaceMakerClass = Part::FaceMakerBullseye
  Placement = pos=(12.5,0,62) rot=(0,0,1;0rad)
  Solid = false
  Source = -> Face146
  Symmetric = false
FEATURE [Part::Revolution] Revolve151  label="removeToCreateScrewAndThreadedInsertHole059"
  Angle = 360
  Axis = (0,1,0)
  Base = (0,0,0)
  FaceMakerClass = Part::FaceMakerBullseye
  Placement = pos=(89.5,0,68.5) rot=(0,0,1;0rad)
  Solid = false
  Source = -> Face143
  Symmetric = false
FEATURE [Part::Revolution] Revolve152  label="removeToCreateScrewAndThreadedInsertHole060"
  Angle = 360
  Axis = (0,1,0)
  Base = (0,0,0)
  FaceMakerClass = Part::FaceMakerBullseye
  Placement = pos=(89.5,0,3.5) rot=(0,0,1;0rad)
  Solid = false
  Source = -> Face142
  Symmetric = false
FEATURE [Part::Revolution] Revolve153  label="removeToCreateScrewAndThreadedInsertHole061"
  Angle = 360
  Axis = (0,1,0)
  Base = (0,0,0)
  FaceMakerClass = Part::FaceMakerBullseye
  Placement = pos=(109.5,4.7,3.5) rot=(0,0,1;0rad)
  Solid = false
  Source = -> Face145
  Symmetric = false
FEATURE [Part::Revolution] Revolve154  label="removeToCreateScrewAndThreadedInsertHole062"
  Angle = 360
  Axis = (0,1,0)
  Base = (0,0,0)
  FaceMakerClass = Part::FaceMakerBullseye
  Placement = pos=(109.5,4.7,68.5) rot=(0,0,1;0rad)
  Solid = false
  Source = -> Face144
  Symmetric = false
FEATURE [Part::MultiFuse] Fusion115  label="removeToCreateScrewAndThreadedInsertHole056"
  Shapes = -> [Revolve154,Revolve153,Revolve152,Revolve151,Revolve150,Revolve149]
FEATURE [Part::Feature] Face147
  shape: bbox 9.8 x 26.5 x 2e-07 mm, 1 faces, 0 solids (baked)
FEATURE [Part::Revolution] Revolve155
  Angle = 360
  Axis = (0,1,0)
  Base = (0,0,0)
  FaceMakerClass = Part::FaceMakerBullseye
  Placement = pos=(0,0,0) rot=(0,0,1;1.5708rad)
  Solid = false
  Source = -> Face147
  Symmetric = false
FEATURE [Part::Feature] Face148
  shape: bbox 9.8 x 26.5 x 2e-07 mm, 1 faces, 0 solids (baked)
FEATURE [Part::Revolution] Revolve156
  Angle = 360
  Axis = (0,1,0)
  Base = (0,0,0)
  FaceMakerClass = Part::FaceMakerBullseye
  Placement = pos=(0,0,0) rot=(0,0,1;1.5708rad)
  Solid = false
  Source = -> Face148
  Symmetric = false
FEATURE [Part::MultiFuse] Fusion116
  Placement = pos=(-18,19,36) rot=(0,0,1;0rad)
  Shapes = -> [Revolve156,Revolve155]
FEATURE [Part::Box] Box029  label="Cube016"
  AttacherType = Attacher::AttachEngine3D
  Height = 28
  Length = 3
  Placement = pos=(110.7,19,22) rot=(0,0,1;0rad)
  Width = 15.7
FEATURE [Part::Cylinder] Cylinder046
  Angle = 360
  AttacherType = Attacher::AttachEngine3D
  Height = 10
  Placement = pos=(0,0,36.15) rot=(0,0,1;0rad)
  Radius = 4
FEATURE [Part::Cylinder] Cylinder047
  Angle = 360
  AttacherType = Attacher::AttachEngine3D
  Height = 20
  Placement = pos=(0,0,36.15) rot=(0,0,1;0rad)
  Radius = 10.3
FEATURE [Part::MultiFuse] Fusion117  label="removeToCreteHoleForPlugHousing041"
  Placement = pos=(70,19,36) rot=(0,1,0;1.5708rad)
  Shapes = -> [Cylinder047,Cylinder046]
FEATURE [Part::Cut] Cut049  label="plugHousingTab004"
  Base = -> Box029
  Placement = pos=(-107.4,-14,0) rot=(0,0,1;0rad)
  Tool = -> Fusion117
FEATURE [Part::Box] Box030  label="Cube017"
  AttacherType = Attacher::AttachEngine3D
  Height = 28
  Length = 3
  Placement = pos=(110.7,19,22) rot=(0,0,1;0rad)
  Width = 15.7
FEATURE [Part::Cylinder] Cylinder048
  Angle = 360
  AttacherType = Attacher::AttachEngine3D
  Height = 10
  Placement = pos=(0,0,36.15) rot=(0,0,1;0rad)
  Radius = 4
FEATURE [Part::Cylinder] Cylinder049
  Angle = 360
  AttacherType = Attacher::AttachEngine3D
  Height = 20
  Placement = pos=(0,0,36.15) rot=(0,0,1;0rad)
  Radius = 10.3
FEATURE [Part::MultiFuse] Fusion118  label="removeToCreteHoleForPlugHousing042"
  Placement = pos=(70,19,36) rot=(0,1,0;1.5708rad)
  Shapes = -> [Cylinder049,Cylinder048]
FEATURE [Part::Cut] Cut050  label="plugHousingTab005"
  Base = -> Box030
  Placement = pos=(-107.4,-14,0) rot=(0,0,1;0rad)
  Tool = -> Fusion118
FEATURE [Part::MultiFuse] Fusion119
  Placement = pos=(9.6,23,0) rot=(0,0,1;3.14159rad)
  Shapes = -> [Cut049,Cut050]
FEATURE [Part::Box] Box031  label="Cube018"
  AttacherType = Attacher::AttachEngine3D
  Height = 10
  Length = 3
  Placement = pos=(3.3,4,12) rot=(0,0,1;0rad)
  Width = 10
FEATURE [Part::Fillet] Fillet044
  Base = -> Box031
  Edges = 1 edges r=2: [Edge11]
FEATURE [Part::Box] Box032  label="Cube019"
  AttacherType = Attacher::AttachEngine3D
  Height = 10
  Length = 3
  Placement = pos=(3.3,4,50) rot=(0,0,1;0rad)
  Width = 10
FEATURE [Part::Fillet] Fillet045
  Base = -> Box032
  Edges = 1 edges r=2: [Edge12]
FEATURE [Part::Box] Box033  label="Cube020"
  AttacherType = Attacher::AttachEngine3D
  Height = 28
  Length = 4
  Placement = pos=(5,0,22) rot=(0,0,1;0rad)
  Width = 10
FEATURE [Part::Fillet] Fillet046
  Base = -> Box033
  Edges = 1 edges r=1: [Edge7]
FEATURE [Part::Fillet] Fillet047
  Base = -> Fillet046
  Edges = 1 edges r=2: [Edge5]
FEATURE [Part::Fillet] Fillet048
  Base = -> Fillet047
  Edges = 1 edges r=2: [Edge2]
FEATURE [Part::Cylinder] Cylinder050
  Angle = 360
  AttacherType = Attacher::AttachEngine3D
  Height = 20
  Placement = pos=(0,0,36.15) rot=(0,0,1;0rad)
  Radius = 8.2
FEATURE [Part::Cylinder] Cylinder051
  Angle = 360
  AttacherType = Attacher::AttachEngine3D
  Height = 10
  Placement = pos=(0,0,36.15) rot=(0,0,1;0rad)
  Radius = 4
FEATURE [Part::MultiFuse] Fusion120  label="removeToCreteHoleForPlugHousing043"
  Placement = pos=(-42,19,36) rot=(0,1,0;1.5708rad)
  Shapes = -> [Cylinder050,Cylinder051]
FEATURE [Sketcher::SketchObject] Sketch067  label="topSketch018"
  FullyConstrained = true
  sketch-geometry (4):
    g0: LineSegment StartX=16.8446 StartY=31.512 StartZ=0 EndX=16.3251 EndY=34.4666 EndZ=0
    g1: ArcOfCircle CenterX=19 CenterY=19.2524 CenterZ=0 NormalX=0 NormalY=0 NormalZ=1 AngleXU=0 Radius=15.4476 StartAngle=1.74483 EndAngle=2.72717
    g2: ArcOfCircle CenterX=19 CenterY=19.2524 CenterZ=0 NormalX=0 NormalY=0 NormalZ=1 AngleXU=0 Radius=12.4476 StartAngle=1.74483 EndAngle=2.73189
    g3: LineSegment StartX=4.86004 StartY=25.4725 StartZ=0 EndX=7.58253 EndY=24.2107 EndZ=0
  constraints (7):
    c: Block(g0)
    c: Coincident(g1,g0)
    c: Coincident(g2,g0)
    c: Coincident(g3,g1)
    c: Coincident(g3,g2)
    c: Block(g1)
    c: Block(g2)
FEATURE [Part::Extrusion] Extrude058
  Base = -> Sketch067
  Dir = (0,0,1)
  DirMode = 2
  FaceMakerClass = Part::FaceMakerBullseye
  LengthFwd = 10
  LengthRev = 0
  Placement = pos=(0,0,31) rot=(0,0,1;0rad)
  Solid = true
  Symmetric = false
FEATURE [Part::Cut] Cut051
  Base = -> Extrude058
  Tool = -> Fusion120
FEATURE [Part::Fillet] Fillet049
  Base = -> Cut051
  Edges = 1 edges r=2: [Edge1]
FEATURE [Part::Fillet] Fillet050
  Base = -> Fillet049
  Edges = 1 edges r=2.5: [Edge1]
FEATURE [Part::Fillet] Fillet051
  Base = -> Fillet050
  Edges = 1 edges r=2.5: [Edge2]
FEATURE [Part::MultiFuse] Fusion121  label="wireHolder003"
  Shapes = -> [Fusion116,Fillet051]
FEATURE [Part::MultiFuse] Fusion122
  Shapes = -> [Fillet045,Fusion121]
FEATURE [Part::MultiFuse] Fusion123  label="wireHolder004"
  Shapes = -> [Fusion122,Fillet048]
FEATURE [Part::MultiFuse] Fusion124  label="wireHolder005"
  Shapes = -> [Fillet044,Fusion119,Fusion123]
FEATURE [Sketcher::SketchObject] Sketch068  label="topSketch019"
  FullyConstrained = true
  sketch-geometry (6):
    g0: LineSegment StartX=19 StartY=38 StartZ=0 EndX=117 EndY=38 EndZ=0
    g1: ArcOfCircle CenterX=19 CenterY=19 CenterZ=0 NormalX=0 NormalY=0 NormalZ=1 AngleXU=0 Radius=19 StartAngle=1.5708 EndAngle=3.14159
    g2: LineSegment StartX=117 StartY=38 StartZ=0 EndX=117 EndY=19 EndZ=0
    g3: LineSegment StartX=98 StartY=1.0161e-12 StartZ=0 EndX=5.22862e-06 EndY=1.0161e-12 EndZ=0
    g4: LineSegment StartX=5.22862e-06 StartY=19 StartZ=0 EndX=5.22862e-06 EndY=1.0161e-12 EndZ=0
    g5: ArcOfCircle CenterX=98 CenterY=19 CenterZ=0 NormalX=0 NormalY=0 NormalZ=1 AngleXU=0 Radius=19 StartAngle=4.71239 EndAngle=6.28319
  constraints (16):
    c: Horizontal(g0)
    c: Distance(g0) = 98
    c: Coincident(g1,g0)
    c: Block(g1)
    c: Coincident(g2,g0)
    c: Vertical(g2)
    c: Distance(g2) = 19
    c: Horizontal(g3)
    c: Coincident(g4,g1)
    c: Vertical(g4)
    c: Coincident(g3,g4)
    c: Block(g3)
    c: Coincident(g5,g2)
    c: Coincident(g5,g3)
    c: Block(g0)
    c: Block(g5)
FEATURE [Part::Extrusion] Extrude059  label="sideA002"
  Base = -> Sketch068
  Dir = (0,0,1)
  DirMode = 2
  FaceMakerClass = Part::FaceMakerBullseye
  LengthFwd = 3
  LengthRev = 0
  Placement = pos=(0,0,-2.7) rot=(0,0,1;0rad)
  Solid = true
  Symmetric = false
FEATURE [Sketcher::SketchObject] Sketch069  label="topSketch020"
  FullyConstrained = true
  sketch-geometry (6):
    g0: LineSegment StartX=19 StartY=38 StartZ=0 EndX=117 EndY=38 EndZ=0
    g1: ArcOfCircle CenterX=19 CenterY=19 CenterZ=0 NormalX=0 NormalY=0 NormalZ=1 AngleXU=0 Radius=19 StartAngle=1.5708 EndAngle=3.14159
    g2: LineSegment StartX=117 StartY=38 StartZ=0 EndX=117 EndY=19 EndZ=0
    g3: LineSegment StartX=98 StartY=1.0161e-12 StartZ=0 EndX=5.22862e-06 EndY=1.0161e-12 EndZ=0
    g4: LineSegment StartX=5.22862e-06 StartY=19 StartZ=0 EndX=5.22862e-06 EndY=1.0161e-12 EndZ=0
    g5: ArcOfCircle CenterX=98 CenterY=19 CenterZ=0 NormalX=0 NormalY=0 NormalZ=1 AngleXU=0 Radius=19 StartAngle=4.71239 EndAngle=6.28319
  constraints (16):
    c: Horizontal(g0)
    c: Distance(g0) = 98
    c: Coincident(g1,g0)
    c: Block(g1)
    c: Coincident(g2,g0)
    c: Vertical(g2)
    c: Distance(g2) = 19
    c: Horizontal(g3)
    c: Coincident(g4,g1)
    c: Vertical(g4)
    c: Coincident(g3,g4)
    c: Block(g3)
    c: Coincident(g5,g2)
    c: Coincident(g5,g3)
    c: Block(g0)
    c: Block(g5)
FEATURE [Part::Extrusion] Extrude060  label="sideB002"
  Base = -> Sketch069
  Dir = (0,0,1)
  DirMode = 2
  FaceMakerClass = Part::FaceMakerBullseye
  LengthFwd = 3
  LengthRev = 0
  Placement = pos=(0,0,71.7) rot=(0,0,1;0rad)
  Solid = true
  Symmetric = false
FEATURE [Part::MultiFuse] Fusion127  label="removeFromBottom001"
  Placement = pos=(2,0,0) rot=(0,0,1;0rad)
  Shapes = -> [Extrude059,Extrude060]
FEATURE [Part::Cylinder] Cylinder052
  Angle = 360
  AttacherType = Attacher::AttachEngine3D
  Height = 20
  Placement = pos=(0,0,36.15) rot=(0,0,1;0rad)
  Radius = 14
FEATURE [Part::Cylinder] Cylinder053
  Angle = 360
  AttacherType = Attacher::AttachEngine3D
  Height = 10
  Placement = pos=(0,0,36.15) rot=(0,0,1;0rad)
  Radius = 4
FEATURE [Part::MultiFuse] Fusion128  label="removeToCreteHoleForPlugHousing044"
  Placement = pos=(70,19,36) rot=(0,1,0;1.5708rad)
  Shapes = -> [Cylinder052,Cylinder053]
FEATURE [Part::Cut] Cut052  label="bottom011"
  Base = -> Extrude043
  Tool = -> Fusion128
FEATURE [Part::Cut] Cut054  label="bottom012"
  Base = -> Cut052
  Tool = -> Fusion115
FEATURE [Sketcher::SketchObject] Sketch070
  FullyConstrained = true
  Placement = pos=(117,19,0) rot=(0.57735,0.57735,0.57735;2.0944rad)
  sketch-geometry (48):
    g0: LineSegment StartX=-49.19 StartY=69.25 StartZ=0 EndX=-49.19 EndY=66.25 EndZ=0
    g1: LineSegment StartX=-49.19 StartY=63.5 StartZ=0 EndX=-49.19 EndY=60.5 EndZ=0
    g2: LineSegment StartX=-49.19 StartY=57.75 StartZ=0 EndX=-49.19 EndY=54.75 EndZ=0
    g3: LineSegment StartX=-49.19 StartY=52 StartZ=0 EndX=-49.19 EndY=49 EndZ=0
    g4: LineSegment StartX=-49.19 StartY=46.25 StartZ=0 EndX=-49.19 EndY=43.25 EndZ=0
    g5: LineSegment StartX=-49.19 StartY=40.5 StartZ=0 EndX=-49.19 EndY=37.5 EndZ=0
    g6: LineSegment StartX=-49.19 StartY=34.5 StartZ=0 EndX=-49.19 EndY=31.5 EndZ=0
    g7: LineSegment StartX=-49.19 StartY=28.75 StartZ=0 EndX=-49.19 EndY=25.75 EndZ=0
    g8: LineSegment StartX=-49.19 StartY=23 StartZ=0 EndX=-49.19 EndY=20 EndZ=0
    g9: LineSegment StartX=-49.19 StartY=17.25 StartZ=0 EndX=-49.19 EndY=14.25 EndZ=0
    g10: LineSegment StartX=-49.19 StartY=11.5 StartZ=0 EndX=-49.19 EndY=8.5 EndZ=0
    g11: LineSegment StartX=-49.19 StartY=5.75 StartZ=0 EndX=-49.19 EndY=2.75 EndZ=0
    g12: ArcOfCircle CenterX=-1.5 CenterY=67.75 CenterZ=0 NormalX=0 NormalY=0 NormalZ=1 AngleXU=0 Radius=1.5 StartAngle=4.71239 EndAngle=7.85398
    g13: ArcOfCircle CenterX=-1.5 CenterY=62 CenterZ=0 NormalX=0 NormalY=0 NormalZ=1 AngleXU=0 Radius=1.5 StartAngle=4.71239 EndAngle=7.85398
    g14: ArcOfCircle CenterX=-1.5 CenterY=56.25 CenterZ=0 NormalX=0 NormalY=0 NormalZ=1 AngleXU=0 Radius=1.5 StartAngle=4.71239 EndAngle=7.85398
    g15: ArcOfCircle CenterX=-11.49 CenterY=50.5 CenterZ=0 NormalX=0 NormalY=0 NormalZ=1 AngleXU=0 Radius=1.5 StartAngle=4.71239 EndAngle=7.85398
    g16: ArcOfCircle CenterX=-16.28 CenterY=44.75 CenterZ=0 NormalX=0 NormalY=0 NormalZ=1 AngleXU=0 Radius=1.5 StartAngle=4.71239 EndAngle=7.85398
    g17: ArcOfCircle CenterX=-18.2337 CenterY=39 CenterZ=0 NormalX=0 NormalY=0 NormalZ=1 AngleXU=0 Radius=1.5 StartAngle=4.71485 EndAngle=7.85398
    g18: ArcOfCircle CenterX=-16.2837 CenterY=27.25 CenterZ=0 NormalX=0 NormalY=0 NormalZ=1 AngleXU=0 Radius=1.5 StartAngle=4.71485 EndAngle=7.85398
    g19: ArcOfCircle CenterX=-18.2337 CenterY=33 CenterZ=0 NormalX=0 NormalY=0 NormalZ=1 AngleXU=0 Radius=1.5 StartAngle=4.71485 EndAngle=7.85398
    g20: ArcOfCircle CenterX=-11.49 CenterY=21.5 CenterZ=0 NormalX=0 NormalY=0 NormalZ=1 AngleXU=0 Radius=1.5 StartAngle=4.71239 EndAngle=7.85398
    g21: ArcOfCircle CenterX=-1.5 CenterY=4.25 CenterZ=0 NormalX=0 NormalY=0 NormalZ=1 AngleXU=0 Radius=1.5 StartAngle=4.71239 EndAngle=7.85398
    g22: ArcOfCircle CenterX=-1.5 CenterY=10 CenterZ=0 NormalX=0 NormalY=0 NormalZ=1 AngleXU=0 Radius=1.5 StartAngle=4.71239 EndAngle=7.85398
    g23: ArcOfCircle CenterX=-1.5 CenterY=15.75 CenterZ=0 NormalX=0 NormalY=0 NormalZ=1 AngleXU=0 Radius=1.5 StartAngle=4.71239 EndAngle=7.85398
    g24: LineSegment StartX=-49.19 StartY=69.25 StartZ=0 EndX=-1.5 EndY=69.25 EndZ=0
    g25: LineSegment StartX=-49.19 StartY=66.25 StartZ=0 EndX=-1.5 EndY=66.25 EndZ=0
    g26: LineSegment StartX=-49.19 StartY=63.5 StartZ=0 EndX=-1.5 EndY=63.5 EndZ=0
    g27: LineSegment StartX=-49.19 StartY=60.5 StartZ=0 EndX=-1.5 EndY=60.5 EndZ=0
    g28: LineSegment StartX=-49.19 StartY=57.75 StartZ=0 EndX=-1.5 EndY=57.75 EndZ=0
    g29: LineSegment StartX=-49.19 StartY=54.75 StartZ=0 EndX=-1.5 EndY=54.75 EndZ=0
    g30: LineSegment StartX=-49.19 StartY=52 StartZ=0 EndX=-11.49 EndY=52 EndZ=0
    g31: LineSegment StartX=-49.19 StartY=49 StartZ=0 EndX=-11.49 EndY=49 EndZ=0
    g32: LineSegment StartX=-49.19 StartY=46.25 StartZ=0 EndX=-16.28 EndY=46.25 EndZ=0
    g33: LineSegment StartX=-49.19 StartY=43.25 StartZ=0 EndX=-16.28 EndY=43.25 EndZ=0
    g34: LineSegment StartX=-49.19 StartY=40.5 StartZ=0 EndX=-18.2337 EndY=40.5 EndZ=0
    g35: LineSegment StartX=-49.19 StartY=37.5 StartZ=0 EndX=-18.23 EndY=37.5 EndZ=0
    g36: LineSegment StartX=-49.19 StartY=34.5 StartZ=0 EndX=-18.2337 EndY=34.5 EndZ=0
    g37: LineSegment StartX=-49.19 StartY=31.5 StartZ=0 EndX=-18.23 EndY=31.5 EndZ=0
    g38: LineSegment StartX=-49.19 StartY=28.75 StartZ=0 EndX=-16.2837 EndY=28.75 EndZ=0
    g39: LineSegment StartX=-49.19 StartY=25.75 StartZ=0 EndX=-16.28 EndY=25.75 EndZ=0
    g40: LineSegment StartX=-49.19 StartY=23 StartZ=0 EndX=-11.49 EndY=23 EndZ=0
    g41: LineSegment StartX=-49.19 StartY=20 StartZ=0 EndX=-11.49 EndY=20 EndZ=0
    g42: LineSegment StartX=-49.19 StartY=17.25 StartZ=0 EndX=-1.5 EndY=17.25 EndZ=0
    g43: LineSegment StartX=-49.19 StartY=14.25 StartZ=0 EndX=-1.5 EndY=14.25 EndZ=0
    g44: LineSegment StartX=-49.19 StartY=11.5 StartZ=0 EndX=-1.5 EndY=11.5 EndZ=0
    g45: LineSegment StartX=-49.19 StartY=8.5 StartZ=0 EndX=-1.5 EndY=8.5 EndZ=0
    g46: LineSegment StartX=-49.19 StartY=5.75 StartZ=0 EndX=-1.5 EndY=5.75 EndZ=0
    g47: LineSegment StartX=-49.19 StartY=2.75 StartZ=0 EndX=-1.5 EndY=2.75 EndZ=0
  constraints (120):
    c: Vertical(g0)
    c: Distance(g0) = 3
    c: Block(g0)
    c: Vertical(g1)
    c: Distance(g1) = 3
    c: Vertical(g2)
    c: Equal(g0,g2) = 3
    c: Block(g2)
    c: Vertical(g3)
    c: Equal(g1,g3) = 3
    c: Vertical(g4)
    c: Equal(g0,g4) = 3
    c: Block(g4)
    c: Vertical(g5)
    c: Equal(g1,g5) = 3
    c: Vertical(g6)
    c: Equal(g0,g6) = 3
    c: Block(g6)
    c: Vertical(g7)
    c: Equal(g1,g7) = 3
    c: Vertical(g8)
    c: Equal(g0,g8) = 3
    c: Block(g8)
    c: Vertical(g9)
    c: Equal(g1,g9) = 3
    c: Vertical(g10)
    c: Equal(g0,g10) = 3
    c: Block(g10)
    c: Vertical(g11)
    c: Equal(g1,g11) = 3
    c: Block(g12)
    c: Block(g13)
    c: Block(g14)
    c: Block(g15)
    c: Block(g16)
    c: Block(g17)
    c: Block(g18)
    c: Block(g19)
    c: Block(g20)
    c: Block(g21)
    c: Block(g22)
    c: Block(g23)
    c: Block(g11)
    c: Block(g9)
    c: Block(g7)
    c: Block(g5)
    c: Block(g3)
    c: Block(g1)
    c: Coincident(g24,g0)
    c: Coincident(g24,g12)
    c: Horizontal(g24)
    c: Coincident(g25,g0)
    c: Coincident(g25,g12)
    c: Horizontal(g25)
    c: Coincident(g26,g1)
    c: Coincident(g26,g13)
    c: Horizontal(g26)
    c: Coincident(g27,g1)
    c: Coincident(g27,g13)
    c: Horizontal(g27)
    c: Coincident(g28,g2)
    c: Coincident(g28,g14)
    c: Horizontal(g28)
    c: Coincident(g29,g2)
    c: Coincident(g29,g14)
    c: Horizontal(g29)
    c: Coincident(g30,g3)
    c: Coincident(g30,g15)
    c: Horizontal(g30)
    c: Coincident(g31,g3)
    c: Coincident(g31,g15)
    c: Horizontal(g31)
    c: Coincident(g32,g4)
    c: Coincident(g32,g16)
    c: Horizontal(g32)
    c: Coincident(g33,g4)
    c: Coincident(g33,g16)
    c: Horizontal(g33)
    c: Coincident(g34,g5)
    c: Coincident(g34,g17)
    c: Horizontal(g34)
    c: Coincident(g35,g5)
    c: Coincident(g35,g17)
    c: Horizontal(g35)
    c: Coincident(g36,g6)
    c: Coincident(g36,g19)
    c: Horizontal(g36)
    c: Coincident(g37,g6)
    c: Coincident(g37,g19)
    c: Horizontal(g37)
    c: Coincident(g38,g7)
    c: Coincident(g38,g18)
    c: Horizontal(g38)
    c: Coincident(g39,g7)
    c: Coincident(g39,g18)
    c: Horizontal(g39)
    c: Coincident(g40,g8)
    c: Coincident(g40,g20)
    c: Horizontal(g40)
    c: Coincident(g41,g8)
    c: Coincident(g41,g20)
    c: Horizontal(g41)
    c: Coincident(g42,g9)
    c: Coincident(g42,g23)
    c: Horizontal(g42)
    c: Coincident(g43,g9)
    c: Coincident(g43,g23)
    c: Horizontal(g43)
    c: Coincident(g44,g10)
    c: Coincident(g44,g22)
    c: Horizontal(g44)
    c: Coincident(g45,g10)
    c: Coincident(g45,g22)
    c: Horizontal(g45)
    c: Coincident(g46,g11)
    c: Coincident(g46,g21)
    c: Horizontal(g46)
    c: Coincident(g47,g11)
    c: Coincident(g47,g21)
    c: Horizontal(g47)
FEATURE [Part::Extrusion] Extrude061
  Base = -> Sketch070
  Dir = (1,0,0)
  DirMode = 2
  FaceMakerClass = Part::FaceMakerBullseye
  LengthFwd = 23
  LengthRev = 0
  Placement = pos=(-19,0,0) rot=(0,0,1;0rad)
  Solid = true
  Symmetric = false
FEATURE [Part::Fillet] Fillet052  label="removeToCreateVentalationHoles002"
  Base = -> Extrude061
  Edges = <same value as first occurrence — deduplicated (x6 in doc)>
  Placement = pos=(7,0.02,0) rot=(0,0,1;0rad)
FEATURE [Part::MultiFuse] Fusion130  label="bottom013"
  Shapes = -> [Cut054,Cut034]
FEATURE [Part::Cut] Cut055
  Base = -> Fusion130
  Tool = -> Fillet052
FEATURE [Part::Cylinder] Cylinder054
  Angle = 360
  AttacherType = Attacher::AttachEngine3D
  Height = 20
  Placement = pos=(0,0,36.15) rot=(0,0,1;0rad)
  Radius = 4
FEATURE [Sketcher::SketchObject] Sketch071  label="bottomSketch002"
  FullyConstrained = true
  sketch-geometry (32):
    g0: LineSegment StartX=3.3 StartY=-6.03275e-07 StartZ=0 EndX=98 EndY=-6.03275e-07 EndZ=0
    g1: ArcOfCircle CenterX=98 CenterY=19 CenterZ=0 NormalX=0 NormalY=0 NormalZ=1 AngleXU=0 Radius=19 StartAngle=4.71239 EndAngle=5.71103
    g2: LineSegment StartX=6.3 StartY=8 StartZ=0 EndX=3.3 EndY=8 EndZ=0
    g3: LineSegment StartX=3.3 StartY=8 StartZ=0 EndX=3.3 EndY=-6.03275e-07 EndZ=0
    g4: ArcOfCircle CenterX=8.3 CenterY=5 CenterZ=0 NormalX=0 NormalY=0 NormalZ=1 AngleXU=0 Radius=2 StartAngle=3.14159 EndAngle=4.71239
    g5: LineSegment StartX=6.3 StartY=8 StartZ=0 EndX=6.3 EndY=5 EndZ=0
    g6: ArcOfCircle CenterX=98 CenterY=19 CenterZ=0 NormalX=0 NormalY=0 NormalZ=1 AngleXU=0 Radius=12.7 StartAngle=4.71239 EndAngle=6.28319
    g7: LineSegment StartX=94.7 StartY=3 StartZ=0 EndX=8.3 EndY=3 EndZ=0
    g8-g12: Circle x5 (B-spline internal-alignment scaffolding for g13; pole/knot coordinates omitted)
    g13: BSplineCurve PolesCount=5 KnotsCount=3 Degree=3 IsPeriodic=0
    g14: GeomPoint X=98 Y=6.3 Z=0
    g15: GeomPoint X=96.3938 Y=4.71946 Z=0
    g16: GeomPoint X=94.7 Y=3 Z=0
    g17-g23: Circle x7 (B-spline internal-alignment scaffolding for g24; pole/knot coordinates omitted)
    g24: BSplineCurve PolesCount=7 KnotsCount=5 Degree=3 IsPeriodic=0
    g25-g29: GeomPoint x5 (B-spline internal-alignment scaffolding for g24; pole/knot coordinates omitted)
    g30: ArcOfCircle CenterX=98 CenterY=19 CenterZ=0 NormalX=0 NormalY=0 NormalZ=1 AngleXU=0 Radius=15.7 StartAngle=5.81226 EndAngle=6.28319
    g31: LineSegment StartX=110.7 StartY=19 StartZ=0 EndX=113.7 EndY=19 EndZ=0
  constraints (41):
    c: Horizontal(g0)
    c: Coincident(g1,g0)
    c: Block(g1)
    c: Horizontal(g2)
    c: Distance(g2) = 3
    c: Coincident(g3,g2)
    c: Vertical(g3)
    c: Coincident(g3,g0)
    c: Block(g4)
    c: Block(g2)
    c: Coincident(g5,g2)
    c: Coincident(g5,g4)
    c: Vertical(g5)
    c: Coincident(g6,g1)
    c: Block(g6)
    c: Coincident(g7,g4)
    c: Horizontal(g7)
    c: Block(g0)
    c: Block(g7)
    c: Block(g3)
    c: Coincident(g13,g6)
    c: Weight(g8) = 1
    c: Equal(g8, g9-g12) x4
    c: Coincident(g13,g7)
    c: InternalAlignment(g8-g12 -> g13) x5
    c: InternalAlignment(g14,g13)
    c: InternalAlignment(g15,g13)
    c: InternalAlignment(g16,g13)
    c: Block(g13)
    c: Weight(g17) = 1
    c: Equal(g17, g18-g23) x6
    c: Coincident(g24,g1)
    c: InternalAlignment(g17-g23 -> g24) x7
    c: InternalAlignment(g25-g29 -> g24) x5
    c: Block(g24)
    c: Coincident(g30,g24)
    c: Coincident(g31,g6)
    c: Coincident(g31,g30)
    c: Horizontal(g31)
    c: Block(g31)
    c: Block(g30)
FEATURE [Part::Extrusion] Extrude062  label="bottom014"
  Base = -> Sketch071
  Dir = (0,0,1)
  DirMode = 2
  FaceMakerClass = Part::FaceMakerBullseye
  LengthFwd = 71.4
  LengthRev = 0
  Placement = pos=(0,0,0.3) rot=(0,0,1;0rad)
  Solid = true
  Symmetric = false
FEATURE [Part::Fillet] Fillet054
  Base = -> Extrude062
  Edges = 1 edges r=2.4: [Edge17]
FEATURE [Part::Fillet] Fillet055  label="bottom015"
  Base = -> Fillet054
  Edges = 1 edges r=2.4: [Edge36]
FEATURE [Part::Cylinder] Cylinder055
  Angle = 360
  AttacherType = Attacher::AttachEngine3D
  Height = 10
  Placement = pos=(0,0,36.15) rot=(0,0,1;0rad)
  Radius = 4
FEATURE [Part::MultiFuse] Fusion131  label="removeToCreateHoleForPlugHousing002"
  Placement = pos=(70,19,36.15) rot=(0,1,0;1.5708rad)
  Shapes = -> [Cylinder054,Cylinder055]
FEATURE [Part::Cut] Cut056  label="Bottom001"
  Base = -> Fillet055
  Placement = pos=(9,0,0) rot=(0,0,1;0rad)
  Tool = -> Fusion131
FEATURE [Part::Cut] Cut057
  Base = -> Cut055
  Tool = -> Cut056
FEATURE [Sketcher::SketchObject] Sketch072  label="topSketch021"
  FullyConstrained = true
  sketch-geometry (4):
    g0: ArcOfCircle CenterX=105 CenterY=19 CenterZ=0 NormalX=0 NormalY=0 NormalZ=1 AngleXU=0 Radius=20.6155 StartAngle=5.54125 EndAngle=6.28319
    g1: ArcOfCircle CenterX=105 CenterY=19 CenterZ=0 NormalX=0 NormalY=0 NormalZ=1 AngleXU=0 Radius=13 StartAngle=5.54125 EndAngle=6.28319
    g2: LineSegment StartX=118 StartY=19 StartZ=0 EndX=125.616 EndY=19 EndZ=0
    g3: LineSegment StartX=114.583 StartY=10.2157 StartZ=0 EndX=120.197 EndY=5.06982 EndZ=0
  constraints (7):
    c: Block(g0)
    c: Block(g1)
    c: Coincident(g2,g1)
    c: Coincident(g2,g0)
    c: Horizontal(g2)
    c: Coincident(g3,g1)
    c: Coincident(g3,g0)
FEATURE [Part::Extrusion] Extrude063  label="bottomPlugHousingBit003"
  Base = -> Sketch072
  Dir = (0,0,1)
  DirMode = 2
  FaceMakerClass = Part::FaceMakerBullseye
  LengthFwd = 72
  LengthRev = 0
  Solid = true
  Symmetric = false
FEATURE [Part::Cylinder] Cylinder056
  Angle = 360
  AttacherType = Attacher::AttachEngine3D
  Height = 20
  Placement = pos=(0,0,36.15) rot=(0,0,1;0rad)
  Radius = 14.3
FEATURE [Part::Cylinder] Cylinder057
  Angle = 360
  AttacherType = Attacher::AttachEngine3D
  Height = 10
  Placement = pos=(0,0,36.15) rot=(0,0,1;0rad)
  Radius = 4
FEATURE [Part::Box] Box034  label="removeToCreteHoleForPlugHousing047"
  AttacherType = Attacher::AttachEngine3D
  Height = 28.6
  Length = 20
  Placement = pos=(106.15,0,21.7) rot=(0,0,1;0rad)
  Width = 19
FEATURE [Part::Cylinder] Cylinder058
  Angle = 360
  AttacherType = Attacher::AttachEngine3D
  Height = 20
  Placement = pos=(0,0,36.15) rot=(0,0,1;0rad)
  Radius = 14.3
FEATURE [Part::Cylinder] Cylinder059
  Angle = 360
  AttacherType = Attacher::AttachEngine3D
  Height = 10
  Placement = pos=(0,0,36.15) rot=(0,0,1;0rad)
  Radius = 4
FEATURE [Part::MultiFuse] Fusion134  label="removeToCreteHoleForPlugHousing046"
  Placement = pos=(70,19,36) rot=(0,1,0;1.5708rad)
  Shapes = -> [Cylinder058,Cylinder059]
FEATURE [Part::Cylinder] Cylinder060
  Angle = 360
  AttacherType = Attacher::AttachEngine3D
  Height = 20
  Placement = pos=(0,0,36.15) rot=(0,0,1;0rad)
  Radius = 14
FEATURE [Part::Cylinder] Cylinder061
  Angle = 360
  AttacherType = Attacher::AttachEngine3D
  Height = 10
  Placement = pos=(0,0,36.15) rot=(0,0,1;0rad)
  Radius = 4
FEATURE [Part::MultiFuse] Fusion135  label="removeToCreteHoleForPlugHousing048"
  Placement = pos=(70,19,36) rot=(0,1,0;1.5708rad)
  Shapes = -> [Cylinder060,Cylinder061]
FEATURE [Part::Box] Box035  label="removeToCreteHoleForPlugHousing049"
  AttacherType = Attacher::AttachEngine3D
  Height = 28.6
  Length = 20
  Placement = pos=(106.15,0,21.7) rot=(0,0,1;0rad)
  Width = 19
FEATURE [Part::MultiFuse] Fusion133  label="removeToCreteHoleForPlugHousing045"
  Placement = pos=(0,0,-28.3) rot=(0,0,1;0rad)
  Shapes = -> [Box035,Fusion134]
FEATURE [Part::MultiFuse] Fusion138  label="removeToCreteHoleForPlugHousing051"
  Placement = pos=(70,19,36) rot=(0,1,0;1.5708rad)
  Shapes = -> [Cylinder056,Cylinder057]
FEATURE [Part::MultiFuse] Fusion137  label="removeToCreteHoleForPlugHousing050"
  Placement = pos=(0,0,28.3) rot=(0,0,1;0rad)
  Shapes = -> [Box034,Fusion138]
FEATURE [Part::MultiFuse] Fusion132  label="removeToCreatePlugHousingBottomBit002"
  Shapes = -> [Fusion133,Fusion137]
FEATURE [Part::MultiFuse] Fusion136  label="removeToCreatePlugHousingBottomBit003"
  Shapes = -> [Fusion135,Fusion132]
FEATURE [Part::Cut] Cut058  label="bottomPlugHousingBit002"
  Base = -> Extrude063
  Placement = pos=(-0.09,0,0) rot=(0,0,1;0rad)
  Tool = -> Fusion136
FEATURE [Sketcher::SketchObject] Sketch073  label="bottomSketch003"
  FullyConstrained = true
  sketch-geometry (45):
    g0: LineSegment StartX=6.29999 StartY=8 StartZ=0 EndX=3.29999 EndY=8 EndZ=0
    g1: LineSegment StartX=3.29999 StartY=8 StartZ=0 EndX=3.29999 EndY=-6.03275e-07 EndZ=0
    g2: ArcOfCircle CenterX=8.29999 CenterY=5 CenterZ=0 NormalX=0 NormalY=0 NormalZ=1 AngleXU=0 Radius=2 StartAngle=3.14159 EndAngle=4.71239
    g3: LineSegment StartX=6.29999 StartY=8 StartZ=0 EndX=6.29999 EndY=5 EndZ=0
    g4: ArcOfCircle CenterX=105 CenterY=19 CenterZ=0 NormalX=0 NormalY=0 NormalZ=1 AngleXU=0 Radius=12.7 StartAngle=4.71239 EndAngle=5.94289
    g5-g11: Circle x7 (B-spline internal-alignment scaffolding for g12; pole/knot coordinates omitted)
    g12: BSplineCurve PolesCount=7 KnotsCount=5 Degree=3 IsPeriodic=0
    g13-g17: GeomPoint x5 (B-spline internal-alignment scaffolding for g12; pole/knot coordinates omitted)
    g18: ArcOfCircle CenterX=105 CenterY=19 CenterZ=0 NormalX=0 NormalY=0 NormalZ=1 AngleXU=0 Radius=15.7 StartAngle=5.81226 EndAngle=6.28319
    g19: BSplineCurve PolesCount=5 KnotsCount=3 Degree=3 IsPeriodic=0
    g20: LineSegment StartX=8.29999 StartY=3 StartZ=0 EndX=101.7 EndY=3 EndZ=0
    g21: LineSegment StartX=3.29999 StartY=-6.03275e-07 StartZ=0 EndX=105 EndY=-6.03275e-07 EndZ=0
    g22: LineSegment StartX=120.974 StartY=8.71251 StartZ=0 EndX=122.332 EndY=7.83778 EndZ=0
    g23: LineSegment StartX=105 StartY=-6.03274e-07 StartZ=0 EndX=113 EndY=-6.03274e-07 EndZ=0
    g24: ArcOfCircle CenterX=105 CenterY=19 CenterZ=0 NormalX=0 NormalY=0 NormalZ=1 AngleXU=0 Radius=20.6155 StartAngle=5.11091 EndAngle=5.71103
    g25: ArcOfCircle CenterX=117.7 CenterY=19 CenterZ=0 NormalX=0 NormalY=0 NormalZ=1 AngleXU=0 Radius=3 StartAngle=1.2e-15 EndAngle=2.10468
    g26: Circle CenterX=116.345 CenterY=16.3232 CenterZ=0 NormalX=0 NormalY=0 NormalZ=1 AngleXU=0 Radius=1
    g27: Circle CenterX=117.24 CenterY=15.7584 CenterZ=0 NormalX=0 NormalY=0 NormalZ=1 AngleXU=0 Radius=1
    g28: Circle CenterX=116.972 CenterY=14.7612 CenterZ=0 NormalX=0 NormalY=0 NormalZ=1 AngleXU=0 Radius=1
    g29: BSplineCurve PolesCount=3 KnotsCount=2 Degree=2 IsPeriodic=0
    g30: GeomPoint X=116.345 Y=16.3232 Z=0
    g31: GeomPoint X=116.972 Y=14.7612 Z=0
    g32: Circle CenterX=115.828 CenterY=17.157 CenterZ=0 NormalX=0 NormalY=0 NormalZ=1 AngleXU=0 Radius=1
    g33: Circle CenterX=115.841 CenterY=16.639 CenterZ=0 NormalX=0 NormalY=0 NormalZ=1 AngleXU=0 Radius=1
    g34: Circle CenterX=116.345 CenterY=16.3232 CenterZ=0 NormalX=0 NormalY=0 NormalZ=1 AngleXU=0 Radius=1
    g35: BSplineCurve PolesCount=3 KnotsCount=2 Degree=2 IsPeriodic=0
    g36: GeomPoint X=115.828 Y=17.157 Z=0
    g37: GeomPoint X=116.345 Y=16.3232 Z=0
    g38: LineSegment StartX=115.828 StartY=17.157 StartZ=0 EndX=115.828 EndY=20.8307 EndZ=0
    g39: Circle CenterX=115.828 CenterY=20.8307 CenterZ=0 NormalX=0 NormalY=0 NormalZ=1 AngleXU=0 Radius=1
    g40: Circle CenterX=115.831 CenterY=21.3396 CenterZ=0 NormalX=0 NormalY=0 NormalZ=1 AngleXU=0 Radius=1
    g41: Circle CenterX=116.173 CenterY=21.5825 CenterZ=0 NormalX=0 NormalY=0 NormalZ=1 AngleXU=0 Radius=1
    g42: BSplineCurve PolesCount=3 KnotsCount=2 Degree=2 IsPeriodic=0
    g43: GeomPoint X=115.828 Y=20.8307 Z=0
    g44: GeomPoint X=116.173 Y=21.5825 Z=0
  constraints (70):
    c: Horizontal(g0)
    c: Distance(g0) = 3
    c: Coincident(g1,g0)
    c: Vertical(g1)
    c: Block(g2)
    c: Block(g0)
    c: Coincident(g3,g0)
    c: Coincident(g3,g2)
    c: Vertical(g3)
    c: Block(g1)
    c: Block(g4)
    c: Coincident(g19,g4)
    c: Block(g19)
    c: Equal(g5, g6-g11) x6
    c: InternalAlignment(g5-g11 -> g12) x7
    c: InternalAlignment(g13-g17 -> g12) x5
    c: Block(g12)
    c: Coincident(g18,g12)
    c: Block(g18)
    c: Coincident(g20,g2)
    c: Coincident(g20,g19)
    c: Horizontal(g20)
    c: Distance(g20) = 93.4
    c: Coincident(g21,g1)
    c: Horizontal(g21)
    c: Distance(g21) = 101.7
    c: Horizontal(g23)
    c: Distance(g23) = 8
    c: Coincident(g24,g23)
    c: Block(g23)
    c: Coincident(g22,g24)
    c: Block(g24)
    c: Block(g22)
    c: Distance(g22) = 1.61553
    c: Coincident(g25,g18)
    c: Block(g25)
    c: Weight(g26) = 1
    c: Equal(g26,g27)
    c: Equal(g26,g28)
    c: Coincident(g29,g4)
    c: InternalAlignment(g26,g29)
    c: InternalAlignment(g27,g29)
    c: InternalAlignment(g28,g29)
    c: InternalAlignment(g30,g29)
    c: InternalAlignment(g31,g29)
    c: Block(g29)
    c: Weight(g32) = 1
    c: Equal(g32,g33)
    c: Equal(g32,g34)
    c: Coincident(g35,g29)
    c: InternalAlignment(g32,g35)
    c: InternalAlignment(g33,g35)
    c: InternalAlignment(g34,g35)
    c: InternalAlignment(g36,g35)
    c: InternalAlignment(g37,g35)
    c: Block(g35)
    c: Coincident(g38,g35)
    c: Vertical(g38)
    c: Block(g38)
    c: Coincident(g42,g38)
    c: Weight(g39) = 1
    c: Equal(g39,g40)
    c: Equal(g39,g41)
    c: Coincident(g42,g25)
    c: InternalAlignment(g39,g42)
    c: InternalAlignment(g40,g42)
    c: InternalAlignment(g41,g42)
    c: InternalAlignment(g43,g42)
    c: InternalAlignment(g44,g42)
    c: Block(g42)
FEATURE [Part::Extrusion] Extrude064  label="bottom016"
  Base = -> Sketch073
  Dir = (0,0,1)
  DirMode = 2
  FaceMakerClass = Part::FaceMakerBullseye
  LengthFwd = 71.4
  LengthRev = 0
  Placement = pos=(0,0,0.3) rot=(0,0,1;0rad)
  Solid = true
  Symmetric = false
FEATURE [Part::Revolution] Revolve157  label="removeToCreateScrewAndThreadedInsertHole063"
  Angle = 360
  Axis = (0,1,0)
  Base = (0,0,0)
  FaceMakerClass = Part::FaceMakerBullseye
  Placement = pos=(12.5,0,10) rot=(0,0,1;0rad)
  Solid = false
  Source = -> Face141
  Symmetric = false
FEATURE [Sketcher::SketchObject] Sketch074
  FullyConstrained = true
  Placement = pos=(117,19,0) rot=(0.57735,0.57735,0.57735;2.0944rad)
  sketch-geometry (48):
    g0: LineSegment StartX=-49.19 StartY=69.25 StartZ=0 EndX=-49.19 EndY=66.25 EndZ=0
    g1: LineSegment StartX=-49.19 StartY=63.5 StartZ=0 EndX=-49.19 EndY=60.5 EndZ=0
    g2: LineSegment StartX=-49.19 StartY=57.75 StartZ=0 EndX=-49.19 EndY=54.75 EndZ=0
    g3: LineSegment StartX=-49.19 StartY=52 StartZ=0 EndX=-49.19 EndY=49 EndZ=0
    g4: LineSegment StartX=-49.19 StartY=46.25 StartZ=0 EndX=-49.19 EndY=43.25 EndZ=0
    g5: LineSegment StartX=-49.19 StartY=40.5 StartZ=0 EndX=-49.19 EndY=37.5 EndZ=0
    g6: LineSegment StartX=-49.19 StartY=34.5 StartZ=0 EndX=-49.19 EndY=31.5 EndZ=0
    g7: LineSegment StartX=-49.19 StartY=28.75 StartZ=0 EndX=-49.19 EndY=25.75 EndZ=0
    g8: LineSegment StartX=-49.19 StartY=23 StartZ=0 EndX=-49.19 EndY=20 EndZ=0
    g9: LineSegment StartX=-49.19 StartY=17.25 StartZ=0 EndX=-49.19 EndY=14.25 EndZ=0
    g10: LineSegment StartX=-49.19 StartY=11.5 StartZ=0 EndX=-49.19 EndY=8.5 EndZ=0
    g11: LineSegment StartX=-49.19 StartY=5.75 StartZ=0 EndX=-49.19 EndY=2.75 EndZ=0
    g12: ArcOfCircle CenterX=-1.5 CenterY=67.75 CenterZ=0 NormalX=0 NormalY=0 NormalZ=1 AngleXU=0 Radius=1.5 StartAngle=4.71239 EndAngle=7.85398
    g13: ArcOfCircle CenterX=-1.5 CenterY=62 CenterZ=0 NormalX=0 NormalY=0 NormalZ=1 AngleXU=0 Radius=1.5 StartAngle=4.71239 EndAngle=7.85398
    g14: ArcOfCircle CenterX=-1.5 CenterY=56.25 CenterZ=0 NormalX=0 NormalY=0 NormalZ=1 AngleXU=0 Radius=1.5 StartAngle=4.71239 EndAngle=7.85398
    g15: ArcOfCircle CenterX=-11.49 CenterY=50.5 CenterZ=0 NormalX=0 NormalY=0 NormalZ=1 AngleXU=0 Radius=1.5 StartAngle=4.71239 EndAngle=7.85398
    g16: ArcOfCircle CenterX=-16.28 CenterY=44.75 CenterZ=0 NormalX=0 NormalY=0 NormalZ=1 AngleXU=0 Radius=1.5 StartAngle=4.71239 EndAngle=7.85398
    g17: ArcOfCircle CenterX=-18.2337 CenterY=39 CenterZ=0 NormalX=0 NormalY=0 NormalZ=1 AngleXU=0 Radius=1.5 StartAngle=4.71485 EndAngle=7.85398
    g18: ArcOfCircle CenterX=-16.2837 CenterY=27.25 CenterZ=0 NormalX=0 NormalY=0 NormalZ=1 AngleXU=0 Radius=1.5 StartAngle=4.71485 EndAngle=7.85398
    g19: ArcOfCircle CenterX=-18.2337 CenterY=33 CenterZ=0 NormalX=0 NormalY=0 NormalZ=1 AngleXU=0 Radius=1.5 StartAngle=4.71485 EndAngle=7.85398
    g20: ArcOfCircle CenterX=-11.49 CenterY=21.5 CenterZ=0 NormalX=0 NormalY=0 NormalZ=1 AngleXU=0 Radius=1.5 StartAngle=4.71239 EndAngle=7.85398
    g21: ArcOfCircle CenterX=-1.5 CenterY=4.25 CenterZ=0 NormalX=0 NormalY=0 NormalZ=1 AngleXU=0 Radius=1.5 StartAngle=4.71239 EndAngle=7.85398
    g22: ArcOfCircle CenterX=-1.5 CenterY=10 CenterZ=0 NormalX=0 NormalY=0 NormalZ=1 AngleXU=0 Radius=1.5 StartAngle=4.71239 EndAngle=7.85398
    g23: ArcOfCircle CenterX=-1.5 CenterY=15.75 CenterZ=0 NormalX=0 NormalY=0 NormalZ=1 AngleXU=0 Radius=1.5 StartAngle=4.71239 EndAngle=7.85398
    g24: LineSegment StartX=-49.19 StartY=69.25 StartZ=0 EndX=-1.5 EndY=69.25 EndZ=0
    g25: LineSegment StartX=-49.19 StartY=66.25 StartZ=0 EndX=-1.5 EndY=66.25 EndZ=0
    g26: LineSegment StartX=-49.19 StartY=63.5 StartZ=0 EndX=-1.5 EndY=63.5 EndZ=0
    g27: LineSegment StartX=-49.19 StartY=60.5 StartZ=0 EndX=-1.5 EndY=60.5 EndZ=0
    g28: LineSegment StartX=-49.19 StartY=57.75 StartZ=0 EndX=-1.5 EndY=57.75 EndZ=0
    g29: LineSegment StartX=-49.19 StartY=54.75 StartZ=0 EndX=-1.5 EndY=54.75 EndZ=0
    g30: LineSegment StartX=-49.19 StartY=52 StartZ=0 EndX=-11.49 EndY=52 EndZ=0
    g31: LineSegment StartX=-49.19 StartY=49 StartZ=0 EndX=-11.49 EndY=49 EndZ=0
    g32: LineSegment StartX=-49.19 StartY=46.25 StartZ=0 EndX=-16.28 EndY=46.25 EndZ=0
    g33: LineSegment StartX=-49.19 StartY=43.25 StartZ=0 EndX=-16.28 EndY=43.25 EndZ=0
    g34: LineSegment StartX=-49.19 StartY=40.5 StartZ=0 EndX=-18.2337 EndY=40.5 EndZ=0
    g35: LineSegment StartX=-49.19 StartY=37.5 StartZ=0 EndX=-18.23 EndY=37.5 EndZ=0
    g36: LineSegment StartX=-49.19 StartY=34.5 StartZ=0 EndX=-18.2337 EndY=34.5 EndZ=0
    g37: LineSegment StartX=-49.19 StartY=31.5 StartZ=0 EndX=-18.23 EndY=31.5 EndZ=0
    g38: LineSegment StartX=-49.19 StartY=28.75 StartZ=0 EndX=-16.2837 EndY=28.75 EndZ=0
    g39: LineSegment StartX=-49.19 StartY=25.75 StartZ=0 EndX=-16.28 EndY=25.75 EndZ=0
    g40: LineSegment StartX=-49.19 StartY=23 StartZ=0 EndX=-11.49 EndY=23 EndZ=0
    g41: LineSegment StartX=-49.19 StartY=20 StartZ=0 EndX=-11.49 EndY=20 EndZ=0
    g42: LineSegment StartX=-49.19 StartY=17.25 StartZ=0 EndX=-1.5 EndY=17.25 EndZ=0
    g43: LineSegment StartX=-49.19 StartY=14.25 StartZ=0 EndX=-1.5 EndY=14.25 EndZ=0
    g44: LineSegment StartX=-49.19 StartY=11.5 StartZ=0 EndX=-1.5 EndY=11.5 EndZ=0
    g45: LineSegment StartX=-49.19 StartY=8.5 StartZ=0 EndX=-1.5 EndY=8.5 EndZ=0
    g46: LineSegment StartX=-49.19 StartY=5.75 StartZ=0 EndX=-1.5 EndY=5.75 EndZ=0
    g47: LineSegment StartX=-49.19 StartY=2.75 StartZ=0 EndX=-1.5 EndY=2.75 EndZ=0
  constraints (120):
    c: Vertical(g0)
    c: Distance(g0) = 3
    c: Block(g0)
    c: Vertical(g1)
    c: Distance(g1) = 3
    c: Vertical(g2)
    c: Equal(g0,g2) = 3
    c: Block(g2)
    c: Vertical(g3)
    c: Equal(g1,g3) = 3
    c: Vertical(g4)
    c: Equal(g0,g4) = 3
    c: Block(g4)
    c: Vertical(g5)
    c: Equal(g1,g5) = 3
    c: Vertical(g6)
    c: Equal(g0,g6) = 3
    c: Block(g6)
    c: Vertical(g7)
    c: Equal(g1,g7) = 3
    c: Vertical(g8)
    c: Equal(g0,g8) = 3
    c: Block(g8)
    c: Vertical(g9)
    c: Equal(g1,g9) = 3
    c: Vertical(g10)
    c: Equal(g0,g10) = 3
    c: Block(g10)
    c: Vertical(g11)
    c: Equal(g1,g11) = 3
    c: Block(g12)
    c: Block(g13)
    c: Block(g14)
    c: Block(g15)
    c: Block(g16)
    c: Block(g17)
    c: Block(g18)
    c: Block(g19)
    c: Block(g20)
    c: Block(g21)
    c: Block(g22)
    c: Block(g23)
    c: Block(g11)
    c: Block(g9)
    c: Block(g7)
    c: Block(g5)
    c: Block(g3)
    c: Block(g1)
    c: Coincident(g24,g0)
    c: Coincident(g24,g12)
    c: Horizontal(g24)
    c: Coincident(g25,g0)
    c: Coincident(g25,g12)
    c: Horizontal(g25)
    c: Coincident(g26,g1)
    c: Coincident(g26,g13)
    c: Horizontal(g26)
    c: Coincident(g27,g1)
    c: Coincident(g27,g13)
    c: Horizontal(g27)
    c: Coincident(g28,g2)
    c: Coincident(g28,g14)
    c: Horizontal(g28)
    c: Coincident(g29,g2)
    c: Coincident(g29,g14)
    c: Horizontal(g29)
    c: Coincident(g30,g3)
    c: Coincident(g30,g15)
    c: Horizontal(g30)
    c: Coincident(g31,g3)
    c: Coincident(g31,g15)
    c: Horizontal(g31)
    c: Coincident(g32,g4)
    c: Coincident(g32,g16)
    c: Horizontal(g32)
    c: Coincident(g33,g4)
    c: Coincident(g33,g16)
    c: Horizontal(g33)
    c: Coincident(g34,g5)
    c: Coincident(g34,g17)
    c: Horizontal(g34)
    c: Coincident(g35,g5)
    c: Coincident(g35,g17)
    c: Horizontal(g35)
    c: Coincident(g36,g6)
    c: Coincident(g36,g19)
    c: Horizontal(g36)
    c: Coincident(g37,g6)
    c: Coincident(g37,g19)
    c: Horizontal(g37)
    c: Coincident(g38,g7)
    c: Coincident(g38,g18)
    c: Horizontal(g38)
    c: Coincident(g39,g7)
    c: Coincident(g39,g18)
    c: Horizontal(g39)
    c: Coincident(g40,g8)
    c: Coincident(g40,g20)
    c: Horizontal(g40)
    c: Coincident(g41,g8)
    c: Coincident(g41,g20)
    c: Horizontal(g41)
    c: Coincident(g42,g9)
    c: Coincident(g42,g23)
    c: Horizontal(g42)
    c: Coincident(g43,g9)
    c: Coincident(g43,g23)
    c: Horizontal(g43)
    c: Coincident(g44,g10)
    c: Coincident(g44,g22)
    c: Horizontal(g44)
    c: Coincident(g45,g10)
    c: Coincident(g45,g22)
    c: Horizontal(g45)
    c: Coincident(g46,g11)
    c: Coincident(g46,g21)
    c: Horizontal(g46)
    c: Coincident(g47,g11)
    c: Coincident(g47,g21)
    c: Horizontal(g47)
FEATURE [Part::Extrusion] Extrude065
  Base = -> Sketch074
  Dir = (1,0,0)
  DirMode = 2
  FaceMakerClass = Part::FaceMakerBullseye
  LengthFwd = 23
  LengthRev = 0
  Placement = pos=(-19,0,0) rot=(0,0,1;0rad)
  Solid = true
  Symmetric = false
FEATURE [Part::Fillet] Fillet056  label="removeToCreateVentalationHoles003"
  Base = -> Extrude065
  Edges = <same value as first occurrence — deduplicated (x6 in doc)>
  Placement = pos=(7,0.02,0) rot=(0,0,1;0rad)
FEATURE [Part::Revolution] Revolve158  label="removeToCreateScrewAndThreadedInsertHole065"
  Angle = 360
  Axis = (0,1,0)
  Base = (0,0,0)
  FaceMakerClass = Part::FaceMakerBullseye
  Placement = pos=(12.5,0,62) rot=(0,0,1;0rad)
  Solid = false
  Source = -> Face146
  Symmetric = false
FEATURE [Part::Revolution] Revolve159  label="removeToCreateScrewAndThreadedInsertHole066"
  Angle = 360
  Axis = (0,1,0)
  Base = (0,0,0)
  FaceMakerClass = Part::FaceMakerBullseye
  Placement = pos=(89.5,0,68.5) rot=(0,0,1;0rad)
  Solid = false
  Source = -> Face143
  Symmetric = false
FEATURE [Part::Revolution] Revolve160  label="removeToCreateScrewAndThreadedInsertHole067"
  Angle = 360
  Axis = (0,1,0)
  Base = (0,0,0)
  FaceMakerClass = Part::FaceMakerBullseye
  Placement = pos=(89.5,0,3.5) rot=(0,0,1;0rad)
  Solid = false
  Source = -> Face142
  Symmetric = false
FEATURE [Part::Revolution] Revolve161  label="removeToCreateScrewAndThreadedInsertHole068"
  Angle = 360
  Axis = (0,1,0)
  Base = (0,0,0)
  FaceMakerClass = Part::FaceMakerBullseye
  Placement = pos=(109.5,4.7,3.5) rot=(0,0,1;0rad)
  Solid = false
  Source = -> Face145
  Symmetric = false
FEATURE [Part::Revolution] Revolve162  label="removeToCreateScrewAndThreadedInsertHole069"
  Angle = 360
  Axis = (0,1,0)
  Base = (0,0,0)
  FaceMakerClass = Part::FaceMakerBullseye
  Placement = pos=(109.5,4.7,68.5) rot=(0,0,1;0rad)
  Solid = false
  Source = -> Face144
  Symmetric = false
FEATURE [Part::MultiFuse] Fusion141  label="removeToCreateScrewAndThreadedInsertHole064"
  Shapes = -> [Revolve162,Revolve161,Revolve160,Revolve159,Revolve158,Revolve157]
FEATURE [Part::Cylinder] Cylinder062
  Angle = 360
  AttacherType = Attacher::AttachEngine3D
  Height = 20
  Placement = pos=(0,0,36.15) rot=(0,0,1;0rad)
  Radius = 14
FEATURE [Part::Cylinder] Cylinder063
  Angle = 360
  AttacherType = Attacher::AttachEngine3D
  Height = 10
  Placement = pos=(0,0,36.15) rot=(0,0,1;0rad)
  Radius = 4
FEATURE [Part::MultiFuse] Fusion139  label="removeToCreteHoleForPlugHousing052"
  Placement = pos=(70,19,36) rot=(0,1,0;1.5708rad)
  Shapes = -> [Cylinder062,Cylinder063]
FEATURE [Part::Cut] Cut060  label="bottom017"
  Base = -> Extrude064
  Tool = -> Fusion139
FEATURE [Part::Cut] Cut061  label="bottom019"
  Base = -> Cut060
  Tool = -> Fusion141
FEATURE [Part::MultiFuse] Fusion140  label="bottom018"
  Shapes = -> [Cut061,Cut058]
FEATURE [Part::Cut] Cut059  label="bottom020"
  Base = -> Fusion140
  Tool = -> Fillet056
FEATURE [Part::Box] Box036  label="Cube021"
  AttacherType = Attacher::AttachEngine3D
  Height = 80
  Length = 26
  Placement = pos=(0,-1,-5) rot=(0,0,1;0rad)
  Width = 11
FEATURE [Part::Cut] Cut062  label="removeFromBottom002"
  Base = -> Cut057
  Tool = -> Box036
FEATURE [Part::Cut] Cut063
  Base = -> Cut059
  Tool = -> Cut062
FEATURE [Part::Cut] Cut064  label="pcbStands"
  Base = -> Fusion095
  Tool = -> Fusion127
FEATURE [Sketcher::SketchObject] Sketch075  label="topSketch022"
  FullyConstrained = true
  sketch-geometry (6):
    g0: LineSegment StartX=19 StartY=38 StartZ=0 EndX=117 EndY=38 EndZ=0
    g1: ArcOfCircle CenterX=19 CenterY=19 CenterZ=0 NormalX=0 NormalY=0 NormalZ=1 AngleXU=0 Radius=19 StartAngle=1.5708 EndAngle=3.14159
    g2: LineSegment StartX=117 StartY=38 StartZ=0 EndX=117 EndY=19 EndZ=0
    g3: LineSegment StartX=98 StartY=1.0161e-12 StartZ=0 EndX=5.22862e-06 EndY=1.0161e-12 EndZ=0
    g4: LineSegment StartX=5.22862e-06 StartY=19 StartZ=0 EndX=5.22862e-06 EndY=1.0161e-12 EndZ=0
    g5: ArcOfCircle CenterX=98 CenterY=19 CenterZ=0 NormalX=0 NormalY=0 NormalZ=1 AngleXU=0 Radius=19 StartAngle=4.71239 EndAngle=6.28319
  constraints (16):
    c: Horizontal(g0)
    c: Distance(g0) = 98
    c: Coincident(g1,g0)
    c: Block(g1)
    c: Coincident(g2,g0)
    c: Vertical(g2)
    c: Distance(g2) = 19
    c: Horizontal(g3)
    c: Coincident(g4,g1)
    c: Vertical(g4)
    c: Coincident(g3,g4)
    c: Block(g3)
    c: Coincident(g5,g2)
    c: Coincident(g5,g3)
    c: Block(g0)
    c: Block(g5)
FEATURE [Part::Extrusion] Extrude067  label="sideB003"
  Base = -> Sketch075
  Dir = (0,0,1)
  DirMode = 2
  FaceMakerClass = Part::FaceMakerBullseye
  LengthFwd = 3
  LengthRev = 0
  Placement = pos=(0,0,71.7) rot=(0,0,1;0rad)
  Solid = true
  Symmetric = false
FEATURE [Sketcher::SketchObject] Sketch076  label="topSketch023"
  FullyConstrained = true
  sketch-geometry (6):
    g0: LineSegment StartX=19 StartY=38 StartZ=0 EndX=117 EndY=38 EndZ=0
    g1: ArcOfCircle CenterX=19 CenterY=19 CenterZ=0 NormalX=0 NormalY=0 NormalZ=1 AngleXU=0 Radius=19 StartAngle=1.5708 EndAngle=3.14159
    g2: LineSegment StartX=117 StartY=38 StartZ=0 EndX=117 EndY=19 EndZ=0
    g3: LineSegment StartX=98 StartY=1.0161e-12 StartZ=0 EndX=5.22862e-06 EndY=1.0161e-12 EndZ=0
    g4: LineSegment StartX=5.22862e-06 StartY=19 StartZ=0 EndX=5.22862e-06 EndY=1.0161e-12 EndZ=0
    g5: ArcOfCircle CenterX=98 CenterY=19 CenterZ=0 NormalX=0 NormalY=0 NormalZ=1 AngleXU=0 Radius=19 StartAngle=4.71239 EndAngle=6.28319
  constraints (16):
    c: Horizontal(g0)
    c: Distance(g0) = 98
    c: Coincident(g1,g0)
    c: Block(g1)
    c: Coincident(g2,g0)
    c: Vertical(g2)
    c: Distance(g2) = 19
    c: Horizontal(g3)
    c: Coincident(g4,g1)
    c: Vertical(g4)
    c: Coincident(g3,g4)
    c: Block(g3)
    c: Coincident(g5,g2)
    c: Coincident(g5,g3)
    c: Block(g0)
    c: Block(g5)
FEATURE [Part::Extrusion] Extrude066  label="sideA003"
  Base = -> Sketch076
  Dir = (0,0,1)
  DirMode = 2
  FaceMakerClass = Part::FaceMakerBullseye
  LengthFwd = 3
  LengthRev = 0
  Placement = pos=(0,0,-2.7) rot=(0,0,1;0rad)
  Solid = true
  Symmetric = false
FEATURE [Part::MultiFuse] Fusion142  label="removeFromBottom003"
  Placement = pos=(2,0,0) rot=(0,0,1;0rad)
  Shapes = -> [Extrude066,Extrude067]
FEATURE [Part::Cut] Cut065  label="screwRetainers002"
  Base = -> Fusion096
  Tool = -> Fusion142
FEATURE [Sketcher::SketchObject] Sketch077
  FullyConstrained = true
  Placement = pos=(117,19,0) rot=(0.57735,0.57735,0.57735;2.0944rad)
  sketch-geometry (8):
    g0: LineSegment StartX=-49.19 StartY=63.5 StartZ=0 EndX=-49.19 EndY=60.5 EndZ=0
    g1: LineSegment StartX=-49.19 StartY=11.5 StartZ=0 EndX=-49.19 EndY=8.5 EndZ=0
    g2: ArcOfCircle CenterX=-1.5 CenterY=62 CenterZ=0 NormalX=0 NormalY=0 NormalZ=1 AngleXU=0 Radius=1.5 StartAngle=4.71239 EndAngle=7.85398
    g3: ArcOfCircle CenterX=-1.5 CenterY=10 CenterZ=0 NormalX=0 NormalY=0 NormalZ=1 AngleXU=0 Radius=1.5 StartAngle=4.71239 EndAngle=7.85398
    g4: LineSegment StartX=-49.19 StartY=63.5 StartZ=0 EndX=-1.5 EndY=63.5 EndZ=0
    g5: LineSegment StartX=-49.19 StartY=60.5 StartZ=0 EndX=-1.5 EndY=60.5 EndZ=0
    g6: LineSegment StartX=-49.19 StartY=11.5 StartZ=0 EndX=-1.5 EndY=11.5 EndZ=0
    g7: LineSegment StartX=-49.19 StartY=8.5 StartZ=0 EndX=-1.5 EndY=8.5 EndZ=0
  constraints (19):
    c: Vertical(g0)
    c: Distance(g0) = 3
    c: Vertical(g1)
    c: Block(g1)
    c: Block(g2)
    c: Block(g3)
    c: Block(g0)
    c: Coincident(g4,g0)
    c: Coincident(g4,g2)
    c: Horizontal(g4)
    c: Coincident(g5,g0)
    c: Coincident(g5,g2)
    c: Horizontal(g5)
    c: Coincident(g6,g1)
    c: Coincident(g6,g3)
    c: Horizontal(g6)
    c: Coincident(g7,g1)
    c: Coincident(g7,g3)
    c: Horizontal(g7)
FEATURE [Part::Extrusion] Extrude068
  Base = -> Sketch077
  Dir = (1,0,0)
  DirMode = 2
  FaceMakerClass = Part::FaceMakerBullseye
  LengthFwd = 10
  LengthRev = 0
  Solid = true
  Symmetric = false
FEATURE [Part::Fillet] Fillet057  label="removeFromtMoreFrontCaseScrewRetainers002"
  Base = -> Extrude068
  Edges = 4 edges r=1.49: [Edge6,Edge11,Edge18,Edge23]
  Placement = pos=(-12,0,0) rot=(0,0,1;0rad)
FEATURE [Sketcher::SketchObject] Sketch078
  FullyConstrained = true
  Placement = pos=(117,19,0) rot=(0.57735,0.57735,0.57735;2.0944rad)
  sketch-geometry (8):
    g0: LineSegment StartX=-49.19 StartY=69.25 StartZ=0 EndX=-49.19 EndY=66.25 EndZ=0
    g1: LineSegment StartX=-49.19 StartY=5.75 StartZ=0 EndX=-49.19 EndY=2.75 EndZ=0
    g2: ArcOfCircle CenterX=-1.5 CenterY=67.75 CenterZ=0 NormalX=0 NormalY=0 NormalZ=1 AngleXU=0 Radius=1.5 StartAngle=4.71239 EndAngle=7.85398
    g3: ArcOfCircle CenterX=-1.5 CenterY=4.25 CenterZ=0 NormalX=0 NormalY=0 NormalZ=1 AngleXU=0 Radius=1.5 StartAngle=4.71239 EndAngle=7.85398
    g4: LineSegment StartX=-49.19 StartY=69.25 StartZ=0 EndX=-1.5 EndY=69.25 EndZ=0
    g5: LineSegment StartX=-49.19 StartY=66.25 StartZ=0 EndX=-1.5 EndY=66.25 EndZ=0
    g6: LineSegment StartX=-49.19 StartY=5.75 StartZ=0 EndX=-1.5 EndY=5.75 EndZ=0
    g7: LineSegment StartX=-49.19 StartY=2.75 StartZ=0 EndX=-1.5 EndY=2.75 EndZ=0
  constraints (19):
    c: Vertical(g0)
    c: Distance(g0) = 3
    c: Block(g0)
    c: Vertical(g1)
    c: Block(g2)
    c: Block(g3)
    c: Block(g1)
    c: Coincident(g4,g0)
    c: Coincident(g4,g2)
    c: Horizontal(g4)
    c: Coincident(g5,g0)
    c: Coincident(g5,g2)
    c: Horizontal(g5)
    c: Coincident(g6,g1)
    c: Coincident(g6,g3)
    c: Horizontal(g6)
    c: Coincident(g7,g1)
    c: Coincident(g7,g3)
    c: Horizontal(g7)
FEATURE [Part::Extrusion] Extrude069
  Base = -> Sketch078
  Dir = (1,0,0)
  DirMode = 2
  FaceMakerClass = Part::FaceMakerBullseye
  LengthFwd = 10
  LengthRev = 0
  Solid = true
  Symmetric = false
FEATURE [Part::Fillet] Fillet058  label="removeFromtMoreFrontCaseScrewRetainers003"
  Base = -> Extrude069
  Edges = 4 edges r=1.49: [Edge6,Edge11,Edge18,Edge23]
  Placement = pos=(-4,0,0) rot=(0,0,1;0rad)
FEATURE [Part::Cut] Cut066
  Base = -> Cut065
  Tool = -> Fillet058
FEATURE [Part::Cut] Cut067  label="screwPillars"
  Base = -> Cut066
  Tool = -> Fillet057
FEATURE [Part::MultiFuse] Fusion143  label="bottom021"
  Shapes = -> [Cut031,Cut063]
FEATURE [Part::Cylinder] Cylinder
  Angle = 360
  AttacherType = Attacher::AttachEngine3D
  Height = 10
  Placement = pos=(20.65,12,4.68) rot=(1,0,0;1.5708rad)
  Radius = 2
FEATURE [Part::Cylinder] Cylinder064
  Angle = 360
  AttacherType = Attacher::AttachEngine3D
  Height = 10
  Placement = pos=(20.65,12,67.38) rot=(1,0,0;1.5708rad)
  Radius = 2
FEATURE [Part::Cylinder] Cylinder065
  Angle = 360
  AttacherType = Attacher::AttachEngine3D
  Height = 10
  Placement = pos=(77.15,12,67.38) rot=(1,0,0;1.5708rad)
  Radius = 2
FEATURE [Part::Cylinder] Cylinder066
  Angle = 360
  AttacherType = Attacher::AttachEngine3D
  Height = 10
  Placement = pos=(77.15,12,4.68) rot=(1,0,0;1.5708rad)
  Radius = 2
FEATURE [Part::MultiFuse] Fusion144  label="removeFromThreadedInsertHousing"
  Shapes = -> [Cylinder065,Cylinder064,Cylinder,Cylinder066]
FEATURE [Part::Cut] Cut068  label="pcbStands001"
  Base = -> Cut064
  Tool = -> Fusion144
FEATURE [Part::MultiFuse] Fusion145
  Shapes = -> [Cut068,Fusion143]
FEATURE [Part::MultiFuse] Fusion146
  Shapes = -> [Fusion145]
FEATURE [Part::MultiFuse] Fusion147  label="bottom022"
  Shapes = -> [Cut067,Fusion146]
FEATURE [Part::MultiFuse] Fusion148  label="casePillars005"
  Shapes = -> [Cut047,Fusion092]
FEATURE [Part::MultiFuse] Fusion149  label="bottom023"
  Shapes = -> [Fusion124,Fusion113,Fusion147]
FEATURE [Part::MultiFuse] Fusion150  label="topBits"
  Shapes = -> [Cut025,Fusion148,Cut030,Fillet034]
FEATURE [Part::Feature] Face149 .. Face152  x4 (patterned run collapsed; names and placements below)
  shape: bbox 3.2 x 1.5 x 2e-07 mm, 1 faces, 0 solids (baked)
FEATURE [Part::Feature] Face153
  shape: bbox 3.6 x 3.2 x 2e-07 mm, 1 faces, 0 solids (baked)
FEATURE [Part::Feature] Face154
  shape: bbox 3.6 x 3.2 x 2e-07 mm, 1 faces, 0 solids (baked)
FEATURE [Sketcher::SketchObject] Sketch079  label="topSketch024"
  FullyConstrained = true
  sketch-geometry (6):
    g0: LineSegment StartX=19 StartY=38 StartZ=0 EndX=117 EndY=38 EndZ=0
    g1: ArcOfCircle CenterX=19 CenterY=19 CenterZ=0 NormalX=0 NormalY=0 NormalZ=1 AngleXU=0 Radius=19 StartAngle=1.5708 EndAngle=3.14159
    g2: LineSegment StartX=117 StartY=38 StartZ=0 EndX=117 EndY=19 EndZ=0
    g3: LineSegment StartX=98 StartY=1.0161e-12 StartZ=0 EndX=5.22862e-06 EndY=1.0161e-12 EndZ=0
    g4: LineSegment StartX=5.22862e-06 StartY=19 StartZ=0 EndX=5.22862e-06 EndY=1.0161e-12 EndZ=0
    g5: ArcOfCircle CenterX=98 CenterY=19 CenterZ=0 NormalX=0 NormalY=0 NormalZ=1 AngleXU=0 Radius=19 StartAngle=4.71239 EndAngle=6.28319
  constraints (16):
    c: Horizontal(g0)
    c: Distance(g0) = 98
    c: Coincident(g1,g0)
    c: Block(g1)
    c: Coincident(g2,g0)
    c: Vertical(g2)
    c: Distance(g2) = 19
    c: Horizontal(g3)
    c: Coincident(g4,g1)
    c: Vertical(g4)
    c: Coincident(g3,g4)
    c: Block(g3)
    c: Coincident(g5,g2)
    c: Coincident(g5,g3)
    c: Block(g0)
    c: Block(g5)
FEATURE [Sketcher::SketchObject] Sketch080  label="topSketch025"
  FullyConstrained = true
  sketch-geometry (6):
    g0: LineSegment StartX=19 StartY=38 StartZ=0 EndX=117 EndY=38 EndZ=0
    g1: ArcOfCircle CenterX=19 CenterY=19 CenterZ=0 NormalX=0 NormalY=0 NormalZ=1 AngleXU=0 Radius=19 StartAngle=1.5708 EndAngle=3.14159
    g2: LineSegment StartX=117 StartY=38 StartZ=0 EndX=117 EndY=19 EndZ=0
    g3: LineSegment StartX=98 StartY=1.0161e-12 StartZ=0 EndX=5.22862e-06 EndY=1.0161e-12 EndZ=0
    g4: LineSegment StartX=5.22862e-06 StartY=19 StartZ=0 EndX=5.22862e-06 EndY=1.0161e-12 EndZ=0
    g5: ArcOfCircle CenterX=98 CenterY=19 CenterZ=0 NormalX=0 NormalY=0 NormalZ=1 AngleXU=0 Radius=19 StartAngle=4.71239 EndAngle=6.28319
  constraints (16):
    c: Horizontal(g0)
    c: Distance(g0) = 98
    c: Coincident(g1,g0)
    c: Block(g1)
    c: Coincident(g2,g0)
    c: Vertical(g2)
    c: Distance(g2) = 19
    c: Horizontal(g3)
    c: Coincident(g4,g1)
    c: Vertical(g4)
    c: Coincident(g3,g4)
    c: Block(g3)
    c: Coincident(g5,g2)
    c: Coincident(g5,g3)
    c: Block(g0)
    c: Block(g5)
FEATURE [Part::Extrusion] Extrude070  label="sideA004"
  Base = -> Sketch080
  Dir = (0,0,1)
  DirMode = 2
  FaceMakerClass = Part::FaceMakerBullseye
  LengthFwd = 3
  LengthRev = 0
  Placement = pos=(0,0,-2.7) rot=(0,0,1;0rad)
  Solid = true
  Symmetric = false
FEATURE [Sketcher::SketchObject] Sketch081
  FullyConstrained = true
  Placement = pos=(117,19,0) rot=(0.57735,0.57735,0.57735;2.0944rad)
  sketch-geometry (8):
    g0: LineSegment StartX=-49.19 StartY=63.5 StartZ=0 EndX=-49.19 EndY=60.5 EndZ=0
    g1: LineSegment StartX=-49.19 StartY=11.5 StartZ=0 EndX=-49.19 EndY=8.5 EndZ=0
    g2: ArcOfCircle CenterX=-1.5 CenterY=62 CenterZ=0 NormalX=0 NormalY=0 NormalZ=1 AngleXU=0 Radius=1.5 StartAngle=4.71239 EndAngle=7.85398
    g3: ArcOfCircle CenterX=-1.5 CenterY=10 CenterZ=0 NormalX=0 NormalY=0 NormalZ=1 AngleXU=0 Radius=1.5 StartAngle=4.71239 EndAngle=7.85398
    g4: LineSegment StartX=-49.19 StartY=63.5 StartZ=0 EndX=-1.5 EndY=63.5 EndZ=0
    g5: LineSegment StartX=-49.19 StartY=60.5 StartZ=0 EndX=-1.5 EndY=60.5 EndZ=0
    g6: LineSegment StartX=-49.19 StartY=11.5 StartZ=0 EndX=-1.5 EndY=11.5 EndZ=0
    g7: LineSegment StartX=-49.19 StartY=8.5 StartZ=0 EndX=-1.5 EndY=8.5 EndZ=0
  constraints (19):
    c: Vertical(g0)
    c: Distance(g0) = 3
    c: Vertical(g1)
    c: Block(g1)
    c: Block(g2)
    c: Block(g3)
    c: Block(g0)
    c: Coincident(g4,g0)
    c: Coincident(g4,g2)
    c: Horizontal(g4)
    c: Coincident(g5,g0)
    c: Coincident(g5,g2)
    c: Horizontal(g5)
    c: Coincident(g6,g1)
    c: Coincident(g6,g3)
    c: Horizontal(g6)
    c: Coincident(g7,g1)
    c: Coincident(g7,g3)
    c: Horizontal(g7)
FEATURE [Part::Extrusion] Extrude071  label="sideB004"
  Base = -> Sketch079
  Dir = (0,0,1)
  DirMode = 2
  FaceMakerClass = Part::FaceMakerBullseye
  LengthFwd = 3
  LengthRev = 0
  Placement = pos=(0,0,71.7) rot=(0,0,1;0rad)
  Solid = true
  Symmetric = false
FEATURE [Part::MultiFuse] Fusion152  label="removeFromBottom004"
  Placement = pos=(2,0,0) rot=(0,0,1;0rad)
  Shapes = -> [Extrude070,Extrude071]
FEATURE [Part::Extrusion] Extrude072
  Base = -> Sketch081
  Dir = (1,0,0)
  DirMode = 2
  FaceMakerClass = Part::FaceMakerBullseye
  LengthFwd = 10
  LengthRev = 0
  Solid = true
  Symmetric = false
FEATURE [Part::Fillet] Fillet059  label="removeFromtMoreFrontCaseScrewRetainers004"
  Base = -> Extrude072
  Edges = 4 edges r=1.49: [Edge6,Edge11,Edge18,Edge23]
  Placement = pos=(-12,0,0) rot=(0,0,1;0rad)
FEATURE [Sketcher::SketchObject] Sketch082
  FullyConstrained = true
  Placement = pos=(117,19,0) rot=(0.57735,0.57735,0.57735;2.0944rad)
  sketch-geometry (8):
    g0: LineSegment StartX=-49.19 StartY=69.25 StartZ=0 EndX=-49.19 EndY=66.25 EndZ=0
    g1: LineSegment StartX=-49.19 StartY=5.75 StartZ=0 EndX=-49.19 EndY=2.75 EndZ=0
    g2: ArcOfCircle CenterX=-1.5 CenterY=67.75 CenterZ=0 NormalX=0 NormalY=0 NormalZ=1 AngleXU=0 Radius=1.5 StartAngle=4.71239 EndAngle=7.85398
    g3: ArcOfCircle CenterX=-1.5 CenterY=4.25 CenterZ=0 NormalX=0 NormalY=0 NormalZ=1 AngleXU=0 Radius=1.5 StartAngle=4.71239 EndAngle=7.85398
    g4: LineSegment StartX=-49.19 StartY=69.25 StartZ=0 EndX=-1.5 EndY=69.25 EndZ=0
    g5: LineSegment StartX=-49.19 StartY=66.25 StartZ=0 EndX=-1.5 EndY=66.25 EndZ=0
    g6: LineSegment StartX=-49.19 StartY=5.75 StartZ=0 EndX=-1.5 EndY=5.75 EndZ=0
    g7: LineSegment StartX=-49.19 StartY=2.75 StartZ=0 EndX=-1.5 EndY=2.75 EndZ=0
  constraints (19):
    c: Vertical(g0)
    c: Distance(g0) = 3
    c: Block(g0)
    c: Vertical(g1)
    c: Block(g2)
    c: Block(g3)
    c: Block(g1)
    c: Coincident(g4,g0)
    c: Coincident(g4,g2)
    c: Horizontal(g4)
    c: Coincident(g5,g0)
    c: Coincident(g5,g2)
    c: Horizontal(g5)
    c: Coincident(g6,g1)
    c: Coincident(g6,g3)
    c: Horizontal(g6)
    c: Coincident(g7,g1)
    c: Coincident(g7,g3)
    c: Horizontal(g7)
FEATURE [Part::Extrusion] Extrude073
  Base = -> Sketch082
  Dir = (1,0,0)
  DirMode = 2
  FaceMakerClass = Part::FaceMakerBullseye
  LengthFwd = 10
  LengthRev = 0
  Solid = true
  Symmetric = false
FEATURE [Part::Fillet] Fillet060  label="removeFromtMoreFrontCaseScrewRetainers005"
  Base = -> Extrude073
  Edges = 4 edges r=1.49: [Edge6,Edge11,Edge18,Edge23]
  Placement = pos=(-4,0,0) rot=(0,0,1;0rad)
FEATURE [Part::Revolution] Revolve163  label="backCaseScrewRetainer004"
  Angle = 360
  Axis = (0,1,0)
  Base = (0,0,0)
  FaceMakerClass = Part::FaceMakerBullseye
  Placement = pos=(12.5,3,62) rot=(0,0,1;0rad)
  Solid = false
  Source = -> Face149
  Symmetric = false
FEATURE [Part::Revolution] Revolve164  label="frontCaseScrewRetainer006"
  Angle = 360
  Axis = (0,1,0)
  Base = (0,0,0)
  FaceMakerClass = Part::FaceMakerBullseye
  Placement = pos=(89.5,3,68.5) rot=(0,0,1;0rad)
  Solid = false
  Source = -> Face151
  Symmetric = false
FEATURE [Part::Revolution] Revolve165  label="frontCaseScrewRetainer007"
  Angle = 360
  Axis = (0,1,0)
  Base = (0,0,0)
  FaceMakerClass = Part::FaceMakerBullseye
  Placement = pos=(89.5,3,3.5) rot=(0,0,1;0rad)
  Solid = false
  Source = -> Face152
  Symmetric = false
FEATURE [Part::Revolution] Revolve166  label="backCaseScrewRetainer005"
  Angle = 360
  Axis = (0,1,0)
  Base = (0,0,0)
  FaceMakerClass = Part::FaceMakerBullseye
  Placement = pos=(12.5,3,10) rot=(0,0,1;0rad)
  Solid = false
  Source = -> Face150
  Symmetric = false
FEATURE [Part::Revolution] Revolve167  label="moreFrontCaseScrewRetainer006"
  Angle = 360
  Axis = (0,1,0)
  Base = (0,0,0)
  FaceMakerClass = Part::FaceMakerBullseye
  Placement = pos=(109.5,4.5,68.5) rot=(0,0,1;0rad)
  Solid = false
  Source = -> Face153
  Symmetric = false
FEATURE [Part::Revolution] Revolve168  label="moreFrontCaseScrewRetainer007"
  Angle = 360
  Axis = (0,1,0)
  Base = (0,0,0)
  FaceMakerClass = Part::FaceMakerBullseye
  Placement = pos=(109.5,4.5,3.5) rot=(0,0,1;0rad)
  Solid = false
  Source = -> Face154
  Symmetric = false
FEATURE [Part::MultiFuse] Fusion151  label="screwRetainers003"
  Shapes = -> [Revolve168,Revolve167,Revolve166,Revolve165,Revolve164,Revolve163]
FEATURE [Part::Cut] Cut069  label="screwRetainers004"
  Base = -> Fusion151
  Tool = -> Fusion152
FEATURE [Part::Cut] Cut070
  Base = -> Cut069
  Tool = -> Fillet060
FEATURE [Part::Cut] Cut071  label="screwPillars001"
  Base = -> Cut070
  Tool = -> Fillet059
FEATURE [Part::MultiFuse] Fusion153  label="bottom024"
  Shapes = -> [Fusion149,Cut071]
FEATURE [Part::Cylinder] Cylinder067
  Angle = 360
  AttacherType = Attacher::AttachEngine3D
  Height = 10
  Placement = pos=(20.65,12,4.68) rot=(1,0,0;1.5708rad)
  Radius = 2
FEATURE [Part::Cylinder] Cylinder068
  Angle = 360
  AttacherType = Attacher::AttachEngine3D
  Height = 10
  Placement = pos=(20.65,12,67.38) rot=(1,0,0;1.5708rad)
  Radius = 2
FEATURE [Part::Cylinder] Cylinder069
  Angle = 360
  AttacherType = Attacher::AttachEngine3D
  Height = 10
  Placement = pos=(77.15,12,67.38) rot=(1,0,0;1.5708rad)
  Radius = 2
FEATURE [Part::Cylinder] Cylinder070
  Angle = 360
  AttacherType = Attacher::AttachEngine3D
  Height = 10
  Placement = pos=(77.15,12,4.68) rot=(1,0,0;1.5708rad)
  Radius = 2
FEATURE [Part::MultiFuse] Fusion154  label="removeFromThreadedInsertHousing001"
  Shapes = -> [Cylinder069,Cylinder068,Cylinder067,Cylinder070]
FEATURE [Part::Cut] Cut072  label="bottom025"
  Base = -> Fusion153
  Tool = -> Fusion154
FEATURE [Image::ImagePlane] ImagePlane
  XSize = 339
  YSize = 72
FEATURE [Sketcher::SketchObject] Sketch083
  FullyConstrained = true
  MapMode = 5
  Support = -> [XY_Plane]
  sketch-geometry (338):
    g0: LineSegment StartX=-151.619 StartY=28.8932 StartZ=0 EndX=-140.819 EndY=28.8932 EndZ=0
    g1: LineSegment StartX=-151.619 StartY=24.0313 StartZ=0 EndX=-151.619 EndY=28.8932 EndZ=0
    g2: LineSegment StartX=-140.819 StartY=17.7713 StartZ=0 EndX=-151.619 EndY=17.7713 EndZ=0
    g3: LineSegment StartX=-151.619 StartY=17.7713 StartZ=0 EndX=-151.619 EndY=22.6313 EndZ=0
    g4: LineSegment StartX=-151.619 StartY=22.6313 StartZ=0 EndX=-145.128 EndY=22.6313 EndZ=0
    g5: LineSegment StartX=-145.128 StartY=24.0313 StartZ=0 EndX=-140.819 EndY=28.8932 EndZ=0
    g6: LineSegment StartX=-145.128 StartY=22.6313 StartZ=0 EndX=-140.819 EndY=17.7713 EndZ=0
    g7: ArcOfCircle CenterX=-155.157 CenterY=23.3323 CenterZ=0 NormalX=0 NormalY=0 NormalZ=1 AngleXU=0 Radius=6.92354 StartAngle=1.03434 EndAngle=5.24885
    g8: ArcOfCircle CenterX=-155.157 CenterY=23.3323 CenterZ=0 NormalX=0 NormalY=0 NormalZ=1 AngleXU=0 Radius=12.6269 StartAngle=1.28675 EndAngle=4.99643
    g9: LineSegment StartX=-151.619 StartY=35.4532 StartZ=0 EndX=-151.619 EndY=29.2832 EndZ=0
    g10: LineSegment StartX=-151.619 StartY=17.3813 StartZ=0 EndX=-151.619 EndY=11.2113 EndZ=0
    g11-g21: Circle x11 (B-spline internal-alignment scaffolding for g22; pole/knot coordinates omitted)
    g22: BSplineCurve PolesCount=11 KnotsCount=9 Degree=3 IsPeriodic=0
    g23-g31: GeomPoint x9 (B-spline internal-alignment scaffolding for g22; pole/knot coordinates omitted)
    g32-g49: Circle x18 (B-spline internal-alignment scaffolding for g50; pole/knot coordinates omitted)
    g50: BSplineCurve PolesCount=18 KnotsCount=16 Degree=3 IsPeriodic=0
    g51-g66: GeomPoint x16 (B-spline internal-alignment scaffolding for g50; pole/knot coordinates omitted)
    g67: LineSegment StartX=-117.124 StartY=30.093 StartZ=0 EndX=-117.603 EndY=26.5272 EndZ=0
    g68: LineSegment StartX=-117.603 StartY=17.8472 StartZ=0 EndX=-117.124 EndY=14.2659 EndZ=0
    g69: Ellipse CenterX=-109.671 CenterY=20.025 CenterZ=0 NormalX=0 NormalY=0 NormalZ=1 MajorRadius=3.34798 MinorRadius=2.71052 AngleXU=-1.56793
    g70: GeomPoint X=-109.666 Y=18.0598 Z=0
    g71: GeomPoint X=-109.677 Y=21.9902 Z=0
    g72: Ellipse CenterX=-109.671 CenterY=20.0123 CenterZ=0 NormalX=0 NormalY=0 NormalZ=1 MajorRadius=6.93002 MinorRadius=6.36273 AngleXU=-3.13976
    g73: GeomPoint X=-112.417 Y=20.0073 Z=0
    g74: GeomPoint X=-106.925 Y=20.0173 Z=0
    g75: Ellipse CenterX=-51.7682 CenterY=20.1463 CenterZ=0 NormalX=0 NormalY=0 NormalZ=1 MajorRadius=3.19279 MinorRadius=2.71052 AngleXU=-1.52774
    g76: GeomPoint X=-51.6955 Y=18.4606 Z=0
    g77: GeomPoint X=-51.8408 Y=21.832 Z=0
    g78: GeomPoint X=-54.5142 Y=20.1413 Z=0
    g79: GeomPoint X=-49.0221 Y=20.1513 Z=0
    g80: Ellipse CenterX=-51.7682 CenterY=20.1463 CenterZ=0 NormalX=0 NormalY=0 NormalZ=1 MajorRadius=6.93002 MinorRadius=6.36273 AngleXU=-3.13976
    g81: Ellipse CenterX=-22.8436 CenterY=20.1783 CenterZ=0 NormalX=0 NormalY=0 NormalZ=1 MajorRadius=3.31512 MinorRadius=2.71052 AngleXU=-1.60214
    g82: GeomPoint X=-22.9034 Y=18.2706 Z=0
    g83: GeomPoint X=-22.7838 Y=22.0861 Z=0
    g84: GeomPoint X=-25.5897 Y=20.1733 Z=0
    g85: GeomPoint X=-20.0976 Y=20.1833 Z=0
    g86: Ellipse CenterX=-22.8436 CenterY=20.1783 CenterZ=0 NormalX=0 NormalY=0 NormalZ=1 MajorRadius=6.93002 MinorRadius=6.36273 AngleXU=-3.13976
    g87: LineSegment StartX=-101.889 StartY=14.1107 StartZ=0 EndX=-97.7455 EndY=14.1107 EndZ=0
    g88: LineSegment StartX=-93.8155 StartY=14.1107 StartZ=0 EndX=-89.6755 EndY=14.1107 EndZ=0
    g89: LineSegment StartX=-85.7455 StartY=14.1107 StartZ=0 EndX=-81.6055 EndY=14.1107 EndZ=0
    g90: LineSegment StartX=-101.889 StartY=14.1107 StartZ=0 EndX=-101.889 EndY=25.9907 EndZ=0
    g91: LineSegment StartX=-101.889 StartY=25.9907 StartZ=0 EndX=-97.8594 EndY=25.9907 EndZ=0
    g92: LineSegment StartX=-97.8594 StartY=25.9907 StartZ=0 EndX=-97.8594 EndY=24.0907 EndZ=0
    g93: LineSegment StartX=-97.7455 StartY=14.1107 StartZ=0 EndX=-97.7455 EndY=19.9107 EndZ=0
    g94: LineSegment StartX=-89.6755 StartY=14.1107 StartZ=0 EndX=-89.6755 EndY=19.9107 EndZ=0
    g95: LineSegment StartX=-93.8155 StartY=14.1107 StartZ=0 EndX=-93.8155 EndY=21.0107 EndZ=0
    g96-g106: Circle x11 (B-spline internal-alignment scaffolding for g107; pole/knot coordinates omitted)
    g107: BSplineCurve PolesCount=11 KnotsCount=9 Degree=3 IsPeriodic=0
    g108-g116: GeomPoint x9 (B-spline internal-alignment scaffolding for g107; pole/knot coordinates omitted)
    g117: BSplineCurve PolesCount=11 KnotsCount=9 Degree=3 IsPeriodic=0
    g118-g125: Circle x8 (B-spline internal-alignment scaffolding for g126; pole/knot coordinates omitted)
    g126: BSplineCurve PolesCount=8 KnotsCount=6 Degree=3 IsPeriodic=0
    g127-g132: GeomPoint x6 (B-spline internal-alignment scaffolding for g126; pole/knot coordinates omitted)
    g133: BSplineCurve PolesCount=8 KnotsCount=6 Degree=3 IsPeriodic=0
    g134: LineSegment StartX=-85.7455 StartY=21.0107 StartZ=0 EndX=-85.7455 EndY=14.1107 EndZ=0
    g135: LineSegment StartX=-80.0879 StartY=14.1107 StartZ=0 EndX=-75.944 EndY=14.1107 EndZ=0
    g136: LineSegment StartX=-72.014 StartY=14.1107 StartZ=0 EndX=-67.874 EndY=14.1107 EndZ=0
    g137: LineSegment StartX=-63.944 StartY=14.1107 StartZ=0 EndX=-59.804 EndY=14.1107 EndZ=0
    g138: LineSegment StartX=-80.0879 StartY=14.1107 StartZ=0 EndX=-80.0879 EndY=25.9907 EndZ=0
    g139: LineSegment StartX=-80.0879 StartY=25.9907 StartZ=0 EndX=-76.0579 EndY=25.9907 EndZ=0
    g140: LineSegment StartX=-76.0579 StartY=25.9907 StartZ=0 EndX=-76.0579 EndY=24.0907 EndZ=0
    g141: LineSegment StartX=-75.944 StartY=14.1107 StartZ=0 EndX=-75.944 EndY=19.9107 EndZ=0
    g142: LineSegment StartX=-67.874 StartY=14.1107 StartZ=0 EndX=-67.874 EndY=19.9107 EndZ=0
    g143: LineSegment StartX=-72.014 StartY=14.1107 StartZ=0 EndX=-72.014 EndY=21.0107 EndZ=0
    g144-g148: Circle x5 (B-spline internal-alignment scaffolding for g149; pole/knot coordinates omitted)
    g149: BSplineCurve PolesCount=11 KnotsCount=9 Degree=3 IsPeriodic=0
    g150-g158: GeomPoint x9 (B-spline internal-alignment scaffolding for g149; pole/knot coordinates omitted)
    g159: BSplineCurve PolesCount=11 KnotsCount=9 Degree=3 IsPeriodic=0
    g160-g167: Circle x8 (B-spline internal-alignment scaffolding for g168; pole/knot coordinates omitted)
    g168: BSplineCurve PolesCount=8 KnotsCount=6 Degree=3 IsPeriodic=0
    g169-g174: GeomPoint x6 (B-spline internal-alignment scaffolding for g168; pole/knot coordinates omitted)
    g175: BSplineCurve PolesCount=8 KnotsCount=6 Degree=3 IsPeriodic=0
    g176: LineSegment StartX=-63.944 StartY=21.0107 StartZ=0 EndX=-63.944 EndY=14.1107 EndZ=0
    g177: LineSegment StartX=-59.804 StartY=14.1107 StartZ=0 EndX=-59.804 EndY=21.5868 EndZ=0
    g178: BSplineCurve PolesCount=4 KnotsCount=2 Degree=3 IsPeriodic=0
    g179: GeomPoint X=-59.804 Y=21.5868 Z=0
    g180: GeomPoint X=-60.2379 Y=24.0907 Z=0
    g181: LineSegment StartX=-81.6055 StartY=14.1107 StartZ=0 EndX=-81.6055 EndY=21.5868 EndZ=0
    g182: LineSegment StartX=-151.619 StartY=24.0313 StartZ=0 EndX=-145.128 EndY=24.0313 EndZ=0
    g183: Circle CenterX=-82.0394 CenterY=24.0907 CenterZ=0 NormalX=0 NormalY=0 NormalZ=1 AngleXU=0 Radius=1
    g184: Circle CenterX=-81.7131 CenterY=23.2736 CenterZ=0 NormalX=0 NormalY=0 NormalZ=1 AngleXU=0 Radius=1
    g185: Circle CenterX=-81.6055 CenterY=21.5868 CenterZ=0 NormalX=0 NormalY=0 NormalZ=1 AngleXU=0 Radius=1
    g186: BSplineCurve PolesCount=3 KnotsCount=2 Degree=2 IsPeriodic=0
    g187: GeomPoint X=-82.0394 Y=24.0907 Z=0
    g188: GeomPoint X=-81.6055 Y=21.5868 Z=0
    g189: Ellipse CenterX=-37.3522 CenterY=19.9515 CenterZ=0 NormalX=0 NormalY=0 NormalZ=1 MajorRadius=2.99755 MinorRadius=2.49 AngleXU=1.5708
    g190: GeomPoint X=-37.3522 Y=21.6203 Z=0
    g191: GeomPoint X=-37.3522 Y=18.2826 Z=0
    g192: ArcOfEllipse CenterX=-38.7647 CenterY=20.06 CenterZ=0 NormalX=0 NormalY=0 NormalZ=1 MajorRadius=6.30025 MinorRadius=5.3849 AngleXU=1.57276 StartAngle=5.50632 EndAngle=10.3035
    g193: GeomPoint X=-38.7711 Y=23.3304 Z=0
    g194: GeomPoint X=-38.7583 Y=16.7895 Z=0
    g195: LineSegment StartX=-34.6109 StartY=14.1107 StartZ=0 EndX=-30.8984 EndY=14.1107 EndZ=0
    g196: LineSegment StartX=-30.8984 StartY=14.1107 StartZ=0 EndX=-30.8984 EndY=31.1784 EndZ=0
    g197: LineSegment StartX=-30.8984 StartY=31.1784 StartZ=0 EndX=-34.9984 EndY=31.1784 EndZ=0
    g198: LineSegment StartX=-34.9984 StartY=24.5602 StartZ=0 EndX=-34.9984 EndY=31.1784 EndZ=0
    g199: LineSegment StartX=-34.6109 StartY=16.0476 StartZ=0 EndX=-34.6109 EndY=14.1107 EndZ=0
    g200: LineSegment StartX=-14.8781 StartY=14.1107 StartZ=0 EndX=-10.5106 EndY=14.1107 EndZ=0
    g201: LineSegment StartX=-14.8781 StartY=14.1107 StartZ=0 EndX=-14.8781 EndY=25.8504 EndZ=0
    g202: LineSegment StartX=-14.8781 StartY=25.8504 StartZ=0 EndX=-10.8534 EndY=25.8504 EndZ=0
    g203: LineSegment StartX=-10.8534 StartY=25.8504 StartZ=0 EndX=-10.8534 EndY=24.0923 EndZ=0
    g204: LineSegment StartX=-10.5106 StartY=14.1107 StartZ=0 EndX=-10.5106 EndY=19.7752 EndZ=0
    g205: LineSegment StartX=-5.96397 StartY=25.9304 StartZ=0 EndX=-5.96397 EndY=22.574 EndZ=0
    g206-g214: Circle x9 (B-spline internal-alignment scaffolding for g215; pole/knot coordinates omitted)
    g215: BSplineCurve PolesCount=9 KnotsCount=7 Degree=3 IsPeriodic=0
    g216-g222: GeomPoint x7 (B-spline internal-alignment scaffolding for g215; pole/knot coordinates omitted)
    g223-g232: Circle x10 (B-spline internal-alignment scaffolding for g233; pole/knot coordinates omitted)
    g233: BSplineCurve PolesCount=10 KnotsCount=8 Degree=3 IsPeriodic=0
    g234-g241: GeomPoint x8 (B-spline internal-alignment scaffolding for g233; pole/knot coordinates omitted)
    g242: LineSegment StartX=-1.58923 StartY=21.0696 StartZ=0 EndX=2.62034 EndY=21.0696 EndZ=0
    g243: LineSegment StartX=-1.55856 StartY=18.7342 StartZ=0 EndX=6.45946 EndY=18.7342 EndZ=0
    g244: LineSegment StartX=5.29231 StartY=17.386 StartZ=0 EndX=5.29231 EndY=14.3674 EndZ=0
    g245-g269: Circle x25 (B-spline internal-alignment scaffolding for g270; pole/knot coordinates omitted)
    g270: BSplineCurve PolesCount=25 KnotsCount=23 Degree=3 IsPeriodic=0
    g271-g293: GeomPoint x23 (B-spline internal-alignment scaffolding for g270; pole/knot coordinates omitted)
    g294-g304: Circle x11 (B-spline internal-alignment scaffolding for g305; pole/knot coordinates omitted)
    g305: BSplineCurve PolesCount=11 KnotsCount=9 Degree=3 IsPeriodic=0
    g306-g314: GeomPoint x9 (B-spline internal-alignment scaffolding for g305; pole/knot coordinates omitted)
    g315-g326: Circle x12 (B-spline internal-alignment scaffolding for g327; pole/knot coordinates omitted)
    g327: BSplineCurve PolesCount=12 KnotsCount=10 Degree=3 IsPeriodic=0
    g328-g337: GeomPoint x10 (B-spline internal-alignment scaffolding for g327; pole/knot coordinates omitted)
  constraints (252):
    c: Coincident(g1,g0)
    c: Horizontal(g0)
    c: Vertical(g1)
    c: Coincident(g2,g3)
    c: Coincident(g3,g4)
    c: Horizontal(g4)
    c: Horizontal(g2)
    c: Vertical(g3)
    c: Block(g1)
    c: Distance(g3) = 4.86
    c: Block(g4)
    c: Distance(g0) = 10.8
    c: Distance(g2) = 10.8
    c: Coincident(g5,g0)
    c: Coincident(g6,g4)
    c: Coincident(g6,g2)
    c: Block(g8)
    c: Block(g7)
    c: Coincident(g9,g8)
    c: Coincident(g9,g7)
    c: Vertical(g9)
    c: Coincident(g10,g7)
    c: Coincident(g10,g8)
    c: Vertical(g10)
    c: Weight(g11) = 1
    c: Equal(g11, g12-g21) x10
    c: InternalAlignment(g11-g21 -> g22) x11
    c: InternalAlignment(g23-g31 -> g22) x9
    c: Block(g22)
    c: Weight(g32) = 1
    c: Equal(g32, g33-g49) x17
    c: InternalAlignment(g32-g49 -> g50) x18
    c: InternalAlignment(g51-g66 -> g50) x16
    c: Block(g50)
    c: Coincident(g67,g50)
    c: Coincident(g67,g22)
    c: Coincident(g68,g22)
    c: Coincident(g68,g50)
    c: InternalAlignment(g70,g69)
    c: InternalAlignment(g71,g69)
    c: Block(g69)
    c: InternalAlignment(g73,g72)
    c: InternalAlignment(g74,g72)
    c: Block(g72)
    c: InternalAlignment(g76,g75)
    c: InternalAlignment(g77,g75)
    c: InternalAlignment(g78,g80)
    c: InternalAlignment(g79,g80)
    c: Block(g80)
    c: Coincident(g75,g80)
    c: Block(g75)
    c: InternalAlignment(g82,g81)
    c: InternalAlignment(g83,g81)
    c: InternalAlignment(g84,g86)
    c: InternalAlignment(g85,g86)
    c: Block(g86)
    c: Coincident(g81,g86)
    c: Block(g81)
    c: Horizontal(g87)
    c: Block(g87)
    c: Horizontal(g88)
    c: Distance(g88) = 4.14
    c: Horizontal(g89)
    c: Equal(g88,g89) = 4.14
    c: Block(g89)
    c: Block(g88)
    c: Coincident(g90,g87)
    c: Vertical(g90)
    c: Distance(g90) = 11.88
    c: Coincident(g91,g90)
    c: Horizontal(g91)
    c: Coincident(g92,g91)
    c: Vertical(g92)
    c: Distance(g91) = 4.03
    c: Distance(g92) = 1.9
    c: Coincident(g93,g87)
    c: Vertical(g93)
    c: Vertical(g94)
    c: Coincident(g94,g88)
    c: Distance(g93) = 5.8
    c: Distance(g94) = 5.8
    c: Vertical(g95)
    c: Coincident(g95,g88)
    c: Distance(g95) = 6.9
    c: Coincident(g107,g92)
    c: Weight(g96) = 1
    c: Equal(g96, g97-g106) x10
    c: InternalAlignment(g96-g106 -> g107) x11
    c: InternalAlignment(g108-g116 -> g107) x9
    c: Block(g107)
    c: Block(g117)
    c: Coincident(g126,g93)
    c: Weight(g118) = 1
    c: Equal(g118, g119-g125) x7
    c: Coincident(g126,g95)
    c: InternalAlignment(g118-g125 -> g126) x8
    c: InternalAlignment(g127-g132 -> g126) x6
    c: Coincident(g133,g94)
    c: Block(g126)
    c: Block(g133)
    c: Coincident(g134,g133)
    c: Coincident(g134,g89)
    c: Vertical(g134)
    c: Horizontal(g135)
    c: Block(g135)
    c: Horizontal(g136)
    c: Equal(g88,g136) = 4.14
    c: Horizontal(g137)
    c: Equal(g136,g137) = 4.14
    c: Block(g137)
    c: Block(g136)
    c: Coincident(g138,g135)
    c: Vertical(g138)
    c: Equal(g90,g138) = 11.88
    c: Coincident(g139,g138)
    c: Horizontal(g139)
    c: Coincident(g140,g139)
    c: Vertical(g140)
    c: Equal(g91,g139) = 4.03
    c: Equal(g92,g140) = 1.9
    c: Coincident(g141,g135)
    c: Vertical(g141)
    c: Vertical(g142)
    c: Coincident(g142,g136)
    c: Equal(g93,g141) = 5.8
    c: Equal(g94,g142) = 5.8
    c: Vertical(g143)
    c: Coincident(g143,g136)
    c: Equal(g95,g143) = 6.9
    c: Coincident(g149,g140)
    c: Equal(g96,g144) = 1
    c: Equal(g144, g145-g148) x4
    c: InternalAlignment(g144-g148 -> g149) x5
    c: InternalAlignment(g150-g158 -> g149) x9
    c: Block(g149)
    c: Block(g159)
    c: Coincident(g168,g141)
    c: Equal(g118,g160) = 1
    c: Equal(g160, g161-g167) x7
    c: Coincident(g168,g143)
    c: InternalAlignment(g160-g167 -> g168) x8
    c: InternalAlignment(g169-g174 -> g168) x6
    c: Coincident(g175,g142)
    c: Block(g168)
    c: Block(g175)
    c: Coincident(g176,g175)
    c: Coincident(g176,g137)
    c: Vertical(g176)
    c: Coincident(g177,g137)
    c: Vertical(g177)
    c: Coincident(g178,g177)
    c: Coincident(g178,g159)
    c: InternalAlignment(g179,g178)
    c: InternalAlignment(g180,g178)
    c: Block(g178)
    c: Vertical(g181)
    c: Coincident(g181,g89)
    c: Block(g5)
    c: Coincident(g182,g1)
    c: Coincident(g182,g5)
    c: Horizontal(g182)
    c: Coincident(g186,g117)
    c: Weight(g183) = 1
    c: Equal(g183,g184)
    c: Equal(g183,g185)
    c: Coincident(g186,g181)
    c: InternalAlignment(g183,g186)
    c: InternalAlignment(g184,g186)
    c: InternalAlignment(g185,g186)
    c: InternalAlignment(g187,g186)
    c: InternalAlignment(g188,g186)
    c: Block(g186)
    c: InternalAlignment(g190,g189)
    c: InternalAlignment(g191,g189)
    c: Block(g189)
    c: InternalAlignment(g193,g192)
    c: InternalAlignment(g194,g192)
    c: Block(g192)
    c: Horizontal(g195)
    c: Block(g195)
    c: Coincident(g196,g195)
    c: Vertical(g196)
    c: Block(g196)
    c: Distance(g195) = 3.71244
    c: Coincident(g197,g196)
    c: Horizontal(g197)
    c: Distance(g197) = 4.1
    c: Coincident(g198,g192)
    c: Coincident(g198,g197)
    c: Vertical(g198)
    c: Block(g198)
    c: Coincident(g199,g192)
    c: Coincident(g199,g195)
    c: Vertical(g199)
    c: Block(g199)
    c: Horizontal(g200)
    c: Block(g200)
    c: Coincident(g201,g200)
    c: Vertical(g201)
    c: Block(g201)
    c: Coincident(g202,g201)
    c: Horizontal(g202)
    c: Block(g202)
    c: Coincident(g203,g202)
    c: Vertical(g203)
    c: Block(g203)
    c: Coincident(g204,g200)
    c: Vertical(g204)
    c: Block(g204)
    c: Coincident(g215,g203)
    c: Weight(g206) = 1
    c: Equal(g206, g207-g214) x8
    c: Coincident(g215,g205)
    c: InternalAlignment(g206-g214 -> g215) x9
    c: InternalAlignment(g216-g222 -> g215) x7
    c: Coincident(g233,g204)
    c: Weight(g223) = 1
    c: Equal(g223, g224-g232) x9
    c: Coincident(g233,g205)
    c: InternalAlignment(g223-g232 -> g233) x10
    c: InternalAlignment(g234-g241 -> g233) x8
    c: Vertical(g205)
    c: Block(g205)
    c: Block(g215)
    c: Block(g233)
    c: Horizontal(g242)
    c: Horizontal(g243)
    c: Block(g242)
    c: Block(g243)
    c: Vertical(g244)
    c: Block(g244)
    c: Coincident(g270,g243)
    c: Weight(g245) = 1
    c: Equal(g245, g246-g269) x24
    c: Coincident(g270,g244)
    c: InternalAlignment(g245-g269 -> g270) x25
    c: InternalAlignment(g271-g293 -> g270) x23
    c: Coincident(g305,g242)
    c: Weight(g294) = 1
    c: Equal(g294, g295-g304) x10
    c: Coincident(g305,g242)
    c: InternalAlignment(g294-g304 -> g305) x11
    c: InternalAlignment(g306-g314 -> g305) x9
    c: Block(g305)
    c: Coincident(g327,g243)
    c: Weight(g315) = 1
    c: Equal(g315, g316-g326) x11
    c: Coincident(g327,g244)
    c: InternalAlignment(g315-g326 -> g327) x12
    c: InternalAlignment(g328-g337 -> g327) x10
    c: Block(g327)
    c: Block(g270)
FEATURE [PartDesign::Body] Body  label="CommodoreLogoAndText"
  Group = -> [Sketch083]
  Origin = -> Origin
FEATURE [Part::Extrusion] Extrude074  label="CommodoreLogoAndText001"
  Base = -> Sketch083
  Dir = (0,0,1)
  DirMode = 2
  FaceMakerClass = Part::FaceMakerBullseye
  LengthFwd = 10
  LengthRev = 0
  Solid = true
  Symmetric = false
FEATURE [Part::FeaturePython] Clone  label="CommodoreLogoAndTextScale"  # Draft clone (typed FeaturePython)
  AttacherType = Attacher::AttachEngine3D
  Fuse = false
  Objects = -> [Extrude074]
  Placement = pos=(111,5.37,0) rot=(0,0,1;0rad)
  Scale = (0.62,0.62,1)
